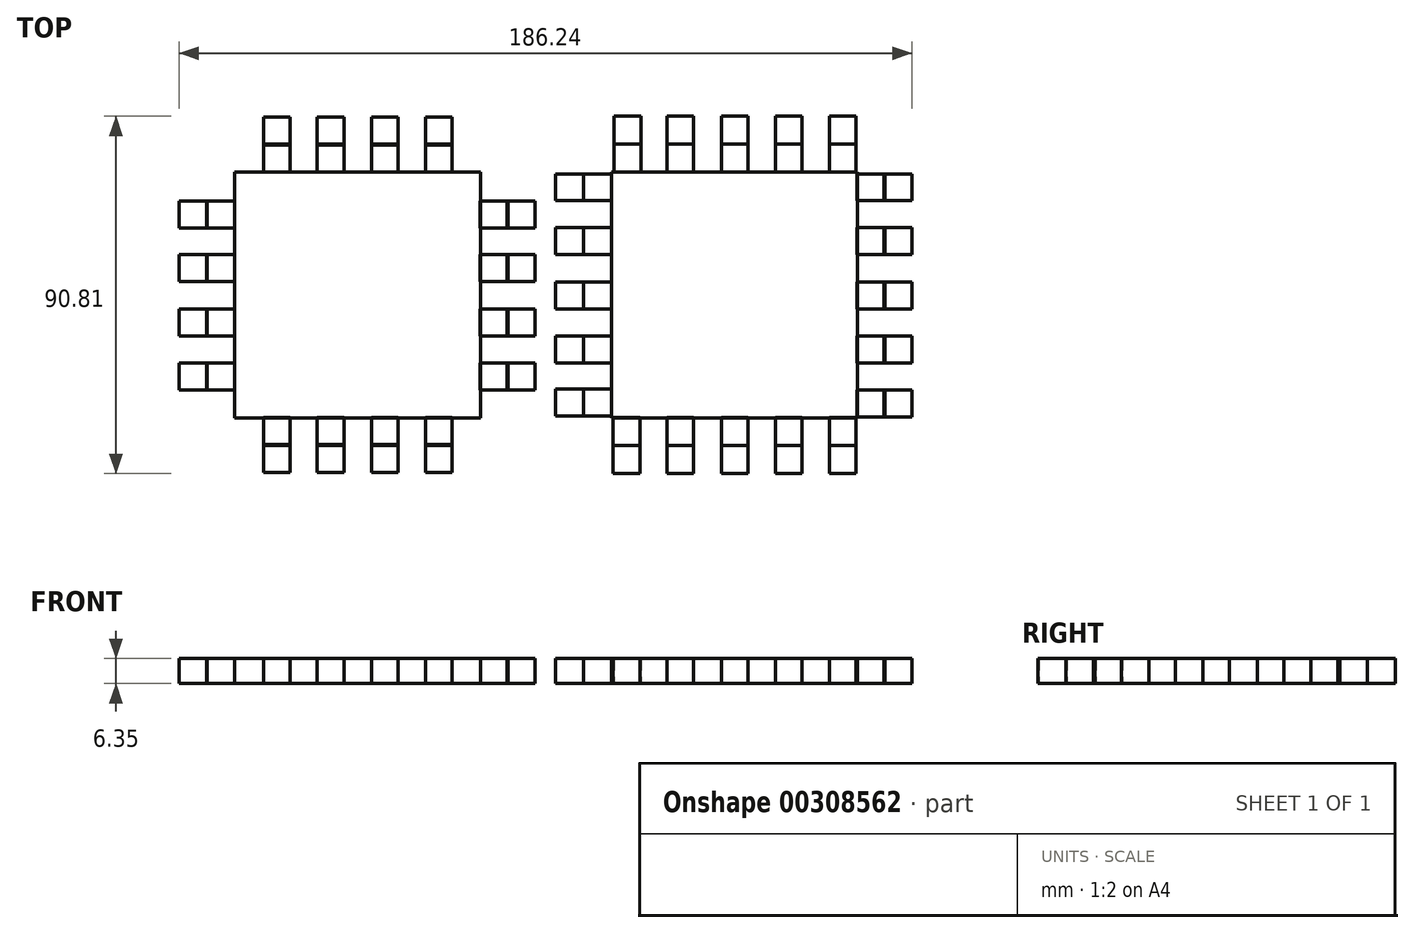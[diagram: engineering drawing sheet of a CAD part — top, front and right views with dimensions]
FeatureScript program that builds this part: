
annotation { "Feature Type Name" : "Feature", "Feature Type Description" : "" }
export const myFeature = defineFeature(function(context is Context, id is Id, definition is map)
    precondition{}
    {
        {
            var Q0;
            Q0=qCreatedBy(makeId("Top.planeOp"),FACE);
            var sketch = newSketch(context, id + "F0", { "sketchPlane" : qUnion([Q0])});
            skLineSegment(sketch, "E0.bottom", {"start": v(18.26, -15.01) * mm, "end": v(-49.21, -15.01) * mm});
            skLineSegment(sketch, "E0.top", {"start": v(18.26, 41.01) * mm, "end": v(-49.21, 41.01) * mm});
            skLineSegment(sketch, "E0.left", {"start": v(18.26, -15.01) * mm, "end": v(18.26, 41.01) * mm});
            skLineSegment(sketch, "E0.right", {"start": v(-49.21, -15.01) * mm, "end": v(-49.21, 41.01) * mm});
            skSolve(sketch);
        }
        {
            var Q0;
            Q0=qCreatedBy(makeId("Top.planeOp"),FACE);
            var sketch = newSketch(context, id + "F1", { "sketchPlane" : qUnion([Q0])});
            skLineSegment(sketch, "E1.bottom", {"start": v(-44.26, 52.77) * mm, "end": v(-37.45, 52.77) * mm});
            skLineSegment(sketch, "E1.top", {"start": v(-44.26, 45.65) * mm, "end": v(-37.45, 45.65) * mm});
            skLineSegment(sketch, "E1.left", {"start": v(-44.26, 52.77) * mm, "end": v(-44.26, 45.65) * mm});
            skLineSegment(sketch, "E1.right", {"start": v(-37.45, 52.77) * mm, "end": v(-37.45, 45.65) * mm});
            skSolve(sketch);
        }
        {
            var Q0;
            Q0=makeQuery(id+"F0.imprint","IMPRINT",FACE,{"disambiguationData":[TD([[makeQuery(id+"F0.imprint","IMPRINT",EDGE,{"derivedFrom":sQuery(id+"F0.wireOp",EDGE,"E0.bottom")}),-1.0]])]});
            var Q1;
            Q1=makeQuery(id+"F1.imprint","IMPRINT",FACE,{"disambiguationData":[TD([[makeQuery(id+"F1.imprint","IMPRINT",EDGE,{"derivedFrom":sQuery(id+"F1.wireOp",EDGE,"E1.bottom")}),-1.0]])]});
            extrude(context, id + "F2", {"entities" : qUnion([Q0, Q1]), "depth" : 6.35 * mm});
        }
        {
            var Q0;
            Q0=makeQuery(id+"F2.opExtrude","SWEPT_BODY",BODY,{"disambiguationData":[OSD([sQuery(id+"F1.wireOp",EDGE,"E1.bottom"),sQuery(id+"F1.wireOp",EDGE,"E1.top"),sQuery(id+"F1.wireOp",EDGE,"E1.left"),sQuery(id+"F1.wireOp",EDGE,"E1.right")])]});
            transform(context, id + "F3", {"entities" : qUnion([Q0]), "transformType" : TransformType.TRANSLATION_3D, "dx" : 21.08 * mm, "dy" : 0 * mm, "dz" : 0 * mm, "makeCopy" : false});
        }
        {
            var Q0;
            Q0=makeQuery(id+"F2.opExtrude","SWEPT_BODY",BODY,{"disambiguationData":[OSD([sQuery(id+"F1.wireOp",EDGE,"E1.bottom"),sQuery(id+"F1.wireOp",EDGE,"E1.top"),sQuery(id+"F1.wireOp",EDGE,"E1.left"),sQuery(id+"F1.wireOp",EDGE,"E1.right")])]});
            transform(context, id + "F4", {"entities" : qUnion([Q0]), "transformType" : TransformType.COPY});
        }
        {
            var Q0;
            Q0=makeQuery(id+"F2.opExtrude","SWEPT_BODY",BODY,{"disambiguationData":[OSD([sQuery(id+"F1.wireOp",EDGE,"E1.bottom"),sQuery(id+"F1.wireOp",EDGE,"E1.top"),sQuery(id+"F1.wireOp",EDGE,"E1.left"),sQuery(id+"F1.wireOp",EDGE,"E1.right")])]});
            transform(context, id + "F5", {"entities" : qUnion([Q0]), "transformType" : TransformType.TRANSLATION_3D, "dx" : 21.08 * mm, "dy" : 0 * mm, "dz" : 0 * mm, "makeCopy" : false});
        }
        {
            var Q0;
            Q0=makeQuery(id+"F4.opPattern","COPY",BODY,{"derivedFrom":makeQuery(id+"F2.opExtrude","SWEPT_BODY",BODY,{"disambiguationData":[OSD([sQuery(id+"F1.wireOp",EDGE,"E1.bottom"),sQuery(id+"F1.wireOp",EDGE,"E1.top"),sQuery(id+"F1.wireOp",EDGE,"E1.left"),sQuery(id+"F1.wireOp",EDGE,"E1.right")])]}),"instanceName":"1"});
            var Q1;
            Q1=makeQuery(id+"F2.opExtrude","SWEPT_BODY",BODY,{"disambiguationData":[OSD([sQuery(id+"F1.wireOp",EDGE,"E1.bottom"),sQuery(id+"F1.wireOp",EDGE,"E1.top"),sQuery(id+"F1.wireOp",EDGE,"E1.left"),sQuery(id+"F1.wireOp",EDGE,"E1.right")])]});
            transform(context, id + "F6", {"entities" : qUnion([Q0, Q1]), "transformType" : TransformType.COPY});
        }
        {
            var Q0;
            Q0=makeQuery(id+"F4.opPattern","COPY",BODY,{"derivedFrom":makeQuery(id+"F2.opExtrude","SWEPT_BODY",BODY,{"disambiguationData":[OSD([sQuery(id+"F1.wireOp",EDGE,"E1.bottom"),sQuery(id+"F1.wireOp",EDGE,"E1.top"),sQuery(id+"F1.wireOp",EDGE,"E1.left"),sQuery(id+"F1.wireOp",EDGE,"E1.right")])]}),"instanceName":"1"});
            var Q1;
            Q1=makeQuery(id+"F2.opExtrude","SWEPT_BODY",BODY,{"disambiguationData":[OSD([sQuery(id+"F1.wireOp",EDGE,"E1.bottom"),sQuery(id+"F1.wireOp",EDGE,"E1.top"),sQuery(id+"F1.wireOp",EDGE,"E1.left"),sQuery(id+"F1.wireOp",EDGE,"E1.right")])]});
            transform(context, id + "F7", {"entities" : qUnion([Q0, Q1]), "transformType" : TransformType.TRANSLATION_3D, "dx" : 9.9 * mm, "dy" : 0 * mm, "dz" : 0 * mm, "makeCopy" : false});
        }
        {
            var Q0;
            Q0=makeQuery(id+"F6.opPattern","COPY",BODY,{"derivedFrom":makeQuery(id+"F4.opPattern","COPY",BODY,{"derivedFrom":makeQuery(id+"F2.opExtrude","SWEPT_BODY",BODY,{"disambiguationData":[OSD([sQuery(id+"F1.wireOp",EDGE,"E1.bottom"),sQuery(id+"F1.wireOp",EDGE,"E1.top"),sQuery(id+"F1.wireOp",EDGE,"E1.left"),sQuery(id+"F1.wireOp",EDGE,"E1.right")])]}),"instanceName":"1"}),"instanceName":"1"});
            transform(context, id + "F8", {"entities" : qUnion([Q0]), "transformType" : TransformType.TRANSLATION_3D, "dx" : 2.54 * mm, "dy" : 0 * mm, "dz" : 0 * mm, "makeCopy" : false});
        }
        {
            var Q0;
            Q0=makeQuery(id+"F6.opPattern","COPY",BODY,{"derivedFrom":makeQuery(id+"F2.opExtrude","SWEPT_BODY",BODY,{"disambiguationData":[OSD([sQuery(id+"F1.wireOp",EDGE,"E1.bottom"),sQuery(id+"F1.wireOp",EDGE,"E1.top"),sQuery(id+"F1.wireOp",EDGE,"E1.left"),sQuery(id+"F1.wireOp",EDGE,"E1.right")])]}),"instanceName":"1"});
            transform(context, id + "F9", {"entities" : qUnion([Q0]), "transformType" : TransformType.TRANSLATION_3D, "dx" : -4.06 * mm, "dy" : 0 * mm, "dz" : 0 * mm, "makeCopy" : false});
        }
        {
            var Q0;
            Q0=makeQuery(id+"F2.opExtrude","SWEPT_BODY",BODY,{"disambiguationData":[OSD([sQuery(id+"F1.wireOp",EDGE,"E1.bottom"),sQuery(id+"F1.wireOp",EDGE,"E1.top"),sQuery(id+"F1.wireOp",EDGE,"E1.left"),sQuery(id+"F1.wireOp",EDGE,"E1.right")])]});
            transform(context, id + "F10", {"entities" : qUnion([Q0]), "transformType" : TransformType.TRANSLATION_3D, "dx" : -6.6 * mm, "dy" : 0 * mm, "dz" : 0 * mm, "makeCopy" : false});
        }
        {
            var Q0;
            Q0=makeQuery(id+"F6.opPattern","COPY",BODY,{"derivedFrom":makeQuery(id+"F2.opExtrude","SWEPT_BODY",BODY,{"disambiguationData":[OSD([sQuery(id+"F1.wireOp",EDGE,"E1.bottom"),sQuery(id+"F1.wireOp",EDGE,"E1.top"),sQuery(id+"F1.wireOp",EDGE,"E1.left"),sQuery(id+"F1.wireOp",EDGE,"E1.right")])]}),"instanceName":"1"});
            var Q1;
            Q1=makeQuery(id+"F4.opPattern","COPY",BODY,{"derivedFrom":makeQuery(id+"F2.opExtrude","SWEPT_BODY",BODY,{"disambiguationData":[OSD([sQuery(id+"F1.wireOp",EDGE,"E1.bottom"),sQuery(id+"F1.wireOp",EDGE,"E1.top"),sQuery(id+"F1.wireOp",EDGE,"E1.left"),sQuery(id+"F1.wireOp",EDGE,"E1.right")])]}),"instanceName":"1"});
            var Q2;
            Q2=makeQuery(id+"F2.opExtrude","SWEPT_BODY",BODY,{"disambiguationData":[OSD([sQuery(id+"F1.wireOp",EDGE,"E1.bottom"),sQuery(id+"F1.wireOp",EDGE,"E1.top"),sQuery(id+"F1.wireOp",EDGE,"E1.left"),sQuery(id+"F1.wireOp",EDGE,"E1.right")])]});
            var Q3;
            Q3=makeQuery(id+"F6.opPattern","COPY",BODY,{"derivedFrom":makeQuery(id+"F4.opPattern","COPY",BODY,{"derivedFrom":makeQuery(id+"F2.opExtrude","SWEPT_BODY",BODY,{"disambiguationData":[OSD([sQuery(id+"F1.wireOp",EDGE,"E1.bottom"),sQuery(id+"F1.wireOp",EDGE,"E1.top"),sQuery(id+"F1.wireOp",EDGE,"E1.left"),sQuery(id+"F1.wireOp",EDGE,"E1.right")])]}),"instanceName":"1"}),"instanceName":"1"});
            transform(context, id + "F11", {"entities" : qUnion([Q0, Q1, Q2, Q3]), "transformType" : TransformType.COPY});
        }
        {
            var Q0;
            Q0=makeQuery(id+"F11.opPattern","COPY",BODY,{"derivedFrom":makeQuery(id+"F4.opPattern","COPY",BODY,{"derivedFrom":makeQuery(id+"F2.opExtrude","SWEPT_BODY",BODY,{"disambiguationData":[OSD([sQuery(id+"F1.wireOp",EDGE,"E1.bottom"),sQuery(id+"F1.wireOp",EDGE,"E1.top"),sQuery(id+"F1.wireOp",EDGE,"E1.left"),sQuery(id+"F1.wireOp",EDGE,"E1.right")])]}),"instanceName":"1"}),"instanceName":"1"});
            var Q1;
            Q1=makeQuery(id+"F11.opPattern","COPY",BODY,{"derivedFrom":makeQuery(id+"F2.opExtrude","SWEPT_BODY",BODY,{"disambiguationData":[OSD([sQuery(id+"F1.wireOp",EDGE,"E1.bottom"),sQuery(id+"F1.wireOp",EDGE,"E1.top"),sQuery(id+"F1.wireOp",EDGE,"E1.left"),sQuery(id+"F1.wireOp",EDGE,"E1.right")])]}),"instanceName":"1"});
            var Q2;
            Q2=makeQuery(id+"F11.opPattern","COPY",BODY,{"derivedFrom":makeQuery(id+"F6.opPattern","COPY",BODY,{"derivedFrom":makeQuery(id+"F2.opExtrude","SWEPT_BODY",BODY,{"disambiguationData":[OSD([sQuery(id+"F1.wireOp",EDGE,"E1.bottom"),sQuery(id+"F1.wireOp",EDGE,"E1.top"),sQuery(id+"F1.wireOp",EDGE,"E1.left"),sQuery(id+"F1.wireOp",EDGE,"E1.right")])]}),"instanceName":"1"}),"instanceName":"1"});
            var Q3;
            Q3=makeQuery(id+"F11.opPattern","COPY",BODY,{"derivedFrom":makeQuery(id+"F6.opPattern","COPY",BODY,{"derivedFrom":makeQuery(id+"F4.opPattern","COPY",BODY,{"derivedFrom":makeQuery(id+"F2.opExtrude","SWEPT_BODY",BODY,{"disambiguationData":[OSD([sQuery(id+"F1.wireOp",EDGE,"E1.bottom"),sQuery(id+"F1.wireOp",EDGE,"E1.top"),sQuery(id+"F1.wireOp",EDGE,"E1.left"),sQuery(id+"F1.wireOp",EDGE,"E1.right")])]}),"instanceName":"1"}),"instanceName":"1"}),"instanceName":"1"});
            transform(context, id + "F12", {"entities" : qUnion([Q0, Q1, Q2, Q3]), "transformType" : TransformType.TRANSLATION_3D, "dx" : -29.46 * mm, "dy" : 0 * mm, "dz" : 0 * mm, "makeCopy" : false});
        }
        {
            var Q0;
            Q0=makeQuery(id+"F11.opPattern","COPY",BODY,{"derivedFrom":makeQuery(id+"F4.opPattern","COPY",BODY,{"derivedFrom":makeQuery(id+"F2.opExtrude","SWEPT_BODY",BODY,{"disambiguationData":[OSD([sQuery(id+"F1.wireOp",EDGE,"E1.bottom"),sQuery(id+"F1.wireOp",EDGE,"E1.top"),sQuery(id+"F1.wireOp",EDGE,"E1.left"),sQuery(id+"F1.wireOp",EDGE,"E1.right")])]}),"instanceName":"1"}),"instanceName":"1"});
            var Q1;
            Q1=makeQuery(id+"F6.opPattern","COPY",BODY,{"derivedFrom":makeQuery(id+"F2.opExtrude","SWEPT_BODY",BODY,{"disambiguationData":[OSD([sQuery(id+"F1.wireOp",EDGE,"E1.bottom"),sQuery(id+"F1.wireOp",EDGE,"E1.top"),sQuery(id+"F1.wireOp",EDGE,"E1.left"),sQuery(id+"F1.wireOp",EDGE,"E1.right")])]}),"instanceName":"1"});
            var Q2;
            Q2=makeQuery(id+"F11.opPattern","COPY",BODY,{"derivedFrom":makeQuery(id+"F2.opExtrude","SWEPT_BODY",BODY,{"disambiguationData":[OSD([sQuery(id+"F1.wireOp",EDGE,"E1.bottom"),sQuery(id+"F1.wireOp",EDGE,"E1.top"),sQuery(id+"F1.wireOp",EDGE,"E1.left"),sQuery(id+"F1.wireOp",EDGE,"E1.right")])]}),"instanceName":"1"});
            var Q3;
            Q3=makeQuery(id+"F4.opPattern","COPY",BODY,{"derivedFrom":makeQuery(id+"F2.opExtrude","SWEPT_BODY",BODY,{"disambiguationData":[OSD([sQuery(id+"F1.wireOp",EDGE,"E1.bottom"),sQuery(id+"F1.wireOp",EDGE,"E1.top"),sQuery(id+"F1.wireOp",EDGE,"E1.left"),sQuery(id+"F1.wireOp",EDGE,"E1.right")])]}),"instanceName":"1"});
            var Q4;
            Q4=makeQuery(id+"F11.opPattern","COPY",BODY,{"derivedFrom":makeQuery(id+"F6.opPattern","COPY",BODY,{"derivedFrom":makeQuery(id+"F2.opExtrude","SWEPT_BODY",BODY,{"disambiguationData":[OSD([sQuery(id+"F1.wireOp",EDGE,"E1.bottom"),sQuery(id+"F1.wireOp",EDGE,"E1.top"),sQuery(id+"F1.wireOp",EDGE,"E1.left"),sQuery(id+"F1.wireOp",EDGE,"E1.right")])]}),"instanceName":"1"}),"instanceName":"1"});
            var Q5;
            Q5=makeQuery(id+"F11.opPattern","COPY",BODY,{"derivedFrom":makeQuery(id+"F6.opPattern","COPY",BODY,{"derivedFrom":makeQuery(id+"F4.opPattern","COPY",BODY,{"derivedFrom":makeQuery(id+"F2.opExtrude","SWEPT_BODY",BODY,{"disambiguationData":[OSD([sQuery(id+"F1.wireOp",EDGE,"E1.bottom"),sQuery(id+"F1.wireOp",EDGE,"E1.top"),sQuery(id+"F1.wireOp",EDGE,"E1.left"),sQuery(id+"F1.wireOp",EDGE,"E1.right")])]}),"instanceName":"1"}),"instanceName":"1"}),"instanceName":"1"});
            var Q6;
            Q6=makeQuery(id+"F2.opExtrude","SWEPT_BODY",BODY,{"disambiguationData":[OSD([sQuery(id+"F1.wireOp",EDGE,"E1.bottom"),sQuery(id+"F1.wireOp",EDGE,"E1.top"),sQuery(id+"F1.wireOp",EDGE,"E1.left"),sQuery(id+"F1.wireOp",EDGE,"E1.right")])]});
            var Q7;
            Q7=makeQuery(id+"F6.opPattern","COPY",BODY,{"derivedFrom":makeQuery(id+"F4.opPattern","COPY",BODY,{"derivedFrom":makeQuery(id+"F2.opExtrude","SWEPT_BODY",BODY,{"disambiguationData":[OSD([sQuery(id+"F1.wireOp",EDGE,"E1.bottom"),sQuery(id+"F1.wireOp",EDGE,"E1.top"),sQuery(id+"F1.wireOp",EDGE,"E1.left"),sQuery(id+"F1.wireOp",EDGE,"E1.right")])]}),"instanceName":"1"}),"instanceName":"1"});
            transform(context, id + "F13", {"entities" : qUnion([Q0, Q1, Q2, Q3, Q4, Q5, Q6, Q7]), "transformType" : TransformType.COPY});
        }
        {
            var Q0;
            Q0=makeQuery(id+"F13.opPattern","COPY",BODY,{"derivedFrom":makeQuery(id+"F11.opPattern","COPY",BODY,{"derivedFrom":makeQuery(id+"F6.opPattern","COPY",BODY,{"derivedFrom":makeQuery(id+"F4.opPattern","COPY",BODY,{"derivedFrom":makeQuery(id+"F2.opExtrude","SWEPT_BODY",BODY,{"disambiguationData":[OSD([sQuery(id+"F1.wireOp",EDGE,"E1.bottom"),sQuery(id+"F1.wireOp",EDGE,"E1.top"),sQuery(id+"F1.wireOp",EDGE,"E1.left"),sQuery(id+"F1.wireOp",EDGE,"E1.right")])]}),"instanceName":"1"}),"instanceName":"1"}),"instanceName":"1"}),"instanceName":"1"});
            var Q1;
            Q1=makeQuery(id+"F13.opPattern","COPY",BODY,{"derivedFrom":makeQuery(id+"F6.opPattern","COPY",BODY,{"derivedFrom":makeQuery(id+"F4.opPattern","COPY",BODY,{"derivedFrom":makeQuery(id+"F2.opExtrude","SWEPT_BODY",BODY,{"disambiguationData":[OSD([sQuery(id+"F1.wireOp",EDGE,"E1.bottom"),sQuery(id+"F1.wireOp",EDGE,"E1.top"),sQuery(id+"F1.wireOp",EDGE,"E1.left"),sQuery(id+"F1.wireOp",EDGE,"E1.right")])]}),"instanceName":"1"}),"instanceName":"1"}),"instanceName":"1"});
            var Q2;
            Q2=makeQuery(id+"F13.opPattern","COPY",BODY,{"derivedFrom":makeQuery(id+"F6.opPattern","COPY",BODY,{"derivedFrom":makeQuery(id+"F2.opExtrude","SWEPT_BODY",BODY,{"disambiguationData":[OSD([sQuery(id+"F1.wireOp",EDGE,"E1.bottom"),sQuery(id+"F1.wireOp",EDGE,"E1.top"),sQuery(id+"F1.wireOp",EDGE,"E1.left"),sQuery(id+"F1.wireOp",EDGE,"E1.right")])]}),"instanceName":"1"}),"instanceName":"1"});
            var Q3;
            Q3=makeQuery(id+"F13.opPattern","COPY",BODY,{"derivedFrom":makeQuery(id+"F4.opPattern","COPY",BODY,{"derivedFrom":makeQuery(id+"F2.opExtrude","SWEPT_BODY",BODY,{"disambiguationData":[OSD([sQuery(id+"F1.wireOp",EDGE,"E1.bottom"),sQuery(id+"F1.wireOp",EDGE,"E1.top"),sQuery(id+"F1.wireOp",EDGE,"E1.left"),sQuery(id+"F1.wireOp",EDGE,"E1.right")])]}),"instanceName":"1"}),"instanceName":"1"});
            var Q4;
            Q4=makeQuery(id+"F13.opPattern","COPY",BODY,{"derivedFrom":makeQuery(id+"F2.opExtrude","SWEPT_BODY",BODY,{"disambiguationData":[OSD([sQuery(id+"F1.wireOp",EDGE,"E1.bottom"),sQuery(id+"F1.wireOp",EDGE,"E1.top"),sQuery(id+"F1.wireOp",EDGE,"E1.left"),sQuery(id+"F1.wireOp",EDGE,"E1.right")])]}),"instanceName":"1"});
            var Q5;
            Q5=makeQuery(id+"F13.opPattern","COPY",BODY,{"derivedFrom":makeQuery(id+"F11.opPattern","COPY",BODY,{"derivedFrom":makeQuery(id+"F6.opPattern","COPY",BODY,{"derivedFrom":makeQuery(id+"F2.opExtrude","SWEPT_BODY",BODY,{"disambiguationData":[OSD([sQuery(id+"F1.wireOp",EDGE,"E1.bottom"),sQuery(id+"F1.wireOp",EDGE,"E1.top"),sQuery(id+"F1.wireOp",EDGE,"E1.left"),sQuery(id+"F1.wireOp",EDGE,"E1.right")])]}),"instanceName":"1"}),"instanceName":"1"}),"instanceName":"1"});
            var Q6;
            Q6=makeQuery(id+"F13.opPattern","COPY",BODY,{"derivedFrom":makeQuery(id+"F11.opPattern","COPY",BODY,{"derivedFrom":makeQuery(id+"F4.opPattern","COPY",BODY,{"derivedFrom":makeQuery(id+"F2.opExtrude","SWEPT_BODY",BODY,{"disambiguationData":[OSD([sQuery(id+"F1.wireOp",EDGE,"E1.bottom"),sQuery(id+"F1.wireOp",EDGE,"E1.top"),sQuery(id+"F1.wireOp",EDGE,"E1.left"),sQuery(id+"F1.wireOp",EDGE,"E1.right")])]}),"instanceName":"1"}),"instanceName":"1"}),"instanceName":"1"});
            var Q7;
            Q7=makeQuery(id+"F13.opPattern","COPY",BODY,{"derivedFrom":makeQuery(id+"F11.opPattern","COPY",BODY,{"derivedFrom":makeQuery(id+"F2.opExtrude","SWEPT_BODY",BODY,{"disambiguationData":[OSD([sQuery(id+"F1.wireOp",EDGE,"E1.bottom"),sQuery(id+"F1.wireOp",EDGE,"E1.top"),sQuery(id+"F1.wireOp",EDGE,"E1.left"),sQuery(id+"F1.wireOp",EDGE,"E1.right")])]}),"instanceName":"1"}),"instanceName":"1"});
            transform(context, id + "F14", {"entities" : qUnion([Q0, Q1, Q2, Q3, Q4, Q5, Q6, Q7]), "transformType" : TransformType.TRANSLATION_3D, "dx" : 58.17 * mm, "dy" : 0 * mm, "dz" : 0 * mm, "makeCopy" : false});
        }
        {
            var Q0;
            Q0=makeQuery(id+"F13.opPattern","COPY",BODY,{"derivedFrom":makeQuery(id+"F11.opPattern","COPY",BODY,{"derivedFrom":makeQuery(id+"F6.opPattern","COPY",BODY,{"derivedFrom":makeQuery(id+"F4.opPattern","COPY",BODY,{"derivedFrom":makeQuery(id+"F2.opExtrude","SWEPT_BODY",BODY,{"disambiguationData":[OSD([sQuery(id+"F1.wireOp",EDGE,"E1.bottom"),sQuery(id+"F1.wireOp",EDGE,"E1.top"),sQuery(id+"F1.wireOp",EDGE,"E1.left"),sQuery(id+"F1.wireOp",EDGE,"E1.right")])]}),"instanceName":"1"}),"instanceName":"1"}),"instanceName":"1"}),"instanceName":"1"});
            var Q1;
            Q1=makeQuery(id+"F13.opPattern","COPY",BODY,{"derivedFrom":makeQuery(id+"F6.opPattern","COPY",BODY,{"derivedFrom":makeQuery(id+"F4.opPattern","COPY",BODY,{"derivedFrom":makeQuery(id+"F2.opExtrude","SWEPT_BODY",BODY,{"disambiguationData":[OSD([sQuery(id+"F1.wireOp",EDGE,"E1.bottom"),sQuery(id+"F1.wireOp",EDGE,"E1.top"),sQuery(id+"F1.wireOp",EDGE,"E1.left"),sQuery(id+"F1.wireOp",EDGE,"E1.right")])]}),"instanceName":"1"}),"instanceName":"1"}),"instanceName":"1"});
            var Q2;
            Q2=makeQuery(id+"F13.opPattern","COPY",BODY,{"derivedFrom":makeQuery(id+"F6.opPattern","COPY",BODY,{"derivedFrom":makeQuery(id+"F2.opExtrude","SWEPT_BODY",BODY,{"disambiguationData":[OSD([sQuery(id+"F1.wireOp",EDGE,"E1.bottom"),sQuery(id+"F1.wireOp",EDGE,"E1.top"),sQuery(id+"F1.wireOp",EDGE,"E1.left"),sQuery(id+"F1.wireOp",EDGE,"E1.right")])]}),"instanceName":"1"}),"instanceName":"1"});
            var Q3;
            Q3=makeQuery(id+"F11.opPattern","COPY",BODY,{"derivedFrom":makeQuery(id+"F4.opPattern","COPY",BODY,{"derivedFrom":makeQuery(id+"F2.opExtrude","SWEPT_BODY",BODY,{"disambiguationData":[OSD([sQuery(id+"F1.wireOp",EDGE,"E1.bottom"),sQuery(id+"F1.wireOp",EDGE,"E1.top"),sQuery(id+"F1.wireOp",EDGE,"E1.left"),sQuery(id+"F1.wireOp",EDGE,"E1.right")])]}),"instanceName":"1"}),"instanceName":"1"});
            var Q4;
            Q4=makeQuery(id+"F6.opPattern","COPY",BODY,{"derivedFrom":makeQuery(id+"F2.opExtrude","SWEPT_BODY",BODY,{"disambiguationData":[OSD([sQuery(id+"F1.wireOp",EDGE,"E1.bottom"),sQuery(id+"F1.wireOp",EDGE,"E1.top"),sQuery(id+"F1.wireOp",EDGE,"E1.left"),sQuery(id+"F1.wireOp",EDGE,"E1.right")])]}),"instanceName":"1"});
            var Q5;
            Q5=makeQuery(id+"F13.opPattern","COPY",BODY,{"derivedFrom":makeQuery(id+"F4.opPattern","COPY",BODY,{"derivedFrom":makeQuery(id+"F2.opExtrude","SWEPT_BODY",BODY,{"disambiguationData":[OSD([sQuery(id+"F1.wireOp",EDGE,"E1.bottom"),sQuery(id+"F1.wireOp",EDGE,"E1.top"),sQuery(id+"F1.wireOp",EDGE,"E1.left"),sQuery(id+"F1.wireOp",EDGE,"E1.right")])]}),"instanceName":"1"}),"instanceName":"1"});
            var Q6;
            Q6=makeQuery(id+"F13.opPattern","COPY",BODY,{"derivedFrom":makeQuery(id+"F2.opExtrude","SWEPT_BODY",BODY,{"disambiguationData":[OSD([sQuery(id+"F1.wireOp",EDGE,"E1.bottom"),sQuery(id+"F1.wireOp",EDGE,"E1.top"),sQuery(id+"F1.wireOp",EDGE,"E1.left"),sQuery(id+"F1.wireOp",EDGE,"E1.right")])]}),"instanceName":"1"});
            var Q7;
            Q7=makeQuery(id+"F11.opPattern","COPY",BODY,{"derivedFrom":makeQuery(id+"F2.opExtrude","SWEPT_BODY",BODY,{"disambiguationData":[OSD([sQuery(id+"F1.wireOp",EDGE,"E1.bottom"),sQuery(id+"F1.wireOp",EDGE,"E1.top"),sQuery(id+"F1.wireOp",EDGE,"E1.left"),sQuery(id+"F1.wireOp",EDGE,"E1.right")])]}),"instanceName":"1"});
            var Q8;
            Q8=makeQuery(id+"F4.opPattern","COPY",BODY,{"derivedFrom":makeQuery(id+"F2.opExtrude","SWEPT_BODY",BODY,{"disambiguationData":[OSD([sQuery(id+"F1.wireOp",EDGE,"E1.bottom"),sQuery(id+"F1.wireOp",EDGE,"E1.top"),sQuery(id+"F1.wireOp",EDGE,"E1.left"),sQuery(id+"F1.wireOp",EDGE,"E1.right")])]}),"instanceName":"1"});
            var Q9;
            Q9=makeQuery(id+"F11.opPattern","COPY",BODY,{"derivedFrom":makeQuery(id+"F6.opPattern","COPY",BODY,{"derivedFrom":makeQuery(id+"F2.opExtrude","SWEPT_BODY",BODY,{"disambiguationData":[OSD([sQuery(id+"F1.wireOp",EDGE,"E1.bottom"),sQuery(id+"F1.wireOp",EDGE,"E1.top"),sQuery(id+"F1.wireOp",EDGE,"E1.left"),sQuery(id+"F1.wireOp",EDGE,"E1.right")])]}),"instanceName":"1"}),"instanceName":"1"});
            var Q10;
            Q10=makeQuery(id+"F11.opPattern","COPY",BODY,{"derivedFrom":makeQuery(id+"F6.opPattern","COPY",BODY,{"derivedFrom":makeQuery(id+"F4.opPattern","COPY",BODY,{"derivedFrom":makeQuery(id+"F2.opExtrude","SWEPT_BODY",BODY,{"disambiguationData":[OSD([sQuery(id+"F1.wireOp",EDGE,"E1.bottom"),sQuery(id+"F1.wireOp",EDGE,"E1.top"),sQuery(id+"F1.wireOp",EDGE,"E1.left"),sQuery(id+"F1.wireOp",EDGE,"E1.right")])]}),"instanceName":"1"}),"instanceName":"1"}),"instanceName":"1"});
            var Q11;
            Q11=makeQuery(id+"F13.opPattern","COPY",BODY,{"derivedFrom":makeQuery(id+"F11.opPattern","COPY",BODY,{"derivedFrom":makeQuery(id+"F6.opPattern","COPY",BODY,{"derivedFrom":makeQuery(id+"F2.opExtrude","SWEPT_BODY",BODY,{"disambiguationData":[OSD([sQuery(id+"F1.wireOp",EDGE,"E1.bottom"),sQuery(id+"F1.wireOp",EDGE,"E1.top"),sQuery(id+"F1.wireOp",EDGE,"E1.left"),sQuery(id+"F1.wireOp",EDGE,"E1.right")])]}),"instanceName":"1"}),"instanceName":"1"}),"instanceName":"1"});
            var Q12;
            Q12=makeQuery(id+"F13.opPattern","COPY",BODY,{"derivedFrom":makeQuery(id+"F11.opPattern","COPY",BODY,{"derivedFrom":makeQuery(id+"F4.opPattern","COPY",BODY,{"derivedFrom":makeQuery(id+"F2.opExtrude","SWEPT_BODY",BODY,{"disambiguationData":[OSD([sQuery(id+"F1.wireOp",EDGE,"E1.bottom"),sQuery(id+"F1.wireOp",EDGE,"E1.top"),sQuery(id+"F1.wireOp",EDGE,"E1.left"),sQuery(id+"F1.wireOp",EDGE,"E1.right")])]}),"instanceName":"1"}),"instanceName":"1"}),"instanceName":"1"});
            var Q13;
            Q13=makeQuery(id+"F2.opExtrude","SWEPT_BODY",BODY,{"disambiguationData":[OSD([sQuery(id+"F1.wireOp",EDGE,"E1.bottom"),sQuery(id+"F1.wireOp",EDGE,"E1.top"),sQuery(id+"F1.wireOp",EDGE,"E1.left"),sQuery(id+"F1.wireOp",EDGE,"E1.right")])]});
            var Q14;
            Q14=makeQuery(id+"F13.opPattern","COPY",BODY,{"derivedFrom":makeQuery(id+"F11.opPattern","COPY",BODY,{"derivedFrom":makeQuery(id+"F2.opExtrude","SWEPT_BODY",BODY,{"disambiguationData":[OSD([sQuery(id+"F1.wireOp",EDGE,"E1.bottom"),sQuery(id+"F1.wireOp",EDGE,"E1.top"),sQuery(id+"F1.wireOp",EDGE,"E1.left"),sQuery(id+"F1.wireOp",EDGE,"E1.right")])]}),"instanceName":"1"}),"instanceName":"1"});
            var Q15;
            Q15=makeQuery(id+"F6.opPattern","COPY",BODY,{"derivedFrom":makeQuery(id+"F4.opPattern","COPY",BODY,{"derivedFrom":makeQuery(id+"F2.opExtrude","SWEPT_BODY",BODY,{"disambiguationData":[OSD([sQuery(id+"F1.wireOp",EDGE,"E1.bottom"),sQuery(id+"F1.wireOp",EDGE,"E1.top"),sQuery(id+"F1.wireOp",EDGE,"E1.left"),sQuery(id+"F1.wireOp",EDGE,"E1.right")])]}),"instanceName":"1"}),"instanceName":"1"});
            transform(context, id + "F15", {"entities" : qUnion([Q0, Q1, Q2, Q3, Q4, Q5, Q6, Q7, Q8, Q9, Q10, Q11, Q12, Q13, Q14, Q15]), "transformType" : TransformType.COPY});
        }
        {
            var Q0;
            Q0=makeQuery(id+"F15.opPattern","COPY",BODY,{"derivedFrom":makeQuery(id+"F11.opPattern","COPY",BODY,{"derivedFrom":makeQuery(id+"F2.opExtrude","SWEPT_BODY",BODY,{"disambiguationData":[OSD([sQuery(id+"F1.wireOp",EDGE,"E1.bottom"),sQuery(id+"F1.wireOp",EDGE,"E1.top"),sQuery(id+"F1.wireOp",EDGE,"E1.left"),sQuery(id+"F1.wireOp",EDGE,"E1.right")])]}),"instanceName":"1"}),"instanceName":"1"});
            var Q1;
            Q1=makeQuery(id+"F15.opPattern","COPY",BODY,{"derivedFrom":makeQuery(id+"F11.opPattern","COPY",BODY,{"derivedFrom":makeQuery(id+"F6.opPattern","COPY",BODY,{"derivedFrom":makeQuery(id+"F2.opExtrude","SWEPT_BODY",BODY,{"disambiguationData":[OSD([sQuery(id+"F1.wireOp",EDGE,"E1.bottom"),sQuery(id+"F1.wireOp",EDGE,"E1.top"),sQuery(id+"F1.wireOp",EDGE,"E1.left"),sQuery(id+"F1.wireOp",EDGE,"E1.right")])]}),"instanceName":"1"}),"instanceName":"1"}),"instanceName":"1"});
            var Q2;
            Q2=makeQuery(id+"F15.opPattern","COPY",BODY,{"derivedFrom":makeQuery(id+"F11.opPattern","COPY",BODY,{"derivedFrom":makeQuery(id+"F4.opPattern","COPY",BODY,{"derivedFrom":makeQuery(id+"F2.opExtrude","SWEPT_BODY",BODY,{"disambiguationData":[OSD([sQuery(id+"F1.wireOp",EDGE,"E1.bottom"),sQuery(id+"F1.wireOp",EDGE,"E1.top"),sQuery(id+"F1.wireOp",EDGE,"E1.left"),sQuery(id+"F1.wireOp",EDGE,"E1.right")])]}),"instanceName":"1"}),"instanceName":"1"}),"instanceName":"1"});
            var Q3;
            Q3=makeQuery(id+"F15.opPattern","COPY",BODY,{"derivedFrom":makeQuery(id+"F6.opPattern","COPY",BODY,{"derivedFrom":makeQuery(id+"F4.opPattern","COPY",BODY,{"derivedFrom":makeQuery(id+"F2.opExtrude","SWEPT_BODY",BODY,{"disambiguationData":[OSD([sQuery(id+"F1.wireOp",EDGE,"E1.bottom"),sQuery(id+"F1.wireOp",EDGE,"E1.top"),sQuery(id+"F1.wireOp",EDGE,"E1.left"),sQuery(id+"F1.wireOp",EDGE,"E1.right")])]}),"instanceName":"1"}),"instanceName":"1"}),"instanceName":"1"});
            var Q4;
            Q4=makeQuery(id+"F15.opPattern","COPY",BODY,{"derivedFrom":makeQuery(id+"F6.opPattern","COPY",BODY,{"derivedFrom":makeQuery(id+"F2.opExtrude","SWEPT_BODY",BODY,{"disambiguationData":[OSD([sQuery(id+"F1.wireOp",EDGE,"E1.bottom"),sQuery(id+"F1.wireOp",EDGE,"E1.top"),sQuery(id+"F1.wireOp",EDGE,"E1.left"),sQuery(id+"F1.wireOp",EDGE,"E1.right")])]}),"instanceName":"1"}),"instanceName":"1"});
            var Q5;
            Q5=makeQuery(id+"F15.opPattern","COPY",BODY,{"derivedFrom":makeQuery(id+"F4.opPattern","COPY",BODY,{"derivedFrom":makeQuery(id+"F2.opExtrude","SWEPT_BODY",BODY,{"disambiguationData":[OSD([sQuery(id+"F1.wireOp",EDGE,"E1.bottom"),sQuery(id+"F1.wireOp",EDGE,"E1.top"),sQuery(id+"F1.wireOp",EDGE,"E1.left"),sQuery(id+"F1.wireOp",EDGE,"E1.right")])]}),"instanceName":"1"}),"instanceName":"1"});
            var Q6;
            Q6=makeQuery(id+"F15.opPattern","COPY",BODY,{"derivedFrom":makeQuery(id+"F2.opExtrude","SWEPT_BODY",BODY,{"disambiguationData":[OSD([sQuery(id+"F1.wireOp",EDGE,"E1.bottom"),sQuery(id+"F1.wireOp",EDGE,"E1.top"),sQuery(id+"F1.wireOp",EDGE,"E1.left"),sQuery(id+"F1.wireOp",EDGE,"E1.right")])]}),"instanceName":"1"});
            var Q7;
            Q7=makeQuery(id+"F15.opPattern","COPY",BODY,{"derivedFrom":makeQuery(id+"F13.opPattern","COPY",BODY,{"derivedFrom":makeQuery(id+"F11.opPattern","COPY",BODY,{"derivedFrom":makeQuery(id+"F4.opPattern","COPY",BODY,{"derivedFrom":makeQuery(id+"F2.opExtrude","SWEPT_BODY",BODY,{"disambiguationData":[OSD([sQuery(id+"F1.wireOp",EDGE,"E1.bottom"),sQuery(id+"F1.wireOp",EDGE,"E1.top"),sQuery(id+"F1.wireOp",EDGE,"E1.left"),sQuery(id+"F1.wireOp",EDGE,"E1.right")])]}),"instanceName":"1"}),"instanceName":"1"}),"instanceName":"1"}),"instanceName":"1"});
            var Q8;
            Q8=makeQuery(id+"F15.opPattern","COPY",BODY,{"derivedFrom":makeQuery(id+"F13.opPattern","COPY",BODY,{"derivedFrom":makeQuery(id+"F11.opPattern","COPY",BODY,{"derivedFrom":makeQuery(id+"F2.opExtrude","SWEPT_BODY",BODY,{"disambiguationData":[OSD([sQuery(id+"F1.wireOp",EDGE,"E1.bottom"),sQuery(id+"F1.wireOp",EDGE,"E1.top"),sQuery(id+"F1.wireOp",EDGE,"E1.left"),sQuery(id+"F1.wireOp",EDGE,"E1.right")])]}),"instanceName":"1"}),"instanceName":"1"}),"instanceName":"1"});
            var Q9;
            Q9=makeQuery(id+"F15.opPattern","COPY",BODY,{"derivedFrom":makeQuery(id+"F13.opPattern","COPY",BODY,{"derivedFrom":makeQuery(id+"F6.opPattern","COPY",BODY,{"derivedFrom":makeQuery(id+"F4.opPattern","COPY",BODY,{"derivedFrom":makeQuery(id+"F2.opExtrude","SWEPT_BODY",BODY,{"disambiguationData":[OSD([sQuery(id+"F1.wireOp",EDGE,"E1.bottom"),sQuery(id+"F1.wireOp",EDGE,"E1.top"),sQuery(id+"F1.wireOp",EDGE,"E1.left"),sQuery(id+"F1.wireOp",EDGE,"E1.right")])]}),"instanceName":"1"}),"instanceName":"1"}),"instanceName":"1"}),"instanceName":"1"});
            var Q10;
            Q10=makeQuery(id+"F15.opPattern","COPY",BODY,{"derivedFrom":makeQuery(id+"F13.opPattern","COPY",BODY,{"derivedFrom":makeQuery(id+"F6.opPattern","COPY",BODY,{"derivedFrom":makeQuery(id+"F2.opExtrude","SWEPT_BODY",BODY,{"disambiguationData":[OSD([sQuery(id+"F1.wireOp",EDGE,"E1.bottom"),sQuery(id+"F1.wireOp",EDGE,"E1.top"),sQuery(id+"F1.wireOp",EDGE,"E1.left"),sQuery(id+"F1.wireOp",EDGE,"E1.right")])]}),"instanceName":"1"}),"instanceName":"1"}),"instanceName":"1"});
            var Q11;
            Q11=makeQuery(id+"F15.opPattern","COPY",BODY,{"derivedFrom":makeQuery(id+"F13.opPattern","COPY",BODY,{"derivedFrom":makeQuery(id+"F4.opPattern","COPY",BODY,{"derivedFrom":makeQuery(id+"F2.opExtrude","SWEPT_BODY",BODY,{"disambiguationData":[OSD([sQuery(id+"F1.wireOp",EDGE,"E1.bottom"),sQuery(id+"F1.wireOp",EDGE,"E1.top"),sQuery(id+"F1.wireOp",EDGE,"E1.left"),sQuery(id+"F1.wireOp",EDGE,"E1.right")])]}),"instanceName":"1"}),"instanceName":"1"}),"instanceName":"1"});
            var Q12;
            Q12=makeQuery(id+"F15.opPattern","COPY",BODY,{"derivedFrom":makeQuery(id+"F13.opPattern","COPY",BODY,{"derivedFrom":makeQuery(id+"F2.opExtrude","SWEPT_BODY",BODY,{"disambiguationData":[OSD([sQuery(id+"F1.wireOp",EDGE,"E1.bottom"),sQuery(id+"F1.wireOp",EDGE,"E1.top"),sQuery(id+"F1.wireOp",EDGE,"E1.left"),sQuery(id+"F1.wireOp",EDGE,"E1.right")])]}),"instanceName":"1"}),"instanceName":"1"});
            var Q13;
            Q13=makeQuery(id+"F15.opPattern","COPY",BODY,{"derivedFrom":makeQuery(id+"F11.opPattern","COPY",BODY,{"derivedFrom":makeQuery(id+"F6.opPattern","COPY",BODY,{"derivedFrom":makeQuery(id+"F4.opPattern","COPY",BODY,{"derivedFrom":makeQuery(id+"F2.opExtrude","SWEPT_BODY",BODY,{"disambiguationData":[OSD([sQuery(id+"F1.wireOp",EDGE,"E1.bottom"),sQuery(id+"F1.wireOp",EDGE,"E1.top"),sQuery(id+"F1.wireOp",EDGE,"E1.left"),sQuery(id+"F1.wireOp",EDGE,"E1.right")])]}),"instanceName":"1"}),"instanceName":"1"}),"instanceName":"1"}),"instanceName":"1"});
            var Q14;
            Q14=makeQuery(id+"F15.opPattern","COPY",BODY,{"derivedFrom":makeQuery(id+"F13.opPattern","COPY",BODY,{"derivedFrom":makeQuery(id+"F11.opPattern","COPY",BODY,{"derivedFrom":makeQuery(id+"F6.opPattern","COPY",BODY,{"derivedFrom":makeQuery(id+"F2.opExtrude","SWEPT_BODY",BODY,{"disambiguationData":[OSD([sQuery(id+"F1.wireOp",EDGE,"E1.bottom"),sQuery(id+"F1.wireOp",EDGE,"E1.top"),sQuery(id+"F1.wireOp",EDGE,"E1.left"),sQuery(id+"F1.wireOp",EDGE,"E1.right")])]}),"instanceName":"1"}),"instanceName":"1"}),"instanceName":"1"}),"instanceName":"1"});
            var Q15;
            Q15=makeQuery(id+"F15.opPattern","COPY",BODY,{"derivedFrom":makeQuery(id+"F13.opPattern","COPY",BODY,{"derivedFrom":makeQuery(id+"F11.opPattern","COPY",BODY,{"derivedFrom":makeQuery(id+"F6.opPattern","COPY",BODY,{"derivedFrom":makeQuery(id+"F4.opPattern","COPY",BODY,{"derivedFrom":makeQuery(id+"F2.opExtrude","SWEPT_BODY",BODY,{"disambiguationData":[OSD([sQuery(id+"F1.wireOp",EDGE,"E1.bottom"),sQuery(id+"F1.wireOp",EDGE,"E1.top"),sQuery(id+"F1.wireOp",EDGE,"E1.left"),sQuery(id+"F1.wireOp",EDGE,"E1.right")])]}),"instanceName":"1"}),"instanceName":"1"}),"instanceName":"1"}),"instanceName":"1"}),"instanceName":"1"});
            transform(context, id + "F16", {"entities" : qUnion([Q0, Q1, Q2, Q3, Q4, Q5, Q6, Q7, Q8, Q9, Q10, Q11, Q12, Q13, Q14, Q15]), "transformType" : TransformType.TRANSLATION_3D, "dx" : 0 * mm, "dy" : 0 * mm, "dz" : 0 * mm, "makeCopy" : false});
        }
        {
            var Q0;
            Q0=makeQuery(id+"F15.opPattern","COPY",BODY,{"derivedFrom":makeQuery(id+"F11.opPattern","COPY",BODY,{"derivedFrom":makeQuery(id+"F2.opExtrude","SWEPT_BODY",BODY,{"disambiguationData":[OSD([sQuery(id+"F1.wireOp",EDGE,"E1.bottom"),sQuery(id+"F1.wireOp",EDGE,"E1.top"),sQuery(id+"F1.wireOp",EDGE,"E1.left"),sQuery(id+"F1.wireOp",EDGE,"E1.right")])]}),"instanceName":"1"}),"instanceName":"1"});
            var Q1;
            Q1=makeQuery(id+"F15.opPattern","COPY",BODY,{"derivedFrom":makeQuery(id+"F11.opPattern","COPY",BODY,{"derivedFrom":makeQuery(id+"F6.opPattern","COPY",BODY,{"derivedFrom":makeQuery(id+"F2.opExtrude","SWEPT_BODY",BODY,{"disambiguationData":[OSD([sQuery(id+"F1.wireOp",EDGE,"E1.bottom"),sQuery(id+"F1.wireOp",EDGE,"E1.top"),sQuery(id+"F1.wireOp",EDGE,"E1.left"),sQuery(id+"F1.wireOp",EDGE,"E1.right")])]}),"instanceName":"1"}),"instanceName":"1"}),"instanceName":"1"});
            var Q2;
            Q2=makeQuery(id+"F15.opPattern","COPY",BODY,{"derivedFrom":makeQuery(id+"F11.opPattern","COPY",BODY,{"derivedFrom":makeQuery(id+"F4.opPattern","COPY",BODY,{"derivedFrom":makeQuery(id+"F2.opExtrude","SWEPT_BODY",BODY,{"disambiguationData":[OSD([sQuery(id+"F1.wireOp",EDGE,"E1.bottom"),sQuery(id+"F1.wireOp",EDGE,"E1.top"),sQuery(id+"F1.wireOp",EDGE,"E1.left"),sQuery(id+"F1.wireOp",EDGE,"E1.right")])]}),"instanceName":"1"}),"instanceName":"1"}),"instanceName":"1"});
            var Q3;
            Q3=makeQuery(id+"F15.opPattern","COPY",BODY,{"derivedFrom":makeQuery(id+"F6.opPattern","COPY",BODY,{"derivedFrom":makeQuery(id+"F4.opPattern","COPY",BODY,{"derivedFrom":makeQuery(id+"F2.opExtrude","SWEPT_BODY",BODY,{"disambiguationData":[OSD([sQuery(id+"F1.wireOp",EDGE,"E1.bottom"),sQuery(id+"F1.wireOp",EDGE,"E1.top"),sQuery(id+"F1.wireOp",EDGE,"E1.left"),sQuery(id+"F1.wireOp",EDGE,"E1.right")])]}),"instanceName":"1"}),"instanceName":"1"}),"instanceName":"1"});
            var Q4;
            Q4=makeQuery(id+"F15.opPattern","COPY",BODY,{"derivedFrom":makeQuery(id+"F6.opPattern","COPY",BODY,{"derivedFrom":makeQuery(id+"F2.opExtrude","SWEPT_BODY",BODY,{"disambiguationData":[OSD([sQuery(id+"F1.wireOp",EDGE,"E1.bottom"),sQuery(id+"F1.wireOp",EDGE,"E1.top"),sQuery(id+"F1.wireOp",EDGE,"E1.left"),sQuery(id+"F1.wireOp",EDGE,"E1.right")])]}),"instanceName":"1"}),"instanceName":"1"});
            var Q5;
            Q5=makeQuery(id+"F15.opPattern","COPY",BODY,{"derivedFrom":makeQuery(id+"F4.opPattern","COPY",BODY,{"derivedFrom":makeQuery(id+"F2.opExtrude","SWEPT_BODY",BODY,{"disambiguationData":[OSD([sQuery(id+"F1.wireOp",EDGE,"E1.bottom"),sQuery(id+"F1.wireOp",EDGE,"E1.top"),sQuery(id+"F1.wireOp",EDGE,"E1.left"),sQuery(id+"F1.wireOp",EDGE,"E1.right")])]}),"instanceName":"1"}),"instanceName":"1"});
            var Q6;
            Q6=makeQuery(id+"F15.opPattern","COPY",BODY,{"derivedFrom":makeQuery(id+"F2.opExtrude","SWEPT_BODY",BODY,{"disambiguationData":[OSD([sQuery(id+"F1.wireOp",EDGE,"E1.bottom"),sQuery(id+"F1.wireOp",EDGE,"E1.top"),sQuery(id+"F1.wireOp",EDGE,"E1.left"),sQuery(id+"F1.wireOp",EDGE,"E1.right")])]}),"instanceName":"1"});
            var Q7;
            Q7=makeQuery(id+"F15.opPattern","COPY",BODY,{"derivedFrom":makeQuery(id+"F13.opPattern","COPY",BODY,{"derivedFrom":makeQuery(id+"F11.opPattern","COPY",BODY,{"derivedFrom":makeQuery(id+"F4.opPattern","COPY",BODY,{"derivedFrom":makeQuery(id+"F2.opExtrude","SWEPT_BODY",BODY,{"disambiguationData":[OSD([sQuery(id+"F1.wireOp",EDGE,"E1.bottom"),sQuery(id+"F1.wireOp",EDGE,"E1.top"),sQuery(id+"F1.wireOp",EDGE,"E1.left"),sQuery(id+"F1.wireOp",EDGE,"E1.right")])]}),"instanceName":"1"}),"instanceName":"1"}),"instanceName":"1"}),"instanceName":"1"});
            var Q8;
            Q8=makeQuery(id+"F15.opPattern","COPY",BODY,{"derivedFrom":makeQuery(id+"F13.opPattern","COPY",BODY,{"derivedFrom":makeQuery(id+"F11.opPattern","COPY",BODY,{"derivedFrom":makeQuery(id+"F2.opExtrude","SWEPT_BODY",BODY,{"disambiguationData":[OSD([sQuery(id+"F1.wireOp",EDGE,"E1.bottom"),sQuery(id+"F1.wireOp",EDGE,"E1.top"),sQuery(id+"F1.wireOp",EDGE,"E1.left"),sQuery(id+"F1.wireOp",EDGE,"E1.right")])]}),"instanceName":"1"}),"instanceName":"1"}),"instanceName":"1"});
            var Q9;
            Q9=makeQuery(id+"F15.opPattern","COPY",BODY,{"derivedFrom":makeQuery(id+"F13.opPattern","COPY",BODY,{"derivedFrom":makeQuery(id+"F6.opPattern","COPY",BODY,{"derivedFrom":makeQuery(id+"F4.opPattern","COPY",BODY,{"derivedFrom":makeQuery(id+"F2.opExtrude","SWEPT_BODY",BODY,{"disambiguationData":[OSD([sQuery(id+"F1.wireOp",EDGE,"E1.bottom"),sQuery(id+"F1.wireOp",EDGE,"E1.top"),sQuery(id+"F1.wireOp",EDGE,"E1.left"),sQuery(id+"F1.wireOp",EDGE,"E1.right")])]}),"instanceName":"1"}),"instanceName":"1"}),"instanceName":"1"}),"instanceName":"1"});
            var Q10;
            Q10=makeQuery(id+"F15.opPattern","COPY",BODY,{"derivedFrom":makeQuery(id+"F13.opPattern","COPY",BODY,{"derivedFrom":makeQuery(id+"F6.opPattern","COPY",BODY,{"derivedFrom":makeQuery(id+"F2.opExtrude","SWEPT_BODY",BODY,{"disambiguationData":[OSD([sQuery(id+"F1.wireOp",EDGE,"E1.bottom"),sQuery(id+"F1.wireOp",EDGE,"E1.top"),sQuery(id+"F1.wireOp",EDGE,"E1.left"),sQuery(id+"F1.wireOp",EDGE,"E1.right")])]}),"instanceName":"1"}),"instanceName":"1"}),"instanceName":"1"});
            var Q11;
            Q11=makeQuery(id+"F15.opPattern","COPY",BODY,{"derivedFrom":makeQuery(id+"F13.opPattern","COPY",BODY,{"derivedFrom":makeQuery(id+"F4.opPattern","COPY",BODY,{"derivedFrom":makeQuery(id+"F2.opExtrude","SWEPT_BODY",BODY,{"disambiguationData":[OSD([sQuery(id+"F1.wireOp",EDGE,"E1.bottom"),sQuery(id+"F1.wireOp",EDGE,"E1.top"),sQuery(id+"F1.wireOp",EDGE,"E1.left"),sQuery(id+"F1.wireOp",EDGE,"E1.right")])]}),"instanceName":"1"}),"instanceName":"1"}),"instanceName":"1"});
            var Q12;
            Q12=makeQuery(id+"F15.opPattern","COPY",BODY,{"derivedFrom":makeQuery(id+"F13.opPattern","COPY",BODY,{"derivedFrom":makeQuery(id+"F2.opExtrude","SWEPT_BODY",BODY,{"disambiguationData":[OSD([sQuery(id+"F1.wireOp",EDGE,"E1.bottom"),sQuery(id+"F1.wireOp",EDGE,"E1.top"),sQuery(id+"F1.wireOp",EDGE,"E1.left"),sQuery(id+"F1.wireOp",EDGE,"E1.right")])]}),"instanceName":"1"}),"instanceName":"1"});
            var Q13;
            Q13=makeQuery(id+"F15.opPattern","COPY",BODY,{"derivedFrom":makeQuery(id+"F11.opPattern","COPY",BODY,{"derivedFrom":makeQuery(id+"F6.opPattern","COPY",BODY,{"derivedFrom":makeQuery(id+"F4.opPattern","COPY",BODY,{"derivedFrom":makeQuery(id+"F2.opExtrude","SWEPT_BODY",BODY,{"disambiguationData":[OSD([sQuery(id+"F1.wireOp",EDGE,"E1.bottom"),sQuery(id+"F1.wireOp",EDGE,"E1.top"),sQuery(id+"F1.wireOp",EDGE,"E1.left"),sQuery(id+"F1.wireOp",EDGE,"E1.right")])]}),"instanceName":"1"}),"instanceName":"1"}),"instanceName":"1"}),"instanceName":"1"});
            var Q14;
            Q14=makeQuery(id+"F15.opPattern","COPY",BODY,{"derivedFrom":makeQuery(id+"F13.opPattern","COPY",BODY,{"derivedFrom":makeQuery(id+"F11.opPattern","COPY",BODY,{"derivedFrom":makeQuery(id+"F6.opPattern","COPY",BODY,{"derivedFrom":makeQuery(id+"F2.opExtrude","SWEPT_BODY",BODY,{"disambiguationData":[OSD([sQuery(id+"F1.wireOp",EDGE,"E1.bottom"),sQuery(id+"F1.wireOp",EDGE,"E1.top"),sQuery(id+"F1.wireOp",EDGE,"E1.left"),sQuery(id+"F1.wireOp",EDGE,"E1.right")])]}),"instanceName":"1"}),"instanceName":"1"}),"instanceName":"1"}),"instanceName":"1"});
            var Q15;
            Q15=makeQuery(id+"F15.opPattern","COPY",BODY,{"derivedFrom":makeQuery(id+"F13.opPattern","COPY",BODY,{"derivedFrom":makeQuery(id+"F11.opPattern","COPY",BODY,{"derivedFrom":makeQuery(id+"F6.opPattern","COPY",BODY,{"derivedFrom":makeQuery(id+"F4.opPattern","COPY",BODY,{"derivedFrom":makeQuery(id+"F2.opExtrude","SWEPT_BODY",BODY,{"disambiguationData":[OSD([sQuery(id+"F1.wireOp",EDGE,"E1.bottom"),sQuery(id+"F1.wireOp",EDGE,"E1.top"),sQuery(id+"F1.wireOp",EDGE,"E1.left"),sQuery(id+"F1.wireOp",EDGE,"E1.right")])]}),"instanceName":"1"}),"instanceName":"1"}),"instanceName":"1"}),"instanceName":"1"}),"instanceName":"1"});
            transform(context, id + "F17", {"entities" : qUnion([Q0, Q1, Q2, Q3, Q4, Q5, Q6, Q7, Q8, Q9, Q10, Q11, Q12, Q13, Q14, Q15]), "transformType" : TransformType.TRANSLATION_3D, "dx" : 0 * mm, "dy" : -74.17 * mm, "dz" : 0 * mm, "makeCopy" : false});
        }
        {
            var Q0;
            Q0=makeQuery(id+"F13.opPattern","COPY",BODY,{"derivedFrom":makeQuery(id+"F11.opPattern","COPY",BODY,{"derivedFrom":makeQuery(id+"F6.opPattern","COPY",BODY,{"derivedFrom":makeQuery(id+"F4.opPattern","COPY",BODY,{"derivedFrom":makeQuery(id+"F2.opExtrude","SWEPT_BODY",BODY,{"disambiguationData":[OSD([sQuery(id+"F1.wireOp",EDGE,"E1.bottom"),sQuery(id+"F1.wireOp",EDGE,"E1.top"),sQuery(id+"F1.wireOp",EDGE,"E1.left"),sQuery(id+"F1.wireOp",EDGE,"E1.right")])]}),"instanceName":"1"}),"instanceName":"1"}),"instanceName":"1"}),"instanceName":"1"});
            var Q1;
            Q1=makeQuery(id+"F13.opPattern","COPY",BODY,{"derivedFrom":makeQuery(id+"F6.opPattern","COPY",BODY,{"derivedFrom":makeQuery(id+"F4.opPattern","COPY",BODY,{"derivedFrom":makeQuery(id+"F2.opExtrude","SWEPT_BODY",BODY,{"disambiguationData":[OSD([sQuery(id+"F1.wireOp",EDGE,"E1.bottom"),sQuery(id+"F1.wireOp",EDGE,"E1.top"),sQuery(id+"F1.wireOp",EDGE,"E1.left"),sQuery(id+"F1.wireOp",EDGE,"E1.right")])]}),"instanceName":"1"}),"instanceName":"1"}),"instanceName":"1"});
            var Q2;
            Q2=makeQuery(id+"F13.opPattern","COPY",BODY,{"derivedFrom":makeQuery(id+"F6.opPattern","COPY",BODY,{"derivedFrom":makeQuery(id+"F2.opExtrude","SWEPT_BODY",BODY,{"disambiguationData":[OSD([sQuery(id+"F1.wireOp",EDGE,"E1.bottom"),sQuery(id+"F1.wireOp",EDGE,"E1.top"),sQuery(id+"F1.wireOp",EDGE,"E1.left"),sQuery(id+"F1.wireOp",EDGE,"E1.right")])]}),"instanceName":"1"}),"instanceName":"1"});
            var Q3;
            Q3=makeQuery(id+"F11.opPattern","COPY",BODY,{"derivedFrom":makeQuery(id+"F4.opPattern","COPY",BODY,{"derivedFrom":makeQuery(id+"F2.opExtrude","SWEPT_BODY",BODY,{"disambiguationData":[OSD([sQuery(id+"F1.wireOp",EDGE,"E1.bottom"),sQuery(id+"F1.wireOp",EDGE,"E1.top"),sQuery(id+"F1.wireOp",EDGE,"E1.left"),sQuery(id+"F1.wireOp",EDGE,"E1.right")])]}),"instanceName":"1"}),"instanceName":"1"});
            var Q4;
            Q4=makeQuery(id+"F6.opPattern","COPY",BODY,{"derivedFrom":makeQuery(id+"F2.opExtrude","SWEPT_BODY",BODY,{"disambiguationData":[OSD([sQuery(id+"F1.wireOp",EDGE,"E1.bottom"),sQuery(id+"F1.wireOp",EDGE,"E1.top"),sQuery(id+"F1.wireOp",EDGE,"E1.left"),sQuery(id+"F1.wireOp",EDGE,"E1.right")])]}),"instanceName":"1"});
            var Q5;
            Q5=makeQuery(id+"F13.opPattern","COPY",BODY,{"derivedFrom":makeQuery(id+"F4.opPattern","COPY",BODY,{"derivedFrom":makeQuery(id+"F2.opExtrude","SWEPT_BODY",BODY,{"disambiguationData":[OSD([sQuery(id+"F1.wireOp",EDGE,"E1.bottom"),sQuery(id+"F1.wireOp",EDGE,"E1.top"),sQuery(id+"F1.wireOp",EDGE,"E1.left"),sQuery(id+"F1.wireOp",EDGE,"E1.right")])]}),"instanceName":"1"}),"instanceName":"1"});
            var Q6;
            Q6=makeQuery(id+"F13.opPattern","COPY",BODY,{"derivedFrom":makeQuery(id+"F2.opExtrude","SWEPT_BODY",BODY,{"disambiguationData":[OSD([sQuery(id+"F1.wireOp",EDGE,"E1.bottom"),sQuery(id+"F1.wireOp",EDGE,"E1.top"),sQuery(id+"F1.wireOp",EDGE,"E1.left"),sQuery(id+"F1.wireOp",EDGE,"E1.right")])]}),"instanceName":"1"});
            var Q7;
            Q7=makeQuery(id+"F11.opPattern","COPY",BODY,{"derivedFrom":makeQuery(id+"F2.opExtrude","SWEPT_BODY",BODY,{"disambiguationData":[OSD([sQuery(id+"F1.wireOp",EDGE,"E1.bottom"),sQuery(id+"F1.wireOp",EDGE,"E1.top"),sQuery(id+"F1.wireOp",EDGE,"E1.left"),sQuery(id+"F1.wireOp",EDGE,"E1.right")])]}),"instanceName":"1"});
            var Q8;
            Q8=makeQuery(id+"F4.opPattern","COPY",BODY,{"derivedFrom":makeQuery(id+"F2.opExtrude","SWEPT_BODY",BODY,{"disambiguationData":[OSD([sQuery(id+"F1.wireOp",EDGE,"E1.bottom"),sQuery(id+"F1.wireOp",EDGE,"E1.top"),sQuery(id+"F1.wireOp",EDGE,"E1.left"),sQuery(id+"F1.wireOp",EDGE,"E1.right")])]}),"instanceName":"1"});
            var Q9;
            Q9=makeQuery(id+"F11.opPattern","COPY",BODY,{"derivedFrom":makeQuery(id+"F6.opPattern","COPY",BODY,{"derivedFrom":makeQuery(id+"F2.opExtrude","SWEPT_BODY",BODY,{"disambiguationData":[OSD([sQuery(id+"F1.wireOp",EDGE,"E1.bottom"),sQuery(id+"F1.wireOp",EDGE,"E1.top"),sQuery(id+"F1.wireOp",EDGE,"E1.left"),sQuery(id+"F1.wireOp",EDGE,"E1.right")])]}),"instanceName":"1"}),"instanceName":"1"});
            var Q10;
            Q10=makeQuery(id+"F11.opPattern","COPY",BODY,{"derivedFrom":makeQuery(id+"F6.opPattern","COPY",BODY,{"derivedFrom":makeQuery(id+"F4.opPattern","COPY",BODY,{"derivedFrom":makeQuery(id+"F2.opExtrude","SWEPT_BODY",BODY,{"disambiguationData":[OSD([sQuery(id+"F1.wireOp",EDGE,"E1.bottom"),sQuery(id+"F1.wireOp",EDGE,"E1.top"),sQuery(id+"F1.wireOp",EDGE,"E1.left"),sQuery(id+"F1.wireOp",EDGE,"E1.right")])]}),"instanceName":"1"}),"instanceName":"1"}),"instanceName":"1"});
            var Q11;
            Q11=makeQuery(id+"F13.opPattern","COPY",BODY,{"derivedFrom":makeQuery(id+"F11.opPattern","COPY",BODY,{"derivedFrom":makeQuery(id+"F6.opPattern","COPY",BODY,{"derivedFrom":makeQuery(id+"F2.opExtrude","SWEPT_BODY",BODY,{"disambiguationData":[OSD([sQuery(id+"F1.wireOp",EDGE,"E1.bottom"),sQuery(id+"F1.wireOp",EDGE,"E1.top"),sQuery(id+"F1.wireOp",EDGE,"E1.left"),sQuery(id+"F1.wireOp",EDGE,"E1.right")])]}),"instanceName":"1"}),"instanceName":"1"}),"instanceName":"1"});
            var Q12;
            Q12=makeQuery(id+"F13.opPattern","COPY",BODY,{"derivedFrom":makeQuery(id+"F11.opPattern","COPY",BODY,{"derivedFrom":makeQuery(id+"F4.opPattern","COPY",BODY,{"derivedFrom":makeQuery(id+"F2.opExtrude","SWEPT_BODY",BODY,{"disambiguationData":[OSD([sQuery(id+"F1.wireOp",EDGE,"E1.bottom"),sQuery(id+"F1.wireOp",EDGE,"E1.top"),sQuery(id+"F1.wireOp",EDGE,"E1.left"),sQuery(id+"F1.wireOp",EDGE,"E1.right")])]}),"instanceName":"1"}),"instanceName":"1"}),"instanceName":"1"});
            var Q13;
            Q13=makeQuery(id+"F2.opExtrude","SWEPT_BODY",BODY,{"disambiguationData":[OSD([sQuery(id+"F1.wireOp",EDGE,"E1.bottom"),sQuery(id+"F1.wireOp",EDGE,"E1.top"),sQuery(id+"F1.wireOp",EDGE,"E1.left"),sQuery(id+"F1.wireOp",EDGE,"E1.right")])]});
            var Q14;
            Q14=makeQuery(id+"F13.opPattern","COPY",BODY,{"derivedFrom":makeQuery(id+"F11.opPattern","COPY",BODY,{"derivedFrom":makeQuery(id+"F2.opExtrude","SWEPT_BODY",BODY,{"disambiguationData":[OSD([sQuery(id+"F1.wireOp",EDGE,"E1.bottom"),sQuery(id+"F1.wireOp",EDGE,"E1.top"),sQuery(id+"F1.wireOp",EDGE,"E1.left"),sQuery(id+"F1.wireOp",EDGE,"E1.right")])]}),"instanceName":"1"}),"instanceName":"1"});
            var Q15;
            Q15=makeQuery(id+"F6.opPattern","COPY",BODY,{"derivedFrom":makeQuery(id+"F4.opPattern","COPY",BODY,{"derivedFrom":makeQuery(id+"F2.opExtrude","SWEPT_BODY",BODY,{"disambiguationData":[OSD([sQuery(id+"F1.wireOp",EDGE,"E1.bottom"),sQuery(id+"F1.wireOp",EDGE,"E1.top"),sQuery(id+"F1.wireOp",EDGE,"E1.left"),sQuery(id+"F1.wireOp",EDGE,"E1.right")])]}),"instanceName":"1"}),"instanceName":"1"});
            transform(context, id + "F18", {"entities" : qUnion([Q0, Q1, Q2, Q3, Q4, Q5, Q6, Q7, Q8, Q9, Q10, Q11, Q12, Q13, Q14, Q15]), "transformType" : TransformType.TRANSLATION_3D, "dx" : 1.02 * mm, "dy" : -4.32 * mm, "dz" : 0 * mm, "makeCopy" : false});
        }
        {
            var Q0;
            Q0=makeQuery(id+"F15.opPattern","COPY",BODY,{"derivedFrom":makeQuery(id+"F13.opPattern","COPY",BODY,{"derivedFrom":makeQuery(id+"F2.opExtrude","SWEPT_BODY",BODY,{"disambiguationData":[OSD([sQuery(id+"F1.wireOp",EDGE,"E1.bottom"),sQuery(id+"F1.wireOp",EDGE,"E1.top"),sQuery(id+"F1.wireOp",EDGE,"E1.left"),sQuery(id+"F1.wireOp",EDGE,"E1.right")])]}),"instanceName":"1"}),"instanceName":"1"});
            var Q1;
            Q1=makeQuery(id+"F15.opPattern","COPY",BODY,{"derivedFrom":makeQuery(id+"F13.opPattern","COPY",BODY,{"derivedFrom":makeQuery(id+"F6.opPattern","COPY",BODY,{"derivedFrom":makeQuery(id+"F2.opExtrude","SWEPT_BODY",BODY,{"disambiguationData":[OSD([sQuery(id+"F1.wireOp",EDGE,"E1.bottom"),sQuery(id+"F1.wireOp",EDGE,"E1.top"),sQuery(id+"F1.wireOp",EDGE,"E1.left"),sQuery(id+"F1.wireOp",EDGE,"E1.right")])]}),"instanceName":"1"}),"instanceName":"1"}),"instanceName":"1"});
            var Q2;
            Q2=makeQuery(id+"F15.opPattern","COPY",BODY,{"derivedFrom":makeQuery(id+"F13.opPattern","COPY",BODY,{"derivedFrom":makeQuery(id+"F4.opPattern","COPY",BODY,{"derivedFrom":makeQuery(id+"F2.opExtrude","SWEPT_BODY",BODY,{"disambiguationData":[OSD([sQuery(id+"F1.wireOp",EDGE,"E1.bottom"),sQuery(id+"F1.wireOp",EDGE,"E1.top"),sQuery(id+"F1.wireOp",EDGE,"E1.left"),sQuery(id+"F1.wireOp",EDGE,"E1.right")])]}),"instanceName":"1"}),"instanceName":"1"}),"instanceName":"1"});
            var Q3;
            Q3=makeQuery(id+"F15.opPattern","COPY",BODY,{"derivedFrom":makeQuery(id+"F13.opPattern","COPY",BODY,{"derivedFrom":makeQuery(id+"F6.opPattern","COPY",BODY,{"derivedFrom":makeQuery(id+"F4.opPattern","COPY",BODY,{"derivedFrom":makeQuery(id+"F2.opExtrude","SWEPT_BODY",BODY,{"disambiguationData":[OSD([sQuery(id+"F1.wireOp",EDGE,"E1.bottom"),sQuery(id+"F1.wireOp",EDGE,"E1.top"),sQuery(id+"F1.wireOp",EDGE,"E1.left"),sQuery(id+"F1.wireOp",EDGE,"E1.right")])]}),"instanceName":"1"}),"instanceName":"1"}),"instanceName":"1"}),"instanceName":"1"});
            var Q4;
            Q4=makeQuery(id+"F15.opPattern","COPY",BODY,{"derivedFrom":makeQuery(id+"F13.opPattern","COPY",BODY,{"derivedFrom":makeQuery(id+"F11.opPattern","COPY",BODY,{"derivedFrom":makeQuery(id+"F2.opExtrude","SWEPT_BODY",BODY,{"disambiguationData":[OSD([sQuery(id+"F1.wireOp",EDGE,"E1.bottom"),sQuery(id+"F1.wireOp",EDGE,"E1.top"),sQuery(id+"F1.wireOp",EDGE,"E1.left"),sQuery(id+"F1.wireOp",EDGE,"E1.right")])]}),"instanceName":"1"}),"instanceName":"1"}),"instanceName":"1"});
            var Q5;
            Q5=makeQuery(id+"F15.opPattern","COPY",BODY,{"derivedFrom":makeQuery(id+"F13.opPattern","COPY",BODY,{"derivedFrom":makeQuery(id+"F11.opPattern","COPY",BODY,{"derivedFrom":makeQuery(id+"F6.opPattern","COPY",BODY,{"derivedFrom":makeQuery(id+"F2.opExtrude","SWEPT_BODY",BODY,{"disambiguationData":[OSD([sQuery(id+"F1.wireOp",EDGE,"E1.bottom"),sQuery(id+"F1.wireOp",EDGE,"E1.top"),sQuery(id+"F1.wireOp",EDGE,"E1.left"),sQuery(id+"F1.wireOp",EDGE,"E1.right")])]}),"instanceName":"1"}),"instanceName":"1"}),"instanceName":"1"}),"instanceName":"1"});
            var Q6;
            Q6=makeQuery(id+"F15.opPattern","COPY",BODY,{"derivedFrom":makeQuery(id+"F13.opPattern","COPY",BODY,{"derivedFrom":makeQuery(id+"F11.opPattern","COPY",BODY,{"derivedFrom":makeQuery(id+"F4.opPattern","COPY",BODY,{"derivedFrom":makeQuery(id+"F2.opExtrude","SWEPT_BODY",BODY,{"disambiguationData":[OSD([sQuery(id+"F1.wireOp",EDGE,"E1.bottom"),sQuery(id+"F1.wireOp",EDGE,"E1.top"),sQuery(id+"F1.wireOp",EDGE,"E1.left"),sQuery(id+"F1.wireOp",EDGE,"E1.right")])]}),"instanceName":"1"}),"instanceName":"1"}),"instanceName":"1"}),"instanceName":"1"});
            var Q7;
            Q7=makeQuery(id+"F15.opPattern","COPY",BODY,{"derivedFrom":makeQuery(id+"F13.opPattern","COPY",BODY,{"derivedFrom":makeQuery(id+"F11.opPattern","COPY",BODY,{"derivedFrom":makeQuery(id+"F6.opPattern","COPY",BODY,{"derivedFrom":makeQuery(id+"F4.opPattern","COPY",BODY,{"derivedFrom":makeQuery(id+"F2.opExtrude","SWEPT_BODY",BODY,{"disambiguationData":[OSD([sQuery(id+"F1.wireOp",EDGE,"E1.bottom"),sQuery(id+"F1.wireOp",EDGE,"E1.top"),sQuery(id+"F1.wireOp",EDGE,"E1.left"),sQuery(id+"F1.wireOp",EDGE,"E1.right")])]}),"instanceName":"1"}),"instanceName":"1"}),"instanceName":"1"}),"instanceName":"1"}),"instanceName":"1"});
            var Q8;
            Q8=makeQuery(id+"F15.opPattern","COPY",BODY,{"derivedFrom":makeQuery(id+"F2.opExtrude","SWEPT_BODY",BODY,{"disambiguationData":[OSD([sQuery(id+"F1.wireOp",EDGE,"E1.bottom"),sQuery(id+"F1.wireOp",EDGE,"E1.top"),sQuery(id+"F1.wireOp",EDGE,"E1.left"),sQuery(id+"F1.wireOp",EDGE,"E1.right")])]}),"instanceName":"1"});
            var Q9;
            Q9=makeQuery(id+"F15.opPattern","COPY",BODY,{"derivedFrom":makeQuery(id+"F6.opPattern","COPY",BODY,{"derivedFrom":makeQuery(id+"F2.opExtrude","SWEPT_BODY",BODY,{"disambiguationData":[OSD([sQuery(id+"F1.wireOp",EDGE,"E1.bottom"),sQuery(id+"F1.wireOp",EDGE,"E1.top"),sQuery(id+"F1.wireOp",EDGE,"E1.left"),sQuery(id+"F1.wireOp",EDGE,"E1.right")])]}),"instanceName":"1"}),"instanceName":"1"});
            var Q10;
            Q10=makeQuery(id+"F15.opPattern","COPY",BODY,{"derivedFrom":makeQuery(id+"F4.opPattern","COPY",BODY,{"derivedFrom":makeQuery(id+"F2.opExtrude","SWEPT_BODY",BODY,{"disambiguationData":[OSD([sQuery(id+"F1.wireOp",EDGE,"E1.bottom"),sQuery(id+"F1.wireOp",EDGE,"E1.top"),sQuery(id+"F1.wireOp",EDGE,"E1.left"),sQuery(id+"F1.wireOp",EDGE,"E1.right")])]}),"instanceName":"1"}),"instanceName":"1"});
            var Q11;
            Q11=makeQuery(id+"F15.opPattern","COPY",BODY,{"derivedFrom":makeQuery(id+"F6.opPattern","COPY",BODY,{"derivedFrom":makeQuery(id+"F4.opPattern","COPY",BODY,{"derivedFrom":makeQuery(id+"F2.opExtrude","SWEPT_BODY",BODY,{"disambiguationData":[OSD([sQuery(id+"F1.wireOp",EDGE,"E1.bottom"),sQuery(id+"F1.wireOp",EDGE,"E1.top"),sQuery(id+"F1.wireOp",EDGE,"E1.left"),sQuery(id+"F1.wireOp",EDGE,"E1.right")])]}),"instanceName":"1"}),"instanceName":"1"}),"instanceName":"1"});
            var Q12;
            Q12=makeQuery(id+"F15.opPattern","COPY",BODY,{"derivedFrom":makeQuery(id+"F11.opPattern","COPY",BODY,{"derivedFrom":makeQuery(id+"F2.opExtrude","SWEPT_BODY",BODY,{"disambiguationData":[OSD([sQuery(id+"F1.wireOp",EDGE,"E1.bottom"),sQuery(id+"F1.wireOp",EDGE,"E1.top"),sQuery(id+"F1.wireOp",EDGE,"E1.left"),sQuery(id+"F1.wireOp",EDGE,"E1.right")])]}),"instanceName":"1"}),"instanceName":"1"});
            var Q13;
            Q13=makeQuery(id+"F15.opPattern","COPY",BODY,{"derivedFrom":makeQuery(id+"F11.opPattern","COPY",BODY,{"derivedFrom":makeQuery(id+"F6.opPattern","COPY",BODY,{"derivedFrom":makeQuery(id+"F2.opExtrude","SWEPT_BODY",BODY,{"disambiguationData":[OSD([sQuery(id+"F1.wireOp",EDGE,"E1.bottom"),sQuery(id+"F1.wireOp",EDGE,"E1.top"),sQuery(id+"F1.wireOp",EDGE,"E1.left"),sQuery(id+"F1.wireOp",EDGE,"E1.right")])]}),"instanceName":"1"}),"instanceName":"1"}),"instanceName":"1"});
            var Q14;
            Q14=makeQuery(id+"F15.opPattern","COPY",BODY,{"derivedFrom":makeQuery(id+"F11.opPattern","COPY",BODY,{"derivedFrom":makeQuery(id+"F4.opPattern","COPY",BODY,{"derivedFrom":makeQuery(id+"F2.opExtrude","SWEPT_BODY",BODY,{"disambiguationData":[OSD([sQuery(id+"F1.wireOp",EDGE,"E1.bottom"),sQuery(id+"F1.wireOp",EDGE,"E1.top"),sQuery(id+"F1.wireOp",EDGE,"E1.left"),sQuery(id+"F1.wireOp",EDGE,"E1.right")])]}),"instanceName":"1"}),"instanceName":"1"}),"instanceName":"1"});
            var Q15;
            Q15=makeQuery(id+"F15.opPattern","COPY",BODY,{"derivedFrom":makeQuery(id+"F11.opPattern","COPY",BODY,{"derivedFrom":makeQuery(id+"F6.opPattern","COPY",BODY,{"derivedFrom":makeQuery(id+"F4.opPattern","COPY",BODY,{"derivedFrom":makeQuery(id+"F2.opExtrude","SWEPT_BODY",BODY,{"disambiguationData":[OSD([sQuery(id+"F1.wireOp",EDGE,"E1.bottom"),sQuery(id+"F1.wireOp",EDGE,"E1.top"),sQuery(id+"F1.wireOp",EDGE,"E1.left"),sQuery(id+"F1.wireOp",EDGE,"E1.right")])]}),"instanceName":"1"}),"instanceName":"1"}),"instanceName":"1"}),"instanceName":"1"});
            transform(context, id + "F19", {"entities" : qUnion([Q0, Q1, Q2, Q3, Q4, Q5, Q6, Q7, Q8, Q9, Q10, Q11, Q12, Q13, Q14, Q15]), "transformType" : TransformType.TRANSLATION_3D, "dx" : 0 * mm, "dy" : 5.84 * mm, "dz" : 0 * mm, "makeCopy" : false});
        }
        {
            var Q0;
            Q0=makeQuery(id+"F15.opPattern","COPY",BODY,{"derivedFrom":makeQuery(id+"F11.opPattern","COPY",BODY,{"derivedFrom":makeQuery(id+"F6.opPattern","COPY",BODY,{"derivedFrom":makeQuery(id+"F4.opPattern","COPY",BODY,{"derivedFrom":makeQuery(id+"F2.opExtrude","SWEPT_BODY",BODY,{"disambiguationData":[OSD([sQuery(id+"F1.wireOp",EDGE,"E1.bottom"),sQuery(id+"F1.wireOp",EDGE,"E1.top"),sQuery(id+"F1.wireOp",EDGE,"E1.left"),sQuery(id+"F1.wireOp",EDGE,"E1.right")])]}),"instanceName":"1"}),"instanceName":"1"}),"instanceName":"1"}),"instanceName":"1"});
            var Q1;
            Q1=makeQuery(id+"F15.opPattern","COPY",BODY,{"derivedFrom":makeQuery(id+"F11.opPattern","COPY",BODY,{"derivedFrom":makeQuery(id+"F4.opPattern","COPY",BODY,{"derivedFrom":makeQuery(id+"F2.opExtrude","SWEPT_BODY",BODY,{"disambiguationData":[OSD([sQuery(id+"F1.wireOp",EDGE,"E1.bottom"),sQuery(id+"F1.wireOp",EDGE,"E1.top"),sQuery(id+"F1.wireOp",EDGE,"E1.left"),sQuery(id+"F1.wireOp",EDGE,"E1.right")])]}),"instanceName":"1"}),"instanceName":"1"}),"instanceName":"1"});
            var Q2;
            Q2=makeQuery(id+"F15.opPattern","COPY",BODY,{"derivedFrom":makeQuery(id+"F11.opPattern","COPY",BODY,{"derivedFrom":makeQuery(id+"F2.opExtrude","SWEPT_BODY",BODY,{"disambiguationData":[OSD([sQuery(id+"F1.wireOp",EDGE,"E1.bottom"),sQuery(id+"F1.wireOp",EDGE,"E1.top"),sQuery(id+"F1.wireOp",EDGE,"E1.left"),sQuery(id+"F1.wireOp",EDGE,"E1.right")])]}),"instanceName":"1"}),"instanceName":"1"});
            var Q3;
            Q3=makeQuery(id+"F15.opPattern","COPY",BODY,{"derivedFrom":makeQuery(id+"F11.opPattern","COPY",BODY,{"derivedFrom":makeQuery(id+"F6.opPattern","COPY",BODY,{"derivedFrom":makeQuery(id+"F2.opExtrude","SWEPT_BODY",BODY,{"disambiguationData":[OSD([sQuery(id+"F1.wireOp",EDGE,"E1.bottom"),sQuery(id+"F1.wireOp",EDGE,"E1.top"),sQuery(id+"F1.wireOp",EDGE,"E1.left"),sQuery(id+"F1.wireOp",EDGE,"E1.right")])]}),"instanceName":"1"}),"instanceName":"1"}),"instanceName":"1"});
            var Q4;
            Q4=makeQuery(id+"F15.opPattern","COPY",BODY,{"derivedFrom":makeQuery(id+"F6.opPattern","COPY",BODY,{"derivedFrom":makeQuery(id+"F4.opPattern","COPY",BODY,{"derivedFrom":makeQuery(id+"F2.opExtrude","SWEPT_BODY",BODY,{"disambiguationData":[OSD([sQuery(id+"F1.wireOp",EDGE,"E1.bottom"),sQuery(id+"F1.wireOp",EDGE,"E1.top"),sQuery(id+"F1.wireOp",EDGE,"E1.left"),sQuery(id+"F1.wireOp",EDGE,"E1.right")])]}),"instanceName":"1"}),"instanceName":"1"}),"instanceName":"1"});
            var Q5;
            Q5=makeQuery(id+"F15.opPattern","COPY",BODY,{"derivedFrom":makeQuery(id+"F4.opPattern","COPY",BODY,{"derivedFrom":makeQuery(id+"F2.opExtrude","SWEPT_BODY",BODY,{"disambiguationData":[OSD([sQuery(id+"F1.wireOp",EDGE,"E1.bottom"),sQuery(id+"F1.wireOp",EDGE,"E1.top"),sQuery(id+"F1.wireOp",EDGE,"E1.left"),sQuery(id+"F1.wireOp",EDGE,"E1.right")])]}),"instanceName":"1"}),"instanceName":"1"});
            var Q6;
            Q6=makeQuery(id+"F15.opPattern","COPY",BODY,{"derivedFrom":makeQuery(id+"F6.opPattern","COPY",BODY,{"derivedFrom":makeQuery(id+"F2.opExtrude","SWEPT_BODY",BODY,{"disambiguationData":[OSD([sQuery(id+"F1.wireOp",EDGE,"E1.bottom"),sQuery(id+"F1.wireOp",EDGE,"E1.top"),sQuery(id+"F1.wireOp",EDGE,"E1.left"),sQuery(id+"F1.wireOp",EDGE,"E1.right")])]}),"instanceName":"1"}),"instanceName":"1"});
            var Q7;
            Q7=makeQuery(id+"F15.opPattern","COPY",BODY,{"derivedFrom":makeQuery(id+"F2.opExtrude","SWEPT_BODY",BODY,{"disambiguationData":[OSD([sQuery(id+"F1.wireOp",EDGE,"E1.bottom"),sQuery(id+"F1.wireOp",EDGE,"E1.top"),sQuery(id+"F1.wireOp",EDGE,"E1.left"),sQuery(id+"F1.wireOp",EDGE,"E1.right")])]}),"instanceName":"1"});
            var Q8;
            Q8=makeQuery(id+"F15.opPattern","COPY",BODY,{"derivedFrom":makeQuery(id+"F13.opPattern","COPY",BODY,{"derivedFrom":makeQuery(id+"F11.opPattern","COPY",BODY,{"derivedFrom":makeQuery(id+"F6.opPattern","COPY",BODY,{"derivedFrom":makeQuery(id+"F4.opPattern","COPY",BODY,{"derivedFrom":makeQuery(id+"F2.opExtrude","SWEPT_BODY",BODY,{"disambiguationData":[OSD([sQuery(id+"F1.wireOp",EDGE,"E1.bottom"),sQuery(id+"F1.wireOp",EDGE,"E1.top"),sQuery(id+"F1.wireOp",EDGE,"E1.left"),sQuery(id+"F1.wireOp",EDGE,"E1.right")])]}),"instanceName":"1"}),"instanceName":"1"}),"instanceName":"1"}),"instanceName":"1"}),"instanceName":"1"});
            var Q9;
            Q9=makeQuery(id+"F15.opPattern","COPY",BODY,{"derivedFrom":makeQuery(id+"F13.opPattern","COPY",BODY,{"derivedFrom":makeQuery(id+"F11.opPattern","COPY",BODY,{"derivedFrom":makeQuery(id+"F4.opPattern","COPY",BODY,{"derivedFrom":makeQuery(id+"F2.opExtrude","SWEPT_BODY",BODY,{"disambiguationData":[OSD([sQuery(id+"F1.wireOp",EDGE,"E1.bottom"),sQuery(id+"F1.wireOp",EDGE,"E1.top"),sQuery(id+"F1.wireOp",EDGE,"E1.left"),sQuery(id+"F1.wireOp",EDGE,"E1.right")])]}),"instanceName":"1"}),"instanceName":"1"}),"instanceName":"1"}),"instanceName":"1"});
            var Q10;
            Q10=makeQuery(id+"F15.opPattern","COPY",BODY,{"derivedFrom":makeQuery(id+"F13.opPattern","COPY",BODY,{"derivedFrom":makeQuery(id+"F11.opPattern","COPY",BODY,{"derivedFrom":makeQuery(id+"F6.opPattern","COPY",BODY,{"derivedFrom":makeQuery(id+"F2.opExtrude","SWEPT_BODY",BODY,{"disambiguationData":[OSD([sQuery(id+"F1.wireOp",EDGE,"E1.bottom"),sQuery(id+"F1.wireOp",EDGE,"E1.top"),sQuery(id+"F1.wireOp",EDGE,"E1.left"),sQuery(id+"F1.wireOp",EDGE,"E1.right")])]}),"instanceName":"1"}),"instanceName":"1"}),"instanceName":"1"}),"instanceName":"1"});
            var Q11;
            Q11=makeQuery(id+"F15.opPattern","COPY",BODY,{"derivedFrom":makeQuery(id+"F13.opPattern","COPY",BODY,{"derivedFrom":makeQuery(id+"F11.opPattern","COPY",BODY,{"derivedFrom":makeQuery(id+"F2.opExtrude","SWEPT_BODY",BODY,{"disambiguationData":[OSD([sQuery(id+"F1.wireOp",EDGE,"E1.bottom"),sQuery(id+"F1.wireOp",EDGE,"E1.top"),sQuery(id+"F1.wireOp",EDGE,"E1.left"),sQuery(id+"F1.wireOp",EDGE,"E1.right")])]}),"instanceName":"1"}),"instanceName":"1"}),"instanceName":"1"});
            var Q12;
            Q12=makeQuery(id+"F15.opPattern","COPY",BODY,{"derivedFrom":makeQuery(id+"F13.opPattern","COPY",BODY,{"derivedFrom":makeQuery(id+"F6.opPattern","COPY",BODY,{"derivedFrom":makeQuery(id+"F4.opPattern","COPY",BODY,{"derivedFrom":makeQuery(id+"F2.opExtrude","SWEPT_BODY",BODY,{"disambiguationData":[OSD([sQuery(id+"F1.wireOp",EDGE,"E1.bottom"),sQuery(id+"F1.wireOp",EDGE,"E1.top"),sQuery(id+"F1.wireOp",EDGE,"E1.left"),sQuery(id+"F1.wireOp",EDGE,"E1.right")])]}),"instanceName":"1"}),"instanceName":"1"}),"instanceName":"1"}),"instanceName":"1"});
            var Q13;
            Q13=makeQuery(id+"F15.opPattern","COPY",BODY,{"derivedFrom":makeQuery(id+"F13.opPattern","COPY",BODY,{"derivedFrom":makeQuery(id+"F4.opPattern","COPY",BODY,{"derivedFrom":makeQuery(id+"F2.opExtrude","SWEPT_BODY",BODY,{"disambiguationData":[OSD([sQuery(id+"F1.wireOp",EDGE,"E1.bottom"),sQuery(id+"F1.wireOp",EDGE,"E1.top"),sQuery(id+"F1.wireOp",EDGE,"E1.left"),sQuery(id+"F1.wireOp",EDGE,"E1.right")])]}),"instanceName":"1"}),"instanceName":"1"}),"instanceName":"1"});
            var Q14;
            Q14=makeQuery(id+"F15.opPattern","COPY",BODY,{"derivedFrom":makeQuery(id+"F13.opPattern","COPY",BODY,{"derivedFrom":makeQuery(id+"F6.opPattern","COPY",BODY,{"derivedFrom":makeQuery(id+"F2.opExtrude","SWEPT_BODY",BODY,{"disambiguationData":[OSD([sQuery(id+"F1.wireOp",EDGE,"E1.bottom"),sQuery(id+"F1.wireOp",EDGE,"E1.top"),sQuery(id+"F1.wireOp",EDGE,"E1.left"),sQuery(id+"F1.wireOp",EDGE,"E1.right")])]}),"instanceName":"1"}),"instanceName":"1"}),"instanceName":"1"});
            var Q15;
            Q15=makeQuery(id+"F15.opPattern","COPY",BODY,{"derivedFrom":makeQuery(id+"F13.opPattern","COPY",BODY,{"derivedFrom":makeQuery(id+"F2.opExtrude","SWEPT_BODY",BODY,{"disambiguationData":[OSD([sQuery(id+"F1.wireOp",EDGE,"E1.bottom"),sQuery(id+"F1.wireOp",EDGE,"E1.top"),sQuery(id+"F1.wireOp",EDGE,"E1.left"),sQuery(id+"F1.wireOp",EDGE,"E1.right")])]}),"instanceName":"1"}),"instanceName":"1"});
            transform(context, id + "F20", {"entities" : qUnion([Q0, Q1, Q2, Q3, Q4, Q5, Q6, Q7, Q8, Q9, Q10, Q11, Q12, Q13, Q14, Q15]), "transformType" : TransformType.COPY});
        }
        {
            var Q0;
            Q0=makeQuery(id+"F15.opPattern","COPY",BODY,{"derivedFrom":makeQuery(id+"F11.opPattern","COPY",BODY,{"derivedFrom":makeQuery(id+"F6.opPattern","COPY",BODY,{"derivedFrom":makeQuery(id+"F4.opPattern","COPY",BODY,{"derivedFrom":makeQuery(id+"F2.opExtrude","SWEPT_BODY",BODY,{"disambiguationData":[OSD([sQuery(id+"F1.wireOp",EDGE,"E1.bottom"),sQuery(id+"F1.wireOp",EDGE,"E1.top"),sQuery(id+"F1.wireOp",EDGE,"E1.left"),sQuery(id+"F1.wireOp",EDGE,"E1.right")])]}),"instanceName":"1"}),"instanceName":"1"}),"instanceName":"1"}),"instanceName":"1"});
            var Q1;
            Q1=makeQuery(id+"F15.opPattern","COPY",BODY,{"derivedFrom":makeQuery(id+"F13.opPattern","COPY",BODY,{"derivedFrom":makeQuery(id+"F2.opExtrude","SWEPT_BODY",BODY,{"disambiguationData":[OSD([sQuery(id+"F1.wireOp",EDGE,"E1.bottom"),sQuery(id+"F1.wireOp",EDGE,"E1.top"),sQuery(id+"F1.wireOp",EDGE,"E1.left"),sQuery(id+"F1.wireOp",EDGE,"E1.right")])]}),"instanceName":"1"}),"instanceName":"1"});
            var Q2;
            Q2=makeQuery(id+"F15.opPattern","COPY",BODY,{"derivedFrom":makeQuery(id+"F13.opPattern","COPY",BODY,{"derivedFrom":makeQuery(id+"F6.opPattern","COPY",BODY,{"derivedFrom":makeQuery(id+"F2.opExtrude","SWEPT_BODY",BODY,{"disambiguationData":[OSD([sQuery(id+"F1.wireOp",EDGE,"E1.bottom"),sQuery(id+"F1.wireOp",EDGE,"E1.top"),sQuery(id+"F1.wireOp",EDGE,"E1.left"),sQuery(id+"F1.wireOp",EDGE,"E1.right")])]}),"instanceName":"1"}),"instanceName":"1"}),"instanceName":"1"});
            var Q3;
            Q3=makeQuery(id+"F15.opPattern","COPY",BODY,{"derivedFrom":makeQuery(id+"F13.opPattern","COPY",BODY,{"derivedFrom":makeQuery(id+"F4.opPattern","COPY",BODY,{"derivedFrom":makeQuery(id+"F2.opExtrude","SWEPT_BODY",BODY,{"disambiguationData":[OSD([sQuery(id+"F1.wireOp",EDGE,"E1.bottom"),sQuery(id+"F1.wireOp",EDGE,"E1.top"),sQuery(id+"F1.wireOp",EDGE,"E1.left"),sQuery(id+"F1.wireOp",EDGE,"E1.right")])]}),"instanceName":"1"}),"instanceName":"1"}),"instanceName":"1"});
            var Q4;
            Q4=makeQuery(id+"F15.opPattern","COPY",BODY,{"derivedFrom":makeQuery(id+"F13.opPattern","COPY",BODY,{"derivedFrom":makeQuery(id+"F6.opPattern","COPY",BODY,{"derivedFrom":makeQuery(id+"F4.opPattern","COPY",BODY,{"derivedFrom":makeQuery(id+"F2.opExtrude","SWEPT_BODY",BODY,{"disambiguationData":[OSD([sQuery(id+"F1.wireOp",EDGE,"E1.bottom"),sQuery(id+"F1.wireOp",EDGE,"E1.top"),sQuery(id+"F1.wireOp",EDGE,"E1.left"),sQuery(id+"F1.wireOp",EDGE,"E1.right")])]}),"instanceName":"1"}),"instanceName":"1"}),"instanceName":"1"}),"instanceName":"1"});
            var Q5;
            Q5=makeQuery(id+"F15.opPattern","COPY",BODY,{"derivedFrom":makeQuery(id+"F11.opPattern","COPY",BODY,{"derivedFrom":makeQuery(id+"F4.opPattern","COPY",BODY,{"derivedFrom":makeQuery(id+"F2.opExtrude","SWEPT_BODY",BODY,{"disambiguationData":[OSD([sQuery(id+"F1.wireOp",EDGE,"E1.bottom"),sQuery(id+"F1.wireOp",EDGE,"E1.top"),sQuery(id+"F1.wireOp",EDGE,"E1.left"),sQuery(id+"F1.wireOp",EDGE,"E1.right")])]}),"instanceName":"1"}),"instanceName":"1"}),"instanceName":"1"});
            var Q6;
            Q6=makeQuery(id+"F15.opPattern","COPY",BODY,{"derivedFrom":makeQuery(id+"F11.opPattern","COPY",BODY,{"derivedFrom":makeQuery(id+"F6.opPattern","COPY",BODY,{"derivedFrom":makeQuery(id+"F2.opExtrude","SWEPT_BODY",BODY,{"disambiguationData":[OSD([sQuery(id+"F1.wireOp",EDGE,"E1.bottom"),sQuery(id+"F1.wireOp",EDGE,"E1.top"),sQuery(id+"F1.wireOp",EDGE,"E1.left"),sQuery(id+"F1.wireOp",EDGE,"E1.right")])]}),"instanceName":"1"}),"instanceName":"1"}),"instanceName":"1"});
            var Q7;
            Q7=makeQuery(id+"F15.opPattern","COPY",BODY,{"derivedFrom":makeQuery(id+"F11.opPattern","COPY",BODY,{"derivedFrom":makeQuery(id+"F2.opExtrude","SWEPT_BODY",BODY,{"disambiguationData":[OSD([sQuery(id+"F1.wireOp",EDGE,"E1.bottom"),sQuery(id+"F1.wireOp",EDGE,"E1.top"),sQuery(id+"F1.wireOp",EDGE,"E1.left"),sQuery(id+"F1.wireOp",EDGE,"E1.right")])]}),"instanceName":"1"}),"instanceName":"1"});
            var Q8;
            Q8=makeQuery(id+"F15.opPattern","COPY",BODY,{"derivedFrom":makeQuery(id+"F6.opPattern","COPY",BODY,{"derivedFrom":makeQuery(id+"F4.opPattern","COPY",BODY,{"derivedFrom":makeQuery(id+"F2.opExtrude","SWEPT_BODY",BODY,{"disambiguationData":[OSD([sQuery(id+"F1.wireOp",EDGE,"E1.bottom"),sQuery(id+"F1.wireOp",EDGE,"E1.top"),sQuery(id+"F1.wireOp",EDGE,"E1.left"),sQuery(id+"F1.wireOp",EDGE,"E1.right")])]}),"instanceName":"1"}),"instanceName":"1"}),"instanceName":"1"});
            var Q9;
            Q9=makeQuery(id+"F15.opPattern","COPY",BODY,{"derivedFrom":makeQuery(id+"F4.opPattern","COPY",BODY,{"derivedFrom":makeQuery(id+"F2.opExtrude","SWEPT_BODY",BODY,{"disambiguationData":[OSD([sQuery(id+"F1.wireOp",EDGE,"E1.bottom"),sQuery(id+"F1.wireOp",EDGE,"E1.top"),sQuery(id+"F1.wireOp",EDGE,"E1.left"),sQuery(id+"F1.wireOp",EDGE,"E1.right")])]}),"instanceName":"1"}),"instanceName":"1"});
            var Q10;
            Q10=makeQuery(id+"F15.opPattern","COPY",BODY,{"derivedFrom":makeQuery(id+"F6.opPattern","COPY",BODY,{"derivedFrom":makeQuery(id+"F2.opExtrude","SWEPT_BODY",BODY,{"disambiguationData":[OSD([sQuery(id+"F1.wireOp",EDGE,"E1.bottom"),sQuery(id+"F1.wireOp",EDGE,"E1.top"),sQuery(id+"F1.wireOp",EDGE,"E1.left"),sQuery(id+"F1.wireOp",EDGE,"E1.right")])]}),"instanceName":"1"}),"instanceName":"1"});
            var Q11;
            Q11=makeQuery(id+"F15.opPattern","COPY",BODY,{"derivedFrom":makeQuery(id+"F2.opExtrude","SWEPT_BODY",BODY,{"disambiguationData":[OSD([sQuery(id+"F1.wireOp",EDGE,"E1.bottom"),sQuery(id+"F1.wireOp",EDGE,"E1.top"),sQuery(id+"F1.wireOp",EDGE,"E1.left"),sQuery(id+"F1.wireOp",EDGE,"E1.right")])]}),"instanceName":"1"});
            var Q12;
            Q12=makeQuery(id+"F15.opPattern","COPY",BODY,{"derivedFrom":makeQuery(id+"F13.opPattern","COPY",BODY,{"derivedFrom":makeQuery(id+"F11.opPattern","COPY",BODY,{"derivedFrom":makeQuery(id+"F2.opExtrude","SWEPT_BODY",BODY,{"disambiguationData":[OSD([sQuery(id+"F1.wireOp",EDGE,"E1.bottom"),sQuery(id+"F1.wireOp",EDGE,"E1.top"),sQuery(id+"F1.wireOp",EDGE,"E1.left"),sQuery(id+"F1.wireOp",EDGE,"E1.right")])]}),"instanceName":"1"}),"instanceName":"1"}),"instanceName":"1"});
            var Q13;
            Q13=makeQuery(id+"F15.opPattern","COPY",BODY,{"derivedFrom":makeQuery(id+"F13.opPattern","COPY",BODY,{"derivedFrom":makeQuery(id+"F11.opPattern","COPY",BODY,{"derivedFrom":makeQuery(id+"F6.opPattern","COPY",BODY,{"derivedFrom":makeQuery(id+"F2.opExtrude","SWEPT_BODY",BODY,{"disambiguationData":[OSD([sQuery(id+"F1.wireOp",EDGE,"E1.bottom"),sQuery(id+"F1.wireOp",EDGE,"E1.top"),sQuery(id+"F1.wireOp",EDGE,"E1.left"),sQuery(id+"F1.wireOp",EDGE,"E1.right")])]}),"instanceName":"1"}),"instanceName":"1"}),"instanceName":"1"}),"instanceName":"1"});
            var Q14;
            Q14=makeQuery(id+"F15.opPattern","COPY",BODY,{"derivedFrom":makeQuery(id+"F13.opPattern","COPY",BODY,{"derivedFrom":makeQuery(id+"F11.opPattern","COPY",BODY,{"derivedFrom":makeQuery(id+"F4.opPattern","COPY",BODY,{"derivedFrom":makeQuery(id+"F2.opExtrude","SWEPT_BODY",BODY,{"disambiguationData":[OSD([sQuery(id+"F1.wireOp",EDGE,"E1.bottom"),sQuery(id+"F1.wireOp",EDGE,"E1.top"),sQuery(id+"F1.wireOp",EDGE,"E1.left"),sQuery(id+"F1.wireOp",EDGE,"E1.right")])]}),"instanceName":"1"}),"instanceName":"1"}),"instanceName":"1"}),"instanceName":"1"});
            var Q15;
            Q15=makeQuery(id+"F15.opPattern","COPY",BODY,{"derivedFrom":makeQuery(id+"F13.opPattern","COPY",BODY,{"derivedFrom":makeQuery(id+"F11.opPattern","COPY",BODY,{"derivedFrom":makeQuery(id+"F6.opPattern","COPY",BODY,{"derivedFrom":makeQuery(id+"F4.opPattern","COPY",BODY,{"derivedFrom":makeQuery(id+"F2.opExtrude","SWEPT_BODY",BODY,{"disambiguationData":[OSD([sQuery(id+"F1.wireOp",EDGE,"E1.bottom"),sQuery(id+"F1.wireOp",EDGE,"E1.top"),sQuery(id+"F1.wireOp",EDGE,"E1.left"),sQuery(id+"F1.wireOp",EDGE,"E1.right")])]}),"instanceName":"1"}),"instanceName":"1"}),"instanceName":"1"}),"instanceName":"1"}),"instanceName":"1"});
            transform(context, id + "F21", {"entities" : qUnion([Q0, Q1, Q2, Q3, Q4, Q5, Q6, Q7, Q8, Q9, Q10, Q11, Q12, Q13, Q14, Q15]), "transformType" : TransformType.TRANSLATION_3D, "dx" : 0 * mm, "dy" : -25.4 * mm, "dz" : 0 * mm, "makeCopy" : false});
        }
        {
            var Q0;
            Q0=makeQuery(id+"F15.opPattern","COPY",BODY,{"derivedFrom":makeQuery(id+"F11.opPattern","COPY",BODY,{"derivedFrom":makeQuery(id+"F6.opPattern","COPY",BODY,{"derivedFrom":makeQuery(id+"F4.opPattern","COPY",BODY,{"derivedFrom":makeQuery(id+"F2.opExtrude","SWEPT_BODY",BODY,{"disambiguationData":[OSD([sQuery(id+"F1.wireOp",EDGE,"E1.bottom"),sQuery(id+"F1.wireOp",EDGE,"E1.top"),sQuery(id+"F1.wireOp",EDGE,"E1.left"),sQuery(id+"F1.wireOp",EDGE,"E1.right")])]}),"instanceName":"1"}),"instanceName":"1"}),"instanceName":"1"}),"instanceName":"1"});
            var Q1;
            Q1=makeQuery(id+"F15.opPattern","COPY",BODY,{"derivedFrom":makeQuery(id+"F11.opPattern","COPY",BODY,{"derivedFrom":makeQuery(id+"F4.opPattern","COPY",BODY,{"derivedFrom":makeQuery(id+"F2.opExtrude","SWEPT_BODY",BODY,{"disambiguationData":[OSD([sQuery(id+"F1.wireOp",EDGE,"E1.bottom"),sQuery(id+"F1.wireOp",EDGE,"E1.top"),sQuery(id+"F1.wireOp",EDGE,"E1.left"),sQuery(id+"F1.wireOp",EDGE,"E1.right")])]}),"instanceName":"1"}),"instanceName":"1"}),"instanceName":"1"});
            var Q2;
            Q2=makeQuery(id+"F15.opPattern","COPY",BODY,{"derivedFrom":makeQuery(id+"F11.opPattern","COPY",BODY,{"derivedFrom":makeQuery(id+"F6.opPattern","COPY",BODY,{"derivedFrom":makeQuery(id+"F2.opExtrude","SWEPT_BODY",BODY,{"disambiguationData":[OSD([sQuery(id+"F1.wireOp",EDGE,"E1.bottom"),sQuery(id+"F1.wireOp",EDGE,"E1.top"),sQuery(id+"F1.wireOp",EDGE,"E1.left"),sQuery(id+"F1.wireOp",EDGE,"E1.right")])]}),"instanceName":"1"}),"instanceName":"1"}),"instanceName":"1"});
            var Q3;
            Q3=makeQuery(id+"F15.opPattern","COPY",BODY,{"derivedFrom":makeQuery(id+"F11.opPattern","COPY",BODY,{"derivedFrom":makeQuery(id+"F2.opExtrude","SWEPT_BODY",BODY,{"disambiguationData":[OSD([sQuery(id+"F1.wireOp",EDGE,"E1.bottom"),sQuery(id+"F1.wireOp",EDGE,"E1.top"),sQuery(id+"F1.wireOp",EDGE,"E1.left"),sQuery(id+"F1.wireOp",EDGE,"E1.right")])]}),"instanceName":"1"}),"instanceName":"1"});
            var Q4;
            Q4=makeQuery(id+"F15.opPattern","COPY",BODY,{"derivedFrom":makeQuery(id+"F6.opPattern","COPY",BODY,{"derivedFrom":makeQuery(id+"F4.opPattern","COPY",BODY,{"derivedFrom":makeQuery(id+"F2.opExtrude","SWEPT_BODY",BODY,{"disambiguationData":[OSD([sQuery(id+"F1.wireOp",EDGE,"E1.bottom"),sQuery(id+"F1.wireOp",EDGE,"E1.top"),sQuery(id+"F1.wireOp",EDGE,"E1.left"),sQuery(id+"F1.wireOp",EDGE,"E1.right")])]}),"instanceName":"1"}),"instanceName":"1"}),"instanceName":"1"});
            var Q5;
            Q5=makeQuery(id+"F15.opPattern","COPY",BODY,{"derivedFrom":makeQuery(id+"F4.opPattern","COPY",BODY,{"derivedFrom":makeQuery(id+"F2.opExtrude","SWEPT_BODY",BODY,{"disambiguationData":[OSD([sQuery(id+"F1.wireOp",EDGE,"E1.bottom"),sQuery(id+"F1.wireOp",EDGE,"E1.top"),sQuery(id+"F1.wireOp",EDGE,"E1.left"),sQuery(id+"F1.wireOp",EDGE,"E1.right")])]}),"instanceName":"1"}),"instanceName":"1"});
            var Q6;
            Q6=makeQuery(id+"F15.opPattern","COPY",BODY,{"derivedFrom":makeQuery(id+"F6.opPattern","COPY",BODY,{"derivedFrom":makeQuery(id+"F2.opExtrude","SWEPT_BODY",BODY,{"disambiguationData":[OSD([sQuery(id+"F1.wireOp",EDGE,"E1.bottom"),sQuery(id+"F1.wireOp",EDGE,"E1.top"),sQuery(id+"F1.wireOp",EDGE,"E1.left"),sQuery(id+"F1.wireOp",EDGE,"E1.right")])]}),"instanceName":"1"}),"instanceName":"1"});
            var Q7;
            Q7=makeQuery(id+"F15.opPattern","COPY",BODY,{"derivedFrom":makeQuery(id+"F2.opExtrude","SWEPT_BODY",BODY,{"disambiguationData":[OSD([sQuery(id+"F1.wireOp",EDGE,"E1.bottom"),sQuery(id+"F1.wireOp",EDGE,"E1.top"),sQuery(id+"F1.wireOp",EDGE,"E1.left"),sQuery(id+"F1.wireOp",EDGE,"E1.right")])]}),"instanceName":"1"});
            var Q8;
            Q8=makeQuery(id+"F15.opPattern","COPY",BODY,{"derivedFrom":makeQuery(id+"F13.opPattern","COPY",BODY,{"derivedFrom":makeQuery(id+"F11.opPattern","COPY",BODY,{"derivedFrom":makeQuery(id+"F6.opPattern","COPY",BODY,{"derivedFrom":makeQuery(id+"F4.opPattern","COPY",BODY,{"derivedFrom":makeQuery(id+"F2.opExtrude","SWEPT_BODY",BODY,{"disambiguationData":[OSD([sQuery(id+"F1.wireOp",EDGE,"E1.bottom"),sQuery(id+"F1.wireOp",EDGE,"E1.top"),sQuery(id+"F1.wireOp",EDGE,"E1.left"),sQuery(id+"F1.wireOp",EDGE,"E1.right")])]}),"instanceName":"1"}),"instanceName":"1"}),"instanceName":"1"}),"instanceName":"1"}),"instanceName":"1"});
            var Q9;
            Q9=makeQuery(id+"F15.opPattern","COPY",BODY,{"derivedFrom":makeQuery(id+"F13.opPattern","COPY",BODY,{"derivedFrom":makeQuery(id+"F11.opPattern","COPY",BODY,{"derivedFrom":makeQuery(id+"F4.opPattern","COPY",BODY,{"derivedFrom":makeQuery(id+"F2.opExtrude","SWEPT_BODY",BODY,{"disambiguationData":[OSD([sQuery(id+"F1.wireOp",EDGE,"E1.bottom"),sQuery(id+"F1.wireOp",EDGE,"E1.top"),sQuery(id+"F1.wireOp",EDGE,"E1.left"),sQuery(id+"F1.wireOp",EDGE,"E1.right")])]}),"instanceName":"1"}),"instanceName":"1"}),"instanceName":"1"}),"instanceName":"1"});
            var Q10;
            Q10=makeQuery(id+"F15.opPattern","COPY",BODY,{"derivedFrom":makeQuery(id+"F13.opPattern","COPY",BODY,{"derivedFrom":makeQuery(id+"F11.opPattern","COPY",BODY,{"derivedFrom":makeQuery(id+"F6.opPattern","COPY",BODY,{"derivedFrom":makeQuery(id+"F2.opExtrude","SWEPT_BODY",BODY,{"disambiguationData":[OSD([sQuery(id+"F1.wireOp",EDGE,"E1.bottom"),sQuery(id+"F1.wireOp",EDGE,"E1.top"),sQuery(id+"F1.wireOp",EDGE,"E1.left"),sQuery(id+"F1.wireOp",EDGE,"E1.right")])]}),"instanceName":"1"}),"instanceName":"1"}),"instanceName":"1"}),"instanceName":"1"});
            var Q11;
            Q11=makeQuery(id+"F15.opPattern","COPY",BODY,{"derivedFrom":makeQuery(id+"F13.opPattern","COPY",BODY,{"derivedFrom":makeQuery(id+"F11.opPattern","COPY",BODY,{"derivedFrom":makeQuery(id+"F2.opExtrude","SWEPT_BODY",BODY,{"disambiguationData":[OSD([sQuery(id+"F1.wireOp",EDGE,"E1.bottom"),sQuery(id+"F1.wireOp",EDGE,"E1.top"),sQuery(id+"F1.wireOp",EDGE,"E1.left"),sQuery(id+"F1.wireOp",EDGE,"E1.right")])]}),"instanceName":"1"}),"instanceName":"1"}),"instanceName":"1"});
            var Q12;
            Q12=makeQuery(id+"F15.opPattern","COPY",BODY,{"derivedFrom":makeQuery(id+"F13.opPattern","COPY",BODY,{"derivedFrom":makeQuery(id+"F6.opPattern","COPY",BODY,{"derivedFrom":makeQuery(id+"F4.opPattern","COPY",BODY,{"derivedFrom":makeQuery(id+"F2.opExtrude","SWEPT_BODY",BODY,{"disambiguationData":[OSD([sQuery(id+"F1.wireOp",EDGE,"E1.bottom"),sQuery(id+"F1.wireOp",EDGE,"E1.top"),sQuery(id+"F1.wireOp",EDGE,"E1.left"),sQuery(id+"F1.wireOp",EDGE,"E1.right")])]}),"instanceName":"1"}),"instanceName":"1"}),"instanceName":"1"}),"instanceName":"1"});
            var Q13;
            Q13=makeQuery(id+"F15.opPattern","COPY",BODY,{"derivedFrom":makeQuery(id+"F13.opPattern","COPY",BODY,{"derivedFrom":makeQuery(id+"F4.opPattern","COPY",BODY,{"derivedFrom":makeQuery(id+"F2.opExtrude","SWEPT_BODY",BODY,{"disambiguationData":[OSD([sQuery(id+"F1.wireOp",EDGE,"E1.bottom"),sQuery(id+"F1.wireOp",EDGE,"E1.top"),sQuery(id+"F1.wireOp",EDGE,"E1.left"),sQuery(id+"F1.wireOp",EDGE,"E1.right")])]}),"instanceName":"1"}),"instanceName":"1"}),"instanceName":"1"});
            var Q14;
            Q14=makeQuery(id+"F15.opPattern","COPY",BODY,{"derivedFrom":makeQuery(id+"F13.opPattern","COPY",BODY,{"derivedFrom":makeQuery(id+"F6.opPattern","COPY",BODY,{"derivedFrom":makeQuery(id+"F2.opExtrude","SWEPT_BODY",BODY,{"disambiguationData":[OSD([sQuery(id+"F1.wireOp",EDGE,"E1.bottom"),sQuery(id+"F1.wireOp",EDGE,"E1.top"),sQuery(id+"F1.wireOp",EDGE,"E1.left"),sQuery(id+"F1.wireOp",EDGE,"E1.right")])]}),"instanceName":"1"}),"instanceName":"1"}),"instanceName":"1"});
            var Q15;
            Q15=makeQuery(id+"F15.opPattern","COPY",BODY,{"derivedFrom":makeQuery(id+"F13.opPattern","COPY",BODY,{"derivedFrom":makeQuery(id+"F2.opExtrude","SWEPT_BODY",BODY,{"disambiguationData":[OSD([sQuery(id+"F1.wireOp",EDGE,"E1.bottom"),sQuery(id+"F1.wireOp",EDGE,"E1.top"),sQuery(id+"F1.wireOp",EDGE,"E1.left"),sQuery(id+"F1.wireOp",EDGE,"E1.right")])]}),"instanceName":"1"}),"instanceName":"1"});
            transform(context, id + "F22", {"entities" : qUnion([Q0, Q1, Q2, Q3, Q4, Q5, Q6, Q7, Q8, Q9, Q10, Q11, Q12, Q13, Q14, Q15]), "transformType" : TransformType.COPY});
        }
        {
            var Q0;
            Q0=makeQuery(id+"F15.opPattern","COPY",BODY,{"derivedFrom":makeQuery(id+"F11.opPattern","COPY",BODY,{"derivedFrom":makeQuery(id+"F6.opPattern","COPY",BODY,{"derivedFrom":makeQuery(id+"F4.opPattern","COPY",BODY,{"derivedFrom":makeQuery(id+"F2.opExtrude","SWEPT_BODY",BODY,{"disambiguationData":[OSD([sQuery(id+"F1.wireOp",EDGE,"E1.bottom"),sQuery(id+"F1.wireOp",EDGE,"E1.top"),sQuery(id+"F1.wireOp",EDGE,"E1.left"),sQuery(id+"F1.wireOp",EDGE,"E1.right")])]}),"instanceName":"1"}),"instanceName":"1"}),"instanceName":"1"}),"instanceName":"1"});
            var Q1;
            Q1=makeQuery(id+"F15.opPattern","COPY",BODY,{"derivedFrom":makeQuery(id+"F13.opPattern","COPY",BODY,{"derivedFrom":makeQuery(id+"F2.opExtrude","SWEPT_BODY",BODY,{"disambiguationData":[OSD([sQuery(id+"F1.wireOp",EDGE,"E1.bottom"),sQuery(id+"F1.wireOp",EDGE,"E1.top"),sQuery(id+"F1.wireOp",EDGE,"E1.left"),sQuery(id+"F1.wireOp",EDGE,"E1.right")])]}),"instanceName":"1"}),"instanceName":"1"});
            var Q2;
            Q2=makeQuery(id+"F15.opPattern","COPY",BODY,{"derivedFrom":makeQuery(id+"F13.opPattern","COPY",BODY,{"derivedFrom":makeQuery(id+"F6.opPattern","COPY",BODY,{"derivedFrom":makeQuery(id+"F2.opExtrude","SWEPT_BODY",BODY,{"disambiguationData":[OSD([sQuery(id+"F1.wireOp",EDGE,"E1.bottom"),sQuery(id+"F1.wireOp",EDGE,"E1.top"),sQuery(id+"F1.wireOp",EDGE,"E1.left"),sQuery(id+"F1.wireOp",EDGE,"E1.right")])]}),"instanceName":"1"}),"instanceName":"1"}),"instanceName":"1"});
            var Q3;
            Q3=makeQuery(id+"F15.opPattern","COPY",BODY,{"derivedFrom":makeQuery(id+"F13.opPattern","COPY",BODY,{"derivedFrom":makeQuery(id+"F4.opPattern","COPY",BODY,{"derivedFrom":makeQuery(id+"F2.opExtrude","SWEPT_BODY",BODY,{"disambiguationData":[OSD([sQuery(id+"F1.wireOp",EDGE,"E1.bottom"),sQuery(id+"F1.wireOp",EDGE,"E1.top"),sQuery(id+"F1.wireOp",EDGE,"E1.left"),sQuery(id+"F1.wireOp",EDGE,"E1.right")])]}),"instanceName":"1"}),"instanceName":"1"}),"instanceName":"1"});
            var Q4;
            Q4=makeQuery(id+"F15.opPattern","COPY",BODY,{"derivedFrom":makeQuery(id+"F13.opPattern","COPY",BODY,{"derivedFrom":makeQuery(id+"F6.opPattern","COPY",BODY,{"derivedFrom":makeQuery(id+"F4.opPattern","COPY",BODY,{"derivedFrom":makeQuery(id+"F2.opExtrude","SWEPT_BODY",BODY,{"disambiguationData":[OSD([sQuery(id+"F1.wireOp",EDGE,"E1.bottom"),sQuery(id+"F1.wireOp",EDGE,"E1.top"),sQuery(id+"F1.wireOp",EDGE,"E1.left"),sQuery(id+"F1.wireOp",EDGE,"E1.right")])]}),"instanceName":"1"}),"instanceName":"1"}),"instanceName":"1"}),"instanceName":"1"});
            var Q5;
            Q5=makeQuery(id+"F15.opPattern","COPY",BODY,{"derivedFrom":makeQuery(id+"F11.opPattern","COPY",BODY,{"derivedFrom":makeQuery(id+"F4.opPattern","COPY",BODY,{"derivedFrom":makeQuery(id+"F2.opExtrude","SWEPT_BODY",BODY,{"disambiguationData":[OSD([sQuery(id+"F1.wireOp",EDGE,"E1.bottom"),sQuery(id+"F1.wireOp",EDGE,"E1.top"),sQuery(id+"F1.wireOp",EDGE,"E1.left"),sQuery(id+"F1.wireOp",EDGE,"E1.right")])]}),"instanceName":"1"}),"instanceName":"1"}),"instanceName":"1"});
            var Q6;
            Q6=makeQuery(id+"F15.opPattern","COPY",BODY,{"derivedFrom":makeQuery(id+"F11.opPattern","COPY",BODY,{"derivedFrom":makeQuery(id+"F6.opPattern","COPY",BODY,{"derivedFrom":makeQuery(id+"F2.opExtrude","SWEPT_BODY",BODY,{"disambiguationData":[OSD([sQuery(id+"F1.wireOp",EDGE,"E1.bottom"),sQuery(id+"F1.wireOp",EDGE,"E1.top"),sQuery(id+"F1.wireOp",EDGE,"E1.left"),sQuery(id+"F1.wireOp",EDGE,"E1.right")])]}),"instanceName":"1"}),"instanceName":"1"}),"instanceName":"1"});
            var Q7;
            Q7=makeQuery(id+"F15.opPattern","COPY",BODY,{"derivedFrom":makeQuery(id+"F11.opPattern","COPY",BODY,{"derivedFrom":makeQuery(id+"F2.opExtrude","SWEPT_BODY",BODY,{"disambiguationData":[OSD([sQuery(id+"F1.wireOp",EDGE,"E1.bottom"),sQuery(id+"F1.wireOp",EDGE,"E1.top"),sQuery(id+"F1.wireOp",EDGE,"E1.left"),sQuery(id+"F1.wireOp",EDGE,"E1.right")])]}),"instanceName":"1"}),"instanceName":"1"});
            var Q8;
            Q8=makeQuery(id+"F15.opPattern","COPY",BODY,{"derivedFrom":makeQuery(id+"F6.opPattern","COPY",BODY,{"derivedFrom":makeQuery(id+"F4.opPattern","COPY",BODY,{"derivedFrom":makeQuery(id+"F2.opExtrude","SWEPT_BODY",BODY,{"disambiguationData":[OSD([sQuery(id+"F1.wireOp",EDGE,"E1.bottom"),sQuery(id+"F1.wireOp",EDGE,"E1.top"),sQuery(id+"F1.wireOp",EDGE,"E1.left"),sQuery(id+"F1.wireOp",EDGE,"E1.right")])]}),"instanceName":"1"}),"instanceName":"1"}),"instanceName":"1"});
            var Q9;
            Q9=makeQuery(id+"F15.opPattern","COPY",BODY,{"derivedFrom":makeQuery(id+"F4.opPattern","COPY",BODY,{"derivedFrom":makeQuery(id+"F2.opExtrude","SWEPT_BODY",BODY,{"disambiguationData":[OSD([sQuery(id+"F1.wireOp",EDGE,"E1.bottom"),sQuery(id+"F1.wireOp",EDGE,"E1.top"),sQuery(id+"F1.wireOp",EDGE,"E1.left"),sQuery(id+"F1.wireOp",EDGE,"E1.right")])]}),"instanceName":"1"}),"instanceName":"1"});
            var Q10;
            Q10=makeQuery(id+"F15.opPattern","COPY",BODY,{"derivedFrom":makeQuery(id+"F6.opPattern","COPY",BODY,{"derivedFrom":makeQuery(id+"F2.opExtrude","SWEPT_BODY",BODY,{"disambiguationData":[OSD([sQuery(id+"F1.wireOp",EDGE,"E1.bottom"),sQuery(id+"F1.wireOp",EDGE,"E1.top"),sQuery(id+"F1.wireOp",EDGE,"E1.left"),sQuery(id+"F1.wireOp",EDGE,"E1.right")])]}),"instanceName":"1"}),"instanceName":"1"});
            var Q11;
            Q11=makeQuery(id+"F15.opPattern","COPY",BODY,{"derivedFrom":makeQuery(id+"F2.opExtrude","SWEPT_BODY",BODY,{"disambiguationData":[OSD([sQuery(id+"F1.wireOp",EDGE,"E1.bottom"),sQuery(id+"F1.wireOp",EDGE,"E1.top"),sQuery(id+"F1.wireOp",EDGE,"E1.left"),sQuery(id+"F1.wireOp",EDGE,"E1.right")])]}),"instanceName":"1"});
            var Q12;
            Q12=makeQuery(id+"F15.opPattern","COPY",BODY,{"derivedFrom":makeQuery(id+"F13.opPattern","COPY",BODY,{"derivedFrom":makeQuery(id+"F11.opPattern","COPY",BODY,{"derivedFrom":makeQuery(id+"F6.opPattern","COPY",BODY,{"derivedFrom":makeQuery(id+"F4.opPattern","COPY",BODY,{"derivedFrom":makeQuery(id+"F2.opExtrude","SWEPT_BODY",BODY,{"disambiguationData":[OSD([sQuery(id+"F1.wireOp",EDGE,"E1.bottom"),sQuery(id+"F1.wireOp",EDGE,"E1.top"),sQuery(id+"F1.wireOp",EDGE,"E1.left"),sQuery(id+"F1.wireOp",EDGE,"E1.right")])]}),"instanceName":"1"}),"instanceName":"1"}),"instanceName":"1"}),"instanceName":"1"}),"instanceName":"1"});
            var Q13;
            Q13=makeQuery(id+"F15.opPattern","COPY",BODY,{"derivedFrom":makeQuery(id+"F13.opPattern","COPY",BODY,{"derivedFrom":makeQuery(id+"F11.opPattern","COPY",BODY,{"derivedFrom":makeQuery(id+"F4.opPattern","COPY",BODY,{"derivedFrom":makeQuery(id+"F2.opExtrude","SWEPT_BODY",BODY,{"disambiguationData":[OSD([sQuery(id+"F1.wireOp",EDGE,"E1.bottom"),sQuery(id+"F1.wireOp",EDGE,"E1.top"),sQuery(id+"F1.wireOp",EDGE,"E1.left"),sQuery(id+"F1.wireOp",EDGE,"E1.right")])]}),"instanceName":"1"}),"instanceName":"1"}),"instanceName":"1"}),"instanceName":"1"});
            var Q14;
            Q14=makeQuery(id+"F15.opPattern","COPY",BODY,{"derivedFrom":makeQuery(id+"F13.opPattern","COPY",BODY,{"derivedFrom":makeQuery(id+"F11.opPattern","COPY",BODY,{"derivedFrom":makeQuery(id+"F6.opPattern","COPY",BODY,{"derivedFrom":makeQuery(id+"F2.opExtrude","SWEPT_BODY",BODY,{"disambiguationData":[OSD([sQuery(id+"F1.wireOp",EDGE,"E1.bottom"),sQuery(id+"F1.wireOp",EDGE,"E1.top"),sQuery(id+"F1.wireOp",EDGE,"E1.left"),sQuery(id+"F1.wireOp",EDGE,"E1.right")])]}),"instanceName":"1"}),"instanceName":"1"}),"instanceName":"1"}),"instanceName":"1"});
            var Q15;
            Q15=makeQuery(id+"F15.opPattern","COPY",BODY,{"derivedFrom":makeQuery(id+"F13.opPattern","COPY",BODY,{"derivedFrom":makeQuery(id+"F11.opPattern","COPY",BODY,{"derivedFrom":makeQuery(id+"F2.opExtrude","SWEPT_BODY",BODY,{"disambiguationData":[OSD([sQuery(id+"F1.wireOp",EDGE,"E1.bottom"),sQuery(id+"F1.wireOp",EDGE,"E1.top"),sQuery(id+"F1.wireOp",EDGE,"E1.left"),sQuery(id+"F1.wireOp",EDGE,"E1.right")])]}),"instanceName":"1"}),"instanceName":"1"}),"instanceName":"1"});
            transform(context, id + "F23", {"entities" : qUnion([Q0, Q1, Q2, Q3, Q4, Q5, Q6, Q7, Q8, Q9, Q10, Q11, Q12, Q13, Q14, Q15]), "transformType" : TransformType.TRANSLATION_3D, "dx" : 0 * mm, "dy" : -25.4 * mm, "dz" : 0 * mm, "makeCopy" : false});
        }
        {
            var Q0;
            Q0=makeQuery(id+"F22.opPattern","COPY",BODY,{"derivedFrom":makeQuery(id+"F15.opPattern","COPY",BODY,{"derivedFrom":makeQuery(id+"F11.opPattern","COPY",BODY,{"derivedFrom":makeQuery(id+"F6.opPattern","COPY",BODY,{"derivedFrom":makeQuery(id+"F4.opPattern","COPY",BODY,{"derivedFrom":makeQuery(id+"F2.opExtrude","SWEPT_BODY",BODY,{"disambiguationData":[OSD([sQuery(id+"F1.wireOp",EDGE,"E1.bottom"),sQuery(id+"F1.wireOp",EDGE,"E1.top"),sQuery(id+"F1.wireOp",EDGE,"E1.left"),sQuery(id+"F1.wireOp",EDGE,"E1.right")])]}),"instanceName":"1"}),"instanceName":"1"}),"instanceName":"1"}),"instanceName":"1"}),"instanceName":"1"});
            var Q1;
            Q1=makeQuery(id+"F22.opPattern","COPY",BODY,{"derivedFrom":makeQuery(id+"F15.opPattern","COPY",BODY,{"derivedFrom":makeQuery(id+"F11.opPattern","COPY",BODY,{"derivedFrom":makeQuery(id+"F4.opPattern","COPY",BODY,{"derivedFrom":makeQuery(id+"F2.opExtrude","SWEPT_BODY",BODY,{"disambiguationData":[OSD([sQuery(id+"F1.wireOp",EDGE,"E1.bottom"),sQuery(id+"F1.wireOp",EDGE,"E1.top"),sQuery(id+"F1.wireOp",EDGE,"E1.left"),sQuery(id+"F1.wireOp",EDGE,"E1.right")])]}),"instanceName":"1"}),"instanceName":"1"}),"instanceName":"1"}),"instanceName":"1"});
            var Q2;
            Q2=makeQuery(id+"F22.opPattern","COPY",BODY,{"derivedFrom":makeQuery(id+"F15.opPattern","COPY",BODY,{"derivedFrom":makeQuery(id+"F11.opPattern","COPY",BODY,{"derivedFrom":makeQuery(id+"F6.opPattern","COPY",BODY,{"derivedFrom":makeQuery(id+"F2.opExtrude","SWEPT_BODY",BODY,{"disambiguationData":[OSD([sQuery(id+"F1.wireOp",EDGE,"E1.bottom"),sQuery(id+"F1.wireOp",EDGE,"E1.top"),sQuery(id+"F1.wireOp",EDGE,"E1.left"),sQuery(id+"F1.wireOp",EDGE,"E1.right")])]}),"instanceName":"1"}),"instanceName":"1"}),"instanceName":"1"}),"instanceName":"1"});
            var Q3;
            Q3=makeQuery(id+"F22.opPattern","COPY",BODY,{"derivedFrom":makeQuery(id+"F15.opPattern","COPY",BODY,{"derivedFrom":makeQuery(id+"F11.opPattern","COPY",BODY,{"derivedFrom":makeQuery(id+"F2.opExtrude","SWEPT_BODY",BODY,{"disambiguationData":[OSD([sQuery(id+"F1.wireOp",EDGE,"E1.bottom"),sQuery(id+"F1.wireOp",EDGE,"E1.top"),sQuery(id+"F1.wireOp",EDGE,"E1.left"),sQuery(id+"F1.wireOp",EDGE,"E1.right")])]}),"instanceName":"1"}),"instanceName":"1"}),"instanceName":"1"});
            var Q4;
            Q4=makeQuery(id+"F22.opPattern","COPY",BODY,{"derivedFrom":makeQuery(id+"F15.opPattern","COPY",BODY,{"derivedFrom":makeQuery(id+"F6.opPattern","COPY",BODY,{"derivedFrom":makeQuery(id+"F4.opPattern","COPY",BODY,{"derivedFrom":makeQuery(id+"F2.opExtrude","SWEPT_BODY",BODY,{"disambiguationData":[OSD([sQuery(id+"F1.wireOp",EDGE,"E1.bottom"),sQuery(id+"F1.wireOp",EDGE,"E1.top"),sQuery(id+"F1.wireOp",EDGE,"E1.left"),sQuery(id+"F1.wireOp",EDGE,"E1.right")])]}),"instanceName":"1"}),"instanceName":"1"}),"instanceName":"1"}),"instanceName":"1"});
            var Q5;
            Q5=makeQuery(id+"F22.opPattern","COPY",BODY,{"derivedFrom":makeQuery(id+"F15.opPattern","COPY",BODY,{"derivedFrom":makeQuery(id+"F4.opPattern","COPY",BODY,{"derivedFrom":makeQuery(id+"F2.opExtrude","SWEPT_BODY",BODY,{"disambiguationData":[OSD([sQuery(id+"F1.wireOp",EDGE,"E1.bottom"),sQuery(id+"F1.wireOp",EDGE,"E1.top"),sQuery(id+"F1.wireOp",EDGE,"E1.left"),sQuery(id+"F1.wireOp",EDGE,"E1.right")])]}),"instanceName":"1"}),"instanceName":"1"}),"instanceName":"1"});
            var Q6;
            Q6=makeQuery(id+"F22.opPattern","COPY",BODY,{"derivedFrom":makeQuery(id+"F15.opPattern","COPY",BODY,{"derivedFrom":makeQuery(id+"F6.opPattern","COPY",BODY,{"derivedFrom":makeQuery(id+"F2.opExtrude","SWEPT_BODY",BODY,{"disambiguationData":[OSD([sQuery(id+"F1.wireOp",EDGE,"E1.bottom"),sQuery(id+"F1.wireOp",EDGE,"E1.top"),sQuery(id+"F1.wireOp",EDGE,"E1.left"),sQuery(id+"F1.wireOp",EDGE,"E1.right")])]}),"instanceName":"1"}),"instanceName":"1"}),"instanceName":"1"});
            var Q7;
            Q7=makeQuery(id+"F22.opPattern","COPY",BODY,{"derivedFrom":makeQuery(id+"F15.opPattern","COPY",BODY,{"derivedFrom":makeQuery(id+"F2.opExtrude","SWEPT_BODY",BODY,{"disambiguationData":[OSD([sQuery(id+"F1.wireOp",EDGE,"E1.bottom"),sQuery(id+"F1.wireOp",EDGE,"E1.top"),sQuery(id+"F1.wireOp",EDGE,"E1.left"),sQuery(id+"F1.wireOp",EDGE,"E1.right")])]}),"instanceName":"1"}),"instanceName":"1"});
            var Q8;
            Q8=makeQuery(id+"F22.opPattern","COPY",BODY,{"derivedFrom":makeQuery(id+"F15.opPattern","COPY",BODY,{"derivedFrom":makeQuery(id+"F13.opPattern","COPY",BODY,{"derivedFrom":makeQuery(id+"F11.opPattern","COPY",BODY,{"derivedFrom":makeQuery(id+"F6.opPattern","COPY",BODY,{"derivedFrom":makeQuery(id+"F4.opPattern","COPY",BODY,{"derivedFrom":makeQuery(id+"F2.opExtrude","SWEPT_BODY",BODY,{"disambiguationData":[OSD([sQuery(id+"F1.wireOp",EDGE,"E1.bottom"),sQuery(id+"F1.wireOp",EDGE,"E1.top"),sQuery(id+"F1.wireOp",EDGE,"E1.left"),sQuery(id+"F1.wireOp",EDGE,"E1.right")])]}),"instanceName":"1"}),"instanceName":"1"}),"instanceName":"1"}),"instanceName":"1"}),"instanceName":"1"}),"instanceName":"1"});
            var Q9;
            Q9=makeQuery(id+"F22.opPattern","COPY",BODY,{"derivedFrom":makeQuery(id+"F15.opPattern","COPY",BODY,{"derivedFrom":makeQuery(id+"F13.opPattern","COPY",BODY,{"derivedFrom":makeQuery(id+"F11.opPattern","COPY",BODY,{"derivedFrom":makeQuery(id+"F4.opPattern","COPY",BODY,{"derivedFrom":makeQuery(id+"F2.opExtrude","SWEPT_BODY",BODY,{"disambiguationData":[OSD([sQuery(id+"F1.wireOp",EDGE,"E1.bottom"),sQuery(id+"F1.wireOp",EDGE,"E1.top"),sQuery(id+"F1.wireOp",EDGE,"E1.left"),sQuery(id+"F1.wireOp",EDGE,"E1.right")])]}),"instanceName":"1"}),"instanceName":"1"}),"instanceName":"1"}),"instanceName":"1"}),"instanceName":"1"});
            var Q10;
            Q10=makeQuery(id+"F22.opPattern","COPY",BODY,{"derivedFrom":makeQuery(id+"F15.opPattern","COPY",BODY,{"derivedFrom":makeQuery(id+"F13.opPattern","COPY",BODY,{"derivedFrom":makeQuery(id+"F11.opPattern","COPY",BODY,{"derivedFrom":makeQuery(id+"F6.opPattern","COPY",BODY,{"derivedFrom":makeQuery(id+"F2.opExtrude","SWEPT_BODY",BODY,{"disambiguationData":[OSD([sQuery(id+"F1.wireOp",EDGE,"E1.bottom"),sQuery(id+"F1.wireOp",EDGE,"E1.top"),sQuery(id+"F1.wireOp",EDGE,"E1.left"),sQuery(id+"F1.wireOp",EDGE,"E1.right")])]}),"instanceName":"1"}),"instanceName":"1"}),"instanceName":"1"}),"instanceName":"1"}),"instanceName":"1"});
            var Q11;
            Q11=makeQuery(id+"F22.opPattern","COPY",BODY,{"derivedFrom":makeQuery(id+"F15.opPattern","COPY",BODY,{"derivedFrom":makeQuery(id+"F13.opPattern","COPY",BODY,{"derivedFrom":makeQuery(id+"F11.opPattern","COPY",BODY,{"derivedFrom":makeQuery(id+"F2.opExtrude","SWEPT_BODY",BODY,{"disambiguationData":[OSD([sQuery(id+"F1.wireOp",EDGE,"E1.bottom"),sQuery(id+"F1.wireOp",EDGE,"E1.top"),sQuery(id+"F1.wireOp",EDGE,"E1.left"),sQuery(id+"F1.wireOp",EDGE,"E1.right")])]}),"instanceName":"1"}),"instanceName":"1"}),"instanceName":"1"}),"instanceName":"1"});
            var Q12;
            Q12=makeQuery(id+"F22.opPattern","COPY",BODY,{"derivedFrom":makeQuery(id+"F15.opPattern","COPY",BODY,{"derivedFrom":makeQuery(id+"F13.opPattern","COPY",BODY,{"derivedFrom":makeQuery(id+"F6.opPattern","COPY",BODY,{"derivedFrom":makeQuery(id+"F4.opPattern","COPY",BODY,{"derivedFrom":makeQuery(id+"F2.opExtrude","SWEPT_BODY",BODY,{"disambiguationData":[OSD([sQuery(id+"F1.wireOp",EDGE,"E1.bottom"),sQuery(id+"F1.wireOp",EDGE,"E1.top"),sQuery(id+"F1.wireOp",EDGE,"E1.left"),sQuery(id+"F1.wireOp",EDGE,"E1.right")])]}),"instanceName":"1"}),"instanceName":"1"}),"instanceName":"1"}),"instanceName":"1"}),"instanceName":"1"});
            var Q13;
            Q13=makeQuery(id+"F22.opPattern","COPY",BODY,{"derivedFrom":makeQuery(id+"F15.opPattern","COPY",BODY,{"derivedFrom":makeQuery(id+"F13.opPattern","COPY",BODY,{"derivedFrom":makeQuery(id+"F4.opPattern","COPY",BODY,{"derivedFrom":makeQuery(id+"F2.opExtrude","SWEPT_BODY",BODY,{"disambiguationData":[OSD([sQuery(id+"F1.wireOp",EDGE,"E1.bottom"),sQuery(id+"F1.wireOp",EDGE,"E1.top"),sQuery(id+"F1.wireOp",EDGE,"E1.left"),sQuery(id+"F1.wireOp",EDGE,"E1.right")])]}),"instanceName":"1"}),"instanceName":"1"}),"instanceName":"1"}),"instanceName":"1"});
            var Q14;
            Q14=makeQuery(id+"F22.opPattern","COPY",BODY,{"derivedFrom":makeQuery(id+"F15.opPattern","COPY",BODY,{"derivedFrom":makeQuery(id+"F13.opPattern","COPY",BODY,{"derivedFrom":makeQuery(id+"F6.opPattern","COPY",BODY,{"derivedFrom":makeQuery(id+"F2.opExtrude","SWEPT_BODY",BODY,{"disambiguationData":[OSD([sQuery(id+"F1.wireOp",EDGE,"E1.bottom"),sQuery(id+"F1.wireOp",EDGE,"E1.top"),sQuery(id+"F1.wireOp",EDGE,"E1.left"),sQuery(id+"F1.wireOp",EDGE,"E1.right")])]}),"instanceName":"1"}),"instanceName":"1"}),"instanceName":"1"}),"instanceName":"1"});
            var Q15;
            Q15=makeQuery(id+"F22.opPattern","COPY",BODY,{"derivedFrom":makeQuery(id+"F15.opPattern","COPY",BODY,{"derivedFrom":makeQuery(id+"F13.opPattern","COPY",BODY,{"derivedFrom":makeQuery(id+"F2.opExtrude","SWEPT_BODY",BODY,{"disambiguationData":[OSD([sQuery(id+"F1.wireOp",EDGE,"E1.bottom"),sQuery(id+"F1.wireOp",EDGE,"E1.top"),sQuery(id+"F1.wireOp",EDGE,"E1.left"),sQuery(id+"F1.wireOp",EDGE,"E1.right")])]}),"instanceName":"1"}),"instanceName":"1"}),"instanceName":"1"});
            var Q16;
            Q16=makeQuery(id+"F20.opPattern","COPY",EDGE,{"derivedFrom":makeQuery(id+"F15.opPattern","COPY",EDGE,{"derivedFrom":makeQuery(id+"F11.opPattern","COPY",EDGE,{"derivedFrom":makeQuery(id+"F6.opPattern","COPY",EDGE,{"derivedFrom":makeQuery(id+"F4.opPattern","COPY",EDGE,{"derivedFrom":makeQuery(id+"F2.opExtrude","SWEPT_EDGE",EDGE,{"disambiguationData":[OSD([sQuery(id+"F1.wireOp",EDGE,"E1.top"),sQuery(id+"F1.wireOp",EDGE,"E1.left")])]}),"instanceName":"1"}),"instanceName":"1"}),"instanceName":"1"}),"instanceName":"1"}),"instanceName":"1"});
            transform(context, id + "F24", {"entities" : qUnion([Q0, Q1, Q2, Q3, Q4, Q5, Q6, Q7, Q8, Q9, Q10, Q11, Q12, Q13, Q14, Q15]), "transformType" : TransformType.ROTATION, "transformAxis" : qUnion([Q16]), "angle" : 90 * degree, "makeCopy" : false});
        }
        {
            var Q0;
            Q0=makeQuery(id+"F15.opPattern","COPY",BODY,{"derivedFrom":makeQuery(id+"F11.opPattern","COPY",BODY,{"derivedFrom":makeQuery(id+"F6.opPattern","COPY",BODY,{"derivedFrom":makeQuery(id+"F4.opPattern","COPY",BODY,{"derivedFrom":makeQuery(id+"F2.opExtrude","SWEPT_BODY",BODY,{"disambiguationData":[OSD([sQuery(id+"F1.wireOp",EDGE,"E1.bottom"),sQuery(id+"F1.wireOp",EDGE,"E1.top"),sQuery(id+"F1.wireOp",EDGE,"E1.left"),sQuery(id+"F1.wireOp",EDGE,"E1.right")])]}),"instanceName":"1"}),"instanceName":"1"}),"instanceName":"1"}),"instanceName":"1"});
            var Q1;
            Q1=makeQuery(id+"F15.opPattern","COPY",BODY,{"derivedFrom":makeQuery(id+"F11.opPattern","COPY",BODY,{"derivedFrom":makeQuery(id+"F4.opPattern","COPY",BODY,{"derivedFrom":makeQuery(id+"F2.opExtrude","SWEPT_BODY",BODY,{"disambiguationData":[OSD([sQuery(id+"F1.wireOp",EDGE,"E1.bottom"),sQuery(id+"F1.wireOp",EDGE,"E1.top"),sQuery(id+"F1.wireOp",EDGE,"E1.left"),sQuery(id+"F1.wireOp",EDGE,"E1.right")])]}),"instanceName":"1"}),"instanceName":"1"}),"instanceName":"1"});
            var Q2;
            Q2=makeQuery(id+"F15.opPattern","COPY",BODY,{"derivedFrom":makeQuery(id+"F11.opPattern","COPY",BODY,{"derivedFrom":makeQuery(id+"F6.opPattern","COPY",BODY,{"derivedFrom":makeQuery(id+"F2.opExtrude","SWEPT_BODY",BODY,{"disambiguationData":[OSD([sQuery(id+"F1.wireOp",EDGE,"E1.bottom"),sQuery(id+"F1.wireOp",EDGE,"E1.top"),sQuery(id+"F1.wireOp",EDGE,"E1.left"),sQuery(id+"F1.wireOp",EDGE,"E1.right")])]}),"instanceName":"1"}),"instanceName":"1"}),"instanceName":"1"});
            var Q3;
            Q3=makeQuery(id+"F15.opPattern","COPY",BODY,{"derivedFrom":makeQuery(id+"F11.opPattern","COPY",BODY,{"derivedFrom":makeQuery(id+"F2.opExtrude","SWEPT_BODY",BODY,{"disambiguationData":[OSD([sQuery(id+"F1.wireOp",EDGE,"E1.bottom"),sQuery(id+"F1.wireOp",EDGE,"E1.top"),sQuery(id+"F1.wireOp",EDGE,"E1.left"),sQuery(id+"F1.wireOp",EDGE,"E1.right")])]}),"instanceName":"1"}),"instanceName":"1"});
            var Q4;
            Q4=makeQuery(id+"F15.opPattern","COPY",BODY,{"derivedFrom":makeQuery(id+"F6.opPattern","COPY",BODY,{"derivedFrom":makeQuery(id+"F4.opPattern","COPY",BODY,{"derivedFrom":makeQuery(id+"F2.opExtrude","SWEPT_BODY",BODY,{"disambiguationData":[OSD([sQuery(id+"F1.wireOp",EDGE,"E1.bottom"),sQuery(id+"F1.wireOp",EDGE,"E1.top"),sQuery(id+"F1.wireOp",EDGE,"E1.left"),sQuery(id+"F1.wireOp",EDGE,"E1.right")])]}),"instanceName":"1"}),"instanceName":"1"}),"instanceName":"1"});
            var Q5;
            Q5=makeQuery(id+"F15.opPattern","COPY",BODY,{"derivedFrom":makeQuery(id+"F4.opPattern","COPY",BODY,{"derivedFrom":makeQuery(id+"F2.opExtrude","SWEPT_BODY",BODY,{"disambiguationData":[OSD([sQuery(id+"F1.wireOp",EDGE,"E1.bottom"),sQuery(id+"F1.wireOp",EDGE,"E1.top"),sQuery(id+"F1.wireOp",EDGE,"E1.left"),sQuery(id+"F1.wireOp",EDGE,"E1.right")])]}),"instanceName":"1"}),"instanceName":"1"});
            var Q6;
            Q6=makeQuery(id+"F15.opPattern","COPY",BODY,{"derivedFrom":makeQuery(id+"F6.opPattern","COPY",BODY,{"derivedFrom":makeQuery(id+"F2.opExtrude","SWEPT_BODY",BODY,{"disambiguationData":[OSD([sQuery(id+"F1.wireOp",EDGE,"E1.bottom"),sQuery(id+"F1.wireOp",EDGE,"E1.top"),sQuery(id+"F1.wireOp",EDGE,"E1.left"),sQuery(id+"F1.wireOp",EDGE,"E1.right")])]}),"instanceName":"1"}),"instanceName":"1"});
            var Q7;
            Q7=makeQuery(id+"F15.opPattern","COPY",BODY,{"derivedFrom":makeQuery(id+"F2.opExtrude","SWEPT_BODY",BODY,{"disambiguationData":[OSD([sQuery(id+"F1.wireOp",EDGE,"E1.bottom"),sQuery(id+"F1.wireOp",EDGE,"E1.top"),sQuery(id+"F1.wireOp",EDGE,"E1.left"),sQuery(id+"F1.wireOp",EDGE,"E1.right")])]}),"instanceName":"1"});
            var Q8;
            Q8=makeQuery(id+"F15.opPattern","COPY",BODY,{"derivedFrom":makeQuery(id+"F13.opPattern","COPY",BODY,{"derivedFrom":makeQuery(id+"F11.opPattern","COPY",BODY,{"derivedFrom":makeQuery(id+"F6.opPattern","COPY",BODY,{"derivedFrom":makeQuery(id+"F4.opPattern","COPY",BODY,{"derivedFrom":makeQuery(id+"F2.opExtrude","SWEPT_BODY",BODY,{"disambiguationData":[OSD([sQuery(id+"F1.wireOp",EDGE,"E1.bottom"),sQuery(id+"F1.wireOp",EDGE,"E1.top"),sQuery(id+"F1.wireOp",EDGE,"E1.left"),sQuery(id+"F1.wireOp",EDGE,"E1.right")])]}),"instanceName":"1"}),"instanceName":"1"}),"instanceName":"1"}),"instanceName":"1"}),"instanceName":"1"});
            var Q9;
            Q9=makeQuery(id+"F15.opPattern","COPY",BODY,{"derivedFrom":makeQuery(id+"F13.opPattern","COPY",BODY,{"derivedFrom":makeQuery(id+"F11.opPattern","COPY",BODY,{"derivedFrom":makeQuery(id+"F4.opPattern","COPY",BODY,{"derivedFrom":makeQuery(id+"F2.opExtrude","SWEPT_BODY",BODY,{"disambiguationData":[OSD([sQuery(id+"F1.wireOp",EDGE,"E1.bottom"),sQuery(id+"F1.wireOp",EDGE,"E1.top"),sQuery(id+"F1.wireOp",EDGE,"E1.left"),sQuery(id+"F1.wireOp",EDGE,"E1.right")])]}),"instanceName":"1"}),"instanceName":"1"}),"instanceName":"1"}),"instanceName":"1"});
            var Q10;
            Q10=makeQuery(id+"F15.opPattern","COPY",BODY,{"derivedFrom":makeQuery(id+"F13.opPattern","COPY",BODY,{"derivedFrom":makeQuery(id+"F11.opPattern","COPY",BODY,{"derivedFrom":makeQuery(id+"F6.opPattern","COPY",BODY,{"derivedFrom":makeQuery(id+"F2.opExtrude","SWEPT_BODY",BODY,{"disambiguationData":[OSD([sQuery(id+"F1.wireOp",EDGE,"E1.bottom"),sQuery(id+"F1.wireOp",EDGE,"E1.top"),sQuery(id+"F1.wireOp",EDGE,"E1.left"),sQuery(id+"F1.wireOp",EDGE,"E1.right")])]}),"instanceName":"1"}),"instanceName":"1"}),"instanceName":"1"}),"instanceName":"1"});
            var Q11;
            Q11=makeQuery(id+"F15.opPattern","COPY",BODY,{"derivedFrom":makeQuery(id+"F13.opPattern","COPY",BODY,{"derivedFrom":makeQuery(id+"F11.opPattern","COPY",BODY,{"derivedFrom":makeQuery(id+"F2.opExtrude","SWEPT_BODY",BODY,{"disambiguationData":[OSD([sQuery(id+"F1.wireOp",EDGE,"E1.bottom"),sQuery(id+"F1.wireOp",EDGE,"E1.top"),sQuery(id+"F1.wireOp",EDGE,"E1.left"),sQuery(id+"F1.wireOp",EDGE,"E1.right")])]}),"instanceName":"1"}),"instanceName":"1"}),"instanceName":"1"});
            var Q12;
            Q12=makeQuery(id+"F15.opPattern","COPY",BODY,{"derivedFrom":makeQuery(id+"F13.opPattern","COPY",BODY,{"derivedFrom":makeQuery(id+"F6.opPattern","COPY",BODY,{"derivedFrom":makeQuery(id+"F4.opPattern","COPY",BODY,{"derivedFrom":makeQuery(id+"F2.opExtrude","SWEPT_BODY",BODY,{"disambiguationData":[OSD([sQuery(id+"F1.wireOp",EDGE,"E1.bottom"),sQuery(id+"F1.wireOp",EDGE,"E1.top"),sQuery(id+"F1.wireOp",EDGE,"E1.left"),sQuery(id+"F1.wireOp",EDGE,"E1.right")])]}),"instanceName":"1"}),"instanceName":"1"}),"instanceName":"1"}),"instanceName":"1"});
            var Q13;
            Q13=makeQuery(id+"F15.opPattern","COPY",BODY,{"derivedFrom":makeQuery(id+"F13.opPattern","COPY",BODY,{"derivedFrom":makeQuery(id+"F4.opPattern","COPY",BODY,{"derivedFrom":makeQuery(id+"F2.opExtrude","SWEPT_BODY",BODY,{"disambiguationData":[OSD([sQuery(id+"F1.wireOp",EDGE,"E1.bottom"),sQuery(id+"F1.wireOp",EDGE,"E1.top"),sQuery(id+"F1.wireOp",EDGE,"E1.left"),sQuery(id+"F1.wireOp",EDGE,"E1.right")])]}),"instanceName":"1"}),"instanceName":"1"}),"instanceName":"1"});
            var Q14;
            Q14=makeQuery(id+"F15.opPattern","COPY",BODY,{"derivedFrom":makeQuery(id+"F13.opPattern","COPY",BODY,{"derivedFrom":makeQuery(id+"F6.opPattern","COPY",BODY,{"derivedFrom":makeQuery(id+"F2.opExtrude","SWEPT_BODY",BODY,{"disambiguationData":[OSD([sQuery(id+"F1.wireOp",EDGE,"E1.bottom"),sQuery(id+"F1.wireOp",EDGE,"E1.top"),sQuery(id+"F1.wireOp",EDGE,"E1.left"),sQuery(id+"F1.wireOp",EDGE,"E1.right")])]}),"instanceName":"1"}),"instanceName":"1"}),"instanceName":"1"});
            var Q15;
            Q15=makeQuery(id+"F15.opPattern","COPY",BODY,{"derivedFrom":makeQuery(id+"F13.opPattern","COPY",BODY,{"derivedFrom":makeQuery(id+"F2.opExtrude","SWEPT_BODY",BODY,{"disambiguationData":[OSD([sQuery(id+"F1.wireOp",EDGE,"E1.bottom"),sQuery(id+"F1.wireOp",EDGE,"E1.top"),sQuery(id+"F1.wireOp",EDGE,"E1.left"),sQuery(id+"F1.wireOp",EDGE,"E1.right")])]}),"instanceName":"1"}),"instanceName":"1"});
            var Q16;
            Q16=makeQuery(id+"F20.opPattern","COPY",EDGE,{"derivedFrom":makeQuery(id+"F15.opPattern","COPY",EDGE,{"derivedFrom":makeQuery(id+"F11.opPattern","COPY",EDGE,{"derivedFrom":makeQuery(id+"F6.opPattern","COPY",EDGE,{"derivedFrom":makeQuery(id+"F4.opPattern","COPY",EDGE,{"derivedFrom":makeQuery(id+"F2.opExtrude","SWEPT_EDGE",EDGE,{"disambiguationData":[OSD([sQuery(id+"F1.wireOp",EDGE,"E1.top"),sQuery(id+"F1.wireOp",EDGE,"E1.left")])]}),"instanceName":"1"}),"instanceName":"1"}),"instanceName":"1"}),"instanceName":"1"}),"instanceName":"1"});
            transform(context, id + "F25", {"entities" : qUnion([Q0, Q1, Q2, Q3, Q4, Q5, Q6, Q7, Q8, Q9, Q10, Q11, Q12, Q13, Q14, Q15]), "transformType" : TransformType.ROTATION, "transformAxis" : qUnion([Q16]), "angle" : 90 * degree, "makeCopy" : false});
        }
        {
            var Q0;
            Q0=makeQuery(id+"F22.opPattern","COPY",BODY,{"derivedFrom":makeQuery(id+"F15.opPattern","COPY",BODY,{"derivedFrom":makeQuery(id+"F11.opPattern","COPY",BODY,{"derivedFrom":makeQuery(id+"F4.opPattern","COPY",BODY,{"derivedFrom":makeQuery(id+"F2.opExtrude","SWEPT_BODY",BODY,{"disambiguationData":[OSD([sQuery(id+"F1.wireOp",EDGE,"E1.bottom"),sQuery(id+"F1.wireOp",EDGE,"E1.top"),sQuery(id+"F1.wireOp",EDGE,"E1.left"),sQuery(id+"F1.wireOp",EDGE,"E1.right")])]}),"instanceName":"1"}),"instanceName":"1"}),"instanceName":"1"}),"instanceName":"1"});
            var Q1;
            Q1=makeQuery(id+"F22.opPattern","COPY",BODY,{"derivedFrom":makeQuery(id+"F15.opPattern","COPY",BODY,{"derivedFrom":makeQuery(id+"F11.opPattern","COPY",BODY,{"derivedFrom":makeQuery(id+"F6.opPattern","COPY",BODY,{"derivedFrom":makeQuery(id+"F2.opExtrude","SWEPT_BODY",BODY,{"disambiguationData":[OSD([sQuery(id+"F1.wireOp",EDGE,"E1.bottom"),sQuery(id+"F1.wireOp",EDGE,"E1.top"),sQuery(id+"F1.wireOp",EDGE,"E1.left"),sQuery(id+"F1.wireOp",EDGE,"E1.right")])]}),"instanceName":"1"}),"instanceName":"1"}),"instanceName":"1"}),"instanceName":"1"});
            var Q2;
            Q2=makeQuery(id+"F22.opPattern","COPY",BODY,{"derivedFrom":makeQuery(id+"F15.opPattern","COPY",BODY,{"derivedFrom":makeQuery(id+"F11.opPattern","COPY",BODY,{"derivedFrom":makeQuery(id+"F2.opExtrude","SWEPT_BODY",BODY,{"disambiguationData":[OSD([sQuery(id+"F1.wireOp",EDGE,"E1.bottom"),sQuery(id+"F1.wireOp",EDGE,"E1.top"),sQuery(id+"F1.wireOp",EDGE,"E1.left"),sQuery(id+"F1.wireOp",EDGE,"E1.right")])]}),"instanceName":"1"}),"instanceName":"1"}),"instanceName":"1"});
            var Q3;
            Q3=makeQuery(id+"F22.opPattern","COPY",BODY,{"derivedFrom":makeQuery(id+"F15.opPattern","COPY",BODY,{"derivedFrom":makeQuery(id+"F6.opPattern","COPY",BODY,{"derivedFrom":makeQuery(id+"F4.opPattern","COPY",BODY,{"derivedFrom":makeQuery(id+"F2.opExtrude","SWEPT_BODY",BODY,{"disambiguationData":[OSD([sQuery(id+"F1.wireOp",EDGE,"E1.bottom"),sQuery(id+"F1.wireOp",EDGE,"E1.top"),sQuery(id+"F1.wireOp",EDGE,"E1.left"),sQuery(id+"F1.wireOp",EDGE,"E1.right")])]}),"instanceName":"1"}),"instanceName":"1"}),"instanceName":"1"}),"instanceName":"1"});
            var Q4;
            Q4=makeQuery(id+"F22.opPattern","COPY",BODY,{"derivedFrom":makeQuery(id+"F15.opPattern","COPY",BODY,{"derivedFrom":makeQuery(id+"F4.opPattern","COPY",BODY,{"derivedFrom":makeQuery(id+"F2.opExtrude","SWEPT_BODY",BODY,{"disambiguationData":[OSD([sQuery(id+"F1.wireOp",EDGE,"E1.bottom"),sQuery(id+"F1.wireOp",EDGE,"E1.top"),sQuery(id+"F1.wireOp",EDGE,"E1.left"),sQuery(id+"F1.wireOp",EDGE,"E1.right")])]}),"instanceName":"1"}),"instanceName":"1"}),"instanceName":"1"});
            var Q5;
            Q5=makeQuery(id+"F22.opPattern","COPY",BODY,{"derivedFrom":makeQuery(id+"F15.opPattern","COPY",BODY,{"derivedFrom":makeQuery(id+"F6.opPattern","COPY",BODY,{"derivedFrom":makeQuery(id+"F2.opExtrude","SWEPT_BODY",BODY,{"disambiguationData":[OSD([sQuery(id+"F1.wireOp",EDGE,"E1.bottom"),sQuery(id+"F1.wireOp",EDGE,"E1.top"),sQuery(id+"F1.wireOp",EDGE,"E1.left"),sQuery(id+"F1.wireOp",EDGE,"E1.right")])]}),"instanceName":"1"}),"instanceName":"1"}),"instanceName":"1"});
            var Q6;
            Q6=makeQuery(id+"F22.opPattern","COPY",BODY,{"derivedFrom":makeQuery(id+"F15.opPattern","COPY",BODY,{"derivedFrom":makeQuery(id+"F2.opExtrude","SWEPT_BODY",BODY,{"disambiguationData":[OSD([sQuery(id+"F1.wireOp",EDGE,"E1.bottom"),sQuery(id+"F1.wireOp",EDGE,"E1.top"),sQuery(id+"F1.wireOp",EDGE,"E1.left"),sQuery(id+"F1.wireOp",EDGE,"E1.right")])]}),"instanceName":"1"}),"instanceName":"1"});
            var Q7;
            Q7=makeQuery(id+"F22.opPattern","COPY",BODY,{"derivedFrom":makeQuery(id+"F15.opPattern","COPY",BODY,{"derivedFrom":makeQuery(id+"F13.opPattern","COPY",BODY,{"derivedFrom":makeQuery(id+"F11.opPattern","COPY",BODY,{"derivedFrom":makeQuery(id+"F6.opPattern","COPY",BODY,{"derivedFrom":makeQuery(id+"F4.opPattern","COPY",BODY,{"derivedFrom":makeQuery(id+"F2.opExtrude","SWEPT_BODY",BODY,{"disambiguationData":[OSD([sQuery(id+"F1.wireOp",EDGE,"E1.bottom"),sQuery(id+"F1.wireOp",EDGE,"E1.top"),sQuery(id+"F1.wireOp",EDGE,"E1.left"),sQuery(id+"F1.wireOp",EDGE,"E1.right")])]}),"instanceName":"1"}),"instanceName":"1"}),"instanceName":"1"}),"instanceName":"1"}),"instanceName":"1"}),"instanceName":"1"});
            var Q8;
            Q8=makeQuery(id+"F22.opPattern","COPY",BODY,{"derivedFrom":makeQuery(id+"F15.opPattern","COPY",BODY,{"derivedFrom":makeQuery(id+"F13.opPattern","COPY",BODY,{"derivedFrom":makeQuery(id+"F11.opPattern","COPY",BODY,{"derivedFrom":makeQuery(id+"F4.opPattern","COPY",BODY,{"derivedFrom":makeQuery(id+"F2.opExtrude","SWEPT_BODY",BODY,{"disambiguationData":[OSD([sQuery(id+"F1.wireOp",EDGE,"E1.bottom"),sQuery(id+"F1.wireOp",EDGE,"E1.top"),sQuery(id+"F1.wireOp",EDGE,"E1.left"),sQuery(id+"F1.wireOp",EDGE,"E1.right")])]}),"instanceName":"1"}),"instanceName":"1"}),"instanceName":"1"}),"instanceName":"1"}),"instanceName":"1"});
            var Q9;
            Q9=makeQuery(id+"F22.opPattern","COPY",BODY,{"derivedFrom":makeQuery(id+"F15.opPattern","COPY",BODY,{"derivedFrom":makeQuery(id+"F13.opPattern","COPY",BODY,{"derivedFrom":makeQuery(id+"F11.opPattern","COPY",BODY,{"derivedFrom":makeQuery(id+"F6.opPattern","COPY",BODY,{"derivedFrom":makeQuery(id+"F2.opExtrude","SWEPT_BODY",BODY,{"disambiguationData":[OSD([sQuery(id+"F1.wireOp",EDGE,"E1.bottom"),sQuery(id+"F1.wireOp",EDGE,"E1.top"),sQuery(id+"F1.wireOp",EDGE,"E1.left"),sQuery(id+"F1.wireOp",EDGE,"E1.right")])]}),"instanceName":"1"}),"instanceName":"1"}),"instanceName":"1"}),"instanceName":"1"}),"instanceName":"1"});
            var Q10;
            Q10=makeQuery(id+"F22.opPattern","COPY",BODY,{"derivedFrom":makeQuery(id+"F15.opPattern","COPY",BODY,{"derivedFrom":makeQuery(id+"F13.opPattern","COPY",BODY,{"derivedFrom":makeQuery(id+"F11.opPattern","COPY",BODY,{"derivedFrom":makeQuery(id+"F2.opExtrude","SWEPT_BODY",BODY,{"disambiguationData":[OSD([sQuery(id+"F1.wireOp",EDGE,"E1.bottom"),sQuery(id+"F1.wireOp",EDGE,"E1.top"),sQuery(id+"F1.wireOp",EDGE,"E1.left"),sQuery(id+"F1.wireOp",EDGE,"E1.right")])]}),"instanceName":"1"}),"instanceName":"1"}),"instanceName":"1"}),"instanceName":"1"});
            var Q11;
            Q11=makeQuery(id+"F22.opPattern","COPY",BODY,{"derivedFrom":makeQuery(id+"F15.opPattern","COPY",BODY,{"derivedFrom":makeQuery(id+"F13.opPattern","COPY",BODY,{"derivedFrom":makeQuery(id+"F6.opPattern","COPY",BODY,{"derivedFrom":makeQuery(id+"F4.opPattern","COPY",BODY,{"derivedFrom":makeQuery(id+"F2.opExtrude","SWEPT_BODY",BODY,{"disambiguationData":[OSD([sQuery(id+"F1.wireOp",EDGE,"E1.bottom"),sQuery(id+"F1.wireOp",EDGE,"E1.top"),sQuery(id+"F1.wireOp",EDGE,"E1.left"),sQuery(id+"F1.wireOp",EDGE,"E1.right")])]}),"instanceName":"1"}),"instanceName":"1"}),"instanceName":"1"}),"instanceName":"1"}),"instanceName":"1"});
            var Q12;
            Q12=makeQuery(id+"F22.opPattern","COPY",BODY,{"derivedFrom":makeQuery(id+"F15.opPattern","COPY",BODY,{"derivedFrom":makeQuery(id+"F13.opPattern","COPY",BODY,{"derivedFrom":makeQuery(id+"F4.opPattern","COPY",BODY,{"derivedFrom":makeQuery(id+"F2.opExtrude","SWEPT_BODY",BODY,{"disambiguationData":[OSD([sQuery(id+"F1.wireOp",EDGE,"E1.bottom"),sQuery(id+"F1.wireOp",EDGE,"E1.top"),sQuery(id+"F1.wireOp",EDGE,"E1.left"),sQuery(id+"F1.wireOp",EDGE,"E1.right")])]}),"instanceName":"1"}),"instanceName":"1"}),"instanceName":"1"}),"instanceName":"1"});
            var Q13;
            Q13=makeQuery(id+"F22.opPattern","COPY",BODY,{"derivedFrom":makeQuery(id+"F15.opPattern","COPY",BODY,{"derivedFrom":makeQuery(id+"F13.opPattern","COPY",BODY,{"derivedFrom":makeQuery(id+"F6.opPattern","COPY",BODY,{"derivedFrom":makeQuery(id+"F2.opExtrude","SWEPT_BODY",BODY,{"disambiguationData":[OSD([sQuery(id+"F1.wireOp",EDGE,"E1.bottom"),sQuery(id+"F1.wireOp",EDGE,"E1.top"),sQuery(id+"F1.wireOp",EDGE,"E1.left"),sQuery(id+"F1.wireOp",EDGE,"E1.right")])]}),"instanceName":"1"}),"instanceName":"1"}),"instanceName":"1"}),"instanceName":"1"});
            var Q14;
            Q14=makeQuery(id+"F22.opPattern","COPY",BODY,{"derivedFrom":makeQuery(id+"F15.opPattern","COPY",BODY,{"derivedFrom":makeQuery(id+"F13.opPattern","COPY",BODY,{"derivedFrom":makeQuery(id+"F2.opExtrude","SWEPT_BODY",BODY,{"disambiguationData":[OSD([sQuery(id+"F1.wireOp",EDGE,"E1.bottom"),sQuery(id+"F1.wireOp",EDGE,"E1.top"),sQuery(id+"F1.wireOp",EDGE,"E1.left"),sQuery(id+"F1.wireOp",EDGE,"E1.right")])]}),"instanceName":"1"}),"instanceName":"1"}),"instanceName":"1"});
            transform(context, id + "F26", {"entities" : qUnion([Q0, Q1, Q2, Q3, Q4, Q5, Q6, Q7, Q8, Q9, Q10, Q11, Q12, Q13, Q14]), "transformType" : TransformType.TRANSLATION_3D, "dx" : 19.05 * mm, "dy" : 78.74 * mm, "dz" : 0 * mm, "makeCopy" : false});
        }
        {
            var Q0;
            Q0=makeQuery(id+"F22.opPattern","COPY",BODY,{"derivedFrom":makeQuery(id+"F15.opPattern","COPY",BODY,{"derivedFrom":makeQuery(id+"F11.opPattern","COPY",BODY,{"derivedFrom":makeQuery(id+"F6.opPattern","COPY",BODY,{"derivedFrom":makeQuery(id+"F4.opPattern","COPY",BODY,{"derivedFrom":makeQuery(id+"F2.opExtrude","SWEPT_BODY",BODY,{"disambiguationData":[OSD([sQuery(id+"F1.wireOp",EDGE,"E1.bottom"),sQuery(id+"F1.wireOp",EDGE,"E1.top"),sQuery(id+"F1.wireOp",EDGE,"E1.left"),sQuery(id+"F1.wireOp",EDGE,"E1.right")])]}),"instanceName":"1"}),"instanceName":"1"}),"instanceName":"1"}),"instanceName":"1"}),"instanceName":"1"});
            deleteBodies(context, id + "F27", {"entities" : qUnion([Q0])});
        }
        {
            var Q0;
            Q0=makeQuery(id+"F15.opPattern","COPY",BODY,{"derivedFrom":makeQuery(id+"F13.opPattern","COPY",BODY,{"derivedFrom":makeQuery(id+"F2.opExtrude","SWEPT_BODY",BODY,{"disambiguationData":[OSD([sQuery(id+"F1.wireOp",EDGE,"E1.bottom"),sQuery(id+"F1.wireOp",EDGE,"E1.top"),sQuery(id+"F1.wireOp",EDGE,"E1.left"),sQuery(id+"F1.wireOp",EDGE,"E1.right")])]}),"instanceName":"1"}),"instanceName":"1"});
            var Q1;
            Q1=makeQuery(id+"F15.opPattern","COPY",BODY,{"derivedFrom":makeQuery(id+"F13.opPattern","COPY",BODY,{"derivedFrom":makeQuery(id+"F6.opPattern","COPY",BODY,{"derivedFrom":makeQuery(id+"F2.opExtrude","SWEPT_BODY",BODY,{"disambiguationData":[OSD([sQuery(id+"F1.wireOp",EDGE,"E1.bottom"),sQuery(id+"F1.wireOp",EDGE,"E1.top"),sQuery(id+"F1.wireOp",EDGE,"E1.left"),sQuery(id+"F1.wireOp",EDGE,"E1.right")])]}),"instanceName":"1"}),"instanceName":"1"}),"instanceName":"1"});
            var Q2;
            Q2=makeQuery(id+"F15.opPattern","COPY",BODY,{"derivedFrom":makeQuery(id+"F13.opPattern","COPY",BODY,{"derivedFrom":makeQuery(id+"F4.opPattern","COPY",BODY,{"derivedFrom":makeQuery(id+"F2.opExtrude","SWEPT_BODY",BODY,{"disambiguationData":[OSD([sQuery(id+"F1.wireOp",EDGE,"E1.bottom"),sQuery(id+"F1.wireOp",EDGE,"E1.top"),sQuery(id+"F1.wireOp",EDGE,"E1.left"),sQuery(id+"F1.wireOp",EDGE,"E1.right")])]}),"instanceName":"1"}),"instanceName":"1"}),"instanceName":"1"});
            var Q3;
            Q3=makeQuery(id+"F15.opPattern","COPY",BODY,{"derivedFrom":makeQuery(id+"F13.opPattern","COPY",BODY,{"derivedFrom":makeQuery(id+"F6.opPattern","COPY",BODY,{"derivedFrom":makeQuery(id+"F4.opPattern","COPY",BODY,{"derivedFrom":makeQuery(id+"F2.opExtrude","SWEPT_BODY",BODY,{"disambiguationData":[OSD([sQuery(id+"F1.wireOp",EDGE,"E1.bottom"),sQuery(id+"F1.wireOp",EDGE,"E1.top"),sQuery(id+"F1.wireOp",EDGE,"E1.left"),sQuery(id+"F1.wireOp",EDGE,"E1.right")])]}),"instanceName":"1"}),"instanceName":"1"}),"instanceName":"1"}),"instanceName":"1"});
            var Q4;
            Q4=makeQuery(id+"F15.opPattern","COPY",BODY,{"derivedFrom":makeQuery(id+"F13.opPattern","COPY",BODY,{"derivedFrom":makeQuery(id+"F11.opPattern","COPY",BODY,{"derivedFrom":makeQuery(id+"F2.opExtrude","SWEPT_BODY",BODY,{"disambiguationData":[OSD([sQuery(id+"F1.wireOp",EDGE,"E1.bottom"),sQuery(id+"F1.wireOp",EDGE,"E1.top"),sQuery(id+"F1.wireOp",EDGE,"E1.left"),sQuery(id+"F1.wireOp",EDGE,"E1.right")])]}),"instanceName":"1"}),"instanceName":"1"}),"instanceName":"1"});
            var Q5;
            Q5=makeQuery(id+"F15.opPattern","COPY",BODY,{"derivedFrom":makeQuery(id+"F13.opPattern","COPY",BODY,{"derivedFrom":makeQuery(id+"F11.opPattern","COPY",BODY,{"derivedFrom":makeQuery(id+"F6.opPattern","COPY",BODY,{"derivedFrom":makeQuery(id+"F2.opExtrude","SWEPT_BODY",BODY,{"disambiguationData":[OSD([sQuery(id+"F1.wireOp",EDGE,"E1.bottom"),sQuery(id+"F1.wireOp",EDGE,"E1.top"),sQuery(id+"F1.wireOp",EDGE,"E1.left"),sQuery(id+"F1.wireOp",EDGE,"E1.right")])]}),"instanceName":"1"}),"instanceName":"1"}),"instanceName":"1"}),"instanceName":"1"});
            var Q6;
            Q6=makeQuery(id+"F15.opPattern","COPY",BODY,{"derivedFrom":makeQuery(id+"F13.opPattern","COPY",BODY,{"derivedFrom":makeQuery(id+"F11.opPattern","COPY",BODY,{"derivedFrom":makeQuery(id+"F4.opPattern","COPY",BODY,{"derivedFrom":makeQuery(id+"F2.opExtrude","SWEPT_BODY",BODY,{"disambiguationData":[OSD([sQuery(id+"F1.wireOp",EDGE,"E1.bottom"),sQuery(id+"F1.wireOp",EDGE,"E1.top"),sQuery(id+"F1.wireOp",EDGE,"E1.left"),sQuery(id+"F1.wireOp",EDGE,"E1.right")])]}),"instanceName":"1"}),"instanceName":"1"}),"instanceName":"1"}),"instanceName":"1"});
            var Q7;
            Q7=makeQuery(id+"F15.opPattern","COPY",BODY,{"derivedFrom":makeQuery(id+"F13.opPattern","COPY",BODY,{"derivedFrom":makeQuery(id+"F11.opPattern","COPY",BODY,{"derivedFrom":makeQuery(id+"F6.opPattern","COPY",BODY,{"derivedFrom":makeQuery(id+"F4.opPattern","COPY",BODY,{"derivedFrom":makeQuery(id+"F2.opExtrude","SWEPT_BODY",BODY,{"disambiguationData":[OSD([sQuery(id+"F1.wireOp",EDGE,"E1.bottom"),sQuery(id+"F1.wireOp",EDGE,"E1.top"),sQuery(id+"F1.wireOp",EDGE,"E1.left"),sQuery(id+"F1.wireOp",EDGE,"E1.right")])]}),"instanceName":"1"}),"instanceName":"1"}),"instanceName":"1"}),"instanceName":"1"}),"instanceName":"1"});
            var Q8;
            Q8=makeQuery(id+"F15.opPattern","COPY",BODY,{"derivedFrom":makeQuery(id+"F2.opExtrude","SWEPT_BODY",BODY,{"disambiguationData":[OSD([sQuery(id+"F1.wireOp",EDGE,"E1.bottom"),sQuery(id+"F1.wireOp",EDGE,"E1.top"),sQuery(id+"F1.wireOp",EDGE,"E1.left"),sQuery(id+"F1.wireOp",EDGE,"E1.right")])]}),"instanceName":"1"});
            var Q9;
            Q9=makeQuery(id+"F15.opPattern","COPY",BODY,{"derivedFrom":makeQuery(id+"F6.opPattern","COPY",BODY,{"derivedFrom":makeQuery(id+"F2.opExtrude","SWEPT_BODY",BODY,{"disambiguationData":[OSD([sQuery(id+"F1.wireOp",EDGE,"E1.bottom"),sQuery(id+"F1.wireOp",EDGE,"E1.top"),sQuery(id+"F1.wireOp",EDGE,"E1.left"),sQuery(id+"F1.wireOp",EDGE,"E1.right")])]}),"instanceName":"1"}),"instanceName":"1"});
            var Q10;
            Q10=makeQuery(id+"F15.opPattern","COPY",BODY,{"derivedFrom":makeQuery(id+"F4.opPattern","COPY",BODY,{"derivedFrom":makeQuery(id+"F2.opExtrude","SWEPT_BODY",BODY,{"disambiguationData":[OSD([sQuery(id+"F1.wireOp",EDGE,"E1.bottom"),sQuery(id+"F1.wireOp",EDGE,"E1.top"),sQuery(id+"F1.wireOp",EDGE,"E1.left"),sQuery(id+"F1.wireOp",EDGE,"E1.right")])]}),"instanceName":"1"}),"instanceName":"1"});
            var Q11;
            Q11=makeQuery(id+"F15.opPattern","COPY",BODY,{"derivedFrom":makeQuery(id+"F6.opPattern","COPY",BODY,{"derivedFrom":makeQuery(id+"F4.opPattern","COPY",BODY,{"derivedFrom":makeQuery(id+"F2.opExtrude","SWEPT_BODY",BODY,{"disambiguationData":[OSD([sQuery(id+"F1.wireOp",EDGE,"E1.bottom"),sQuery(id+"F1.wireOp",EDGE,"E1.top"),sQuery(id+"F1.wireOp",EDGE,"E1.left"),sQuery(id+"F1.wireOp",EDGE,"E1.right")])]}),"instanceName":"1"}),"instanceName":"1"}),"instanceName":"1"});
            var Q12;
            Q12=makeQuery(id+"F15.opPattern","COPY",BODY,{"derivedFrom":makeQuery(id+"F11.opPattern","COPY",BODY,{"derivedFrom":makeQuery(id+"F2.opExtrude","SWEPT_BODY",BODY,{"disambiguationData":[OSD([sQuery(id+"F1.wireOp",EDGE,"E1.bottom"),sQuery(id+"F1.wireOp",EDGE,"E1.top"),sQuery(id+"F1.wireOp",EDGE,"E1.left"),sQuery(id+"F1.wireOp",EDGE,"E1.right")])]}),"instanceName":"1"}),"instanceName":"1"});
            var Q13;
            Q13=makeQuery(id+"F15.opPattern","COPY",BODY,{"derivedFrom":makeQuery(id+"F11.opPattern","COPY",BODY,{"derivedFrom":makeQuery(id+"F6.opPattern","COPY",BODY,{"derivedFrom":makeQuery(id+"F2.opExtrude","SWEPT_BODY",BODY,{"disambiguationData":[OSD([sQuery(id+"F1.wireOp",EDGE,"E1.bottom"),sQuery(id+"F1.wireOp",EDGE,"E1.top"),sQuery(id+"F1.wireOp",EDGE,"E1.left"),sQuery(id+"F1.wireOp",EDGE,"E1.right")])]}),"instanceName":"1"}),"instanceName":"1"}),"instanceName":"1"});
            var Q14;
            Q14=makeQuery(id+"F15.opPattern","COPY",BODY,{"derivedFrom":makeQuery(id+"F11.opPattern","COPY",BODY,{"derivedFrom":makeQuery(id+"F4.opPattern","COPY",BODY,{"derivedFrom":makeQuery(id+"F2.opExtrude","SWEPT_BODY",BODY,{"disambiguationData":[OSD([sQuery(id+"F1.wireOp",EDGE,"E1.bottom"),sQuery(id+"F1.wireOp",EDGE,"E1.top"),sQuery(id+"F1.wireOp",EDGE,"E1.left"),sQuery(id+"F1.wireOp",EDGE,"E1.right")])]}),"instanceName":"1"}),"instanceName":"1"}),"instanceName":"1"});
            var Q15;
            Q15=makeQuery(id+"F15.opPattern","COPY",BODY,{"derivedFrom":makeQuery(id+"F11.opPattern","COPY",BODY,{"derivedFrom":makeQuery(id+"F6.opPattern","COPY",BODY,{"derivedFrom":makeQuery(id+"F4.opPattern","COPY",BODY,{"derivedFrom":makeQuery(id+"F2.opExtrude","SWEPT_BODY",BODY,{"disambiguationData":[OSD([sQuery(id+"F1.wireOp",EDGE,"E1.bottom"),sQuery(id+"F1.wireOp",EDGE,"E1.top"),sQuery(id+"F1.wireOp",EDGE,"E1.left"),sQuery(id+"F1.wireOp",EDGE,"E1.right")])]}),"instanceName":"1"}),"instanceName":"1"}),"instanceName":"1"}),"instanceName":"1"});
            transform(context, id + "F28", {"entities" : qUnion([Q0, Q1, Q2, Q3, Q4, Q5, Q6, Q7, Q8, Q9, Q10, Q11, Q12, Q13, Q14, Q15]), "transformType" : TransformType.TRANSLATION_3D, "dx" : 119.38 * mm, "dy" : 63.5 * mm, "dz" : 0 * mm, "makeCopy" : false});
        }
        {
            var Q0;
            Q0=makeQuery(id+"F15.opPattern","COPY",BODY,{"derivedFrom":makeQuery(id+"F13.opPattern","COPY",BODY,{"derivedFrom":makeQuery(id+"F2.opExtrude","SWEPT_BODY",BODY,{"disambiguationData":[OSD([sQuery(id+"F1.wireOp",EDGE,"E1.bottom"),sQuery(id+"F1.wireOp",EDGE,"E1.top"),sQuery(id+"F1.wireOp",EDGE,"E1.left"),sQuery(id+"F1.wireOp",EDGE,"E1.right")])]}),"instanceName":"1"}),"instanceName":"1"});
            var Q1;
            Q1=makeQuery(id+"F15.opPattern","COPY",BODY,{"derivedFrom":makeQuery(id+"F13.opPattern","COPY",BODY,{"derivedFrom":makeQuery(id+"F6.opPattern","COPY",BODY,{"derivedFrom":makeQuery(id+"F2.opExtrude","SWEPT_BODY",BODY,{"disambiguationData":[OSD([sQuery(id+"F1.wireOp",EDGE,"E1.bottom"),sQuery(id+"F1.wireOp",EDGE,"E1.top"),sQuery(id+"F1.wireOp",EDGE,"E1.left"),sQuery(id+"F1.wireOp",EDGE,"E1.right")])]}),"instanceName":"1"}),"instanceName":"1"}),"instanceName":"1"});
            var Q2;
            Q2=makeQuery(id+"F15.opPattern","COPY",BODY,{"derivedFrom":makeQuery(id+"F13.opPattern","COPY",BODY,{"derivedFrom":makeQuery(id+"F4.opPattern","COPY",BODY,{"derivedFrom":makeQuery(id+"F2.opExtrude","SWEPT_BODY",BODY,{"disambiguationData":[OSD([sQuery(id+"F1.wireOp",EDGE,"E1.bottom"),sQuery(id+"F1.wireOp",EDGE,"E1.top"),sQuery(id+"F1.wireOp",EDGE,"E1.left"),sQuery(id+"F1.wireOp",EDGE,"E1.right")])]}),"instanceName":"1"}),"instanceName":"1"}),"instanceName":"1"});
            var Q3;
            Q3=makeQuery(id+"F15.opPattern","COPY",BODY,{"derivedFrom":makeQuery(id+"F13.opPattern","COPY",BODY,{"derivedFrom":makeQuery(id+"F6.opPattern","COPY",BODY,{"derivedFrom":makeQuery(id+"F4.opPattern","COPY",BODY,{"derivedFrom":makeQuery(id+"F2.opExtrude","SWEPT_BODY",BODY,{"disambiguationData":[OSD([sQuery(id+"F1.wireOp",EDGE,"E1.bottom"),sQuery(id+"F1.wireOp",EDGE,"E1.top"),sQuery(id+"F1.wireOp",EDGE,"E1.left"),sQuery(id+"F1.wireOp",EDGE,"E1.right")])]}),"instanceName":"1"}),"instanceName":"1"}),"instanceName":"1"}),"instanceName":"1"});
            var Q4;
            Q4=makeQuery(id+"F15.opPattern","COPY",BODY,{"derivedFrom":makeQuery(id+"F13.opPattern","COPY",BODY,{"derivedFrom":makeQuery(id+"F11.opPattern","COPY",BODY,{"derivedFrom":makeQuery(id+"F2.opExtrude","SWEPT_BODY",BODY,{"disambiguationData":[OSD([sQuery(id+"F1.wireOp",EDGE,"E1.bottom"),sQuery(id+"F1.wireOp",EDGE,"E1.top"),sQuery(id+"F1.wireOp",EDGE,"E1.left"),sQuery(id+"F1.wireOp",EDGE,"E1.right")])]}),"instanceName":"1"}),"instanceName":"1"}),"instanceName":"1"});
            var Q5;
            Q5=makeQuery(id+"F15.opPattern","COPY",BODY,{"derivedFrom":makeQuery(id+"F13.opPattern","COPY",BODY,{"derivedFrom":makeQuery(id+"F11.opPattern","COPY",BODY,{"derivedFrom":makeQuery(id+"F6.opPattern","COPY",BODY,{"derivedFrom":makeQuery(id+"F2.opExtrude","SWEPT_BODY",BODY,{"disambiguationData":[OSD([sQuery(id+"F1.wireOp",EDGE,"E1.bottom"),sQuery(id+"F1.wireOp",EDGE,"E1.top"),sQuery(id+"F1.wireOp",EDGE,"E1.left"),sQuery(id+"F1.wireOp",EDGE,"E1.right")])]}),"instanceName":"1"}),"instanceName":"1"}),"instanceName":"1"}),"instanceName":"1"});
            var Q6;
            Q6=makeQuery(id+"F15.opPattern","COPY",BODY,{"derivedFrom":makeQuery(id+"F13.opPattern","COPY",BODY,{"derivedFrom":makeQuery(id+"F11.opPattern","COPY",BODY,{"derivedFrom":makeQuery(id+"F4.opPattern","COPY",BODY,{"derivedFrom":makeQuery(id+"F2.opExtrude","SWEPT_BODY",BODY,{"disambiguationData":[OSD([sQuery(id+"F1.wireOp",EDGE,"E1.bottom"),sQuery(id+"F1.wireOp",EDGE,"E1.top"),sQuery(id+"F1.wireOp",EDGE,"E1.left"),sQuery(id+"F1.wireOp",EDGE,"E1.right")])]}),"instanceName":"1"}),"instanceName":"1"}),"instanceName":"1"}),"instanceName":"1"});
            var Q7;
            Q7=makeQuery(id+"F15.opPattern","COPY",BODY,{"derivedFrom":makeQuery(id+"F13.opPattern","COPY",BODY,{"derivedFrom":makeQuery(id+"F11.opPattern","COPY",BODY,{"derivedFrom":makeQuery(id+"F6.opPattern","COPY",BODY,{"derivedFrom":makeQuery(id+"F4.opPattern","COPY",BODY,{"derivedFrom":makeQuery(id+"F2.opExtrude","SWEPT_BODY",BODY,{"disambiguationData":[OSD([sQuery(id+"F1.wireOp",EDGE,"E1.bottom"),sQuery(id+"F1.wireOp",EDGE,"E1.top"),sQuery(id+"F1.wireOp",EDGE,"E1.left"),sQuery(id+"F1.wireOp",EDGE,"E1.right")])]}),"instanceName":"1"}),"instanceName":"1"}),"instanceName":"1"}),"instanceName":"1"}),"instanceName":"1"});
            deleteBodies(context, id + "F29", {"entities" : qUnion([Q0, Q1, Q2, Q3, Q4, Q5, Q6, Q7])});
        }
        {
            var Q0;
            Q0=makeQuery(id+"F20.opPattern","COPY",BODY,{"derivedFrom":makeQuery(id+"F15.opPattern","COPY",BODY,{"derivedFrom":makeQuery(id+"F13.opPattern","COPY",BODY,{"derivedFrom":makeQuery(id+"F11.opPattern","COPY",BODY,{"derivedFrom":makeQuery(id+"F6.opPattern","COPY",BODY,{"derivedFrom":makeQuery(id+"F2.opExtrude","SWEPT_BODY",BODY,{"disambiguationData":[OSD([sQuery(id+"F1.wireOp",EDGE,"E1.bottom"),sQuery(id+"F1.wireOp",EDGE,"E1.top"),sQuery(id+"F1.wireOp",EDGE,"E1.left"),sQuery(id+"F1.wireOp",EDGE,"E1.right")])]}),"instanceName":"1"}),"instanceName":"1"}),"instanceName":"1"}),"instanceName":"1"}),"instanceName":"1"});
            var Q1;
            Q1=makeQuery(id+"F20.opPattern","COPY",BODY,{"derivedFrom":makeQuery(id+"F15.opPattern","COPY",BODY,{"derivedFrom":makeQuery(id+"F13.opPattern","COPY",BODY,{"derivedFrom":makeQuery(id+"F11.opPattern","COPY",BODY,{"derivedFrom":makeQuery(id+"F2.opExtrude","SWEPT_BODY",BODY,{"disambiguationData":[OSD([sQuery(id+"F1.wireOp",EDGE,"E1.bottom"),sQuery(id+"F1.wireOp",EDGE,"E1.top"),sQuery(id+"F1.wireOp",EDGE,"E1.left"),sQuery(id+"F1.wireOp",EDGE,"E1.right")])]}),"instanceName":"1"}),"instanceName":"1"}),"instanceName":"1"}),"instanceName":"1"});
            var Q2;
            Q2=makeQuery(id+"F20.opPattern","COPY",BODY,{"derivedFrom":makeQuery(id+"F15.opPattern","COPY",BODY,{"derivedFrom":makeQuery(id+"F13.opPattern","COPY",BODY,{"derivedFrom":makeQuery(id+"F6.opPattern","COPY",BODY,{"derivedFrom":makeQuery(id+"F4.opPattern","COPY",BODY,{"derivedFrom":makeQuery(id+"F2.opExtrude","SWEPT_BODY",BODY,{"disambiguationData":[OSD([sQuery(id+"F1.wireOp",EDGE,"E1.bottom"),sQuery(id+"F1.wireOp",EDGE,"E1.top"),sQuery(id+"F1.wireOp",EDGE,"E1.left"),sQuery(id+"F1.wireOp",EDGE,"E1.right")])]}),"instanceName":"1"}),"instanceName":"1"}),"instanceName":"1"}),"instanceName":"1"}),"instanceName":"1"});
            var Q3;
            Q3=makeQuery(id+"F20.opPattern","COPY",BODY,{"derivedFrom":makeQuery(id+"F15.opPattern","COPY",BODY,{"derivedFrom":makeQuery(id+"F13.opPattern","COPY",BODY,{"derivedFrom":makeQuery(id+"F4.opPattern","COPY",BODY,{"derivedFrom":makeQuery(id+"F2.opExtrude","SWEPT_BODY",BODY,{"disambiguationData":[OSD([sQuery(id+"F1.wireOp",EDGE,"E1.bottom"),sQuery(id+"F1.wireOp",EDGE,"E1.top"),sQuery(id+"F1.wireOp",EDGE,"E1.left"),sQuery(id+"F1.wireOp",EDGE,"E1.right")])]}),"instanceName":"1"}),"instanceName":"1"}),"instanceName":"1"}),"instanceName":"1"});
            var Q4;
            Q4=makeQuery(id+"F20.opPattern","COPY",BODY,{"derivedFrom":makeQuery(id+"F15.opPattern","COPY",BODY,{"derivedFrom":makeQuery(id+"F13.opPattern","COPY",BODY,{"derivedFrom":makeQuery(id+"F6.opPattern","COPY",BODY,{"derivedFrom":makeQuery(id+"F2.opExtrude","SWEPT_BODY",BODY,{"disambiguationData":[OSD([sQuery(id+"F1.wireOp",EDGE,"E1.bottom"),sQuery(id+"F1.wireOp",EDGE,"E1.top"),sQuery(id+"F1.wireOp",EDGE,"E1.left"),sQuery(id+"F1.wireOp",EDGE,"E1.right")])]}),"instanceName":"1"}),"instanceName":"1"}),"instanceName":"1"}),"instanceName":"1"});
            var Q5;
            Q5=makeQuery(id+"F20.opPattern","COPY",BODY,{"derivedFrom":makeQuery(id+"F15.opPattern","COPY",BODY,{"derivedFrom":makeQuery(id+"F13.opPattern","COPY",BODY,{"derivedFrom":makeQuery(id+"F2.opExtrude","SWEPT_BODY",BODY,{"disambiguationData":[OSD([sQuery(id+"F1.wireOp",EDGE,"E1.bottom"),sQuery(id+"F1.wireOp",EDGE,"E1.top"),sQuery(id+"F1.wireOp",EDGE,"E1.left"),sQuery(id+"F1.wireOp",EDGE,"E1.right")])]}),"instanceName":"1"}),"instanceName":"1"}),"instanceName":"1"});
            var Q6;
            Q6=makeQuery(id+"F22.opPattern","COPY",BODY,{"derivedFrom":makeQuery(id+"F15.opPattern","COPY",BODY,{"derivedFrom":makeQuery(id+"F13.opPattern","COPY",BODY,{"derivedFrom":makeQuery(id+"F2.opExtrude","SWEPT_BODY",BODY,{"disambiguationData":[OSD([sQuery(id+"F1.wireOp",EDGE,"E1.bottom"),sQuery(id+"F1.wireOp",EDGE,"E1.top"),sQuery(id+"F1.wireOp",EDGE,"E1.left"),sQuery(id+"F1.wireOp",EDGE,"E1.right")])]}),"instanceName":"1"}),"instanceName":"1"}),"instanceName":"1"});
            var Q7;
            Q7=makeQuery(id+"F22.opPattern","COPY",BODY,{"derivedFrom":makeQuery(id+"F15.opPattern","COPY",BODY,{"derivedFrom":makeQuery(id+"F13.opPattern","COPY",BODY,{"derivedFrom":makeQuery(id+"F4.opPattern","COPY",BODY,{"derivedFrom":makeQuery(id+"F2.opExtrude","SWEPT_BODY",BODY,{"disambiguationData":[OSD([sQuery(id+"F1.wireOp",EDGE,"E1.bottom"),sQuery(id+"F1.wireOp",EDGE,"E1.top"),sQuery(id+"F1.wireOp",EDGE,"E1.left"),sQuery(id+"F1.wireOp",EDGE,"E1.right")])]}),"instanceName":"1"}),"instanceName":"1"}),"instanceName":"1"}),"instanceName":"1"});
            var Q8;
            Q8=makeQuery(id+"F22.opPattern","COPY",BODY,{"derivedFrom":makeQuery(id+"F15.opPattern","COPY",BODY,{"derivedFrom":makeQuery(id+"F13.opPattern","COPY",BODY,{"derivedFrom":makeQuery(id+"F6.opPattern","COPY",BODY,{"derivedFrom":makeQuery(id+"F2.opExtrude","SWEPT_BODY",BODY,{"disambiguationData":[OSD([sQuery(id+"F1.wireOp",EDGE,"E1.bottom"),sQuery(id+"F1.wireOp",EDGE,"E1.top"),sQuery(id+"F1.wireOp",EDGE,"E1.left"),sQuery(id+"F1.wireOp",EDGE,"E1.right")])]}),"instanceName":"1"}),"instanceName":"1"}),"instanceName":"1"}),"instanceName":"1"});
            var Q9;
            Q9=makeQuery(id+"F22.opPattern","COPY",BODY,{"derivedFrom":makeQuery(id+"F15.opPattern","COPY",BODY,{"derivedFrom":makeQuery(id+"F13.opPattern","COPY",BODY,{"derivedFrom":makeQuery(id+"F6.opPattern","COPY",BODY,{"derivedFrom":makeQuery(id+"F4.opPattern","COPY",BODY,{"derivedFrom":makeQuery(id+"F2.opExtrude","SWEPT_BODY",BODY,{"disambiguationData":[OSD([sQuery(id+"F1.wireOp",EDGE,"E1.bottom"),sQuery(id+"F1.wireOp",EDGE,"E1.top"),sQuery(id+"F1.wireOp",EDGE,"E1.left"),sQuery(id+"F1.wireOp",EDGE,"E1.right")])]}),"instanceName":"1"}),"instanceName":"1"}),"instanceName":"1"}),"instanceName":"1"}),"instanceName":"1"});
            var Q10;
            Q10=makeQuery(id+"F22.opPattern","COPY",BODY,{"derivedFrom":makeQuery(id+"F15.opPattern","COPY",BODY,{"derivedFrom":makeQuery(id+"F13.opPattern","COPY",BODY,{"derivedFrom":makeQuery(id+"F11.opPattern","COPY",BODY,{"derivedFrom":makeQuery(id+"F2.opExtrude","SWEPT_BODY",BODY,{"disambiguationData":[OSD([sQuery(id+"F1.wireOp",EDGE,"E1.bottom"),sQuery(id+"F1.wireOp",EDGE,"E1.top"),sQuery(id+"F1.wireOp",EDGE,"E1.left"),sQuery(id+"F1.wireOp",EDGE,"E1.right")])]}),"instanceName":"1"}),"instanceName":"1"}),"instanceName":"1"}),"instanceName":"1"});
            deleteBodies(context, id + "F30", {"entities" : qUnion([Q0, Q1, Q2, Q3, Q4, Q5, Q6, Q7, Q8, Q9, Q10])});
        }
        {
            var Q0;
            Q0=makeQuery(id+"F13.opPattern","COPY",BODY,{"derivedFrom":makeQuery(id+"F2.opExtrude","SWEPT_BODY",BODY,{"disambiguationData":[OSD([sQuery(id+"F1.wireOp",EDGE,"E1.bottom"),sQuery(id+"F1.wireOp",EDGE,"E1.top"),sQuery(id+"F1.wireOp",EDGE,"E1.left"),sQuery(id+"F1.wireOp",EDGE,"E1.right")])]}),"instanceName":"1"});
            var Q1;
            Q1=makeQuery(id+"F13.opPattern","COPY",BODY,{"derivedFrom":makeQuery(id+"F4.opPattern","COPY",BODY,{"derivedFrom":makeQuery(id+"F2.opExtrude","SWEPT_BODY",BODY,{"disambiguationData":[OSD([sQuery(id+"F1.wireOp",EDGE,"E1.bottom"),sQuery(id+"F1.wireOp",EDGE,"E1.top"),sQuery(id+"F1.wireOp",EDGE,"E1.left"),sQuery(id+"F1.wireOp",EDGE,"E1.right")])]}),"instanceName":"1"}),"instanceName":"1"});
            var Q2;
            Q2=makeQuery(id+"F13.opPattern","COPY",BODY,{"derivedFrom":makeQuery(id+"F6.opPattern","COPY",BODY,{"derivedFrom":makeQuery(id+"F2.opExtrude","SWEPT_BODY",BODY,{"disambiguationData":[OSD([sQuery(id+"F1.wireOp",EDGE,"E1.bottom"),sQuery(id+"F1.wireOp",EDGE,"E1.top"),sQuery(id+"F1.wireOp",EDGE,"E1.left"),sQuery(id+"F1.wireOp",EDGE,"E1.right")])]}),"instanceName":"1"}),"instanceName":"1"});
            var Q3;
            Q3=makeQuery(id+"F13.opPattern","COPY",BODY,{"derivedFrom":makeQuery(id+"F6.opPattern","COPY",BODY,{"derivedFrom":makeQuery(id+"F4.opPattern","COPY",BODY,{"derivedFrom":makeQuery(id+"F2.opExtrude","SWEPT_BODY",BODY,{"disambiguationData":[OSD([sQuery(id+"F1.wireOp",EDGE,"E1.bottom"),sQuery(id+"F1.wireOp",EDGE,"E1.top"),sQuery(id+"F1.wireOp",EDGE,"E1.left"),sQuery(id+"F1.wireOp",EDGE,"E1.right")])]}),"instanceName":"1"}),"instanceName":"1"}),"instanceName":"1"});
            var Q4;
            Q4=makeQuery(id+"F13.opPattern","COPY",BODY,{"derivedFrom":makeQuery(id+"F11.opPattern","COPY",BODY,{"derivedFrom":makeQuery(id+"F2.opExtrude","SWEPT_BODY",BODY,{"disambiguationData":[OSD([sQuery(id+"F1.wireOp",EDGE,"E1.bottom"),sQuery(id+"F1.wireOp",EDGE,"E1.top"),sQuery(id+"F1.wireOp",EDGE,"E1.left"),sQuery(id+"F1.wireOp",EDGE,"E1.right")])]}),"instanceName":"1"}),"instanceName":"1"});
            var Q5;
            Q5=makeQuery(id+"F13.opPattern","COPY",BODY,{"derivedFrom":makeQuery(id+"F11.opPattern","COPY",BODY,{"derivedFrom":makeQuery(id+"F6.opPattern","COPY",BODY,{"derivedFrom":makeQuery(id+"F2.opExtrude","SWEPT_BODY",BODY,{"disambiguationData":[OSD([sQuery(id+"F1.wireOp",EDGE,"E1.bottom"),sQuery(id+"F1.wireOp",EDGE,"E1.top"),sQuery(id+"F1.wireOp",EDGE,"E1.left"),sQuery(id+"F1.wireOp",EDGE,"E1.right")])]}),"instanceName":"1"}),"instanceName":"1"}),"instanceName":"1"});
            deleteBodies(context, id + "F31", {"entities" : qUnion([Q0, Q1, Q2, Q3, Q4, Q5])});
        }
        {
            var Q0;
            Q0=makeQuery(id+"F22.opPattern","COPY",BODY,{"derivedFrom":makeQuery(id+"F15.opPattern","COPY",BODY,{"derivedFrom":makeQuery(id+"F11.opPattern","COPY",BODY,{"derivedFrom":makeQuery(id+"F4.opPattern","COPY",BODY,{"derivedFrom":makeQuery(id+"F2.opExtrude","SWEPT_BODY",BODY,{"disambiguationData":[OSD([sQuery(id+"F1.wireOp",EDGE,"E1.bottom"),sQuery(id+"F1.wireOp",EDGE,"E1.top"),sQuery(id+"F1.wireOp",EDGE,"E1.left"),sQuery(id+"F1.wireOp",EDGE,"E1.right")])]}),"instanceName":"1"}),"instanceName":"1"}),"instanceName":"1"}),"instanceName":"1"});
            var Q1;
            Q1=makeQuery(id+"F22.opPattern","COPY",BODY,{"derivedFrom":makeQuery(id+"F15.opPattern","COPY",BODY,{"derivedFrom":makeQuery(id+"F13.opPattern","COPY",BODY,{"derivedFrom":makeQuery(id+"F11.opPattern","COPY",BODY,{"derivedFrom":makeQuery(id+"F6.opPattern","COPY",BODY,{"derivedFrom":makeQuery(id+"F2.opExtrude","SWEPT_BODY",BODY,{"disambiguationData":[OSD([sQuery(id+"F1.wireOp",EDGE,"E1.bottom"),sQuery(id+"F1.wireOp",EDGE,"E1.top"),sQuery(id+"F1.wireOp",EDGE,"E1.left"),sQuery(id+"F1.wireOp",EDGE,"E1.right")])]}),"instanceName":"1"}),"instanceName":"1"}),"instanceName":"1"}),"instanceName":"1"}),"instanceName":"1"});
            var Q2;
            Q2=makeQuery(id+"F20.opPattern","COPY",BODY,{"derivedFrom":makeQuery(id+"F15.opPattern","COPY",BODY,{"derivedFrom":makeQuery(id+"F13.opPattern","COPY",BODY,{"derivedFrom":makeQuery(id+"F11.opPattern","COPY",BODY,{"derivedFrom":makeQuery(id+"F4.opPattern","COPY",BODY,{"derivedFrom":makeQuery(id+"F2.opExtrude","SWEPT_BODY",BODY,{"disambiguationData":[OSD([sQuery(id+"F1.wireOp",EDGE,"E1.bottom"),sQuery(id+"F1.wireOp",EDGE,"E1.top"),sQuery(id+"F1.wireOp",EDGE,"E1.left"),sQuery(id+"F1.wireOp",EDGE,"E1.right")])]}),"instanceName":"1"}),"instanceName":"1"}),"instanceName":"1"}),"instanceName":"1"}),"instanceName":"1"});
            var Q3;
            Q3=makeQuery(id+"F13.opPattern","COPY",BODY,{"derivedFrom":makeQuery(id+"F11.opPattern","COPY",BODY,{"derivedFrom":makeQuery(id+"F4.opPattern","COPY",BODY,{"derivedFrom":makeQuery(id+"F2.opExtrude","SWEPT_BODY",BODY,{"disambiguationData":[OSD([sQuery(id+"F1.wireOp",EDGE,"E1.bottom"),sQuery(id+"F1.wireOp",EDGE,"E1.top"),sQuery(id+"F1.wireOp",EDGE,"E1.left"),sQuery(id+"F1.wireOp",EDGE,"E1.right")])]}),"instanceName":"1"}),"instanceName":"1"}),"instanceName":"1"});
            var Q4;
            Q4=makeQuery(id+"F15.opPattern","COPY",BODY,{"derivedFrom":makeQuery(id+"F2.opExtrude","SWEPT_BODY",BODY,{"disambiguationData":[OSD([sQuery(id+"F1.wireOp",EDGE,"E1.bottom"),sQuery(id+"F1.wireOp",EDGE,"E1.top"),sQuery(id+"F1.wireOp",EDGE,"E1.left"),sQuery(id+"F1.wireOp",EDGE,"E1.right")])]}),"instanceName":"1"});
            deleteBodies(context, id + "F32", {"entities" : qUnion([Q0, Q1, Q2, Q3, Q4])});
        }
        {
            var Q0;
            Q0=makeQuery(id+"F20.opPattern","COPY",BODY,{"derivedFrom":makeQuery(id+"F15.opPattern","COPY",BODY,{"derivedFrom":makeQuery(id+"F13.opPattern","COPY",BODY,{"derivedFrom":makeQuery(id+"F11.opPattern","COPY",BODY,{"derivedFrom":makeQuery(id+"F6.opPattern","COPY",BODY,{"derivedFrom":makeQuery(id+"F4.opPattern","COPY",BODY,{"derivedFrom":makeQuery(id+"F2.opExtrude","SWEPT_BODY",BODY,{"disambiguationData":[OSD([sQuery(id+"F1.wireOp",EDGE,"E1.bottom"),sQuery(id+"F1.wireOp",EDGE,"E1.top"),sQuery(id+"F1.wireOp",EDGE,"E1.left"),sQuery(id+"F1.wireOp",EDGE,"E1.right")])]}),"instanceName":"1"}),"instanceName":"1"}),"instanceName":"1"}),"instanceName":"1"}),"instanceName":"1"}),"instanceName":"1"});
            var Q1;
            Q1=makeQuery(id+"F20.opPattern","COPY",BODY,{"derivedFrom":makeQuery(id+"F15.opPattern","COPY",BODY,{"derivedFrom":makeQuery(id+"F11.opPattern","COPY",BODY,{"derivedFrom":makeQuery(id+"F6.opPattern","COPY",BODY,{"derivedFrom":makeQuery(id+"F4.opPattern","COPY",BODY,{"derivedFrom":makeQuery(id+"F2.opExtrude","SWEPT_BODY",BODY,{"disambiguationData":[OSD([sQuery(id+"F1.wireOp",EDGE,"E1.bottom"),sQuery(id+"F1.wireOp",EDGE,"E1.top"),sQuery(id+"F1.wireOp",EDGE,"E1.left"),sQuery(id+"F1.wireOp",EDGE,"E1.right")])]}),"instanceName":"1"}),"instanceName":"1"}),"instanceName":"1"}),"instanceName":"1"}),"instanceName":"1"});
            var Q2;
            Q2=makeQuery(id+"F20.opPattern","COPY",BODY,{"derivedFrom":makeQuery(id+"F15.opPattern","COPY",BODY,{"derivedFrom":makeQuery(id+"F11.opPattern","COPY",BODY,{"derivedFrom":makeQuery(id+"F6.opPattern","COPY",BODY,{"derivedFrom":makeQuery(id+"F2.opExtrude","SWEPT_BODY",BODY,{"disambiguationData":[OSD([sQuery(id+"F1.wireOp",EDGE,"E1.bottom"),sQuery(id+"F1.wireOp",EDGE,"E1.top"),sQuery(id+"F1.wireOp",EDGE,"E1.left"),sQuery(id+"F1.wireOp",EDGE,"E1.right")])]}),"instanceName":"1"}),"instanceName":"1"}),"instanceName":"1"}),"instanceName":"1"});
            var Q3;
            Q3=makeQuery(id+"F20.opPattern","COPY",BODY,{"derivedFrom":makeQuery(id+"F15.opPattern","COPY",BODY,{"derivedFrom":makeQuery(id+"F11.opPattern","COPY",BODY,{"derivedFrom":makeQuery(id+"F4.opPattern","COPY",BODY,{"derivedFrom":makeQuery(id+"F2.opExtrude","SWEPT_BODY",BODY,{"disambiguationData":[OSD([sQuery(id+"F1.wireOp",EDGE,"E1.bottom"),sQuery(id+"F1.wireOp",EDGE,"E1.top"),sQuery(id+"F1.wireOp",EDGE,"E1.left"),sQuery(id+"F1.wireOp",EDGE,"E1.right")])]}),"instanceName":"1"}),"instanceName":"1"}),"instanceName":"1"}),"instanceName":"1"});
            var Q4;
            Q4=makeQuery(id+"F20.opPattern","COPY",BODY,{"derivedFrom":makeQuery(id+"F15.opPattern","COPY",BODY,{"derivedFrom":makeQuery(id+"F11.opPattern","COPY",BODY,{"derivedFrom":makeQuery(id+"F2.opExtrude","SWEPT_BODY",BODY,{"disambiguationData":[OSD([sQuery(id+"F1.wireOp",EDGE,"E1.bottom"),sQuery(id+"F1.wireOp",EDGE,"E1.top"),sQuery(id+"F1.wireOp",EDGE,"E1.left"),sQuery(id+"F1.wireOp",EDGE,"E1.right")])]}),"instanceName":"1"}),"instanceName":"1"}),"instanceName":"1"});
            var Q5;
            Q5=makeQuery(id+"F20.opPattern","COPY",BODY,{"derivedFrom":makeQuery(id+"F15.opPattern","COPY",BODY,{"derivedFrom":makeQuery(id+"F6.opPattern","COPY",BODY,{"derivedFrom":makeQuery(id+"F4.opPattern","COPY",BODY,{"derivedFrom":makeQuery(id+"F2.opExtrude","SWEPT_BODY",BODY,{"disambiguationData":[OSD([sQuery(id+"F1.wireOp",EDGE,"E1.bottom"),sQuery(id+"F1.wireOp",EDGE,"E1.top"),sQuery(id+"F1.wireOp",EDGE,"E1.left"),sQuery(id+"F1.wireOp",EDGE,"E1.right")])]}),"instanceName":"1"}),"instanceName":"1"}),"instanceName":"1"}),"instanceName":"1"});
            var Q6;
            Q6=makeQuery(id+"F20.opPattern","COPY",BODY,{"derivedFrom":makeQuery(id+"F15.opPattern","COPY",BODY,{"derivedFrom":makeQuery(id+"F6.opPattern","COPY",BODY,{"derivedFrom":makeQuery(id+"F2.opExtrude","SWEPT_BODY",BODY,{"disambiguationData":[OSD([sQuery(id+"F1.wireOp",EDGE,"E1.bottom"),sQuery(id+"F1.wireOp",EDGE,"E1.top"),sQuery(id+"F1.wireOp",EDGE,"E1.left"),sQuery(id+"F1.wireOp",EDGE,"E1.right")])]}),"instanceName":"1"}),"instanceName":"1"}),"instanceName":"1"});
            var Q7;
            Q7=makeQuery(id+"F20.opPattern","COPY",BODY,{"derivedFrom":makeQuery(id+"F15.opPattern","COPY",BODY,{"derivedFrom":makeQuery(id+"F4.opPattern","COPY",BODY,{"derivedFrom":makeQuery(id+"F2.opExtrude","SWEPT_BODY",BODY,{"disambiguationData":[OSD([sQuery(id+"F1.wireOp",EDGE,"E1.bottom"),sQuery(id+"F1.wireOp",EDGE,"E1.top"),sQuery(id+"F1.wireOp",EDGE,"E1.left"),sQuery(id+"F1.wireOp",EDGE,"E1.right")])]}),"instanceName":"1"}),"instanceName":"1"}),"instanceName":"1"});
            var Q8;
            Q8=makeQuery(id+"F20.opPattern","COPY",BODY,{"derivedFrom":makeQuery(id+"F15.opPattern","COPY",BODY,{"derivedFrom":makeQuery(id+"F2.opExtrude","SWEPT_BODY",BODY,{"disambiguationData":[OSD([sQuery(id+"F1.wireOp",EDGE,"E1.bottom"),sQuery(id+"F1.wireOp",EDGE,"E1.top"),sQuery(id+"F1.wireOp",EDGE,"E1.left"),sQuery(id+"F1.wireOp",EDGE,"E1.right")])]}),"instanceName":"1"}),"instanceName":"1"});
            transform(context, id + "F33", {"entities" : qUnion([Q0, Q1, Q2, Q3, Q4, Q5, Q6, Q7, Q8]), "transformType" : TransformType.TRANSLATION_3D, "dx" : 1.78 * mm, "dy" : 0 * mm, "dz" : 0 * mm, "makeCopy" : false});
        }
        {
            var Q0;
            Q0=makeQuery(id+"F2.opExtrude","SWEPT_BODY",BODY,{"disambiguationData":[OSD([sQuery(id+"F1.wireOp",EDGE,"E1.bottom"),sQuery(id+"F1.wireOp",EDGE,"E1.top"),sQuery(id+"F1.wireOp",EDGE,"E1.left"),sQuery(id+"F1.wireOp",EDGE,"E1.right")])]});
            var Q1;
            Q1=makeQuery(id+"F4.opPattern","COPY",BODY,{"derivedFrom":makeQuery(id+"F2.opExtrude","SWEPT_BODY",BODY,{"disambiguationData":[OSD([sQuery(id+"F1.wireOp",EDGE,"E1.bottom"),sQuery(id+"F1.wireOp",EDGE,"E1.top"),sQuery(id+"F1.wireOp",EDGE,"E1.left"),sQuery(id+"F1.wireOp",EDGE,"E1.right")])]}),"instanceName":"1"});
            var Q2;
            Q2=makeQuery(id+"F6.opPattern","COPY",BODY,{"derivedFrom":makeQuery(id+"F2.opExtrude","SWEPT_BODY",BODY,{"disambiguationData":[OSD([sQuery(id+"F1.wireOp",EDGE,"E1.bottom"),sQuery(id+"F1.wireOp",EDGE,"E1.top"),sQuery(id+"F1.wireOp",EDGE,"E1.left"),sQuery(id+"F1.wireOp",EDGE,"E1.right")])]}),"instanceName":"1"});
            var Q3;
            Q3=makeQuery(id+"F6.opPattern","COPY",BODY,{"derivedFrom":makeQuery(id+"F4.opPattern","COPY",BODY,{"derivedFrom":makeQuery(id+"F2.opExtrude","SWEPT_BODY",BODY,{"disambiguationData":[OSD([sQuery(id+"F1.wireOp",EDGE,"E1.bottom"),sQuery(id+"F1.wireOp",EDGE,"E1.top"),sQuery(id+"F1.wireOp",EDGE,"E1.left"),sQuery(id+"F1.wireOp",EDGE,"E1.right")])]}),"instanceName":"1"}),"instanceName":"1"});
            var Q4;
            Q4=makeQuery(id+"F11.opPattern","COPY",BODY,{"derivedFrom":makeQuery(id+"F2.opExtrude","SWEPT_BODY",BODY,{"disambiguationData":[OSD([sQuery(id+"F1.wireOp",EDGE,"E1.bottom"),sQuery(id+"F1.wireOp",EDGE,"E1.top"),sQuery(id+"F1.wireOp",EDGE,"E1.left"),sQuery(id+"F1.wireOp",EDGE,"E1.right")])]}),"instanceName":"1"});
            var Q5;
            Q5=makeQuery(id+"F11.opPattern","COPY",BODY,{"derivedFrom":makeQuery(id+"F4.opPattern","COPY",BODY,{"derivedFrom":makeQuery(id+"F2.opExtrude","SWEPT_BODY",BODY,{"disambiguationData":[OSD([sQuery(id+"F1.wireOp",EDGE,"E1.bottom"),sQuery(id+"F1.wireOp",EDGE,"E1.top"),sQuery(id+"F1.wireOp",EDGE,"E1.left"),sQuery(id+"F1.wireOp",EDGE,"E1.right")])]}),"instanceName":"1"}),"instanceName":"1"});
            var Q6;
            Q6=makeQuery(id+"F11.opPattern","COPY",BODY,{"derivedFrom":makeQuery(id+"F6.opPattern","COPY",BODY,{"derivedFrom":makeQuery(id+"F2.opExtrude","SWEPT_BODY",BODY,{"disambiguationData":[OSD([sQuery(id+"F1.wireOp",EDGE,"E1.bottom"),sQuery(id+"F1.wireOp",EDGE,"E1.top"),sQuery(id+"F1.wireOp",EDGE,"E1.left"),sQuery(id+"F1.wireOp",EDGE,"E1.right")])]}),"instanceName":"1"}),"instanceName":"1"});
            var Q7;
            Q7=makeQuery(id+"F11.opPattern","COPY",BODY,{"derivedFrom":makeQuery(id+"F6.opPattern","COPY",BODY,{"derivedFrom":makeQuery(id+"F4.opPattern","COPY",BODY,{"derivedFrom":makeQuery(id+"F2.opExtrude","SWEPT_BODY",BODY,{"disambiguationData":[OSD([sQuery(id+"F1.wireOp",EDGE,"E1.bottom"),sQuery(id+"F1.wireOp",EDGE,"E1.top"),sQuery(id+"F1.wireOp",EDGE,"E1.left"),sQuery(id+"F1.wireOp",EDGE,"E1.right")])]}),"instanceName":"1"}),"instanceName":"1"}),"instanceName":"1"});
            var Q8;
            Q8=makeQuery(id+"F13.opPattern","COPY",BODY,{"derivedFrom":makeQuery(id+"F11.opPattern","COPY",BODY,{"derivedFrom":makeQuery(id+"F6.opPattern","COPY",BODY,{"derivedFrom":makeQuery(id+"F4.opPattern","COPY",BODY,{"derivedFrom":makeQuery(id+"F2.opExtrude","SWEPT_BODY",BODY,{"disambiguationData":[OSD([sQuery(id+"F1.wireOp",EDGE,"E1.bottom"),sQuery(id+"F1.wireOp",EDGE,"E1.top"),sQuery(id+"F1.wireOp",EDGE,"E1.left"),sQuery(id+"F1.wireOp",EDGE,"E1.right")])]}),"instanceName":"1"}),"instanceName":"1"}),"instanceName":"1"}),"instanceName":"1"});
            transform(context, id + "F34", {"entities" : qUnion([Q0, Q1, Q2, Q3, Q4, Q5, Q6, Q7, Q8]), "transformType" : TransformType.TRANSLATION_3D, "dx" : 1.27 * mm, "dy" : 0 * mm, "dz" : 0 * mm, "makeCopy" : false});
        }
        {
            var Q0;
            Q0=makeQuery(id+"F22.opPattern","COPY",BODY,{"derivedFrom":makeQuery(id+"F15.opPattern","COPY",BODY,{"derivedFrom":makeQuery(id+"F13.opPattern","COPY",BODY,{"derivedFrom":makeQuery(id+"F11.opPattern","COPY",BODY,{"derivedFrom":makeQuery(id+"F4.opPattern","COPY",BODY,{"derivedFrom":makeQuery(id+"F2.opExtrude","SWEPT_BODY",BODY,{"disambiguationData":[OSD([sQuery(id+"F1.wireOp",EDGE,"E1.bottom"),sQuery(id+"F1.wireOp",EDGE,"E1.top"),sQuery(id+"F1.wireOp",EDGE,"E1.left"),sQuery(id+"F1.wireOp",EDGE,"E1.right")])]}),"instanceName":"1"}),"instanceName":"1"}),"instanceName":"1"}),"instanceName":"1"}),"instanceName":"1"});
            deleteBodies(context, id + "F35", {"entities" : qUnion([Q0])});
        }
        {
            var Q0;
            Q0=makeQuery(id+"F22.opPattern","COPY",BODY,{"derivedFrom":makeQuery(id+"F15.opPattern","COPY",BODY,{"derivedFrom":makeQuery(id+"F13.opPattern","COPY",BODY,{"derivedFrom":makeQuery(id+"F11.opPattern","COPY",BODY,{"derivedFrom":makeQuery(id+"F6.opPattern","COPY",BODY,{"derivedFrom":makeQuery(id+"F4.opPattern","COPY",BODY,{"derivedFrom":makeQuery(id+"F2.opExtrude","SWEPT_BODY",BODY,{"disambiguationData":[OSD([sQuery(id+"F1.wireOp",EDGE,"E1.bottom"),sQuery(id+"F1.wireOp",EDGE,"E1.top"),sQuery(id+"F1.wireOp",EDGE,"E1.left"),sQuery(id+"F1.wireOp",EDGE,"E1.right")])]}),"instanceName":"1"}),"instanceName":"1"}),"instanceName":"1"}),"instanceName":"1"}),"instanceName":"1"}),"instanceName":"1"});
            var Q1;
            Q1=makeQuery(id+"F22.opPattern","COPY",BODY,{"derivedFrom":makeQuery(id+"F15.opPattern","COPY",BODY,{"derivedFrom":makeQuery(id+"F11.opPattern","COPY",BODY,{"derivedFrom":makeQuery(id+"F6.opPattern","COPY",BODY,{"derivedFrom":makeQuery(id+"F2.opExtrude","SWEPT_BODY",BODY,{"disambiguationData":[OSD([sQuery(id+"F1.wireOp",EDGE,"E1.bottom"),sQuery(id+"F1.wireOp",EDGE,"E1.top"),sQuery(id+"F1.wireOp",EDGE,"E1.left"),sQuery(id+"F1.wireOp",EDGE,"E1.right")])]}),"instanceName":"1"}),"instanceName":"1"}),"instanceName":"1"}),"instanceName":"1"});
            var Q2;
            Q2=makeQuery(id+"F22.opPattern","COPY",BODY,{"derivedFrom":makeQuery(id+"F15.opPattern","COPY",BODY,{"derivedFrom":makeQuery(id+"F11.opPattern","COPY",BODY,{"derivedFrom":makeQuery(id+"F2.opExtrude","SWEPT_BODY",BODY,{"disambiguationData":[OSD([sQuery(id+"F1.wireOp",EDGE,"E1.bottom"),sQuery(id+"F1.wireOp",EDGE,"E1.top"),sQuery(id+"F1.wireOp",EDGE,"E1.left"),sQuery(id+"F1.wireOp",EDGE,"E1.right")])]}),"instanceName":"1"}),"instanceName":"1"}),"instanceName":"1"});
            var Q3;
            Q3=makeQuery(id+"F22.opPattern","COPY",BODY,{"derivedFrom":makeQuery(id+"F15.opPattern","COPY",BODY,{"derivedFrom":makeQuery(id+"F6.opPattern","COPY",BODY,{"derivedFrom":makeQuery(id+"F4.opPattern","COPY",BODY,{"derivedFrom":makeQuery(id+"F2.opExtrude","SWEPT_BODY",BODY,{"disambiguationData":[OSD([sQuery(id+"F1.wireOp",EDGE,"E1.bottom"),sQuery(id+"F1.wireOp",EDGE,"E1.top"),sQuery(id+"F1.wireOp",EDGE,"E1.left"),sQuery(id+"F1.wireOp",EDGE,"E1.right")])]}),"instanceName":"1"}),"instanceName":"1"}),"instanceName":"1"}),"instanceName":"1"});
            var Q4;
            Q4=makeQuery(id+"F22.opPattern","COPY",BODY,{"derivedFrom":makeQuery(id+"F15.opPattern","COPY",BODY,{"derivedFrom":makeQuery(id+"F6.opPattern","COPY",BODY,{"derivedFrom":makeQuery(id+"F2.opExtrude","SWEPT_BODY",BODY,{"disambiguationData":[OSD([sQuery(id+"F1.wireOp",EDGE,"E1.bottom"),sQuery(id+"F1.wireOp",EDGE,"E1.top"),sQuery(id+"F1.wireOp",EDGE,"E1.left"),sQuery(id+"F1.wireOp",EDGE,"E1.right")])]}),"instanceName":"1"}),"instanceName":"1"}),"instanceName":"1"});
            var Q5;
            Q5=makeQuery(id+"F22.opPattern","COPY",BODY,{"derivedFrom":makeQuery(id+"F15.opPattern","COPY",BODY,{"derivedFrom":makeQuery(id+"F4.opPattern","COPY",BODY,{"derivedFrom":makeQuery(id+"F2.opExtrude","SWEPT_BODY",BODY,{"disambiguationData":[OSD([sQuery(id+"F1.wireOp",EDGE,"E1.bottom"),sQuery(id+"F1.wireOp",EDGE,"E1.top"),sQuery(id+"F1.wireOp",EDGE,"E1.left"),sQuery(id+"F1.wireOp",EDGE,"E1.right")])]}),"instanceName":"1"}),"instanceName":"1"}),"instanceName":"1"});
            var Q6;
            Q6=makeQuery(id+"F22.opPattern","COPY",BODY,{"derivedFrom":makeQuery(id+"F15.opPattern","COPY",BODY,{"derivedFrom":makeQuery(id+"F2.opExtrude","SWEPT_BODY",BODY,{"disambiguationData":[OSD([sQuery(id+"F1.wireOp",EDGE,"E1.bottom"),sQuery(id+"F1.wireOp",EDGE,"E1.top"),sQuery(id+"F1.wireOp",EDGE,"E1.left"),sQuery(id+"F1.wireOp",EDGE,"E1.right")])]}),"instanceName":"1"}),"instanceName":"1"});
            var Q7;
            Q7=makeQuery(id+"F15.opPattern","COPY",BODY,{"derivedFrom":makeQuery(id+"F4.opPattern","COPY",BODY,{"derivedFrom":makeQuery(id+"F2.opExtrude","SWEPT_BODY",BODY,{"disambiguationData":[OSD([sQuery(id+"F1.wireOp",EDGE,"E1.bottom"),sQuery(id+"F1.wireOp",EDGE,"E1.top"),sQuery(id+"F1.wireOp",EDGE,"E1.left"),sQuery(id+"F1.wireOp",EDGE,"E1.right")])]}),"instanceName":"1"}),"instanceName":"1"});
            var Q8;
            Q8=makeQuery(id+"F15.opPattern","COPY",BODY,{"derivedFrom":makeQuery(id+"F11.opPattern","COPY",BODY,{"derivedFrom":makeQuery(id+"F6.opPattern","COPY",BODY,{"derivedFrom":makeQuery(id+"F4.opPattern","COPY",BODY,{"derivedFrom":makeQuery(id+"F2.opExtrude","SWEPT_BODY",BODY,{"disambiguationData":[OSD([sQuery(id+"F1.wireOp",EDGE,"E1.bottom"),sQuery(id+"F1.wireOp",EDGE,"E1.top"),sQuery(id+"F1.wireOp",EDGE,"E1.left"),sQuery(id+"F1.wireOp",EDGE,"E1.right")])]}),"instanceName":"1"}),"instanceName":"1"}),"instanceName":"1"}),"instanceName":"1"});
            var Q9;
            Q9=makeQuery(id+"F15.opPattern","COPY",BODY,{"derivedFrom":makeQuery(id+"F11.opPattern","COPY",BODY,{"derivedFrom":makeQuery(id+"F6.opPattern","COPY",BODY,{"derivedFrom":makeQuery(id+"F2.opExtrude","SWEPT_BODY",BODY,{"disambiguationData":[OSD([sQuery(id+"F1.wireOp",EDGE,"E1.bottom"),sQuery(id+"F1.wireOp",EDGE,"E1.top"),sQuery(id+"F1.wireOp",EDGE,"E1.left"),sQuery(id+"F1.wireOp",EDGE,"E1.right")])]}),"instanceName":"1"}),"instanceName":"1"}),"instanceName":"1"});
            var Q10;
            Q10=makeQuery(id+"F15.opPattern","COPY",BODY,{"derivedFrom":makeQuery(id+"F11.opPattern","COPY",BODY,{"derivedFrom":makeQuery(id+"F4.opPattern","COPY",BODY,{"derivedFrom":makeQuery(id+"F2.opExtrude","SWEPT_BODY",BODY,{"disambiguationData":[OSD([sQuery(id+"F1.wireOp",EDGE,"E1.bottom"),sQuery(id+"F1.wireOp",EDGE,"E1.top"),sQuery(id+"F1.wireOp",EDGE,"E1.left"),sQuery(id+"F1.wireOp",EDGE,"E1.right")])]}),"instanceName":"1"}),"instanceName":"1"}),"instanceName":"1"});
            var Q11;
            Q11=makeQuery(id+"F15.opPattern","COPY",BODY,{"derivedFrom":makeQuery(id+"F11.opPattern","COPY",BODY,{"derivedFrom":makeQuery(id+"F2.opExtrude","SWEPT_BODY",BODY,{"disambiguationData":[OSD([sQuery(id+"F1.wireOp",EDGE,"E1.bottom"),sQuery(id+"F1.wireOp",EDGE,"E1.top"),sQuery(id+"F1.wireOp",EDGE,"E1.left"),sQuery(id+"F1.wireOp",EDGE,"E1.right")])]}),"instanceName":"1"}),"instanceName":"1"});
            var Q12;
            Q12=makeQuery(id+"F15.opPattern","COPY",BODY,{"derivedFrom":makeQuery(id+"F6.opPattern","COPY",BODY,{"derivedFrom":makeQuery(id+"F4.opPattern","COPY",BODY,{"derivedFrom":makeQuery(id+"F2.opExtrude","SWEPT_BODY",BODY,{"disambiguationData":[OSD([sQuery(id+"F1.wireOp",EDGE,"E1.bottom"),sQuery(id+"F1.wireOp",EDGE,"E1.top"),sQuery(id+"F1.wireOp",EDGE,"E1.left"),sQuery(id+"F1.wireOp",EDGE,"E1.right")])]}),"instanceName":"1"}),"instanceName":"1"}),"instanceName":"1"});
            var Q13;
            Q13=makeQuery(id+"F15.opPattern","COPY",BODY,{"derivedFrom":makeQuery(id+"F6.opPattern","COPY",BODY,{"derivedFrom":makeQuery(id+"F2.opExtrude","SWEPT_BODY",BODY,{"disambiguationData":[OSD([sQuery(id+"F1.wireOp",EDGE,"E1.bottom"),sQuery(id+"F1.wireOp",EDGE,"E1.top"),sQuery(id+"F1.wireOp",EDGE,"E1.left"),sQuery(id+"F1.wireOp",EDGE,"E1.right")])]}),"instanceName":"1"}),"instanceName":"1"});
            transform(context, id + "F36", {"entities" : qUnion([Q0, Q1, Q2, Q3, Q4, Q5, Q6, Q7, Q8, Q9, Q10, Q11, Q12, Q13]), "transformType" : TransformType.TRANSLATION_3D, "dx" : 0 * mm, "dy" : -2.8 * mm, "dz" : 0 * mm, "makeCopy" : false});
        }
        {
            var Q0;
            Q0=makeQuery(id+"F22.opPattern","COPY",BODY,{"derivedFrom":makeQuery(id+"F15.opPattern","COPY",BODY,{"derivedFrom":makeQuery(id+"F11.opPattern","COPY",BODY,{"derivedFrom":makeQuery(id+"F2.opExtrude","SWEPT_BODY",BODY,{"disambiguationData":[OSD([sQuery(id+"F1.wireOp",EDGE,"E1.bottom"),sQuery(id+"F1.wireOp",EDGE,"E1.top"),sQuery(id+"F1.wireOp",EDGE,"E1.left"),sQuery(id+"F1.wireOp",EDGE,"E1.right")])]}),"instanceName":"1"}),"instanceName":"1"}),"instanceName":"1"});
            transform(context, id + "F37", {"entities" : qUnion([Q0]), "transformType" : TransformType.TRANSLATION_3D, "dx" : 0 * mm, "dy" : -0.76 * mm, "dz" : 0 * mm, "makeCopy" : false});
        }
        {
            var Q0;
            Q0=makeQuery(id+"F22.opPattern","COPY",BODY,{"derivedFrom":makeQuery(id+"F15.opPattern","COPY",BODY,{"derivedFrom":makeQuery(id+"F11.opPattern","COPY",BODY,{"derivedFrom":makeQuery(id+"F6.opPattern","COPY",BODY,{"derivedFrom":makeQuery(id+"F2.opExtrude","SWEPT_BODY",BODY,{"disambiguationData":[OSD([sQuery(id+"F1.wireOp",EDGE,"E1.bottom"),sQuery(id+"F1.wireOp",EDGE,"E1.top"),sQuery(id+"F1.wireOp",EDGE,"E1.left"),sQuery(id+"F1.wireOp",EDGE,"E1.right")])]}),"instanceName":"1"}),"instanceName":"1"}),"instanceName":"1"}),"instanceName":"1"});
            transform(context, id + "F38", {"entities" : qUnion([Q0]), "transformType" : TransformType.TRANSLATION_3D, "dx" : 0 * mm, "dy" : -1.27 * mm, "dz" : 0 * mm, "makeCopy" : false});
        }
        {
            var Q0;
            Q0=makeQuery(id+"F22.opPattern","COPY",BODY,{"derivedFrom":makeQuery(id+"F15.opPattern","COPY",BODY,{"derivedFrom":makeQuery(id+"F4.opPattern","COPY",BODY,{"derivedFrom":makeQuery(id+"F2.opExtrude","SWEPT_BODY",BODY,{"disambiguationData":[OSD([sQuery(id+"F1.wireOp",EDGE,"E1.bottom"),sQuery(id+"F1.wireOp",EDGE,"E1.top"),sQuery(id+"F1.wireOp",EDGE,"E1.left"),sQuery(id+"F1.wireOp",EDGE,"E1.right")])]}),"instanceName":"1"}),"instanceName":"1"}),"instanceName":"1"});
            transform(context, id + "F39", {"entities" : qUnion([Q0]), "transformType" : TransformType.TRANSLATION_3D, "dx" : 0 * mm, "dy" : 0.5 * mm, "dz" : 0 * mm, "makeCopy" : false});
        }
        {
            var Q0;
            Q0=makeQuery(id+"F22.opPattern","COPY",BODY,{"derivedFrom":makeQuery(id+"F15.opPattern","COPY",BODY,{"derivedFrom":makeQuery(id+"F6.opPattern","COPY",BODY,{"derivedFrom":makeQuery(id+"F2.opExtrude","SWEPT_BODY",BODY,{"disambiguationData":[OSD([sQuery(id+"F1.wireOp",EDGE,"E1.bottom"),sQuery(id+"F1.wireOp",EDGE,"E1.top"),sQuery(id+"F1.wireOp",EDGE,"E1.left"),sQuery(id+"F1.wireOp",EDGE,"E1.right")])]}),"instanceName":"1"}),"instanceName":"1"}),"instanceName":"1"});
            transform(context, id + "F40", {"entities" : qUnion([Q0]), "transformType" : TransformType.TRANSLATION_3D, "dx" : 0 * mm, "dy" : 0.76 * mm, "dz" : 0 * mm, "makeCopy" : false});
        }
        {
            var Q0;
            Q0=makeQuery(id+"F22.opPattern","COPY",BODY,{"derivedFrom":makeQuery(id+"F15.opPattern","COPY",BODY,{"derivedFrom":makeQuery(id+"F2.opExtrude","SWEPT_BODY",BODY,{"disambiguationData":[OSD([sQuery(id+"F1.wireOp",EDGE,"E1.bottom"),sQuery(id+"F1.wireOp",EDGE,"E1.top"),sQuery(id+"F1.wireOp",EDGE,"E1.left"),sQuery(id+"F1.wireOp",EDGE,"E1.right")])]}),"instanceName":"1"}),"instanceName":"1"});
            transform(context, id + "F41", {"entities" : qUnion([Q0]), "transformType" : TransformType.TRANSLATION_3D, "dx" : 0 * mm, "dy" : 1.27 * mm, "dz" : 0 * mm, "makeCopy" : false});
        }
        {
            var Q0;
            Q0=makeQuery(id+"F22.opPattern","COPY",BODY,{"derivedFrom":makeQuery(id+"F15.opPattern","COPY",BODY,{"derivedFrom":makeQuery(id+"F13.opPattern","COPY",BODY,{"derivedFrom":makeQuery(id+"F11.opPattern","COPY",BODY,{"derivedFrom":makeQuery(id+"F6.opPattern","COPY",BODY,{"derivedFrom":makeQuery(id+"F4.opPattern","COPY",BODY,{"derivedFrom":makeQuery(id+"F2.opExtrude","SWEPT_BODY",BODY,{"disambiguationData":[OSD([sQuery(id+"F1.wireOp",EDGE,"E1.bottom"),sQuery(id+"F1.wireOp",EDGE,"E1.top"),sQuery(id+"F1.wireOp",EDGE,"E1.left"),sQuery(id+"F1.wireOp",EDGE,"E1.right")])]}),"instanceName":"1"}),"instanceName":"1"}),"instanceName":"1"}),"instanceName":"1"}),"instanceName":"1"}),"instanceName":"1"});
            transform(context, id + "F42", {"entities" : qUnion([Q0]), "transformType" : TransformType.TRANSLATION_3D, "dx" : 0 * mm, "dy" : 1.27 * mm, "dz" : 0 * mm, "makeCopy" : false});
        }
        {
            var Q0;
            Q0=makeQuery(id+"F15.opPattern","COPY",BODY,{"derivedFrom":makeQuery(id+"F4.opPattern","COPY",BODY,{"derivedFrom":makeQuery(id+"F2.opExtrude","SWEPT_BODY",BODY,{"disambiguationData":[OSD([sQuery(id+"F1.wireOp",EDGE,"E1.bottom"),sQuery(id+"F1.wireOp",EDGE,"E1.top"),sQuery(id+"F1.wireOp",EDGE,"E1.left"),sQuery(id+"F1.wireOp",EDGE,"E1.right")])]}),"instanceName":"1"}),"instanceName":"1"});
            var Q1;
            Q1=makeQuery(id+"F15.opPattern","COPY",BODY,{"derivedFrom":makeQuery(id+"F11.opPattern","COPY",BODY,{"derivedFrom":makeQuery(id+"F6.opPattern","COPY",BODY,{"derivedFrom":makeQuery(id+"F4.opPattern","COPY",BODY,{"derivedFrom":makeQuery(id+"F2.opExtrude","SWEPT_BODY",BODY,{"disambiguationData":[OSD([sQuery(id+"F1.wireOp",EDGE,"E1.bottom"),sQuery(id+"F1.wireOp",EDGE,"E1.top"),sQuery(id+"F1.wireOp",EDGE,"E1.left"),sQuery(id+"F1.wireOp",EDGE,"E1.right")])]}),"instanceName":"1"}),"instanceName":"1"}),"instanceName":"1"}),"instanceName":"1"});
            var Q2;
            Q2=makeQuery(id+"F15.opPattern","COPY",BODY,{"derivedFrom":makeQuery(id+"F11.opPattern","COPY",BODY,{"derivedFrom":makeQuery(id+"F6.opPattern","COPY",BODY,{"derivedFrom":makeQuery(id+"F2.opExtrude","SWEPT_BODY",BODY,{"disambiguationData":[OSD([sQuery(id+"F1.wireOp",EDGE,"E1.bottom"),sQuery(id+"F1.wireOp",EDGE,"E1.top"),sQuery(id+"F1.wireOp",EDGE,"E1.left"),sQuery(id+"F1.wireOp",EDGE,"E1.right")])]}),"instanceName":"1"}),"instanceName":"1"}),"instanceName":"1"});
            var Q3;
            Q3=makeQuery(id+"F15.opPattern","COPY",BODY,{"derivedFrom":makeQuery(id+"F11.opPattern","COPY",BODY,{"derivedFrom":makeQuery(id+"F4.opPattern","COPY",BODY,{"derivedFrom":makeQuery(id+"F2.opExtrude","SWEPT_BODY",BODY,{"disambiguationData":[OSD([sQuery(id+"F1.wireOp",EDGE,"E1.bottom"),sQuery(id+"F1.wireOp",EDGE,"E1.top"),sQuery(id+"F1.wireOp",EDGE,"E1.left"),sQuery(id+"F1.wireOp",EDGE,"E1.right")])]}),"instanceName":"1"}),"instanceName":"1"}),"instanceName":"1"});
            var Q4;
            Q4=makeQuery(id+"F15.opPattern","COPY",BODY,{"derivedFrom":makeQuery(id+"F11.opPattern","COPY",BODY,{"derivedFrom":makeQuery(id+"F2.opExtrude","SWEPT_BODY",BODY,{"disambiguationData":[OSD([sQuery(id+"F1.wireOp",EDGE,"E1.bottom"),sQuery(id+"F1.wireOp",EDGE,"E1.top"),sQuery(id+"F1.wireOp",EDGE,"E1.left"),sQuery(id+"F1.wireOp",EDGE,"E1.right")])]}),"instanceName":"1"}),"instanceName":"1"});
            var Q5;
            Q5=makeQuery(id+"F15.opPattern","COPY",BODY,{"derivedFrom":makeQuery(id+"F6.opPattern","COPY",BODY,{"derivedFrom":makeQuery(id+"F4.opPattern","COPY",BODY,{"derivedFrom":makeQuery(id+"F2.opExtrude","SWEPT_BODY",BODY,{"disambiguationData":[OSD([sQuery(id+"F1.wireOp",EDGE,"E1.bottom"),sQuery(id+"F1.wireOp",EDGE,"E1.top"),sQuery(id+"F1.wireOp",EDGE,"E1.left"),sQuery(id+"F1.wireOp",EDGE,"E1.right")])]}),"instanceName":"1"}),"instanceName":"1"}),"instanceName":"1"});
            var Q6;
            Q6=makeQuery(id+"F15.opPattern","COPY",BODY,{"derivedFrom":makeQuery(id+"F6.opPattern","COPY",BODY,{"derivedFrom":makeQuery(id+"F2.opExtrude","SWEPT_BODY",BODY,{"disambiguationData":[OSD([sQuery(id+"F1.wireOp",EDGE,"E1.bottom"),sQuery(id+"F1.wireOp",EDGE,"E1.top"),sQuery(id+"F1.wireOp",EDGE,"E1.left"),sQuery(id+"F1.wireOp",EDGE,"E1.right")])]}),"instanceName":"1"}),"instanceName":"1"});
            deleteBodies(context, id + "F43", {"entities" : qUnion([Q0, Q1, Q2, Q3, Q4, Q5, Q6])});
        }
        {
            var Q0;
            Q0=makeQuery(id+"F22.opPattern","COPY",BODY,{"derivedFrom":makeQuery(id+"F15.opPattern","COPY",BODY,{"derivedFrom":makeQuery(id+"F13.opPattern","COPY",BODY,{"derivedFrom":makeQuery(id+"F11.opPattern","COPY",BODY,{"derivedFrom":makeQuery(id+"F6.opPattern","COPY",BODY,{"derivedFrom":makeQuery(id+"F4.opPattern","COPY",BODY,{"derivedFrom":makeQuery(id+"F2.opExtrude","SWEPT_BODY",BODY,{"disambiguationData":[OSD([sQuery(id+"F1.wireOp",EDGE,"E1.bottom"),sQuery(id+"F1.wireOp",EDGE,"E1.top"),sQuery(id+"F1.wireOp",EDGE,"E1.left"),sQuery(id+"F1.wireOp",EDGE,"E1.right")])]}),"instanceName":"1"}),"instanceName":"1"}),"instanceName":"1"}),"instanceName":"1"}),"instanceName":"1"}),"instanceName":"1"});
            var Q1;
            Q1=makeQuery(id+"F22.opPattern","COPY",BODY,{"derivedFrom":makeQuery(id+"F15.opPattern","COPY",BODY,{"derivedFrom":makeQuery(id+"F11.opPattern","COPY",BODY,{"derivedFrom":makeQuery(id+"F6.opPattern","COPY",BODY,{"derivedFrom":makeQuery(id+"F2.opExtrude","SWEPT_BODY",BODY,{"disambiguationData":[OSD([sQuery(id+"F1.wireOp",EDGE,"E1.bottom"),sQuery(id+"F1.wireOp",EDGE,"E1.top"),sQuery(id+"F1.wireOp",EDGE,"E1.left"),sQuery(id+"F1.wireOp",EDGE,"E1.right")])]}),"instanceName":"1"}),"instanceName":"1"}),"instanceName":"1"}),"instanceName":"1"});
            var Q2;
            Q2=makeQuery(id+"F22.opPattern","COPY",BODY,{"derivedFrom":makeQuery(id+"F15.opPattern","COPY",BODY,{"derivedFrom":makeQuery(id+"F11.opPattern","COPY",BODY,{"derivedFrom":makeQuery(id+"F2.opExtrude","SWEPT_BODY",BODY,{"disambiguationData":[OSD([sQuery(id+"F1.wireOp",EDGE,"E1.bottom"),sQuery(id+"F1.wireOp",EDGE,"E1.top"),sQuery(id+"F1.wireOp",EDGE,"E1.left"),sQuery(id+"F1.wireOp",EDGE,"E1.right")])]}),"instanceName":"1"}),"instanceName":"1"}),"instanceName":"1"});
            var Q3;
            Q3=makeQuery(id+"F22.opPattern","COPY",BODY,{"derivedFrom":makeQuery(id+"F15.opPattern","COPY",BODY,{"derivedFrom":makeQuery(id+"F6.opPattern","COPY",BODY,{"derivedFrom":makeQuery(id+"F4.opPattern","COPY",BODY,{"derivedFrom":makeQuery(id+"F2.opExtrude","SWEPT_BODY",BODY,{"disambiguationData":[OSD([sQuery(id+"F1.wireOp",EDGE,"E1.bottom"),sQuery(id+"F1.wireOp",EDGE,"E1.top"),sQuery(id+"F1.wireOp",EDGE,"E1.left"),sQuery(id+"F1.wireOp",EDGE,"E1.right")])]}),"instanceName":"1"}),"instanceName":"1"}),"instanceName":"1"}),"instanceName":"1"});
            var Q4;
            Q4=makeQuery(id+"F22.opPattern","COPY",BODY,{"derivedFrom":makeQuery(id+"F15.opPattern","COPY",BODY,{"derivedFrom":makeQuery(id+"F6.opPattern","COPY",BODY,{"derivedFrom":makeQuery(id+"F2.opExtrude","SWEPT_BODY",BODY,{"disambiguationData":[OSD([sQuery(id+"F1.wireOp",EDGE,"E1.bottom"),sQuery(id+"F1.wireOp",EDGE,"E1.top"),sQuery(id+"F1.wireOp",EDGE,"E1.left"),sQuery(id+"F1.wireOp",EDGE,"E1.right")])]}),"instanceName":"1"}),"instanceName":"1"}),"instanceName":"1"});
            var Q5;
            Q5=makeQuery(id+"F22.opPattern","COPY",BODY,{"derivedFrom":makeQuery(id+"F15.opPattern","COPY",BODY,{"derivedFrom":makeQuery(id+"F4.opPattern","COPY",BODY,{"derivedFrom":makeQuery(id+"F2.opExtrude","SWEPT_BODY",BODY,{"disambiguationData":[OSD([sQuery(id+"F1.wireOp",EDGE,"E1.bottom"),sQuery(id+"F1.wireOp",EDGE,"E1.top"),sQuery(id+"F1.wireOp",EDGE,"E1.left"),sQuery(id+"F1.wireOp",EDGE,"E1.right")])]}),"instanceName":"1"}),"instanceName":"1"}),"instanceName":"1"});
            var Q6;
            Q6=makeQuery(id+"F22.opPattern","COPY",BODY,{"derivedFrom":makeQuery(id+"F15.opPattern","COPY",BODY,{"derivedFrom":makeQuery(id+"F2.opExtrude","SWEPT_BODY",BODY,{"disambiguationData":[OSD([sQuery(id+"F1.wireOp",EDGE,"E1.bottom"),sQuery(id+"F1.wireOp",EDGE,"E1.top"),sQuery(id+"F1.wireOp",EDGE,"E1.left"),sQuery(id+"F1.wireOp",EDGE,"E1.right")])]}),"instanceName":"1"}),"instanceName":"1"});
            transform(context, id + "F44", {"entities" : qUnion([Q0, Q1, Q2, Q3, Q4, Q5, Q6]), "transformType" : TransformType.COPY});
        }
        {
            var Q0;
            Q0=makeQuery(id+"F22.opPattern","COPY",BODY,{"derivedFrom":makeQuery(id+"F15.opPattern","COPY",BODY,{"derivedFrom":makeQuery(id+"F11.opPattern","COPY",BODY,{"derivedFrom":makeQuery(id+"F6.opPattern","COPY",BODY,{"derivedFrom":makeQuery(id+"F2.opExtrude","SWEPT_BODY",BODY,{"disambiguationData":[OSD([sQuery(id+"F1.wireOp",EDGE,"E1.bottom"),sQuery(id+"F1.wireOp",EDGE,"E1.top"),sQuery(id+"F1.wireOp",EDGE,"E1.left"),sQuery(id+"F1.wireOp",EDGE,"E1.right")])]}),"instanceName":"1"}),"instanceName":"1"}),"instanceName":"1"}),"instanceName":"1"});
            var Q1;
            Q1=makeQuery(id+"F44.opPattern","COPY",BODY,{"derivedFrom":makeQuery(id+"F22.opPattern","COPY",BODY,{"derivedFrom":makeQuery(id+"F15.opPattern","COPY",BODY,{"derivedFrom":makeQuery(id+"F11.opPattern","COPY",BODY,{"derivedFrom":makeQuery(id+"F2.opExtrude","SWEPT_BODY",BODY,{"disambiguationData":[OSD([sQuery(id+"F1.wireOp",EDGE,"E1.bottom"),sQuery(id+"F1.wireOp",EDGE,"E1.top"),sQuery(id+"F1.wireOp",EDGE,"E1.left"),sQuery(id+"F1.wireOp",EDGE,"E1.right")])]}),"instanceName":"1"}),"instanceName":"1"}),"instanceName":"1"}),"instanceName":"1"});
            var Q2;
            Q2=makeQuery(id+"F44.opPattern","COPY",BODY,{"derivedFrom":makeQuery(id+"F22.opPattern","COPY",BODY,{"derivedFrom":makeQuery(id+"F15.opPattern","COPY",BODY,{"derivedFrom":makeQuery(id+"F6.opPattern","COPY",BODY,{"derivedFrom":makeQuery(id+"F4.opPattern","COPY",BODY,{"derivedFrom":makeQuery(id+"F2.opExtrude","SWEPT_BODY",BODY,{"disambiguationData":[OSD([sQuery(id+"F1.wireOp",EDGE,"E1.bottom"),sQuery(id+"F1.wireOp",EDGE,"E1.top"),sQuery(id+"F1.wireOp",EDGE,"E1.left"),sQuery(id+"F1.wireOp",EDGE,"E1.right")])]}),"instanceName":"1"}),"instanceName":"1"}),"instanceName":"1"}),"instanceName":"1"}),"instanceName":"1"});
            var Q3;
            Q3=makeQuery(id+"F44.opPattern","COPY",BODY,{"derivedFrom":makeQuery(id+"F22.opPattern","COPY",BODY,{"derivedFrom":makeQuery(id+"F15.opPattern","COPY",BODY,{"derivedFrom":makeQuery(id+"F4.opPattern","COPY",BODY,{"derivedFrom":makeQuery(id+"F2.opExtrude","SWEPT_BODY",BODY,{"disambiguationData":[OSD([sQuery(id+"F1.wireOp",EDGE,"E1.bottom"),sQuery(id+"F1.wireOp",EDGE,"E1.top"),sQuery(id+"F1.wireOp",EDGE,"E1.left"),sQuery(id+"F1.wireOp",EDGE,"E1.right")])]}),"instanceName":"1"}),"instanceName":"1"}),"instanceName":"1"}),"instanceName":"1"});
            var Q4;
            Q4=makeQuery(id+"F44.opPattern","COPY",BODY,{"derivedFrom":makeQuery(id+"F22.opPattern","COPY",BODY,{"derivedFrom":makeQuery(id+"F15.opPattern","COPY",BODY,{"derivedFrom":makeQuery(id+"F6.opPattern","COPY",BODY,{"derivedFrom":makeQuery(id+"F2.opExtrude","SWEPT_BODY",BODY,{"disambiguationData":[OSD([sQuery(id+"F1.wireOp",EDGE,"E1.bottom"),sQuery(id+"F1.wireOp",EDGE,"E1.top"),sQuery(id+"F1.wireOp",EDGE,"E1.left"),sQuery(id+"F1.wireOp",EDGE,"E1.right")])]}),"instanceName":"1"}),"instanceName":"1"}),"instanceName":"1"}),"instanceName":"1"});
            var Q5;
            Q5=makeQuery(id+"F44.opPattern","COPY",BODY,{"derivedFrom":makeQuery(id+"F22.opPattern","COPY",BODY,{"derivedFrom":makeQuery(id+"F15.opPattern","COPY",BODY,{"derivedFrom":makeQuery(id+"F2.opExtrude","SWEPT_BODY",BODY,{"disambiguationData":[OSD([sQuery(id+"F1.wireOp",EDGE,"E1.bottom"),sQuery(id+"F1.wireOp",EDGE,"E1.top"),sQuery(id+"F1.wireOp",EDGE,"E1.left"),sQuery(id+"F1.wireOp",EDGE,"E1.right")])]}),"instanceName":"1"}),"instanceName":"1"}),"instanceName":"1"});
            var Q6;
            Q6=makeQuery(id+"F22.opPattern","COPY",BODY,{"derivedFrom":makeQuery(id+"F15.opPattern","COPY",BODY,{"derivedFrom":makeQuery(id+"F13.opPattern","COPY",BODY,{"derivedFrom":makeQuery(id+"F11.opPattern","COPY",BODY,{"derivedFrom":makeQuery(id+"F6.opPattern","COPY",BODY,{"derivedFrom":makeQuery(id+"F4.opPattern","COPY",BODY,{"derivedFrom":makeQuery(id+"F2.opExtrude","SWEPT_BODY",BODY,{"disambiguationData":[OSD([sQuery(id+"F1.wireOp",EDGE,"E1.bottom"),sQuery(id+"F1.wireOp",EDGE,"E1.top"),sQuery(id+"F1.wireOp",EDGE,"E1.left"),sQuery(id+"F1.wireOp",EDGE,"E1.right")])]}),"instanceName":"1"}),"instanceName":"1"}),"instanceName":"1"}),"instanceName":"1"}),"instanceName":"1"}),"instanceName":"1"});
            transform(context, id + "F45", {"entities" : qUnion([Q0, Q1, Q2, Q3, Q4, Q5, Q6]), "transformType" : TransformType.TRANSLATION_3D, "dx" : 74.68 * mm, "dy" : 0 * mm, "dz" : 0 * mm, "makeCopy" : false});
        }
        {
            var Q0;
            Q0=makeQuery(id+"F11.opPattern","COPY",BODY,{"derivedFrom":makeQuery(id+"F6.opPattern","COPY",BODY,{"derivedFrom":makeQuery(id+"F4.opPattern","COPY",BODY,{"derivedFrom":makeQuery(id+"F2.opExtrude","SWEPT_BODY",BODY,{"disambiguationData":[OSD([sQuery(id+"F1.wireOp",EDGE,"E1.bottom"),sQuery(id+"F1.wireOp",EDGE,"E1.top"),sQuery(id+"F1.wireOp",EDGE,"E1.left"),sQuery(id+"F1.wireOp",EDGE,"E1.right")])]}),"instanceName":"1"}),"instanceName":"1"}),"instanceName":"1"});
            transform(context, id + "F46", {"entities" : qUnion([Q0]), "transformType" : TransformType.TRANSLATION_3D, "dx" : 0.46 * mm, "dy" : 0 * mm, "dz" : 0 * mm, "makeCopy" : false});
        }
        {
            var Q0;
            Q0=makeQuery(id+"F11.opPattern","COPY",BODY,{"derivedFrom":makeQuery(id+"F6.opPattern","COPY",BODY,{"derivedFrom":makeQuery(id+"F2.opExtrude","SWEPT_BODY",BODY,{"disambiguationData":[OSD([sQuery(id+"F1.wireOp",EDGE,"E1.bottom"),sQuery(id+"F1.wireOp",EDGE,"E1.top"),sQuery(id+"F1.wireOp",EDGE,"E1.left"),sQuery(id+"F1.wireOp",EDGE,"E1.right")])]}),"instanceName":"1"}),"instanceName":"1"});
            transform(context, id + "F47", {"entities" : qUnion([Q0]), "transformType" : TransformType.TRANSLATION_3D, "dx" : -0.38 * mm, "dy" : 0 * mm, "dz" : 0 * mm, "makeCopy" : false});
        }
        {
            var Q0;
            Q0=makeQuery(id+"F11.opPattern","COPY",BODY,{"derivedFrom":makeQuery(id+"F2.opExtrude","SWEPT_BODY",BODY,{"disambiguationData":[OSD([sQuery(id+"F1.wireOp",EDGE,"E1.bottom"),sQuery(id+"F1.wireOp",EDGE,"E1.top"),sQuery(id+"F1.wireOp",EDGE,"E1.left"),sQuery(id+"F1.wireOp",EDGE,"E1.right")])]}),"instanceName":"1"});
            transform(context, id + "F48", {"entities" : qUnion([Q0]), "transformType" : TransformType.TRANSLATION_3D, "dx" : -0.84 * mm, "dy" : 0 * mm, "dz" : 0 * mm, "makeCopy" : false});
        }
        {
            var Q0;
            Q0=makeQuery(id+"F6.opPattern","COPY",BODY,{"derivedFrom":makeQuery(id+"F4.opPattern","COPY",BODY,{"derivedFrom":makeQuery(id+"F2.opExtrude","SWEPT_BODY",BODY,{"disambiguationData":[OSD([sQuery(id+"F1.wireOp",EDGE,"E1.bottom"),sQuery(id+"F1.wireOp",EDGE,"E1.top"),sQuery(id+"F1.wireOp",EDGE,"E1.left"),sQuery(id+"F1.wireOp",EDGE,"E1.right")])]}),"instanceName":"1"}),"instanceName":"1"});
            transform(context, id + "F49", {"entities" : qUnion([Q0]), "transformType" : TransformType.TRANSLATION_3D, "dx" : -1.52 * mm, "dy" : 0 * mm, "dz" : 0 * mm, "makeCopy" : false});
        }
        {
            var Q0;
            Q0=makeQuery(id+"F4.opPattern","COPY",BODY,{"derivedFrom":makeQuery(id+"F2.opExtrude","SWEPT_BODY",BODY,{"disambiguationData":[OSD([sQuery(id+"F1.wireOp",EDGE,"E1.bottom"),sQuery(id+"F1.wireOp",EDGE,"E1.top"),sQuery(id+"F1.wireOp",EDGE,"E1.left"),sQuery(id+"F1.wireOp",EDGE,"E1.right")])]}),"instanceName":"1"});
            transform(context, id + "F50", {"entities" : qUnion([Q0]), "transformType" : TransformType.TRANSLATION_3D, "dx" : -2.03 * mm, "dy" : 0 * mm, "dz" : 0 * mm, "makeCopy" : false});
        }
        {
            var Q0;
            Q0=makeQuery(id+"F6.opPattern","COPY",BODY,{"derivedFrom":makeQuery(id+"F2.opExtrude","SWEPT_BODY",BODY,{"disambiguationData":[OSD([sQuery(id+"F1.wireOp",EDGE,"E1.bottom"),sQuery(id+"F1.wireOp",EDGE,"E1.top"),sQuery(id+"F1.wireOp",EDGE,"E1.left"),sQuery(id+"F1.wireOp",EDGE,"E1.right")])]}),"instanceName":"1"});
            transform(context, id + "F51", {"entities" : qUnion([Q0]), "transformType" : TransformType.TRANSLATION_3D, "dx" : -2.3 * mm, "dy" : 0 * mm, "dz" : 0 * mm, "makeCopy" : false});
        }
        {
            var Q0;
            Q0=makeQuery(id+"F2.opExtrude","SWEPT_BODY",BODY,{"disambiguationData":[OSD([sQuery(id+"F1.wireOp",EDGE,"E1.bottom"),sQuery(id+"F1.wireOp",EDGE,"E1.top"),sQuery(id+"F1.wireOp",EDGE,"E1.left"),sQuery(id+"F1.wireOp",EDGE,"E1.right")])]});
            transform(context, id + "F52", {"entities" : qUnion([Q0]), "transformType" : TransformType.TRANSLATION_3D, "dx" : 0 * mm, "dy" : 0 * mm, "dz" : 0 * mm, "makeCopy" : false});
        }
        {
            var Q0;
            Q0=makeQuery(id+"F2.opExtrude","SWEPT_BODY",BODY,{"disambiguationData":[OSD([sQuery(id+"F1.wireOp",EDGE,"E1.bottom"),sQuery(id+"F1.wireOp",EDGE,"E1.top"),sQuery(id+"F1.wireOp",EDGE,"E1.left"),sQuery(id+"F1.wireOp",EDGE,"E1.right")])]});
            var Q1;
            Q1=makeQuery(id+"F13.opPattern","COPY",BODY,{"derivedFrom":makeQuery(id+"F11.opPattern","COPY",BODY,{"derivedFrom":makeQuery(id+"F6.opPattern","COPY",BODY,{"derivedFrom":makeQuery(id+"F4.opPattern","COPY",BODY,{"derivedFrom":makeQuery(id+"F2.opExtrude","SWEPT_BODY",BODY,{"disambiguationData":[OSD([sQuery(id+"F1.wireOp",EDGE,"E1.bottom"),sQuery(id+"F1.wireOp",EDGE,"E1.top"),sQuery(id+"F1.wireOp",EDGE,"E1.left"),sQuery(id+"F1.wireOp",EDGE,"E1.right")])]}),"instanceName":"1"}),"instanceName":"1"}),"instanceName":"1"}),"instanceName":"1"});
            transform(context, id + "F53", {"entities" : qUnion([Q0, Q1]), "transformType" : TransformType.TRANSLATION_3D, "dx" : -2.8 * mm, "dy" : 0 * mm, "dz" : 0 * mm, "makeCopy" : false});
        }
        {
            var Q0;
            Q0=makeQuery(id+"F20.opPattern","COPY",BODY,{"derivedFrom":makeQuery(id+"F15.opPattern","COPY",BODY,{"derivedFrom":makeQuery(id+"F13.opPattern","COPY",BODY,{"derivedFrom":makeQuery(id+"F11.opPattern","COPY",BODY,{"derivedFrom":makeQuery(id+"F6.opPattern","COPY",BODY,{"derivedFrom":makeQuery(id+"F4.opPattern","COPY",BODY,{"derivedFrom":makeQuery(id+"F2.opExtrude","SWEPT_BODY",BODY,{"disambiguationData":[OSD([sQuery(id+"F1.wireOp",EDGE,"E1.bottom"),sQuery(id+"F1.wireOp",EDGE,"E1.top"),sQuery(id+"F1.wireOp",EDGE,"E1.left"),sQuery(id+"F1.wireOp",EDGE,"E1.right")])]}),"instanceName":"1"}),"instanceName":"1"}),"instanceName":"1"}),"instanceName":"1"}),"instanceName":"1"}),"instanceName":"1"});
            var Q1;
            Q1=makeQuery(id+"F20.opPattern","COPY",BODY,{"derivedFrom":makeQuery(id+"F15.opPattern","COPY",BODY,{"derivedFrom":makeQuery(id+"F11.opPattern","COPY",BODY,{"derivedFrom":makeQuery(id+"F6.opPattern","COPY",BODY,{"derivedFrom":makeQuery(id+"F4.opPattern","COPY",BODY,{"derivedFrom":makeQuery(id+"F2.opExtrude","SWEPT_BODY",BODY,{"disambiguationData":[OSD([sQuery(id+"F1.wireOp",EDGE,"E1.bottom"),sQuery(id+"F1.wireOp",EDGE,"E1.top"),sQuery(id+"F1.wireOp",EDGE,"E1.left"),sQuery(id+"F1.wireOp",EDGE,"E1.right")])]}),"instanceName":"1"}),"instanceName":"1"}),"instanceName":"1"}),"instanceName":"1"}),"instanceName":"1"});
            var Q2;
            Q2=makeQuery(id+"F20.opPattern","COPY",BODY,{"derivedFrom":makeQuery(id+"F15.opPattern","COPY",BODY,{"derivedFrom":makeQuery(id+"F11.opPattern","COPY",BODY,{"derivedFrom":makeQuery(id+"F6.opPattern","COPY",BODY,{"derivedFrom":makeQuery(id+"F2.opExtrude","SWEPT_BODY",BODY,{"disambiguationData":[OSD([sQuery(id+"F1.wireOp",EDGE,"E1.bottom"),sQuery(id+"F1.wireOp",EDGE,"E1.top"),sQuery(id+"F1.wireOp",EDGE,"E1.left"),sQuery(id+"F1.wireOp",EDGE,"E1.right")])]}),"instanceName":"1"}),"instanceName":"1"}),"instanceName":"1"}),"instanceName":"1"});
            var Q3;
            Q3=makeQuery(id+"F20.opPattern","COPY",BODY,{"derivedFrom":makeQuery(id+"F15.opPattern","COPY",BODY,{"derivedFrom":makeQuery(id+"F11.opPattern","COPY",BODY,{"derivedFrom":makeQuery(id+"F4.opPattern","COPY",BODY,{"derivedFrom":makeQuery(id+"F2.opExtrude","SWEPT_BODY",BODY,{"disambiguationData":[OSD([sQuery(id+"F1.wireOp",EDGE,"E1.bottom"),sQuery(id+"F1.wireOp",EDGE,"E1.top"),sQuery(id+"F1.wireOp",EDGE,"E1.left"),sQuery(id+"F1.wireOp",EDGE,"E1.right")])]}),"instanceName":"1"}),"instanceName":"1"}),"instanceName":"1"}),"instanceName":"1"});
            var Q4;
            Q4=makeQuery(id+"F20.opPattern","COPY",BODY,{"derivedFrom":makeQuery(id+"F15.opPattern","COPY",BODY,{"derivedFrom":makeQuery(id+"F11.opPattern","COPY",BODY,{"derivedFrom":makeQuery(id+"F2.opExtrude","SWEPT_BODY",BODY,{"disambiguationData":[OSD([sQuery(id+"F1.wireOp",EDGE,"E1.bottom"),sQuery(id+"F1.wireOp",EDGE,"E1.top"),sQuery(id+"F1.wireOp",EDGE,"E1.left"),sQuery(id+"F1.wireOp",EDGE,"E1.right")])]}),"instanceName":"1"}),"instanceName":"1"}),"instanceName":"1"});
            var Q5;
            Q5=makeQuery(id+"F20.opPattern","COPY",BODY,{"derivedFrom":makeQuery(id+"F15.opPattern","COPY",BODY,{"derivedFrom":makeQuery(id+"F6.opPattern","COPY",BODY,{"derivedFrom":makeQuery(id+"F4.opPattern","COPY",BODY,{"derivedFrom":makeQuery(id+"F2.opExtrude","SWEPT_BODY",BODY,{"disambiguationData":[OSD([sQuery(id+"F1.wireOp",EDGE,"E1.bottom"),sQuery(id+"F1.wireOp",EDGE,"E1.top"),sQuery(id+"F1.wireOp",EDGE,"E1.left"),sQuery(id+"F1.wireOp",EDGE,"E1.right")])]}),"instanceName":"1"}),"instanceName":"1"}),"instanceName":"1"}),"instanceName":"1"});
            var Q6;
            Q6=makeQuery(id+"F20.opPattern","COPY",BODY,{"derivedFrom":makeQuery(id+"F15.opPattern","COPY",BODY,{"derivedFrom":makeQuery(id+"F6.opPattern","COPY",BODY,{"derivedFrom":makeQuery(id+"F2.opExtrude","SWEPT_BODY",BODY,{"disambiguationData":[OSD([sQuery(id+"F1.wireOp",EDGE,"E1.bottom"),sQuery(id+"F1.wireOp",EDGE,"E1.top"),sQuery(id+"F1.wireOp",EDGE,"E1.left"),sQuery(id+"F1.wireOp",EDGE,"E1.right")])]}),"instanceName":"1"}),"instanceName":"1"}),"instanceName":"1"});
            var Q7;
            Q7=makeQuery(id+"F20.opPattern","COPY",BODY,{"derivedFrom":makeQuery(id+"F15.opPattern","COPY",BODY,{"derivedFrom":makeQuery(id+"F4.opPattern","COPY",BODY,{"derivedFrom":makeQuery(id+"F2.opExtrude","SWEPT_BODY",BODY,{"disambiguationData":[OSD([sQuery(id+"F1.wireOp",EDGE,"E1.bottom"),sQuery(id+"F1.wireOp",EDGE,"E1.top"),sQuery(id+"F1.wireOp",EDGE,"E1.left"),sQuery(id+"F1.wireOp",EDGE,"E1.right")])]}),"instanceName":"1"}),"instanceName":"1"}),"instanceName":"1"});
            var Q8;
            Q8=makeQuery(id+"F20.opPattern","COPY",BODY,{"derivedFrom":makeQuery(id+"F15.opPattern","COPY",BODY,{"derivedFrom":makeQuery(id+"F2.opExtrude","SWEPT_BODY",BODY,{"disambiguationData":[OSD([sQuery(id+"F1.wireOp",EDGE,"E1.bottom"),sQuery(id+"F1.wireOp",EDGE,"E1.top"),sQuery(id+"F1.wireOp",EDGE,"E1.left"),sQuery(id+"F1.wireOp",EDGE,"E1.right")])]}),"instanceName":"1"}),"instanceName":"1"});
            deleteBodies(context, id + "F54", {"entities" : qUnion([Q0, Q1, Q2, Q3, Q4, Q5, Q6, Q7, Q8])});
        }
        {
            var Q0;
            Q0=makeQuery(id+"F2.opExtrude","SWEPT_BODY",BODY,{"disambiguationData":[OSD([sQuery(id+"F1.wireOp",EDGE,"E1.bottom"),sQuery(id+"F1.wireOp",EDGE,"E1.top"),sQuery(id+"F1.wireOp",EDGE,"E1.left"),sQuery(id+"F1.wireOp",EDGE,"E1.right")])]});
            var Q1;
            Q1=makeQuery(id+"F4.opPattern","COPY",BODY,{"derivedFrom":makeQuery(id+"F2.opExtrude","SWEPT_BODY",BODY,{"disambiguationData":[OSD([sQuery(id+"F1.wireOp",EDGE,"E1.bottom"),sQuery(id+"F1.wireOp",EDGE,"E1.top"),sQuery(id+"F1.wireOp",EDGE,"E1.left"),sQuery(id+"F1.wireOp",EDGE,"E1.right")])]}),"instanceName":"1"});
            var Q2;
            Q2=makeQuery(id+"F6.opPattern","COPY",BODY,{"derivedFrom":makeQuery(id+"F2.opExtrude","SWEPT_BODY",BODY,{"disambiguationData":[OSD([sQuery(id+"F1.wireOp",EDGE,"E1.bottom"),sQuery(id+"F1.wireOp",EDGE,"E1.top"),sQuery(id+"F1.wireOp",EDGE,"E1.left"),sQuery(id+"F1.wireOp",EDGE,"E1.right")])]}),"instanceName":"1"});
            var Q3;
            Q3=makeQuery(id+"F6.opPattern","COPY",BODY,{"derivedFrom":makeQuery(id+"F4.opPattern","COPY",BODY,{"derivedFrom":makeQuery(id+"F2.opExtrude","SWEPT_BODY",BODY,{"disambiguationData":[OSD([sQuery(id+"F1.wireOp",EDGE,"E1.bottom"),sQuery(id+"F1.wireOp",EDGE,"E1.top"),sQuery(id+"F1.wireOp",EDGE,"E1.left"),sQuery(id+"F1.wireOp",EDGE,"E1.right")])]}),"instanceName":"1"}),"instanceName":"1"});
            var Q4;
            Q4=makeQuery(id+"F11.opPattern","COPY",BODY,{"derivedFrom":makeQuery(id+"F2.opExtrude","SWEPT_BODY",BODY,{"disambiguationData":[OSD([sQuery(id+"F1.wireOp",EDGE,"E1.bottom"),sQuery(id+"F1.wireOp",EDGE,"E1.top"),sQuery(id+"F1.wireOp",EDGE,"E1.left"),sQuery(id+"F1.wireOp",EDGE,"E1.right")])]}),"instanceName":"1"});
            var Q5;
            Q5=makeQuery(id+"F11.opPattern","COPY",BODY,{"derivedFrom":makeQuery(id+"F4.opPattern","COPY",BODY,{"derivedFrom":makeQuery(id+"F2.opExtrude","SWEPT_BODY",BODY,{"disambiguationData":[OSD([sQuery(id+"F1.wireOp",EDGE,"E1.bottom"),sQuery(id+"F1.wireOp",EDGE,"E1.top"),sQuery(id+"F1.wireOp",EDGE,"E1.left"),sQuery(id+"F1.wireOp",EDGE,"E1.right")])]}),"instanceName":"1"}),"instanceName":"1"});
            var Q6;
            Q6=makeQuery(id+"F11.opPattern","COPY",BODY,{"derivedFrom":makeQuery(id+"F6.opPattern","COPY",BODY,{"derivedFrom":makeQuery(id+"F2.opExtrude","SWEPT_BODY",BODY,{"disambiguationData":[OSD([sQuery(id+"F1.wireOp",EDGE,"E1.bottom"),sQuery(id+"F1.wireOp",EDGE,"E1.top"),sQuery(id+"F1.wireOp",EDGE,"E1.left"),sQuery(id+"F1.wireOp",EDGE,"E1.right")])]}),"instanceName":"1"}),"instanceName":"1"});
            var Q7;
            Q7=makeQuery(id+"F11.opPattern","COPY",BODY,{"derivedFrom":makeQuery(id+"F6.opPattern","COPY",BODY,{"derivedFrom":makeQuery(id+"F4.opPattern","COPY",BODY,{"derivedFrom":makeQuery(id+"F2.opExtrude","SWEPT_BODY",BODY,{"disambiguationData":[OSD([sQuery(id+"F1.wireOp",EDGE,"E1.bottom"),sQuery(id+"F1.wireOp",EDGE,"E1.top"),sQuery(id+"F1.wireOp",EDGE,"E1.left"),sQuery(id+"F1.wireOp",EDGE,"E1.right")])]}),"instanceName":"1"}),"instanceName":"1"}),"instanceName":"1"});
            var Q8;
            Q8=makeQuery(id+"F13.opPattern","COPY",BODY,{"derivedFrom":makeQuery(id+"F11.opPattern","COPY",BODY,{"derivedFrom":makeQuery(id+"F6.opPattern","COPY",BODY,{"derivedFrom":makeQuery(id+"F4.opPattern","COPY",BODY,{"derivedFrom":makeQuery(id+"F2.opExtrude","SWEPT_BODY",BODY,{"disambiguationData":[OSD([sQuery(id+"F1.wireOp",EDGE,"E1.bottom"),sQuery(id+"F1.wireOp",EDGE,"E1.top"),sQuery(id+"F1.wireOp",EDGE,"E1.left"),sQuery(id+"F1.wireOp",EDGE,"E1.right")])]}),"instanceName":"1"}),"instanceName":"1"}),"instanceName":"1"}),"instanceName":"1"});
            transform(context, id + "F55", {"entities" : qUnion([Q0, Q1, Q2, Q3, Q4, Q5, Q6, Q7, Q8]), "transformType" : TransformType.COPY});
        }
        {
            var Q0;
            Q0=makeQuery(id+"F11.opPattern","COPY",BODY,{"derivedFrom":makeQuery(id+"F4.opPattern","COPY",BODY,{"derivedFrom":makeQuery(id+"F2.opExtrude","SWEPT_BODY",BODY,{"disambiguationData":[OSD([sQuery(id+"F1.wireOp",EDGE,"E1.bottom"),sQuery(id+"F1.wireOp",EDGE,"E1.top"),sQuery(id+"F1.wireOp",EDGE,"E1.left"),sQuery(id+"F1.wireOp",EDGE,"E1.right")])]}),"instanceName":"1"}),"instanceName":"1"});
            var Q1;
            Q1=makeQuery(id+"F55.opPattern","COPY",BODY,{"derivedFrom":makeQuery(id+"F11.opPattern","COPY",BODY,{"derivedFrom":makeQuery(id+"F6.opPattern","COPY",BODY,{"derivedFrom":makeQuery(id+"F2.opExtrude","SWEPT_BODY",BODY,{"disambiguationData":[OSD([sQuery(id+"F1.wireOp",EDGE,"E1.bottom"),sQuery(id+"F1.wireOp",EDGE,"E1.top"),sQuery(id+"F1.wireOp",EDGE,"E1.left"),sQuery(id+"F1.wireOp",EDGE,"E1.right")])]}),"instanceName":"1"}),"instanceName":"1"}),"instanceName":"1"});
            var Q2;
            Q2=makeQuery(id+"F11.opPattern","COPY",BODY,{"derivedFrom":makeQuery(id+"F2.opExtrude","SWEPT_BODY",BODY,{"disambiguationData":[OSD([sQuery(id+"F1.wireOp",EDGE,"E1.bottom"),sQuery(id+"F1.wireOp",EDGE,"E1.top"),sQuery(id+"F1.wireOp",EDGE,"E1.left"),sQuery(id+"F1.wireOp",EDGE,"E1.right")])]}),"instanceName":"1"});
            var Q3;
            Q3=makeQuery(id+"F11.opPattern","COPY",BODY,{"derivedFrom":makeQuery(id+"F6.opPattern","COPY",BODY,{"derivedFrom":makeQuery(id+"F4.opPattern","COPY",BODY,{"derivedFrom":makeQuery(id+"F2.opExtrude","SWEPT_BODY",BODY,{"disambiguationData":[OSD([sQuery(id+"F1.wireOp",EDGE,"E1.bottom"),sQuery(id+"F1.wireOp",EDGE,"E1.top"),sQuery(id+"F1.wireOp",EDGE,"E1.left"),sQuery(id+"F1.wireOp",EDGE,"E1.right")])]}),"instanceName":"1"}),"instanceName":"1"}),"instanceName":"1"});
            var Q4;
            Q4=makeQuery(id+"F13.opPattern","COPY",BODY,{"derivedFrom":makeQuery(id+"F11.opPattern","COPY",BODY,{"derivedFrom":makeQuery(id+"F6.opPattern","COPY",BODY,{"derivedFrom":makeQuery(id+"F4.opPattern","COPY",BODY,{"derivedFrom":makeQuery(id+"F2.opExtrude","SWEPT_BODY",BODY,{"disambiguationData":[OSD([sQuery(id+"F1.wireOp",EDGE,"E1.bottom"),sQuery(id+"F1.wireOp",EDGE,"E1.top"),sQuery(id+"F1.wireOp",EDGE,"E1.left"),sQuery(id+"F1.wireOp",EDGE,"E1.right")])]}),"instanceName":"1"}),"instanceName":"1"}),"instanceName":"1"}),"instanceName":"1"});
            var Q5;
            Q5=makeQuery(id+"F55.opPattern","COPY",BODY,{"derivedFrom":makeQuery(id+"F2.opExtrude","SWEPT_BODY",BODY,{"disambiguationData":[OSD([sQuery(id+"F1.wireOp",EDGE,"E1.bottom"),sQuery(id+"F1.wireOp",EDGE,"E1.top"),sQuery(id+"F1.wireOp",EDGE,"E1.left"),sQuery(id+"F1.wireOp",EDGE,"E1.right")])]}),"instanceName":"1"});
            var Q6;
            Q6=makeQuery(id+"F6.opPattern","COPY",BODY,{"derivedFrom":makeQuery(id+"F2.opExtrude","SWEPT_BODY",BODY,{"disambiguationData":[OSD([sQuery(id+"F1.wireOp",EDGE,"E1.bottom"),sQuery(id+"F1.wireOp",EDGE,"E1.top"),sQuery(id+"F1.wireOp",EDGE,"E1.left"),sQuery(id+"F1.wireOp",EDGE,"E1.right")])]}),"instanceName":"1"});
            var Q7;
            Q7=makeQuery(id+"F4.opPattern","COPY",BODY,{"derivedFrom":makeQuery(id+"F2.opExtrude","SWEPT_BODY",BODY,{"disambiguationData":[OSD([sQuery(id+"F1.wireOp",EDGE,"E1.bottom"),sQuery(id+"F1.wireOp",EDGE,"E1.top"),sQuery(id+"F1.wireOp",EDGE,"E1.left"),sQuery(id+"F1.wireOp",EDGE,"E1.right")])]}),"instanceName":"1"});
            var Q8;
            Q8=makeQuery(id+"F6.opPattern","COPY",BODY,{"derivedFrom":makeQuery(id+"F4.opPattern","COPY",BODY,{"derivedFrom":makeQuery(id+"F2.opExtrude","SWEPT_BODY",BODY,{"disambiguationData":[OSD([sQuery(id+"F1.wireOp",EDGE,"E1.bottom"),sQuery(id+"F1.wireOp",EDGE,"E1.top"),sQuery(id+"F1.wireOp",EDGE,"E1.left"),sQuery(id+"F1.wireOp",EDGE,"E1.right")])]}),"instanceName":"1"}),"instanceName":"1"});
            transform(context, id + "F56", {"entities" : qUnion([Q0, Q1, Q2, Q3, Q4, Q5, Q6, Q7, Q8]), "transformType" : TransformType.TRANSLATION_3D, "dx" : 0 * mm, "dy" : -63.5 * mm, "dz" : 0 * mm, "makeCopy" : false});
        }
        {
            var Q0;
            Q0=makeQuery(id+"F55.opPattern","COPY",BODY,{"derivedFrom":makeQuery(id+"F4.opPattern","COPY",BODY,{"derivedFrom":makeQuery(id+"F2.opExtrude","SWEPT_BODY",BODY,{"disambiguationData":[OSD([sQuery(id+"F1.wireOp",EDGE,"E1.bottom"),sQuery(id+"F1.wireOp",EDGE,"E1.top"),sQuery(id+"F1.wireOp",EDGE,"E1.left"),sQuery(id+"F1.wireOp",EDGE,"E1.right")])]}),"instanceName":"1"}),"instanceName":"1"});
            var Q1;
            Q1=makeQuery(id+"F55.opPattern","COPY",BODY,{"derivedFrom":makeQuery(id+"F6.opPattern","COPY",BODY,{"derivedFrom":makeQuery(id+"F2.opExtrude","SWEPT_BODY",BODY,{"disambiguationData":[OSD([sQuery(id+"F1.wireOp",EDGE,"E1.bottom"),sQuery(id+"F1.wireOp",EDGE,"E1.top"),sQuery(id+"F1.wireOp",EDGE,"E1.left"),sQuery(id+"F1.wireOp",EDGE,"E1.right")])]}),"instanceName":"1"}),"instanceName":"1"});
            var Q2;
            Q2=makeQuery(id+"F55.opPattern","COPY",BODY,{"derivedFrom":makeQuery(id+"F6.opPattern","COPY",BODY,{"derivedFrom":makeQuery(id+"F4.opPattern","COPY",BODY,{"derivedFrom":makeQuery(id+"F2.opExtrude","SWEPT_BODY",BODY,{"disambiguationData":[OSD([sQuery(id+"F1.wireOp",EDGE,"E1.bottom"),sQuery(id+"F1.wireOp",EDGE,"E1.top"),sQuery(id+"F1.wireOp",EDGE,"E1.left"),sQuery(id+"F1.wireOp",EDGE,"E1.right")])]}),"instanceName":"1"}),"instanceName":"1"}),"instanceName":"1"});
            var Q3;
            Q3=makeQuery(id+"F55.opPattern","COPY",BODY,{"derivedFrom":makeQuery(id+"F11.opPattern","COPY",BODY,{"derivedFrom":makeQuery(id+"F2.opExtrude","SWEPT_BODY",BODY,{"disambiguationData":[OSD([sQuery(id+"F1.wireOp",EDGE,"E1.bottom"),sQuery(id+"F1.wireOp",EDGE,"E1.top"),sQuery(id+"F1.wireOp",EDGE,"E1.left"),sQuery(id+"F1.wireOp",EDGE,"E1.right")])]}),"instanceName":"1"}),"instanceName":"1"});
            var Q4;
            Q4=makeQuery(id+"F55.opPattern","COPY",BODY,{"derivedFrom":makeQuery(id+"F11.opPattern","COPY",BODY,{"derivedFrom":makeQuery(id+"F4.opPattern","COPY",BODY,{"derivedFrom":makeQuery(id+"F2.opExtrude","SWEPT_BODY",BODY,{"disambiguationData":[OSD([sQuery(id+"F1.wireOp",EDGE,"E1.bottom"),sQuery(id+"F1.wireOp",EDGE,"E1.top"),sQuery(id+"F1.wireOp",EDGE,"E1.left"),sQuery(id+"F1.wireOp",EDGE,"E1.right")])]}),"instanceName":"1"}),"instanceName":"1"}),"instanceName":"1"});
            var Q5;
            Q5=makeQuery(id+"F55.opPattern","COPY",BODY,{"derivedFrom":makeQuery(id+"F11.opPattern","COPY",BODY,{"derivedFrom":makeQuery(id+"F6.opPattern","COPY",BODY,{"derivedFrom":makeQuery(id+"F4.opPattern","COPY",BODY,{"derivedFrom":makeQuery(id+"F2.opExtrude","SWEPT_BODY",BODY,{"disambiguationData":[OSD([sQuery(id+"F1.wireOp",EDGE,"E1.bottom"),sQuery(id+"F1.wireOp",EDGE,"E1.top"),sQuery(id+"F1.wireOp",EDGE,"E1.left"),sQuery(id+"F1.wireOp",EDGE,"E1.right")])]}),"instanceName":"1"}),"instanceName":"1"}),"instanceName":"1"}),"instanceName":"1"});
            var Q6;
            Q6=makeQuery(id+"F55.opPattern","COPY",BODY,{"derivedFrom":makeQuery(id+"F13.opPattern","COPY",BODY,{"derivedFrom":makeQuery(id+"F11.opPattern","COPY",BODY,{"derivedFrom":makeQuery(id+"F6.opPattern","COPY",BODY,{"derivedFrom":makeQuery(id+"F4.opPattern","COPY",BODY,{"derivedFrom":makeQuery(id+"F2.opExtrude","SWEPT_BODY",BODY,{"disambiguationData":[OSD([sQuery(id+"F1.wireOp",EDGE,"E1.bottom"),sQuery(id+"F1.wireOp",EDGE,"E1.top"),sQuery(id+"F1.wireOp",EDGE,"E1.left"),sQuery(id+"F1.wireOp",EDGE,"E1.right")])]}),"instanceName":"1"}),"instanceName":"1"}),"instanceName":"1"}),"instanceName":"1"}),"instanceName":"1"});
            var Q7;
            Q7=makeQuery(id+"F2.opExtrude","SWEPT_BODY",BODY,{"disambiguationData":[OSD([sQuery(id+"F1.wireOp",EDGE,"E1.bottom"),sQuery(id+"F1.wireOp",EDGE,"E1.top"),sQuery(id+"F1.wireOp",EDGE,"E1.left"),sQuery(id+"F1.wireOp",EDGE,"E1.right")])]});
            var Q8;
            Q8=makeQuery(id+"F11.opPattern","COPY",BODY,{"derivedFrom":makeQuery(id+"F6.opPattern","COPY",BODY,{"derivedFrom":makeQuery(id+"F2.opExtrude","SWEPT_BODY",BODY,{"disambiguationData":[OSD([sQuery(id+"F1.wireOp",EDGE,"E1.bottom"),sQuery(id+"F1.wireOp",EDGE,"E1.top"),sQuery(id+"F1.wireOp",EDGE,"E1.left"),sQuery(id+"F1.wireOp",EDGE,"E1.right")])]}),"instanceName":"1"}),"instanceName":"1"});
            var Q9;
            Q9=makeQuery(id+"F55.opPattern","COPY",BODY,{"derivedFrom":makeQuery(id+"F2.opExtrude","SWEPT_BODY",BODY,{"disambiguationData":[OSD([sQuery(id+"F1.wireOp",EDGE,"E1.bottom"),sQuery(id+"F1.wireOp",EDGE,"E1.top"),sQuery(id+"F1.wireOp",EDGE,"E1.left"),sQuery(id+"F1.wireOp",EDGE,"E1.right")])]}),"instanceName":"1"});
            var Q10;
            Q10=makeQuery(id+"F55.opPattern","COPY",BODY,{"derivedFrom":makeQuery(id+"F11.opPattern","COPY",BODY,{"derivedFrom":makeQuery(id+"F6.opPattern","COPY",BODY,{"derivedFrom":makeQuery(id+"F2.opExtrude","SWEPT_BODY",BODY,{"disambiguationData":[OSD([sQuery(id+"F1.wireOp",EDGE,"E1.bottom"),sQuery(id+"F1.wireOp",EDGE,"E1.top"),sQuery(id+"F1.wireOp",EDGE,"E1.left"),sQuery(id+"F1.wireOp",EDGE,"E1.right")])]}),"instanceName":"1"}),"instanceName":"1"}),"instanceName":"1"});
            var Q11;
            Q11=makeQuery(id+"F4.opPattern","COPY",BODY,{"derivedFrom":makeQuery(id+"F2.opExtrude","SWEPT_BODY",BODY,{"disambiguationData":[OSD([sQuery(id+"F1.wireOp",EDGE,"E1.bottom"),sQuery(id+"F1.wireOp",EDGE,"E1.top"),sQuery(id+"F1.wireOp",EDGE,"E1.left"),sQuery(id+"F1.wireOp",EDGE,"E1.right")])]}),"instanceName":"1"});
            var Q12;
            Q12=makeQuery(id+"F6.opPattern","COPY",BODY,{"derivedFrom":makeQuery(id+"F2.opExtrude","SWEPT_BODY",BODY,{"disambiguationData":[OSD([sQuery(id+"F1.wireOp",EDGE,"E1.bottom"),sQuery(id+"F1.wireOp",EDGE,"E1.top"),sQuery(id+"F1.wireOp",EDGE,"E1.left"),sQuery(id+"F1.wireOp",EDGE,"E1.right")])]}),"instanceName":"1"});
            var Q13;
            Q13=makeQuery(id+"F6.opPattern","COPY",BODY,{"derivedFrom":makeQuery(id+"F4.opPattern","COPY",BODY,{"derivedFrom":makeQuery(id+"F2.opExtrude","SWEPT_BODY",BODY,{"disambiguationData":[OSD([sQuery(id+"F1.wireOp",EDGE,"E1.bottom"),sQuery(id+"F1.wireOp",EDGE,"E1.top"),sQuery(id+"F1.wireOp",EDGE,"E1.left"),sQuery(id+"F1.wireOp",EDGE,"E1.right")])]}),"instanceName":"1"}),"instanceName":"1"});
            var Q14;
            Q14=makeQuery(id+"F11.opPattern","COPY",BODY,{"derivedFrom":makeQuery(id+"F2.opExtrude","SWEPT_BODY",BODY,{"disambiguationData":[OSD([sQuery(id+"F1.wireOp",EDGE,"E1.bottom"),sQuery(id+"F1.wireOp",EDGE,"E1.top"),sQuery(id+"F1.wireOp",EDGE,"E1.left"),sQuery(id+"F1.wireOp",EDGE,"E1.right")])]}),"instanceName":"1"});
            var Q15;
            Q15=makeQuery(id+"F11.opPattern","COPY",BODY,{"derivedFrom":makeQuery(id+"F4.opPattern","COPY",BODY,{"derivedFrom":makeQuery(id+"F2.opExtrude","SWEPT_BODY",BODY,{"disambiguationData":[OSD([sQuery(id+"F1.wireOp",EDGE,"E1.bottom"),sQuery(id+"F1.wireOp",EDGE,"E1.top"),sQuery(id+"F1.wireOp",EDGE,"E1.left"),sQuery(id+"F1.wireOp",EDGE,"E1.right")])]}),"instanceName":"1"}),"instanceName":"1"});
            var Q16;
            Q16=makeQuery(id+"F11.opPattern","COPY",BODY,{"derivedFrom":makeQuery(id+"F6.opPattern","COPY",BODY,{"derivedFrom":makeQuery(id+"F4.opPattern","COPY",BODY,{"derivedFrom":makeQuery(id+"F2.opExtrude","SWEPT_BODY",BODY,{"disambiguationData":[OSD([sQuery(id+"F1.wireOp",EDGE,"E1.bottom"),sQuery(id+"F1.wireOp",EDGE,"E1.top"),sQuery(id+"F1.wireOp",EDGE,"E1.left"),sQuery(id+"F1.wireOp",EDGE,"E1.right")])]}),"instanceName":"1"}),"instanceName":"1"}),"instanceName":"1"});
            var Q17;
            Q17=makeQuery(id+"F13.opPattern","COPY",BODY,{"derivedFrom":makeQuery(id+"F11.opPattern","COPY",BODY,{"derivedFrom":makeQuery(id+"F6.opPattern","COPY",BODY,{"derivedFrom":makeQuery(id+"F4.opPattern","COPY",BODY,{"derivedFrom":makeQuery(id+"F2.opExtrude","SWEPT_BODY",BODY,{"disambiguationData":[OSD([sQuery(id+"F1.wireOp",EDGE,"E1.bottom"),sQuery(id+"F1.wireOp",EDGE,"E1.top"),sQuery(id+"F1.wireOp",EDGE,"E1.left"),sQuery(id+"F1.wireOp",EDGE,"E1.right")])]}),"instanceName":"1"}),"instanceName":"1"}),"instanceName":"1"}),"instanceName":"1"});
            transform(context, id + "F57", {"entities" : qUnion([Q0, Q1, Q2, Q3, Q4, Q5, Q6, Q7, Q8, Q9, Q10, Q11, Q12, Q13, Q14, Q15, Q16, Q17]), "transformType" : TransformType.TRANSLATION_3D, "dx" : 0.97 * mm, "dy" : 0 * mm, "dz" : 0 * mm, "makeCopy" : false});
        }
        {
            var Q0;
            Q0=qCreatedBy(makeId("Top.planeOp"),FACE);
            var sketch = newSketch(context, id + "F58", { "sketchPlane" : qUnion([Q0])});
            skLineSegment(sketch, "E2.bottom", {"start": v(-74.28, -29.87) * mm, "end": v(-136.8, -29.87) * mm});
            skLineSegment(sketch, "E2.top", {"start": v(-74.28, 32.65) * mm, "end": v(-136.8, 32.65) * mm});
            skLineSegment(sketch, "E2.left", {"start": v(-74.28, -29.87) * mm, "end": v(-74.28, 32.65) * mm});
            skLineSegment(sketch, "E2.right", {"start": v(-136.8, -29.87) * mm, "end": v(-136.8, 32.65) * mm});
            skSolve(sketch);
        }
        {
            var Q0;
            Q0=makeQuery(id+"F58.imprint","IMPRINT",FACE,{"disambiguationData":[TD([[makeQuery(id+"F58.imprint","IMPRINT",EDGE,{"derivedFrom":sQuery(id+"F58.wireOp",EDGE,"E2.bottom")}),-1.0]])]});
            extrude(context, id + "F59", {"entities" : qUnion([Q0]), "depth" : 6.35 * mm});
        }
        {
            var Q0;
            Q0=makeQuery(id+"F59.opExtrude","SWEPT_BODY",BODY,{"disambiguationData":[OSD([sQuery(id+"F58.wireOp",EDGE,"E2.bottom"),sQuery(id+"F58.wireOp",EDGE,"E2.top"),sQuery(id+"F58.wireOp",EDGE,"E2.left"),sQuery(id+"F58.wireOp",EDGE,"E2.right")])]});
            transform(context, id + "F60", {"entities" : qUnion([Q0]), "transformType" : TransformType.TRANSLATION_3D, "dx" : 89.92 * mm, "dy" : 8.13 * mm, "dz" : 0 * mm, "makeCopy" : false});
        }
        {
            var Q0;
            Q0=makeQuery(id+"F2.opExtrude","SWEPT_BODY",BODY,{"disambiguationData":[OSD([sQuery(id+"F0.wireOp",EDGE,"E0.bottom"),sQuery(id+"F0.wireOp",EDGE,"E0.top"),sQuery(id+"F0.wireOp",EDGE,"E0.left"),sQuery(id+"F0.wireOp",EDGE,"E0.right")])]});
            deleteBodies(context, id + "F61", {"entities" : qUnion([Q0])});
        }
        {
            var Q0;
            Q0=makeQuery(id+"F2.opExtrude","SWEPT_BODY",BODY,{"disambiguationData":[OSD([sQuery(id+"F1.wireOp",EDGE,"E1.bottom"),sQuery(id+"F1.wireOp",EDGE,"E1.top"),sQuery(id+"F1.wireOp",EDGE,"E1.left"),sQuery(id+"F1.wireOp",EDGE,"E1.right")])]});
            var Q1;
            Q1=makeQuery(id+"F55.opPattern","COPY",BODY,{"derivedFrom":makeQuery(id+"F4.opPattern","COPY",BODY,{"derivedFrom":makeQuery(id+"F2.opExtrude","SWEPT_BODY",BODY,{"disambiguationData":[OSD([sQuery(id+"F1.wireOp",EDGE,"E1.bottom"),sQuery(id+"F1.wireOp",EDGE,"E1.top"),sQuery(id+"F1.wireOp",EDGE,"E1.left"),sQuery(id+"F1.wireOp",EDGE,"E1.right")])]}),"instanceName":"1"}),"instanceName":"1"});
            var Q2;
            Q2=makeQuery(id+"F55.opPattern","COPY",BODY,{"derivedFrom":makeQuery(id+"F6.opPattern","COPY",BODY,{"derivedFrom":makeQuery(id+"F2.opExtrude","SWEPT_BODY",BODY,{"disambiguationData":[OSD([sQuery(id+"F1.wireOp",EDGE,"E1.bottom"),sQuery(id+"F1.wireOp",EDGE,"E1.top"),sQuery(id+"F1.wireOp",EDGE,"E1.left"),sQuery(id+"F1.wireOp",EDGE,"E1.right")])]}),"instanceName":"1"}),"instanceName":"1"});
            var Q3;
            Q3=makeQuery(id+"F55.opPattern","COPY",BODY,{"derivedFrom":makeQuery(id+"F6.opPattern","COPY",BODY,{"derivedFrom":makeQuery(id+"F4.opPattern","COPY",BODY,{"derivedFrom":makeQuery(id+"F2.opExtrude","SWEPT_BODY",BODY,{"disambiguationData":[OSD([sQuery(id+"F1.wireOp",EDGE,"E1.bottom"),sQuery(id+"F1.wireOp",EDGE,"E1.top"),sQuery(id+"F1.wireOp",EDGE,"E1.left"),sQuery(id+"F1.wireOp",EDGE,"E1.right")])]}),"instanceName":"1"}),"instanceName":"1"}),"instanceName":"1"});
            var Q4;
            Q4=makeQuery(id+"F55.opPattern","COPY",BODY,{"derivedFrom":makeQuery(id+"F11.opPattern","COPY",BODY,{"derivedFrom":makeQuery(id+"F2.opExtrude","SWEPT_BODY",BODY,{"disambiguationData":[OSD([sQuery(id+"F1.wireOp",EDGE,"E1.bottom"),sQuery(id+"F1.wireOp",EDGE,"E1.top"),sQuery(id+"F1.wireOp",EDGE,"E1.left"),sQuery(id+"F1.wireOp",EDGE,"E1.right")])]}),"instanceName":"1"}),"instanceName":"1"});
            var Q5;
            Q5=makeQuery(id+"F55.opPattern","COPY",BODY,{"derivedFrom":makeQuery(id+"F11.opPattern","COPY",BODY,{"derivedFrom":makeQuery(id+"F4.opPattern","COPY",BODY,{"derivedFrom":makeQuery(id+"F2.opExtrude","SWEPT_BODY",BODY,{"disambiguationData":[OSD([sQuery(id+"F1.wireOp",EDGE,"E1.bottom"),sQuery(id+"F1.wireOp",EDGE,"E1.top"),sQuery(id+"F1.wireOp",EDGE,"E1.left"),sQuery(id+"F1.wireOp",EDGE,"E1.right")])]}),"instanceName":"1"}),"instanceName":"1"}),"instanceName":"1"});
            var Q6;
            Q6=makeQuery(id+"F11.opPattern","COPY",BODY,{"derivedFrom":makeQuery(id+"F6.opPattern","COPY",BODY,{"derivedFrom":makeQuery(id+"F2.opExtrude","SWEPT_BODY",BODY,{"disambiguationData":[OSD([sQuery(id+"F1.wireOp",EDGE,"E1.bottom"),sQuery(id+"F1.wireOp",EDGE,"E1.top"),sQuery(id+"F1.wireOp",EDGE,"E1.left"),sQuery(id+"F1.wireOp",EDGE,"E1.right")])]}),"instanceName":"1"}),"instanceName":"1"});
            var Q7;
            Q7=makeQuery(id+"F55.opPattern","COPY",BODY,{"derivedFrom":makeQuery(id+"F11.opPattern","COPY",BODY,{"derivedFrom":makeQuery(id+"F6.opPattern","COPY",BODY,{"derivedFrom":makeQuery(id+"F4.opPattern","COPY",BODY,{"derivedFrom":makeQuery(id+"F2.opExtrude","SWEPT_BODY",BODY,{"disambiguationData":[OSD([sQuery(id+"F1.wireOp",EDGE,"E1.bottom"),sQuery(id+"F1.wireOp",EDGE,"E1.top"),sQuery(id+"F1.wireOp",EDGE,"E1.left"),sQuery(id+"F1.wireOp",EDGE,"E1.right")])]}),"instanceName":"1"}),"instanceName":"1"}),"instanceName":"1"}),"instanceName":"1"});
            var Q8;
            Q8=makeQuery(id+"F55.opPattern","COPY",BODY,{"derivedFrom":makeQuery(id+"F13.opPattern","COPY",BODY,{"derivedFrom":makeQuery(id+"F11.opPattern","COPY",BODY,{"derivedFrom":makeQuery(id+"F6.opPattern","COPY",BODY,{"derivedFrom":makeQuery(id+"F4.opPattern","COPY",BODY,{"derivedFrom":makeQuery(id+"F2.opExtrude","SWEPT_BODY",BODY,{"disambiguationData":[OSD([sQuery(id+"F1.wireOp",EDGE,"E1.bottom"),sQuery(id+"F1.wireOp",EDGE,"E1.top"),sQuery(id+"F1.wireOp",EDGE,"E1.left"),sQuery(id+"F1.wireOp",EDGE,"E1.right")])]}),"instanceName":"1"}),"instanceName":"1"}),"instanceName":"1"}),"instanceName":"1"}),"instanceName":"1"});
            transform(context, id + "F62", {"entities" : qUnion([Q0, Q1, Q2, Q3, Q4, Q5, Q6, Q7, Q8]), "transformType" : TransformType.TRANSLATION_3D, "dx" : 0 * mm, "dy" : -0.5 * mm, "dz" : 0 * mm, "makeCopy" : false});
        }
        {
            var Q0;
            Q0=makeQuery(id+"F11.opPattern","COPY",BODY,{"derivedFrom":makeQuery(id+"F4.opPattern","COPY",BODY,{"derivedFrom":makeQuery(id+"F2.opExtrude","SWEPT_BODY",BODY,{"disambiguationData":[OSD([sQuery(id+"F1.wireOp",EDGE,"E1.bottom"),sQuery(id+"F1.wireOp",EDGE,"E1.top"),sQuery(id+"F1.wireOp",EDGE,"E1.left"),sQuery(id+"F1.wireOp",EDGE,"E1.right")])]}),"instanceName":"1"}),"instanceName":"1"});
            var Q1;
            Q1=makeQuery(id+"F11.opPattern","COPY",BODY,{"derivedFrom":makeQuery(id+"F6.opPattern","COPY",BODY,{"derivedFrom":makeQuery(id+"F4.opPattern","COPY",BODY,{"derivedFrom":makeQuery(id+"F2.opExtrude","SWEPT_BODY",BODY,{"disambiguationData":[OSD([sQuery(id+"F1.wireOp",EDGE,"E1.bottom"),sQuery(id+"F1.wireOp",EDGE,"E1.top"),sQuery(id+"F1.wireOp",EDGE,"E1.left"),sQuery(id+"F1.wireOp",EDGE,"E1.right")])]}),"instanceName":"1"}),"instanceName":"1"}),"instanceName":"1"});
            var Q2;
            Q2=makeQuery(id+"F55.opPattern","COPY",BODY,{"derivedFrom":makeQuery(id+"F11.opPattern","COPY",BODY,{"derivedFrom":makeQuery(id+"F6.opPattern","COPY",BODY,{"derivedFrom":makeQuery(id+"F2.opExtrude","SWEPT_BODY",BODY,{"disambiguationData":[OSD([sQuery(id+"F1.wireOp",EDGE,"E1.bottom"),sQuery(id+"F1.wireOp",EDGE,"E1.top"),sQuery(id+"F1.wireOp",EDGE,"E1.left"),sQuery(id+"F1.wireOp",EDGE,"E1.right")])]}),"instanceName":"1"}),"instanceName":"1"}),"instanceName":"1"});
            var Q3;
            Q3=makeQuery(id+"F11.opPattern","COPY",BODY,{"derivedFrom":makeQuery(id+"F2.opExtrude","SWEPT_BODY",BODY,{"disambiguationData":[OSD([sQuery(id+"F1.wireOp",EDGE,"E1.bottom"),sQuery(id+"F1.wireOp",EDGE,"E1.top"),sQuery(id+"F1.wireOp",EDGE,"E1.left"),sQuery(id+"F1.wireOp",EDGE,"E1.right")])]}),"instanceName":"1"});
            var Q4;
            Q4=makeQuery(id+"F6.opPattern","COPY",BODY,{"derivedFrom":makeQuery(id+"F4.opPattern","COPY",BODY,{"derivedFrom":makeQuery(id+"F2.opExtrude","SWEPT_BODY",BODY,{"disambiguationData":[OSD([sQuery(id+"F1.wireOp",EDGE,"E1.bottom"),sQuery(id+"F1.wireOp",EDGE,"E1.top"),sQuery(id+"F1.wireOp",EDGE,"E1.left"),sQuery(id+"F1.wireOp",EDGE,"E1.right")])]}),"instanceName":"1"}),"instanceName":"1"});
            var Q5;
            Q5=makeQuery(id+"F4.opPattern","COPY",BODY,{"derivedFrom":makeQuery(id+"F2.opExtrude","SWEPT_BODY",BODY,{"disambiguationData":[OSD([sQuery(id+"F1.wireOp",EDGE,"E1.bottom"),sQuery(id+"F1.wireOp",EDGE,"E1.top"),sQuery(id+"F1.wireOp",EDGE,"E1.left"),sQuery(id+"F1.wireOp",EDGE,"E1.right")])]}),"instanceName":"1"});
            var Q6;
            Q6=makeQuery(id+"F6.opPattern","COPY",BODY,{"derivedFrom":makeQuery(id+"F2.opExtrude","SWEPT_BODY",BODY,{"disambiguationData":[OSD([sQuery(id+"F1.wireOp",EDGE,"E1.bottom"),sQuery(id+"F1.wireOp",EDGE,"E1.top"),sQuery(id+"F1.wireOp",EDGE,"E1.left"),sQuery(id+"F1.wireOp",EDGE,"E1.right")])]}),"instanceName":"1"});
            var Q7;
            Q7=makeQuery(id+"F55.opPattern","COPY",BODY,{"derivedFrom":makeQuery(id+"F2.opExtrude","SWEPT_BODY",BODY,{"disambiguationData":[OSD([sQuery(id+"F1.wireOp",EDGE,"E1.bottom"),sQuery(id+"F1.wireOp",EDGE,"E1.top"),sQuery(id+"F1.wireOp",EDGE,"E1.left"),sQuery(id+"F1.wireOp",EDGE,"E1.right")])]}),"instanceName":"1"});
            var Q8;
            Q8=makeQuery(id+"F13.opPattern","COPY",BODY,{"derivedFrom":makeQuery(id+"F11.opPattern","COPY",BODY,{"derivedFrom":makeQuery(id+"F6.opPattern","COPY",BODY,{"derivedFrom":makeQuery(id+"F4.opPattern","COPY",BODY,{"derivedFrom":makeQuery(id+"F2.opExtrude","SWEPT_BODY",BODY,{"disambiguationData":[OSD([sQuery(id+"F1.wireOp",EDGE,"E1.bottom"),sQuery(id+"F1.wireOp",EDGE,"E1.top"),sQuery(id+"F1.wireOp",EDGE,"E1.left"),sQuery(id+"F1.wireOp",EDGE,"E1.right")])]}),"instanceName":"1"}),"instanceName":"1"}),"instanceName":"1"}),"instanceName":"1"});
            transform(context, id + "F63", {"entities" : qUnion([Q0, Q1, Q2, Q3, Q4, Q5, Q6, Q7, Q8]), "transformType" : TransformType.TRANSLATION_3D, "dx" : 0 * mm, "dy" : -7.11 * mm, "dz" : 0 * mm, "makeCopy" : false});
        }
        {
            var Q0;
            Q0=makeQuery(id+"F4.opPattern","COPY",BODY,{"derivedFrom":makeQuery(id+"F2.opExtrude","SWEPT_BODY",BODY,{"disambiguationData":[OSD([sQuery(id+"F1.wireOp",EDGE,"E1.bottom"),sQuery(id+"F1.wireOp",EDGE,"E1.top"),sQuery(id+"F1.wireOp",EDGE,"E1.left"),sQuery(id+"F1.wireOp",EDGE,"E1.right")])]}),"instanceName":"1"});
            var Q1;
            Q1=makeQuery(id+"F6.opPattern","COPY",BODY,{"derivedFrom":makeQuery(id+"F2.opExtrude","SWEPT_BODY",BODY,{"disambiguationData":[OSD([sQuery(id+"F1.wireOp",EDGE,"E1.bottom"),sQuery(id+"F1.wireOp",EDGE,"E1.top"),sQuery(id+"F1.wireOp",EDGE,"E1.left"),sQuery(id+"F1.wireOp",EDGE,"E1.right")])]}),"instanceName":"1"});
            var Q2;
            Q2=makeQuery(id+"F6.opPattern","COPY",BODY,{"derivedFrom":makeQuery(id+"F4.opPattern","COPY",BODY,{"derivedFrom":makeQuery(id+"F2.opExtrude","SWEPT_BODY",BODY,{"disambiguationData":[OSD([sQuery(id+"F1.wireOp",EDGE,"E1.bottom"),sQuery(id+"F1.wireOp",EDGE,"E1.top"),sQuery(id+"F1.wireOp",EDGE,"E1.left"),sQuery(id+"F1.wireOp",EDGE,"E1.right")])]}),"instanceName":"1"}),"instanceName":"1"});
            var Q3;
            Q3=makeQuery(id+"F55.opPattern","COPY",BODY,{"derivedFrom":makeQuery(id+"F2.opExtrude","SWEPT_BODY",BODY,{"disambiguationData":[OSD([sQuery(id+"F1.wireOp",EDGE,"E1.bottom"),sQuery(id+"F1.wireOp",EDGE,"E1.top"),sQuery(id+"F1.wireOp",EDGE,"E1.left"),sQuery(id+"F1.wireOp",EDGE,"E1.right")])]}),"instanceName":"1"});
            var Q4;
            Q4=makeQuery(id+"F55.opPattern","COPY",BODY,{"derivedFrom":makeQuery(id+"F11.opPattern","COPY",BODY,{"derivedFrom":makeQuery(id+"F6.opPattern","COPY",BODY,{"derivedFrom":makeQuery(id+"F2.opExtrude","SWEPT_BODY",BODY,{"disambiguationData":[OSD([sQuery(id+"F1.wireOp",EDGE,"E1.bottom"),sQuery(id+"F1.wireOp",EDGE,"E1.top"),sQuery(id+"F1.wireOp",EDGE,"E1.left"),sQuery(id+"F1.wireOp",EDGE,"E1.right")])]}),"instanceName":"1"}),"instanceName":"1"}),"instanceName":"1"});
            var Q5;
            Q5=makeQuery(id+"F13.opPattern","COPY",BODY,{"derivedFrom":makeQuery(id+"F11.opPattern","COPY",BODY,{"derivedFrom":makeQuery(id+"F6.opPattern","COPY",BODY,{"derivedFrom":makeQuery(id+"F4.opPattern","COPY",BODY,{"derivedFrom":makeQuery(id+"F2.opExtrude","SWEPT_BODY",BODY,{"disambiguationData":[OSD([sQuery(id+"F1.wireOp",EDGE,"E1.bottom"),sQuery(id+"F1.wireOp",EDGE,"E1.top"),sQuery(id+"F1.wireOp",EDGE,"E1.left"),sQuery(id+"F1.wireOp",EDGE,"E1.right")])]}),"instanceName":"1"}),"instanceName":"1"}),"instanceName":"1"}),"instanceName":"1"});
            var Q6;
            Q6=makeQuery(id+"F11.opPattern","COPY",BODY,{"derivedFrom":makeQuery(id+"F6.opPattern","COPY",BODY,{"derivedFrom":makeQuery(id+"F4.opPattern","COPY",BODY,{"derivedFrom":makeQuery(id+"F2.opExtrude","SWEPT_BODY",BODY,{"disambiguationData":[OSD([sQuery(id+"F1.wireOp",EDGE,"E1.bottom"),sQuery(id+"F1.wireOp",EDGE,"E1.top"),sQuery(id+"F1.wireOp",EDGE,"E1.left"),sQuery(id+"F1.wireOp",EDGE,"E1.right")])]}),"instanceName":"1"}),"instanceName":"1"}),"instanceName":"1"});
            var Q7;
            Q7=makeQuery(id+"F11.opPattern","COPY",BODY,{"derivedFrom":makeQuery(id+"F4.opPattern","COPY",BODY,{"derivedFrom":makeQuery(id+"F2.opExtrude","SWEPT_BODY",BODY,{"disambiguationData":[OSD([sQuery(id+"F1.wireOp",EDGE,"E1.bottom"),sQuery(id+"F1.wireOp",EDGE,"E1.top"),sQuery(id+"F1.wireOp",EDGE,"E1.left"),sQuery(id+"F1.wireOp",EDGE,"E1.right")])]}),"instanceName":"1"}),"instanceName":"1"});
            var Q8;
            Q8=makeQuery(id+"F11.opPattern","COPY",BODY,{"derivedFrom":makeQuery(id+"F2.opExtrude","SWEPT_BODY",BODY,{"disambiguationData":[OSD([sQuery(id+"F1.wireOp",EDGE,"E1.bottom"),sQuery(id+"F1.wireOp",EDGE,"E1.top"),sQuery(id+"F1.wireOp",EDGE,"E1.left"),sQuery(id+"F1.wireOp",EDGE,"E1.right")])]}),"instanceName":"1"});
            transform(context, id + "F64", {"entities" : qUnion([Q0, Q1, Q2, Q3, Q4, Q5, Q6, Q7, Q8]), "transformType" : TransformType.TRANSLATION_3D, "dx" : 0 * mm, "dy" : 0.38 * mm, "dz" : 0 * mm, "makeCopy" : false});
        }
        {
            var Q0;
            Q0=makeQuery(id+"F4.opPattern","COPY",BODY,{"derivedFrom":makeQuery(id+"F2.opExtrude","SWEPT_BODY",BODY,{"disambiguationData":[OSD([sQuery(id+"F1.wireOp",EDGE,"E1.bottom"),sQuery(id+"F1.wireOp",EDGE,"E1.top"),sQuery(id+"F1.wireOp",EDGE,"E1.left"),sQuery(id+"F1.wireOp",EDGE,"E1.right")])]}),"instanceName":"1"});
            var Q1;
            Q1=makeQuery(id+"F6.opPattern","COPY",BODY,{"derivedFrom":makeQuery(id+"F2.opExtrude","SWEPT_BODY",BODY,{"disambiguationData":[OSD([sQuery(id+"F1.wireOp",EDGE,"E1.bottom"),sQuery(id+"F1.wireOp",EDGE,"E1.top"),sQuery(id+"F1.wireOp",EDGE,"E1.left"),sQuery(id+"F1.wireOp",EDGE,"E1.right")])]}),"instanceName":"1"});
            var Q2;
            Q2=makeQuery(id+"F6.opPattern","COPY",BODY,{"derivedFrom":makeQuery(id+"F4.opPattern","COPY",BODY,{"derivedFrom":makeQuery(id+"F2.opExtrude","SWEPT_BODY",BODY,{"disambiguationData":[OSD([sQuery(id+"F1.wireOp",EDGE,"E1.bottom"),sQuery(id+"F1.wireOp",EDGE,"E1.top"),sQuery(id+"F1.wireOp",EDGE,"E1.left"),sQuery(id+"F1.wireOp",EDGE,"E1.right")])]}),"instanceName":"1"}),"instanceName":"1"});
            var Q3;
            Q3=makeQuery(id+"F55.opPattern","COPY",BODY,{"derivedFrom":makeQuery(id+"F2.opExtrude","SWEPT_BODY",BODY,{"disambiguationData":[OSD([sQuery(id+"F1.wireOp",EDGE,"E1.bottom"),sQuery(id+"F1.wireOp",EDGE,"E1.top"),sQuery(id+"F1.wireOp",EDGE,"E1.left"),sQuery(id+"F1.wireOp",EDGE,"E1.right")])]}),"instanceName":"1"});
            var Q4;
            Q4=makeQuery(id+"F55.opPattern","COPY",BODY,{"derivedFrom":makeQuery(id+"F11.opPattern","COPY",BODY,{"derivedFrom":makeQuery(id+"F6.opPattern","COPY",BODY,{"derivedFrom":makeQuery(id+"F2.opExtrude","SWEPT_BODY",BODY,{"disambiguationData":[OSD([sQuery(id+"F1.wireOp",EDGE,"E1.bottom"),sQuery(id+"F1.wireOp",EDGE,"E1.top"),sQuery(id+"F1.wireOp",EDGE,"E1.left"),sQuery(id+"F1.wireOp",EDGE,"E1.right")])]}),"instanceName":"1"}),"instanceName":"1"}),"instanceName":"1"});
            var Q5;
            Q5=makeQuery(id+"F13.opPattern","COPY",BODY,{"derivedFrom":makeQuery(id+"F11.opPattern","COPY",BODY,{"derivedFrom":makeQuery(id+"F6.opPattern","COPY",BODY,{"derivedFrom":makeQuery(id+"F4.opPattern","COPY",BODY,{"derivedFrom":makeQuery(id+"F2.opExtrude","SWEPT_BODY",BODY,{"disambiguationData":[OSD([sQuery(id+"F1.wireOp",EDGE,"E1.bottom"),sQuery(id+"F1.wireOp",EDGE,"E1.top"),sQuery(id+"F1.wireOp",EDGE,"E1.left"),sQuery(id+"F1.wireOp",EDGE,"E1.right")])]}),"instanceName":"1"}),"instanceName":"1"}),"instanceName":"1"}),"instanceName":"1"});
            var Q6;
            Q6=makeQuery(id+"F11.opPattern","COPY",BODY,{"derivedFrom":makeQuery(id+"F6.opPattern","COPY",BODY,{"derivedFrom":makeQuery(id+"F4.opPattern","COPY",BODY,{"derivedFrom":makeQuery(id+"F2.opExtrude","SWEPT_BODY",BODY,{"disambiguationData":[OSD([sQuery(id+"F1.wireOp",EDGE,"E1.bottom"),sQuery(id+"F1.wireOp",EDGE,"E1.top"),sQuery(id+"F1.wireOp",EDGE,"E1.left"),sQuery(id+"F1.wireOp",EDGE,"E1.right")])]}),"instanceName":"1"}),"instanceName":"1"}),"instanceName":"1"});
            var Q7;
            Q7=makeQuery(id+"F11.opPattern","COPY",BODY,{"derivedFrom":makeQuery(id+"F4.opPattern","COPY",BODY,{"derivedFrom":makeQuery(id+"F2.opExtrude","SWEPT_BODY",BODY,{"disambiguationData":[OSD([sQuery(id+"F1.wireOp",EDGE,"E1.bottom"),sQuery(id+"F1.wireOp",EDGE,"E1.top"),sQuery(id+"F1.wireOp",EDGE,"E1.left"),sQuery(id+"F1.wireOp",EDGE,"E1.right")])]}),"instanceName":"1"}),"instanceName":"1"});
            var Q8;
            Q8=makeQuery(id+"F11.opPattern","COPY",BODY,{"derivedFrom":makeQuery(id+"F2.opExtrude","SWEPT_BODY",BODY,{"disambiguationData":[OSD([sQuery(id+"F1.wireOp",EDGE,"E1.bottom"),sQuery(id+"F1.wireOp",EDGE,"E1.top"),sQuery(id+"F1.wireOp",EDGE,"E1.left"),sQuery(id+"F1.wireOp",EDGE,"E1.right")])]}),"instanceName":"1"});
            transform(context, id + "F65", {"entities" : qUnion([Q0, Q1, Q2, Q3, Q4, Q5, Q6, Q7, Q8]), "transformType" : TransformType.COPY});
        }
        {
            var Q0;
            Q0=makeQuery(id+"F22.opPattern","COPY",BODY,{"derivedFrom":makeQuery(id+"F15.opPattern","COPY",BODY,{"derivedFrom":makeQuery(id+"F6.opPattern","COPY",BODY,{"derivedFrom":makeQuery(id+"F4.opPattern","COPY",BODY,{"derivedFrom":makeQuery(id+"F2.opExtrude","SWEPT_BODY",BODY,{"disambiguationData":[OSD([sQuery(id+"F1.wireOp",EDGE,"E1.bottom"),sQuery(id+"F1.wireOp",EDGE,"E1.top"),sQuery(id+"F1.wireOp",EDGE,"E1.left"),sQuery(id+"F1.wireOp",EDGE,"E1.right")])]}),"instanceName":"1"}),"instanceName":"1"}),"instanceName":"1"}),"instanceName":"1"});
            var Q1;
            Q1=makeQuery(id+"F22.opPattern","COPY",BODY,{"derivedFrom":makeQuery(id+"F15.opPattern","COPY",BODY,{"derivedFrom":makeQuery(id+"F11.opPattern","COPY",BODY,{"derivedFrom":makeQuery(id+"F2.opExtrude","SWEPT_BODY",BODY,{"disambiguationData":[OSD([sQuery(id+"F1.wireOp",EDGE,"E1.bottom"),sQuery(id+"F1.wireOp",EDGE,"E1.top"),sQuery(id+"F1.wireOp",EDGE,"E1.left"),sQuery(id+"F1.wireOp",EDGE,"E1.right")])]}),"instanceName":"1"}),"instanceName":"1"}),"instanceName":"1"});
            var Q2;
            Q2=makeQuery(id+"F22.opPattern","COPY",BODY,{"derivedFrom":makeQuery(id+"F15.opPattern","COPY",BODY,{"derivedFrom":makeQuery(id+"F6.opPattern","COPY",BODY,{"derivedFrom":makeQuery(id+"F2.opExtrude","SWEPT_BODY",BODY,{"disambiguationData":[OSD([sQuery(id+"F1.wireOp",EDGE,"E1.bottom"),sQuery(id+"F1.wireOp",EDGE,"E1.top"),sQuery(id+"F1.wireOp",EDGE,"E1.left"),sQuery(id+"F1.wireOp",EDGE,"E1.right")])]}),"instanceName":"1"}),"instanceName":"1"}),"instanceName":"1"});
            var Q3;
            Q3=makeQuery(id+"F44.opPattern","COPY",BODY,{"derivedFrom":makeQuery(id+"F22.opPattern","COPY",BODY,{"derivedFrom":makeQuery(id+"F15.opPattern","COPY",BODY,{"derivedFrom":makeQuery(id+"F11.opPattern","COPY",BODY,{"derivedFrom":makeQuery(id+"F6.opPattern","COPY",BODY,{"derivedFrom":makeQuery(id+"F2.opExtrude","SWEPT_BODY",BODY,{"disambiguationData":[OSD([sQuery(id+"F1.wireOp",EDGE,"E1.bottom"),sQuery(id+"F1.wireOp",EDGE,"E1.top"),sQuery(id+"F1.wireOp",EDGE,"E1.left"),sQuery(id+"F1.wireOp",EDGE,"E1.right")])]}),"instanceName":"1"}),"instanceName":"1"}),"instanceName":"1"}),"instanceName":"1"}),"instanceName":"1"});
            var Q4;
            Q4=makeQuery(id+"F44.opPattern","COPY",BODY,{"derivedFrom":makeQuery(id+"F22.opPattern","COPY",BODY,{"derivedFrom":makeQuery(id+"F15.opPattern","COPY",BODY,{"derivedFrom":makeQuery(id+"F13.opPattern","COPY",BODY,{"derivedFrom":makeQuery(id+"F11.opPattern","COPY",BODY,{"derivedFrom":makeQuery(id+"F6.opPattern","COPY",BODY,{"derivedFrom":makeQuery(id+"F4.opPattern","COPY",BODY,{"derivedFrom":makeQuery(id+"F2.opExtrude","SWEPT_BODY",BODY,{"disambiguationData":[OSD([sQuery(id+"F1.wireOp",EDGE,"E1.bottom"),sQuery(id+"F1.wireOp",EDGE,"E1.top"),sQuery(id+"F1.wireOp",EDGE,"E1.left"),sQuery(id+"F1.wireOp",EDGE,"E1.right")])]}),"instanceName":"1"}),"instanceName":"1"}),"instanceName":"1"}),"instanceName":"1"}),"instanceName":"1"}),"instanceName":"1"}),"instanceName":"1"});
            var Q5;
            Q5=makeQuery(id+"F22.opPattern","COPY",BODY,{"derivedFrom":makeQuery(id+"F15.opPattern","COPY",BODY,{"derivedFrom":makeQuery(id+"F4.opPattern","COPY",BODY,{"derivedFrom":makeQuery(id+"F2.opExtrude","SWEPT_BODY",BODY,{"disambiguationData":[OSD([sQuery(id+"F1.wireOp",EDGE,"E1.bottom"),sQuery(id+"F1.wireOp",EDGE,"E1.top"),sQuery(id+"F1.wireOp",EDGE,"E1.left"),sQuery(id+"F1.wireOp",EDGE,"E1.right")])]}),"instanceName":"1"}),"instanceName":"1"}),"instanceName":"1"});
            var Q6;
            Q6=makeQuery(id+"F22.opPattern","COPY",BODY,{"derivedFrom":makeQuery(id+"F15.opPattern","COPY",BODY,{"derivedFrom":makeQuery(id+"F2.opExtrude","SWEPT_BODY",BODY,{"disambiguationData":[OSD([sQuery(id+"F1.wireOp",EDGE,"E1.bottom"),sQuery(id+"F1.wireOp",EDGE,"E1.top"),sQuery(id+"F1.wireOp",EDGE,"E1.left"),sQuery(id+"F1.wireOp",EDGE,"E1.right")])]}),"instanceName":"1"}),"instanceName":"1"});
            deleteBodies(context, id + "F66", {"entities" : qUnion([Q0, Q1, Q2, Q3, Q4, Q5, Q6])});
        }
        {
            var Q0;
            Q0=makeQuery(id+"F11.opPattern","COPY",BODY,{"derivedFrom":makeQuery(id+"F6.opPattern","COPY",BODY,{"derivedFrom":makeQuery(id+"F4.opPattern","COPY",BODY,{"derivedFrom":makeQuery(id+"F2.opExtrude","SWEPT_BODY",BODY,{"disambiguationData":[OSD([sQuery(id+"F1.wireOp",EDGE,"E1.bottom"),sQuery(id+"F1.wireOp",EDGE,"E1.top"),sQuery(id+"F1.wireOp",EDGE,"E1.left"),sQuery(id+"F1.wireOp",EDGE,"E1.right")])]}),"instanceName":"1"}),"instanceName":"1"}),"instanceName":"1"});
            var Q1;
            Q1=makeQuery(id+"F11.opPattern","COPY",BODY,{"derivedFrom":makeQuery(id+"F4.opPattern","COPY",BODY,{"derivedFrom":makeQuery(id+"F2.opExtrude","SWEPT_BODY",BODY,{"disambiguationData":[OSD([sQuery(id+"F1.wireOp",EDGE,"E1.bottom"),sQuery(id+"F1.wireOp",EDGE,"E1.top"),sQuery(id+"F1.wireOp",EDGE,"E1.left"),sQuery(id+"F1.wireOp",EDGE,"E1.right")])]}),"instanceName":"1"}),"instanceName":"1"});
            var Q2;
            Q2=makeQuery(id+"F55.opPattern","COPY",BODY,{"derivedFrom":makeQuery(id+"F11.opPattern","COPY",BODY,{"derivedFrom":makeQuery(id+"F6.opPattern","COPY",BODY,{"derivedFrom":makeQuery(id+"F2.opExtrude","SWEPT_BODY",BODY,{"disambiguationData":[OSD([sQuery(id+"F1.wireOp",EDGE,"E1.bottom"),sQuery(id+"F1.wireOp",EDGE,"E1.top"),sQuery(id+"F1.wireOp",EDGE,"E1.left"),sQuery(id+"F1.wireOp",EDGE,"E1.right")])]}),"instanceName":"1"}),"instanceName":"1"}),"instanceName":"1"});
            var Q3;
            Q3=makeQuery(id+"F6.opPattern","COPY",BODY,{"derivedFrom":makeQuery(id+"F4.opPattern","COPY",BODY,{"derivedFrom":makeQuery(id+"F2.opExtrude","SWEPT_BODY",BODY,{"disambiguationData":[OSD([sQuery(id+"F1.wireOp",EDGE,"E1.bottom"),sQuery(id+"F1.wireOp",EDGE,"E1.top"),sQuery(id+"F1.wireOp",EDGE,"E1.left"),sQuery(id+"F1.wireOp",EDGE,"E1.right")])]}),"instanceName":"1"}),"instanceName":"1"});
            var Q4;
            Q4=makeQuery(id+"F11.opPattern","COPY",BODY,{"derivedFrom":makeQuery(id+"F2.opExtrude","SWEPT_BODY",BODY,{"disambiguationData":[OSD([sQuery(id+"F1.wireOp",EDGE,"E1.bottom"),sQuery(id+"F1.wireOp",EDGE,"E1.top"),sQuery(id+"F1.wireOp",EDGE,"E1.left"),sQuery(id+"F1.wireOp",EDGE,"E1.right")])]}),"instanceName":"1"});
            var Q5;
            Q5=makeQuery(id+"F4.opPattern","COPY",BODY,{"derivedFrom":makeQuery(id+"F2.opExtrude","SWEPT_BODY",BODY,{"disambiguationData":[OSD([sQuery(id+"F1.wireOp",EDGE,"E1.bottom"),sQuery(id+"F1.wireOp",EDGE,"E1.top"),sQuery(id+"F1.wireOp",EDGE,"E1.left"),sQuery(id+"F1.wireOp",EDGE,"E1.right")])]}),"instanceName":"1"});
            var Q6;
            Q6=makeQuery(id+"F6.opPattern","COPY",BODY,{"derivedFrom":makeQuery(id+"F2.opExtrude","SWEPT_BODY",BODY,{"disambiguationData":[OSD([sQuery(id+"F1.wireOp",EDGE,"E1.bottom"),sQuery(id+"F1.wireOp",EDGE,"E1.top"),sQuery(id+"F1.wireOp",EDGE,"E1.left"),sQuery(id+"F1.wireOp",EDGE,"E1.right")])]}),"instanceName":"1"});
            var Q7;
            Q7=makeQuery(id+"F55.opPattern","COPY",BODY,{"derivedFrom":makeQuery(id+"F2.opExtrude","SWEPT_BODY",BODY,{"disambiguationData":[OSD([sQuery(id+"F1.wireOp",EDGE,"E1.bottom"),sQuery(id+"F1.wireOp",EDGE,"E1.top"),sQuery(id+"F1.wireOp",EDGE,"E1.left"),sQuery(id+"F1.wireOp",EDGE,"E1.right")])]}),"instanceName":"1"});
            var Q8;
            Q8=makeQuery(id+"F13.opPattern","COPY",BODY,{"derivedFrom":makeQuery(id+"F11.opPattern","COPY",BODY,{"derivedFrom":makeQuery(id+"F6.opPattern","COPY",BODY,{"derivedFrom":makeQuery(id+"F4.opPattern","COPY",BODY,{"derivedFrom":makeQuery(id+"F2.opExtrude","SWEPT_BODY",BODY,{"disambiguationData":[OSD([sQuery(id+"F1.wireOp",EDGE,"E1.bottom"),sQuery(id+"F1.wireOp",EDGE,"E1.top"),sQuery(id+"F1.wireOp",EDGE,"E1.left"),sQuery(id+"F1.wireOp",EDGE,"E1.right")])]}),"instanceName":"1"}),"instanceName":"1"}),"instanceName":"1"}),"instanceName":"1"});
            var Q9;
            Q9=makeQuery(id+"F59.opExtrude","SWEPT_EDGE",EDGE,{"disambiguationData":[OSD([sQuery(id+"F58.wireOp",EDGE,"E2.top"),sQuery(id+"F58.wireOp",EDGE,"E2.right")])]});
            transform(context, id + "F67", {"entities" : qUnion([Q0, Q1, Q2, Q3, Q4, Q5, Q6, Q7, Q8]), "transformType" : TransformType.ROTATION, "transformAxis" : qUnion([Q9]), "angle" : 90 * degree, "makeCopy" : false});
        }
        {
            var Q0;
            Q0=makeQuery(id+"F44.opPattern","COPY",BODY,{"derivedFrom":makeQuery(id+"F22.opPattern","COPY",BODY,{"derivedFrom":makeQuery(id+"F15.opPattern","COPY",BODY,{"derivedFrom":makeQuery(id+"F11.opPattern","COPY",BODY,{"derivedFrom":makeQuery(id+"F2.opExtrude","SWEPT_BODY",BODY,{"disambiguationData":[OSD([sQuery(id+"F1.wireOp",EDGE,"E1.bottom"),sQuery(id+"F1.wireOp",EDGE,"E1.top"),sQuery(id+"F1.wireOp",EDGE,"E1.left"),sQuery(id+"F1.wireOp",EDGE,"E1.right")])]}),"instanceName":"1"}),"instanceName":"1"}),"instanceName":"1"}),"instanceName":"1"});
            var Q1;
            Q1=makeQuery(id+"F22.opPattern","COPY",BODY,{"derivedFrom":makeQuery(id+"F15.opPattern","COPY",BODY,{"derivedFrom":makeQuery(id+"F11.opPattern","COPY",BODY,{"derivedFrom":makeQuery(id+"F6.opPattern","COPY",BODY,{"derivedFrom":makeQuery(id+"F2.opExtrude","SWEPT_BODY",BODY,{"disambiguationData":[OSD([sQuery(id+"F1.wireOp",EDGE,"E1.bottom"),sQuery(id+"F1.wireOp",EDGE,"E1.top"),sQuery(id+"F1.wireOp",EDGE,"E1.left"),sQuery(id+"F1.wireOp",EDGE,"E1.right")])]}),"instanceName":"1"}),"instanceName":"1"}),"instanceName":"1"}),"instanceName":"1"});
            var Q2;
            Q2=makeQuery(id+"F22.opPattern","COPY",BODY,{"derivedFrom":makeQuery(id+"F15.opPattern","COPY",BODY,{"derivedFrom":makeQuery(id+"F13.opPattern","COPY",BODY,{"derivedFrom":makeQuery(id+"F11.opPattern","COPY",BODY,{"derivedFrom":makeQuery(id+"F6.opPattern","COPY",BODY,{"derivedFrom":makeQuery(id+"F4.opPattern","COPY",BODY,{"derivedFrom":makeQuery(id+"F2.opExtrude","SWEPT_BODY",BODY,{"disambiguationData":[OSD([sQuery(id+"F1.wireOp",EDGE,"E1.bottom"),sQuery(id+"F1.wireOp",EDGE,"E1.top"),sQuery(id+"F1.wireOp",EDGE,"E1.left"),sQuery(id+"F1.wireOp",EDGE,"E1.right")])]}),"instanceName":"1"}),"instanceName":"1"}),"instanceName":"1"}),"instanceName":"1"}),"instanceName":"1"}),"instanceName":"1"});
            var Q3;
            Q3=makeQuery(id+"F44.opPattern","COPY",BODY,{"derivedFrom":makeQuery(id+"F22.opPattern","COPY",BODY,{"derivedFrom":makeQuery(id+"F15.opPattern","COPY",BODY,{"derivedFrom":makeQuery(id+"F2.opExtrude","SWEPT_BODY",BODY,{"disambiguationData":[OSD([sQuery(id+"F1.wireOp",EDGE,"E1.bottom"),sQuery(id+"F1.wireOp",EDGE,"E1.top"),sQuery(id+"F1.wireOp",EDGE,"E1.left"),sQuery(id+"F1.wireOp",EDGE,"E1.right")])]}),"instanceName":"1"}),"instanceName":"1"}),"instanceName":"1"});
            var Q4;
            Q4=makeQuery(id+"F44.opPattern","COPY",BODY,{"derivedFrom":makeQuery(id+"F22.opPattern","COPY",BODY,{"derivedFrom":makeQuery(id+"F15.opPattern","COPY",BODY,{"derivedFrom":makeQuery(id+"F4.opPattern","COPY",BODY,{"derivedFrom":makeQuery(id+"F2.opExtrude","SWEPT_BODY",BODY,{"disambiguationData":[OSD([sQuery(id+"F1.wireOp",EDGE,"E1.bottom"),sQuery(id+"F1.wireOp",EDGE,"E1.top"),sQuery(id+"F1.wireOp",EDGE,"E1.left"),sQuery(id+"F1.wireOp",EDGE,"E1.right")])]}),"instanceName":"1"}),"instanceName":"1"}),"instanceName":"1"}),"instanceName":"1"});
            var Q5;
            Q5=makeQuery(id+"F44.opPattern","COPY",BODY,{"derivedFrom":makeQuery(id+"F22.opPattern","COPY",BODY,{"derivedFrom":makeQuery(id+"F15.opPattern","COPY",BODY,{"derivedFrom":makeQuery(id+"F6.opPattern","COPY",BODY,{"derivedFrom":makeQuery(id+"F2.opExtrude","SWEPT_BODY",BODY,{"disambiguationData":[OSD([sQuery(id+"F1.wireOp",EDGE,"E1.bottom"),sQuery(id+"F1.wireOp",EDGE,"E1.top"),sQuery(id+"F1.wireOp",EDGE,"E1.left"),sQuery(id+"F1.wireOp",EDGE,"E1.right")])]}),"instanceName":"1"}),"instanceName":"1"}),"instanceName":"1"}),"instanceName":"1"});
            var Q6;
            Q6=makeQuery(id+"F44.opPattern","COPY",BODY,{"derivedFrom":makeQuery(id+"F22.opPattern","COPY",BODY,{"derivedFrom":makeQuery(id+"F15.opPattern","COPY",BODY,{"derivedFrom":makeQuery(id+"F6.opPattern","COPY",BODY,{"derivedFrom":makeQuery(id+"F4.opPattern","COPY",BODY,{"derivedFrom":makeQuery(id+"F2.opExtrude","SWEPT_BODY",BODY,{"disambiguationData":[OSD([sQuery(id+"F1.wireOp",EDGE,"E1.bottom"),sQuery(id+"F1.wireOp",EDGE,"E1.top"),sQuery(id+"F1.wireOp",EDGE,"E1.left"),sQuery(id+"F1.wireOp",EDGE,"E1.right")])]}),"instanceName":"1"}),"instanceName":"1"}),"instanceName":"1"}),"instanceName":"1"}),"instanceName":"1"});
            deleteBodies(context, id + "F68", {"entities" : qUnion([Q0, Q1, Q2, Q3, Q4, Q5, Q6])});
        }
        {
            var Q0;
            Q0=makeQuery(id+"F4.opPattern","COPY",BODY,{"derivedFrom":makeQuery(id+"F2.opExtrude","SWEPT_BODY",BODY,{"disambiguationData":[OSD([sQuery(id+"F1.wireOp",EDGE,"E1.bottom"),sQuery(id+"F1.wireOp",EDGE,"E1.top"),sQuery(id+"F1.wireOp",EDGE,"E1.left"),sQuery(id+"F1.wireOp",EDGE,"E1.right")])]}),"instanceName":"1"});
            var Q1;
            Q1=makeQuery(id+"F6.opPattern","COPY",BODY,{"derivedFrom":makeQuery(id+"F2.opExtrude","SWEPT_BODY",BODY,{"disambiguationData":[OSD([sQuery(id+"F1.wireOp",EDGE,"E1.bottom"),sQuery(id+"F1.wireOp",EDGE,"E1.top"),sQuery(id+"F1.wireOp",EDGE,"E1.left"),sQuery(id+"F1.wireOp",EDGE,"E1.right")])]}),"instanceName":"1"});
            var Q2;
            Q2=makeQuery(id+"F6.opPattern","COPY",BODY,{"derivedFrom":makeQuery(id+"F4.opPattern","COPY",BODY,{"derivedFrom":makeQuery(id+"F2.opExtrude","SWEPT_BODY",BODY,{"disambiguationData":[OSD([sQuery(id+"F1.wireOp",EDGE,"E1.bottom"),sQuery(id+"F1.wireOp",EDGE,"E1.top"),sQuery(id+"F1.wireOp",EDGE,"E1.left"),sQuery(id+"F1.wireOp",EDGE,"E1.right")])]}),"instanceName":"1"}),"instanceName":"1"});
            var Q3;
            Q3=makeQuery(id+"F55.opPattern","COPY",BODY,{"derivedFrom":makeQuery(id+"F2.opExtrude","SWEPT_BODY",BODY,{"disambiguationData":[OSD([sQuery(id+"F1.wireOp",EDGE,"E1.bottom"),sQuery(id+"F1.wireOp",EDGE,"E1.top"),sQuery(id+"F1.wireOp",EDGE,"E1.left"),sQuery(id+"F1.wireOp",EDGE,"E1.right")])]}),"instanceName":"1"});
            var Q4;
            Q4=makeQuery(id+"F55.opPattern","COPY",BODY,{"derivedFrom":makeQuery(id+"F11.opPattern","COPY",BODY,{"derivedFrom":makeQuery(id+"F6.opPattern","COPY",BODY,{"derivedFrom":makeQuery(id+"F2.opExtrude","SWEPT_BODY",BODY,{"disambiguationData":[OSD([sQuery(id+"F1.wireOp",EDGE,"E1.bottom"),sQuery(id+"F1.wireOp",EDGE,"E1.top"),sQuery(id+"F1.wireOp",EDGE,"E1.left"),sQuery(id+"F1.wireOp",EDGE,"E1.right")])]}),"instanceName":"1"}),"instanceName":"1"}),"instanceName":"1"});
            var Q5;
            Q5=makeQuery(id+"F13.opPattern","COPY",BODY,{"derivedFrom":makeQuery(id+"F11.opPattern","COPY",BODY,{"derivedFrom":makeQuery(id+"F6.opPattern","COPY",BODY,{"derivedFrom":makeQuery(id+"F4.opPattern","COPY",BODY,{"derivedFrom":makeQuery(id+"F2.opExtrude","SWEPT_BODY",BODY,{"disambiguationData":[OSD([sQuery(id+"F1.wireOp",EDGE,"E1.bottom"),sQuery(id+"F1.wireOp",EDGE,"E1.top"),sQuery(id+"F1.wireOp",EDGE,"E1.left"),sQuery(id+"F1.wireOp",EDGE,"E1.right")])]}),"instanceName":"1"}),"instanceName":"1"}),"instanceName":"1"}),"instanceName":"1"});
            var Q6;
            Q6=makeQuery(id+"F11.opPattern","COPY",BODY,{"derivedFrom":makeQuery(id+"F6.opPattern","COPY",BODY,{"derivedFrom":makeQuery(id+"F4.opPattern","COPY",BODY,{"derivedFrom":makeQuery(id+"F2.opExtrude","SWEPT_BODY",BODY,{"disambiguationData":[OSD([sQuery(id+"F1.wireOp",EDGE,"E1.bottom"),sQuery(id+"F1.wireOp",EDGE,"E1.top"),sQuery(id+"F1.wireOp",EDGE,"E1.left"),sQuery(id+"F1.wireOp",EDGE,"E1.right")])]}),"instanceName":"1"}),"instanceName":"1"}),"instanceName":"1"});
            var Q7;
            Q7=makeQuery(id+"F11.opPattern","COPY",BODY,{"derivedFrom":makeQuery(id+"F4.opPattern","COPY",BODY,{"derivedFrom":makeQuery(id+"F2.opExtrude","SWEPT_BODY",BODY,{"disambiguationData":[OSD([sQuery(id+"F1.wireOp",EDGE,"E1.bottom"),sQuery(id+"F1.wireOp",EDGE,"E1.top"),sQuery(id+"F1.wireOp",EDGE,"E1.left"),sQuery(id+"F1.wireOp",EDGE,"E1.right")])]}),"instanceName":"1"}),"instanceName":"1"});
            var Q8;
            Q8=makeQuery(id+"F11.opPattern","COPY",BODY,{"derivedFrom":makeQuery(id+"F2.opExtrude","SWEPT_BODY",BODY,{"disambiguationData":[OSD([sQuery(id+"F1.wireOp",EDGE,"E1.bottom"),sQuery(id+"F1.wireOp",EDGE,"E1.top"),sQuery(id+"F1.wireOp",EDGE,"E1.left"),sQuery(id+"F1.wireOp",EDGE,"E1.right")])]}),"instanceName":"1"});
            transform(context, id + "F69", {"entities" : qUnion([Q0, Q1, Q2, Q3, Q4, Q5, Q6, Q7, Q8]), "transformType" : TransformType.TRANSLATION_3D, "dx" : 132.08 * mm, "dy" : 0 * mm, "dz" : 0 * mm, "makeCopy" : true});
        }
        {
            var Q0;
            Q0=makeQuery(id+"F4.opPattern","COPY",BODY,{"derivedFrom":makeQuery(id+"F2.opExtrude","SWEPT_BODY",BODY,{"disambiguationData":[OSD([sQuery(id+"F1.wireOp",EDGE,"E1.bottom"),sQuery(id+"F1.wireOp",EDGE,"E1.top"),sQuery(id+"F1.wireOp",EDGE,"E1.left"),sQuery(id+"F1.wireOp",EDGE,"E1.right")])]}),"instanceName":"1"});
            var Q1;
            Q1=makeQuery(id+"F6.opPattern","COPY",BODY,{"derivedFrom":makeQuery(id+"F2.opExtrude","SWEPT_BODY",BODY,{"disambiguationData":[OSD([sQuery(id+"F1.wireOp",EDGE,"E1.bottom"),sQuery(id+"F1.wireOp",EDGE,"E1.top"),sQuery(id+"F1.wireOp",EDGE,"E1.left"),sQuery(id+"F1.wireOp",EDGE,"E1.right")])]}),"instanceName":"1"});
            var Q2;
            Q2=makeQuery(id+"F6.opPattern","COPY",BODY,{"derivedFrom":makeQuery(id+"F4.opPattern","COPY",BODY,{"derivedFrom":makeQuery(id+"F2.opExtrude","SWEPT_BODY",BODY,{"disambiguationData":[OSD([sQuery(id+"F1.wireOp",EDGE,"E1.bottom"),sQuery(id+"F1.wireOp",EDGE,"E1.top"),sQuery(id+"F1.wireOp",EDGE,"E1.left"),sQuery(id+"F1.wireOp",EDGE,"E1.right")])]}),"instanceName":"1"}),"instanceName":"1"});
            var Q3;
            Q3=makeQuery(id+"F55.opPattern","COPY",BODY,{"derivedFrom":makeQuery(id+"F2.opExtrude","SWEPT_BODY",BODY,{"disambiguationData":[OSD([sQuery(id+"F1.wireOp",EDGE,"E1.bottom"),sQuery(id+"F1.wireOp",EDGE,"E1.top"),sQuery(id+"F1.wireOp",EDGE,"E1.left"),sQuery(id+"F1.wireOp",EDGE,"E1.right")])]}),"instanceName":"1"});
            var Q4;
            Q4=makeQuery(id+"F55.opPattern","COPY",BODY,{"derivedFrom":makeQuery(id+"F11.opPattern","COPY",BODY,{"derivedFrom":makeQuery(id+"F6.opPattern","COPY",BODY,{"derivedFrom":makeQuery(id+"F2.opExtrude","SWEPT_BODY",BODY,{"disambiguationData":[OSD([sQuery(id+"F1.wireOp",EDGE,"E1.bottom"),sQuery(id+"F1.wireOp",EDGE,"E1.top"),sQuery(id+"F1.wireOp",EDGE,"E1.left"),sQuery(id+"F1.wireOp",EDGE,"E1.right")])]}),"instanceName":"1"}),"instanceName":"1"}),"instanceName":"1"});
            var Q5;
            Q5=makeQuery(id+"F13.opPattern","COPY",BODY,{"derivedFrom":makeQuery(id+"F11.opPattern","COPY",BODY,{"derivedFrom":makeQuery(id+"F6.opPattern","COPY",BODY,{"derivedFrom":makeQuery(id+"F4.opPattern","COPY",BODY,{"derivedFrom":makeQuery(id+"F2.opExtrude","SWEPT_BODY",BODY,{"disambiguationData":[OSD([sQuery(id+"F1.wireOp",EDGE,"E1.bottom"),sQuery(id+"F1.wireOp",EDGE,"E1.top"),sQuery(id+"F1.wireOp",EDGE,"E1.left"),sQuery(id+"F1.wireOp",EDGE,"E1.right")])]}),"instanceName":"1"}),"instanceName":"1"}),"instanceName":"1"}),"instanceName":"1"});
            var Q6;
            Q6=makeQuery(id+"F11.opPattern","COPY",BODY,{"derivedFrom":makeQuery(id+"F6.opPattern","COPY",BODY,{"derivedFrom":makeQuery(id+"F4.opPattern","COPY",BODY,{"derivedFrom":makeQuery(id+"F2.opExtrude","SWEPT_BODY",BODY,{"disambiguationData":[OSD([sQuery(id+"F1.wireOp",EDGE,"E1.bottom"),sQuery(id+"F1.wireOp",EDGE,"E1.top"),sQuery(id+"F1.wireOp",EDGE,"E1.left"),sQuery(id+"F1.wireOp",EDGE,"E1.right")])]}),"instanceName":"1"}),"instanceName":"1"}),"instanceName":"1"});
            var Q7;
            Q7=makeQuery(id+"F11.opPattern","COPY",BODY,{"derivedFrom":makeQuery(id+"F4.opPattern","COPY",BODY,{"derivedFrom":makeQuery(id+"F2.opExtrude","SWEPT_BODY",BODY,{"disambiguationData":[OSD([sQuery(id+"F1.wireOp",EDGE,"E1.bottom"),sQuery(id+"F1.wireOp",EDGE,"E1.top"),sQuery(id+"F1.wireOp",EDGE,"E1.left"),sQuery(id+"F1.wireOp",EDGE,"E1.right")])]}),"instanceName":"1"}),"instanceName":"1"});
            var Q8;
            Q8=makeQuery(id+"F11.opPattern","COPY",BODY,{"derivedFrom":makeQuery(id+"F2.opExtrude","SWEPT_BODY",BODY,{"disambiguationData":[OSD([sQuery(id+"F1.wireOp",EDGE,"E1.bottom"),sQuery(id+"F1.wireOp",EDGE,"E1.top"),sQuery(id+"F1.wireOp",EDGE,"E1.left"),sQuery(id+"F1.wireOp",EDGE,"E1.right")])]}),"instanceName":"1"});
            transform(context, id + "F70", {"entities" : qUnion([Q0, Q1, Q2, Q3, Q4, Q5, Q6, Q7, Q8]), "transformType" : TransformType.TRANSLATION_3D, "dx" : 62.23 * mm, "dy" : 0 * mm, "dz" : 0 * mm, "makeCopy" : false});
        }
        {
            var Q0;
            Q0=makeQuery(id+"F69.opPattern","COPY",BODY,{"derivedFrom":makeQuery(id+"F11.opPattern","COPY",BODY,{"derivedFrom":makeQuery(id+"F2.opExtrude","SWEPT_BODY",BODY,{"disambiguationData":[OSD([sQuery(id+"F1.wireOp",EDGE,"E1.bottom"),sQuery(id+"F1.wireOp",EDGE,"E1.top"),sQuery(id+"F1.wireOp",EDGE,"E1.left"),sQuery(id+"F1.wireOp",EDGE,"E1.right")])]}),"instanceName":"1"}),"instanceName":"1"});
            var Q1;
            Q1=makeQuery(id+"F69.opPattern","COPY",BODY,{"derivedFrom":makeQuery(id+"F6.opPattern","COPY",BODY,{"derivedFrom":makeQuery(id+"F4.opPattern","COPY",BODY,{"derivedFrom":makeQuery(id+"F2.opExtrude","SWEPT_BODY",BODY,{"disambiguationData":[OSD([sQuery(id+"F1.wireOp",EDGE,"E1.bottom"),sQuery(id+"F1.wireOp",EDGE,"E1.top"),sQuery(id+"F1.wireOp",EDGE,"E1.left"),sQuery(id+"F1.wireOp",EDGE,"E1.right")])]}),"instanceName":"1"}),"instanceName":"1"}),"instanceName":"1"});
            var Q2;
            Q2=makeQuery(id+"F65.opPattern","COPY",BODY,{"derivedFrom":makeQuery(id+"F13.opPattern","COPY",BODY,{"derivedFrom":makeQuery(id+"F11.opPattern","COPY",BODY,{"derivedFrom":makeQuery(id+"F6.opPattern","COPY",BODY,{"derivedFrom":makeQuery(id+"F4.opPattern","COPY",BODY,{"derivedFrom":makeQuery(id+"F2.opExtrude","SWEPT_BODY",BODY,{"disambiguationData":[OSD([sQuery(id+"F1.wireOp",EDGE,"E1.bottom"),sQuery(id+"F1.wireOp",EDGE,"E1.top"),sQuery(id+"F1.wireOp",EDGE,"E1.left"),sQuery(id+"F1.wireOp",EDGE,"E1.right")])]}),"instanceName":"1"}),"instanceName":"1"}),"instanceName":"1"}),"instanceName":"1"}),"instanceName":"1"});
            var Q3;
            Q3=makeQuery(id+"F2.opExtrude","SWEPT_BODY",BODY,{"disambiguationData":[OSD([sQuery(id+"F1.wireOp",EDGE,"E1.bottom"),sQuery(id+"F1.wireOp",EDGE,"E1.top"),sQuery(id+"F1.wireOp",EDGE,"E1.left"),sQuery(id+"F1.wireOp",EDGE,"E1.right")])]});
            var Q4;
            Q4=makeQuery(id+"F4.opPattern","COPY",BODY,{"derivedFrom":makeQuery(id+"F2.opExtrude","SWEPT_BODY",BODY,{"disambiguationData":[OSD([sQuery(id+"F1.wireOp",EDGE,"E1.bottom"),sQuery(id+"F1.wireOp",EDGE,"E1.top"),sQuery(id+"F1.wireOp",EDGE,"E1.left"),sQuery(id+"F1.wireOp",EDGE,"E1.right")])]}),"instanceName":"1"});
            var Q5;
            Q5=makeQuery(id+"F65.opPattern","COPY",BODY,{"derivedFrom":makeQuery(id+"F6.opPattern","COPY",BODY,{"derivedFrom":makeQuery(id+"F4.opPattern","COPY",BODY,{"derivedFrom":makeQuery(id+"F2.opExtrude","SWEPT_BODY",BODY,{"disambiguationData":[OSD([sQuery(id+"F1.wireOp",EDGE,"E1.bottom"),sQuery(id+"F1.wireOp",EDGE,"E1.top"),sQuery(id+"F1.wireOp",EDGE,"E1.left"),sQuery(id+"F1.wireOp",EDGE,"E1.right")])]}),"instanceName":"1"}),"instanceName":"1"}),"instanceName":"1"});
            var Q6;
            Q6=makeQuery(id+"F69.opPattern","COPY",BODY,{"derivedFrom":makeQuery(id+"F11.opPattern","COPY",BODY,{"derivedFrom":makeQuery(id+"F4.opPattern","COPY",BODY,{"derivedFrom":makeQuery(id+"F2.opExtrude","SWEPT_BODY",BODY,{"disambiguationData":[OSD([sQuery(id+"F1.wireOp",EDGE,"E1.bottom"),sQuery(id+"F1.wireOp",EDGE,"E1.top"),sQuery(id+"F1.wireOp",EDGE,"E1.left"),sQuery(id+"F1.wireOp",EDGE,"E1.right")])]}),"instanceName":"1"}),"instanceName":"1"}),"instanceName":"1"});
            var Q7;
            Q7=makeQuery(id+"F6.opPattern","COPY",BODY,{"derivedFrom":makeQuery(id+"F2.opExtrude","SWEPT_BODY",BODY,{"disambiguationData":[OSD([sQuery(id+"F1.wireOp",EDGE,"E1.bottom"),sQuery(id+"F1.wireOp",EDGE,"E1.top"),sQuery(id+"F1.wireOp",EDGE,"E1.left"),sQuery(id+"F1.wireOp",EDGE,"E1.right")])]}),"instanceName":"1"});
            var Q8;
            Q8=makeQuery(id+"F6.opPattern","COPY",BODY,{"derivedFrom":makeQuery(id+"F4.opPattern","COPY",BODY,{"derivedFrom":makeQuery(id+"F2.opExtrude","SWEPT_BODY",BODY,{"disambiguationData":[OSD([sQuery(id+"F1.wireOp",EDGE,"E1.bottom"),sQuery(id+"F1.wireOp",EDGE,"E1.top"),sQuery(id+"F1.wireOp",EDGE,"E1.left"),sQuery(id+"F1.wireOp",EDGE,"E1.right")])]}),"instanceName":"1"}),"instanceName":"1"});
            var Q9;
            Q9=makeQuery(id+"F69.opPattern","COPY",BODY,{"derivedFrom":makeQuery(id+"F6.opPattern","COPY",BODY,{"derivedFrom":makeQuery(id+"F2.opExtrude","SWEPT_BODY",BODY,{"disambiguationData":[OSD([sQuery(id+"F1.wireOp",EDGE,"E1.bottom"),sQuery(id+"F1.wireOp",EDGE,"E1.top"),sQuery(id+"F1.wireOp",EDGE,"E1.left"),sQuery(id+"F1.wireOp",EDGE,"E1.right")])]}),"instanceName":"1"}),"instanceName":"1"});
            var Q10;
            Q10=makeQuery(id+"F69.opPattern","COPY",BODY,{"derivedFrom":makeQuery(id+"F4.opPattern","COPY",BODY,{"derivedFrom":makeQuery(id+"F2.opExtrude","SWEPT_BODY",BODY,{"disambiguationData":[OSD([sQuery(id+"F1.wireOp",EDGE,"E1.bottom"),sQuery(id+"F1.wireOp",EDGE,"E1.top"),sQuery(id+"F1.wireOp",EDGE,"E1.left"),sQuery(id+"F1.wireOp",EDGE,"E1.right")])]}),"instanceName":"1"}),"instanceName":"1"});
            var Q11;
            Q11=makeQuery(id+"F55.opPattern","COPY",BODY,{"derivedFrom":makeQuery(id+"F2.opExtrude","SWEPT_BODY",BODY,{"disambiguationData":[OSD([sQuery(id+"F1.wireOp",EDGE,"E1.bottom"),sQuery(id+"F1.wireOp",EDGE,"E1.top"),sQuery(id+"F1.wireOp",EDGE,"E1.left"),sQuery(id+"F1.wireOp",EDGE,"E1.right")])]}),"instanceName":"1"});
            var Q12;
            Q12=makeQuery(id+"F55.opPattern","COPY",BODY,{"derivedFrom":makeQuery(id+"F4.opPattern","COPY",BODY,{"derivedFrom":makeQuery(id+"F2.opExtrude","SWEPT_BODY",BODY,{"disambiguationData":[OSD([sQuery(id+"F1.wireOp",EDGE,"E1.bottom"),sQuery(id+"F1.wireOp",EDGE,"E1.top"),sQuery(id+"F1.wireOp",EDGE,"E1.left"),sQuery(id+"F1.wireOp",EDGE,"E1.right")])]}),"instanceName":"1"}),"instanceName":"1"});
            var Q13;
            Q13=makeQuery(id+"F55.opPattern","COPY",BODY,{"derivedFrom":makeQuery(id+"F6.opPattern","COPY",BODY,{"derivedFrom":makeQuery(id+"F2.opExtrude","SWEPT_BODY",BODY,{"disambiguationData":[OSD([sQuery(id+"F1.wireOp",EDGE,"E1.bottom"),sQuery(id+"F1.wireOp",EDGE,"E1.top"),sQuery(id+"F1.wireOp",EDGE,"E1.left"),sQuery(id+"F1.wireOp",EDGE,"E1.right")])]}),"instanceName":"1"}),"instanceName":"1"});
            var Q14;
            Q14=makeQuery(id+"F55.opPattern","COPY",BODY,{"derivedFrom":makeQuery(id+"F6.opPattern","COPY",BODY,{"derivedFrom":makeQuery(id+"F4.opPattern","COPY",BODY,{"derivedFrom":makeQuery(id+"F2.opExtrude","SWEPT_BODY",BODY,{"disambiguationData":[OSD([sQuery(id+"F1.wireOp",EDGE,"E1.bottom"),sQuery(id+"F1.wireOp",EDGE,"E1.top"),sQuery(id+"F1.wireOp",EDGE,"E1.left"),sQuery(id+"F1.wireOp",EDGE,"E1.right")])]}),"instanceName":"1"}),"instanceName":"1"}),"instanceName":"1"});
            var Q15;
            Q15=makeQuery(id+"F55.opPattern","COPY",BODY,{"derivedFrom":makeQuery(id+"F11.opPattern","COPY",BODY,{"derivedFrom":makeQuery(id+"F2.opExtrude","SWEPT_BODY",BODY,{"disambiguationData":[OSD([sQuery(id+"F1.wireOp",EDGE,"E1.bottom"),sQuery(id+"F1.wireOp",EDGE,"E1.top"),sQuery(id+"F1.wireOp",EDGE,"E1.left"),sQuery(id+"F1.wireOp",EDGE,"E1.right")])]}),"instanceName":"1"}),"instanceName":"1"});
            var Q16;
            Q16=makeQuery(id+"F65.opPattern","COPY",BODY,{"derivedFrom":makeQuery(id+"F55.opPattern","COPY",BODY,{"derivedFrom":makeQuery(id+"F11.opPattern","COPY",BODY,{"derivedFrom":makeQuery(id+"F6.opPattern","COPY",BODY,{"derivedFrom":makeQuery(id+"F2.opExtrude","SWEPT_BODY",BODY,{"disambiguationData":[OSD([sQuery(id+"F1.wireOp",EDGE,"E1.bottom"),sQuery(id+"F1.wireOp",EDGE,"E1.top"),sQuery(id+"F1.wireOp",EDGE,"E1.left"),sQuery(id+"F1.wireOp",EDGE,"E1.right")])]}),"instanceName":"1"}),"instanceName":"1"}),"instanceName":"1"}),"instanceName":"1"});
            var Q17;
            Q17=makeQuery(id+"F55.opPattern","COPY",BODY,{"derivedFrom":makeQuery(id+"F11.opPattern","COPY",BODY,{"derivedFrom":makeQuery(id+"F4.opPattern","COPY",BODY,{"derivedFrom":makeQuery(id+"F2.opExtrude","SWEPT_BODY",BODY,{"disambiguationData":[OSD([sQuery(id+"F1.wireOp",EDGE,"E1.bottom"),sQuery(id+"F1.wireOp",EDGE,"E1.top"),sQuery(id+"F1.wireOp",EDGE,"E1.left"),sQuery(id+"F1.wireOp",EDGE,"E1.right")])]}),"instanceName":"1"}),"instanceName":"1"}),"instanceName":"1"});
            var Q18;
            Q18=makeQuery(id+"F55.opPattern","COPY",BODY,{"derivedFrom":makeQuery(id+"F11.opPattern","COPY",BODY,{"derivedFrom":makeQuery(id+"F6.opPattern","COPY",BODY,{"derivedFrom":makeQuery(id+"F2.opExtrude","SWEPT_BODY",BODY,{"disambiguationData":[OSD([sQuery(id+"F1.wireOp",EDGE,"E1.bottom"),sQuery(id+"F1.wireOp",EDGE,"E1.top"),sQuery(id+"F1.wireOp",EDGE,"E1.left"),sQuery(id+"F1.wireOp",EDGE,"E1.right")])]}),"instanceName":"1"}),"instanceName":"1"}),"instanceName":"1"});
            var Q19;
            Q19=makeQuery(id+"F69.opPattern","COPY",BODY,{"derivedFrom":makeQuery(id+"F55.opPattern","COPY",BODY,{"derivedFrom":makeQuery(id+"F2.opExtrude","SWEPT_BODY",BODY,{"disambiguationData":[OSD([sQuery(id+"F1.wireOp",EDGE,"E1.bottom"),sQuery(id+"F1.wireOp",EDGE,"E1.top"),sQuery(id+"F1.wireOp",EDGE,"E1.left"),sQuery(id+"F1.wireOp",EDGE,"E1.right")])]}),"instanceName":"1"}),"instanceName":"1"});
            var Q20;
            Q20=makeQuery(id+"F69.opPattern","COPY",BODY,{"derivedFrom":makeQuery(id+"F11.opPattern","COPY",BODY,{"derivedFrom":makeQuery(id+"F6.opPattern","COPY",BODY,{"derivedFrom":makeQuery(id+"F4.opPattern","COPY",BODY,{"derivedFrom":makeQuery(id+"F2.opExtrude","SWEPT_BODY",BODY,{"disambiguationData":[OSD([sQuery(id+"F1.wireOp",EDGE,"E1.bottom"),sQuery(id+"F1.wireOp",EDGE,"E1.top"),sQuery(id+"F1.wireOp",EDGE,"E1.left"),sQuery(id+"F1.wireOp",EDGE,"E1.right")])]}),"instanceName":"1"}),"instanceName":"1"}),"instanceName":"1"}),"instanceName":"1"});
            var Q21;
            Q21=makeQuery(id+"F69.opPattern","COPY",BODY,{"derivedFrom":makeQuery(id+"F13.opPattern","COPY",BODY,{"derivedFrom":makeQuery(id+"F11.opPattern","COPY",BODY,{"derivedFrom":makeQuery(id+"F6.opPattern","COPY",BODY,{"derivedFrom":makeQuery(id+"F4.opPattern","COPY",BODY,{"derivedFrom":makeQuery(id+"F2.opExtrude","SWEPT_BODY",BODY,{"disambiguationData":[OSD([sQuery(id+"F1.wireOp",EDGE,"E1.bottom"),sQuery(id+"F1.wireOp",EDGE,"E1.top"),sQuery(id+"F1.wireOp",EDGE,"E1.left"),sQuery(id+"F1.wireOp",EDGE,"E1.right")])]}),"instanceName":"1"}),"instanceName":"1"}),"instanceName":"1"}),"instanceName":"1"}),"instanceName":"1"});
            var Q22;
            Q22=makeQuery(id+"F13.opPattern","COPY",BODY,{"derivedFrom":makeQuery(id+"F11.opPattern","COPY",BODY,{"derivedFrom":makeQuery(id+"F6.opPattern","COPY",BODY,{"derivedFrom":makeQuery(id+"F4.opPattern","COPY",BODY,{"derivedFrom":makeQuery(id+"F2.opExtrude","SWEPT_BODY",BODY,{"disambiguationData":[OSD([sQuery(id+"F1.wireOp",EDGE,"E1.bottom"),sQuery(id+"F1.wireOp",EDGE,"E1.top"),sQuery(id+"F1.wireOp",EDGE,"E1.left"),sQuery(id+"F1.wireOp",EDGE,"E1.right")])]}),"instanceName":"1"}),"instanceName":"1"}),"instanceName":"1"}),"instanceName":"1"});
            var Q23;
            Q23=makeQuery(id+"F11.opPattern","COPY",BODY,{"derivedFrom":makeQuery(id+"F6.opPattern","COPY",BODY,{"derivedFrom":makeQuery(id+"F4.opPattern","COPY",BODY,{"derivedFrom":makeQuery(id+"F2.opExtrude","SWEPT_BODY",BODY,{"disambiguationData":[OSD([sQuery(id+"F1.wireOp",EDGE,"E1.bottom"),sQuery(id+"F1.wireOp",EDGE,"E1.top"),sQuery(id+"F1.wireOp",EDGE,"E1.left"),sQuery(id+"F1.wireOp",EDGE,"E1.right")])]}),"instanceName":"1"}),"instanceName":"1"}),"instanceName":"1"});
            var Q24;
            Q24=makeQuery(id+"F11.opPattern","COPY",BODY,{"derivedFrom":makeQuery(id+"F6.opPattern","COPY",BODY,{"derivedFrom":makeQuery(id+"F2.opExtrude","SWEPT_BODY",BODY,{"disambiguationData":[OSD([sQuery(id+"F1.wireOp",EDGE,"E1.bottom"),sQuery(id+"F1.wireOp",EDGE,"E1.top"),sQuery(id+"F1.wireOp",EDGE,"E1.left"),sQuery(id+"F1.wireOp",EDGE,"E1.right")])]}),"instanceName":"1"}),"instanceName":"1"});
            var Q25;
            Q25=makeQuery(id+"F11.opPattern","COPY",BODY,{"derivedFrom":makeQuery(id+"F4.opPattern","COPY",BODY,{"derivedFrom":makeQuery(id+"F2.opExtrude","SWEPT_BODY",BODY,{"disambiguationData":[OSD([sQuery(id+"F1.wireOp",EDGE,"E1.bottom"),sQuery(id+"F1.wireOp",EDGE,"E1.top"),sQuery(id+"F1.wireOp",EDGE,"E1.left"),sQuery(id+"F1.wireOp",EDGE,"E1.right")])]}),"instanceName":"1"}),"instanceName":"1"});
            var Q26;
            Q26=makeQuery(id+"F69.opPattern","COPY",BODY,{"derivedFrom":makeQuery(id+"F55.opPattern","COPY",BODY,{"derivedFrom":makeQuery(id+"F11.opPattern","COPY",BODY,{"derivedFrom":makeQuery(id+"F6.opPattern","COPY",BODY,{"derivedFrom":makeQuery(id+"F2.opExtrude","SWEPT_BODY",BODY,{"disambiguationData":[OSD([sQuery(id+"F1.wireOp",EDGE,"E1.bottom"),sQuery(id+"F1.wireOp",EDGE,"E1.top"),sQuery(id+"F1.wireOp",EDGE,"E1.left"),sQuery(id+"F1.wireOp",EDGE,"E1.right")])]}),"instanceName":"1"}),"instanceName":"1"}),"instanceName":"1"}),"instanceName":"1"});
            var Q27;
            Q27=makeQuery(id+"F65.opPattern","COPY",BODY,{"derivedFrom":makeQuery(id+"F6.opPattern","COPY",BODY,{"derivedFrom":makeQuery(id+"F2.opExtrude","SWEPT_BODY",BODY,{"disambiguationData":[OSD([sQuery(id+"F1.wireOp",EDGE,"E1.bottom"),sQuery(id+"F1.wireOp",EDGE,"E1.top"),sQuery(id+"F1.wireOp",EDGE,"E1.left"),sQuery(id+"F1.wireOp",EDGE,"E1.right")])]}),"instanceName":"1"}),"instanceName":"1"});
            var Q28;
            Q28=makeQuery(id+"F65.opPattern","COPY",BODY,{"derivedFrom":makeQuery(id+"F4.opPattern","COPY",BODY,{"derivedFrom":makeQuery(id+"F2.opExtrude","SWEPT_BODY",BODY,{"disambiguationData":[OSD([sQuery(id+"F1.wireOp",EDGE,"E1.bottom"),sQuery(id+"F1.wireOp",EDGE,"E1.top"),sQuery(id+"F1.wireOp",EDGE,"E1.left"),sQuery(id+"F1.wireOp",EDGE,"E1.right")])]}),"instanceName":"1"}),"instanceName":"1"});
            var Q29;
            Q29=makeQuery(id+"F65.opPattern","COPY",BODY,{"derivedFrom":makeQuery(id+"F55.opPattern","COPY",BODY,{"derivedFrom":makeQuery(id+"F2.opExtrude","SWEPT_BODY",BODY,{"disambiguationData":[OSD([sQuery(id+"F1.wireOp",EDGE,"E1.bottom"),sQuery(id+"F1.wireOp",EDGE,"E1.top"),sQuery(id+"F1.wireOp",EDGE,"E1.left"),sQuery(id+"F1.wireOp",EDGE,"E1.right")])]}),"instanceName":"1"}),"instanceName":"1"});
            var Q30;
            Q30=makeQuery(id+"F59.opExtrude","SWEPT_BODY",BODY,{"disambiguationData":[OSD([sQuery(id+"F58.wireOp",EDGE,"E2.bottom"),sQuery(id+"F58.wireOp",EDGE,"E2.top"),sQuery(id+"F58.wireOp",EDGE,"E2.left"),sQuery(id+"F58.wireOp",EDGE,"E2.right")])]});
            var Q31;
            Q31=makeQuery(id+"F65.opPattern","COPY",BODY,{"derivedFrom":makeQuery(id+"F11.opPattern","COPY",BODY,{"derivedFrom":makeQuery(id+"F2.opExtrude","SWEPT_BODY",BODY,{"disambiguationData":[OSD([sQuery(id+"F1.wireOp",EDGE,"E1.bottom"),sQuery(id+"F1.wireOp",EDGE,"E1.top"),sQuery(id+"F1.wireOp",EDGE,"E1.left"),sQuery(id+"F1.wireOp",EDGE,"E1.right")])]}),"instanceName":"1"}),"instanceName":"1"});
            var Q32;
            Q32=makeQuery(id+"F11.opPattern","COPY",BODY,{"derivedFrom":makeQuery(id+"F2.opExtrude","SWEPT_BODY",BODY,{"disambiguationData":[OSD([sQuery(id+"F1.wireOp",EDGE,"E1.bottom"),sQuery(id+"F1.wireOp",EDGE,"E1.top"),sQuery(id+"F1.wireOp",EDGE,"E1.left"),sQuery(id+"F1.wireOp",EDGE,"E1.right")])]}),"instanceName":"1"});
            var Q33;
            Q33=makeQuery(id+"F65.opPattern","COPY",BODY,{"derivedFrom":makeQuery(id+"F11.opPattern","COPY",BODY,{"derivedFrom":makeQuery(id+"F4.opPattern","COPY",BODY,{"derivedFrom":makeQuery(id+"F2.opExtrude","SWEPT_BODY",BODY,{"disambiguationData":[OSD([sQuery(id+"F1.wireOp",EDGE,"E1.bottom"),sQuery(id+"F1.wireOp",EDGE,"E1.top"),sQuery(id+"F1.wireOp",EDGE,"E1.left"),sQuery(id+"F1.wireOp",EDGE,"E1.right")])]}),"instanceName":"1"}),"instanceName":"1"}),"instanceName":"1"});
            var Q34;
            Q34=makeQuery(id+"F55.opPattern","COPY",BODY,{"derivedFrom":makeQuery(id+"F11.opPattern","COPY",BODY,{"derivedFrom":makeQuery(id+"F6.opPattern","COPY",BODY,{"derivedFrom":makeQuery(id+"F4.opPattern","COPY",BODY,{"derivedFrom":makeQuery(id+"F2.opExtrude","SWEPT_BODY",BODY,{"disambiguationData":[OSD([sQuery(id+"F1.wireOp",EDGE,"E1.bottom"),sQuery(id+"F1.wireOp",EDGE,"E1.top"),sQuery(id+"F1.wireOp",EDGE,"E1.left"),sQuery(id+"F1.wireOp",EDGE,"E1.right")])]}),"instanceName":"1"}),"instanceName":"1"}),"instanceName":"1"}),"instanceName":"1"});
            var Q35;
            Q35=makeQuery(id+"F65.opPattern","COPY",BODY,{"derivedFrom":makeQuery(id+"F11.opPattern","COPY",BODY,{"derivedFrom":makeQuery(id+"F6.opPattern","COPY",BODY,{"derivedFrom":makeQuery(id+"F4.opPattern","COPY",BODY,{"derivedFrom":makeQuery(id+"F2.opExtrude","SWEPT_BODY",BODY,{"disambiguationData":[OSD([sQuery(id+"F1.wireOp",EDGE,"E1.bottom"),sQuery(id+"F1.wireOp",EDGE,"E1.top"),sQuery(id+"F1.wireOp",EDGE,"E1.left"),sQuery(id+"F1.wireOp",EDGE,"E1.right")])]}),"instanceName":"1"}),"instanceName":"1"}),"instanceName":"1"}),"instanceName":"1"});
            var Q36;
            Q36=makeQuery(id+"F55.opPattern","COPY",BODY,{"derivedFrom":makeQuery(id+"F13.opPattern","COPY",BODY,{"derivedFrom":makeQuery(id+"F11.opPattern","COPY",BODY,{"derivedFrom":makeQuery(id+"F6.opPattern","COPY",BODY,{"derivedFrom":makeQuery(id+"F4.opPattern","COPY",BODY,{"derivedFrom":makeQuery(id+"F2.opExtrude","SWEPT_BODY",BODY,{"disambiguationData":[OSD([sQuery(id+"F1.wireOp",EDGE,"E1.bottom"),sQuery(id+"F1.wireOp",EDGE,"E1.top"),sQuery(id+"F1.wireOp",EDGE,"E1.left"),sQuery(id+"F1.wireOp",EDGE,"E1.right")])]}),"instanceName":"1"}),"instanceName":"1"}),"instanceName":"1"}),"instanceName":"1"}),"instanceName":"1"});
            transform(context, id + "F71", {"entities" : qUnion([Q0, Q1, Q2, Q3, Q4, Q5, Q6, Q7, Q8, Q9, Q10, Q11, Q12, Q13, Q14, Q15, Q16, Q17, Q18, Q19, Q20, Q21, Q22, Q23, Q24, Q25, Q26, Q27, Q28, Q29, Q30, Q31, Q32, Q33, Q34, Q35, Q36]), "transformType" : TransformType.TRANSLATION_3D, "dx" : 95.76 * mm, "dy" : 0 * mm, "dz" : 0 * mm, "makeCopy" : true});
        }
        {
            var Q0;
            Q0=makeQuery(id+"F71.opPattern","COPY",BODY,{"derivedFrom":makeQuery(id+"F11.opPattern","COPY",BODY,{"derivedFrom":makeQuery(id+"F4.opPattern","COPY",BODY,{"derivedFrom":makeQuery(id+"F2.opExtrude","SWEPT_BODY",BODY,{"disambiguationData":[OSD([sQuery(id+"F1.wireOp",EDGE,"E1.bottom"),sQuery(id+"F1.wireOp",EDGE,"E1.top"),sQuery(id+"F1.wireOp",EDGE,"E1.left"),sQuery(id+"F1.wireOp",EDGE,"E1.right")])]}),"instanceName":"1"}),"instanceName":"1"}),"instanceName":"1"});
            var Q1;
            Q1=makeQuery(id+"F71.opPattern","COPY",BODY,{"derivedFrom":makeQuery(id+"F11.opPattern","COPY",BODY,{"derivedFrom":makeQuery(id+"F2.opExtrude","SWEPT_BODY",BODY,{"disambiguationData":[OSD([sQuery(id+"F1.wireOp",EDGE,"E1.bottom"),sQuery(id+"F1.wireOp",EDGE,"E1.top"),sQuery(id+"F1.wireOp",EDGE,"E1.left"),sQuery(id+"F1.wireOp",EDGE,"E1.right")])]}),"instanceName":"1"}),"instanceName":"1"});
            var Q2;
            Q2=makeQuery(id+"F71.opPattern","COPY",BODY,{"derivedFrom":makeQuery(id+"F4.opPattern","COPY",BODY,{"derivedFrom":makeQuery(id+"F2.opExtrude","SWEPT_BODY",BODY,{"disambiguationData":[OSD([sQuery(id+"F1.wireOp",EDGE,"E1.bottom"),sQuery(id+"F1.wireOp",EDGE,"E1.top"),sQuery(id+"F1.wireOp",EDGE,"E1.left"),sQuery(id+"F1.wireOp",EDGE,"E1.right")])]}),"instanceName":"1"}),"instanceName":"1"});
            var Q3;
            Q3=makeQuery(id+"F71.opPattern","COPY",BODY,{"derivedFrom":makeQuery(id+"F55.opPattern","COPY",BODY,{"derivedFrom":makeQuery(id+"F2.opExtrude","SWEPT_BODY",BODY,{"disambiguationData":[OSD([sQuery(id+"F1.wireOp",EDGE,"E1.bottom"),sQuery(id+"F1.wireOp",EDGE,"E1.top"),sQuery(id+"F1.wireOp",EDGE,"E1.left"),sQuery(id+"F1.wireOp",EDGE,"E1.right")])]}),"instanceName":"1"}),"instanceName":"1"});
            var Q4;
            Q4=makeQuery(id+"F71.opPattern","COPY",BODY,{"derivedFrom":makeQuery(id+"F65.opPattern","COPY",BODY,{"derivedFrom":makeQuery(id+"F11.opPattern","COPY",BODY,{"derivedFrom":makeQuery(id+"F4.opPattern","COPY",BODY,{"derivedFrom":makeQuery(id+"F2.opExtrude","SWEPT_BODY",BODY,{"disambiguationData":[OSD([sQuery(id+"F1.wireOp",EDGE,"E1.bottom"),sQuery(id+"F1.wireOp",EDGE,"E1.top"),sQuery(id+"F1.wireOp",EDGE,"E1.left"),sQuery(id+"F1.wireOp",EDGE,"E1.right")])]}),"instanceName":"1"}),"instanceName":"1"}),"instanceName":"1"}),"instanceName":"1"});
            var Q5;
            Q5=makeQuery(id+"F71.opPattern","COPY",BODY,{"derivedFrom":makeQuery(id+"F65.opPattern","COPY",BODY,{"derivedFrom":makeQuery(id+"F11.opPattern","COPY",BODY,{"derivedFrom":makeQuery(id+"F2.opExtrude","SWEPT_BODY",BODY,{"disambiguationData":[OSD([sQuery(id+"F1.wireOp",EDGE,"E1.bottom"),sQuery(id+"F1.wireOp",EDGE,"E1.top"),sQuery(id+"F1.wireOp",EDGE,"E1.left"),sQuery(id+"F1.wireOp",EDGE,"E1.right")])]}),"instanceName":"1"}),"instanceName":"1"}),"instanceName":"1"});
            var Q6;
            Q6=makeQuery(id+"F71.opPattern","COPY",BODY,{"derivedFrom":makeQuery(id+"F65.opPattern","COPY",BODY,{"derivedFrom":makeQuery(id+"F4.opPattern","COPY",BODY,{"derivedFrom":makeQuery(id+"F2.opExtrude","SWEPT_BODY",BODY,{"disambiguationData":[OSD([sQuery(id+"F1.wireOp",EDGE,"E1.bottom"),sQuery(id+"F1.wireOp",EDGE,"E1.top"),sQuery(id+"F1.wireOp",EDGE,"E1.left"),sQuery(id+"F1.wireOp",EDGE,"E1.right")])]}),"instanceName":"1"}),"instanceName":"1"}),"instanceName":"1"});
            var Q7;
            Q7=makeQuery(id+"F71.opPattern","COPY",BODY,{"derivedFrom":makeQuery(id+"F65.opPattern","COPY",BODY,{"derivedFrom":makeQuery(id+"F55.opPattern","COPY",BODY,{"derivedFrom":makeQuery(id+"F2.opExtrude","SWEPT_BODY",BODY,{"disambiguationData":[OSD([sQuery(id+"F1.wireOp",EDGE,"E1.bottom"),sQuery(id+"F1.wireOp",EDGE,"E1.top"),sQuery(id+"F1.wireOp",EDGE,"E1.left"),sQuery(id+"F1.wireOp",EDGE,"E1.right")])]}),"instanceName":"1"}),"instanceName":"1"}),"instanceName":"1"});
            var Q8;
            Q8=makeQuery(id+"F71.opPattern","COPY",BODY,{"derivedFrom":makeQuery(id+"F69.opPattern","COPY",BODY,{"derivedFrom":makeQuery(id+"F55.opPattern","COPY",BODY,{"derivedFrom":makeQuery(id+"F2.opExtrude","SWEPT_BODY",BODY,{"disambiguationData":[OSD([sQuery(id+"F1.wireOp",EDGE,"E1.bottom"),sQuery(id+"F1.wireOp",EDGE,"E1.top"),sQuery(id+"F1.wireOp",EDGE,"E1.left"),sQuery(id+"F1.wireOp",EDGE,"E1.right")])]}),"instanceName":"1"}),"instanceName":"1"}),"instanceName":"1"});
            var Q9;
            Q9=makeQuery(id+"F71.opPattern","COPY",BODY,{"derivedFrom":makeQuery(id+"F69.opPattern","COPY",BODY,{"derivedFrom":makeQuery(id+"F4.opPattern","COPY",BODY,{"derivedFrom":makeQuery(id+"F2.opExtrude","SWEPT_BODY",BODY,{"disambiguationData":[OSD([sQuery(id+"F1.wireOp",EDGE,"E1.bottom"),sQuery(id+"F1.wireOp",EDGE,"E1.top"),sQuery(id+"F1.wireOp",EDGE,"E1.left"),sQuery(id+"F1.wireOp",EDGE,"E1.right")])]}),"instanceName":"1"}),"instanceName":"1"}),"instanceName":"1"});
            var Q10;
            Q10=makeQuery(id+"F71.opPattern","COPY",BODY,{"derivedFrom":makeQuery(id+"F69.opPattern","COPY",BODY,{"derivedFrom":makeQuery(id+"F11.opPattern","COPY",BODY,{"derivedFrom":makeQuery(id+"F2.opExtrude","SWEPT_BODY",BODY,{"disambiguationData":[OSD([sQuery(id+"F1.wireOp",EDGE,"E1.bottom"),sQuery(id+"F1.wireOp",EDGE,"E1.top"),sQuery(id+"F1.wireOp",EDGE,"E1.left"),sQuery(id+"F1.wireOp",EDGE,"E1.right")])]}),"instanceName":"1"}),"instanceName":"1"}),"instanceName":"1"});
            var Q11;
            Q11=makeQuery(id+"F71.opPattern","COPY",BODY,{"derivedFrom":makeQuery(id+"F69.opPattern","COPY",BODY,{"derivedFrom":makeQuery(id+"F11.opPattern","COPY",BODY,{"derivedFrom":makeQuery(id+"F4.opPattern","COPY",BODY,{"derivedFrom":makeQuery(id+"F2.opExtrude","SWEPT_BODY",BODY,{"disambiguationData":[OSD([sQuery(id+"F1.wireOp",EDGE,"E1.bottom"),sQuery(id+"F1.wireOp",EDGE,"E1.top"),sQuery(id+"F1.wireOp",EDGE,"E1.left"),sQuery(id+"F1.wireOp",EDGE,"E1.right")])]}),"instanceName":"1"}),"instanceName":"1"}),"instanceName":"1"}),"instanceName":"1"});
            var Q12;
            Q12=makeQuery(id+"F71.opPattern","COPY",BODY,{"derivedFrom":makeQuery(id+"F2.opExtrude","SWEPT_BODY",BODY,{"disambiguationData":[OSD([sQuery(id+"F1.wireOp",EDGE,"E1.bottom"),sQuery(id+"F1.wireOp",EDGE,"E1.top"),sQuery(id+"F1.wireOp",EDGE,"E1.left"),sQuery(id+"F1.wireOp",EDGE,"E1.right")])]}),"instanceName":"1"});
            var Q13;
            Q13=makeQuery(id+"F71.opPattern","COPY",BODY,{"derivedFrom":makeQuery(id+"F55.opPattern","COPY",BODY,{"derivedFrom":makeQuery(id+"F4.opPattern","COPY",BODY,{"derivedFrom":makeQuery(id+"F2.opExtrude","SWEPT_BODY",BODY,{"disambiguationData":[OSD([sQuery(id+"F1.wireOp",EDGE,"E1.bottom"),sQuery(id+"F1.wireOp",EDGE,"E1.top"),sQuery(id+"F1.wireOp",EDGE,"E1.left"),sQuery(id+"F1.wireOp",EDGE,"E1.right")])]}),"instanceName":"1"}),"instanceName":"1"}),"instanceName":"1"});
            var Q14;
            Q14=makeQuery(id+"F71.opPattern","COPY",BODY,{"derivedFrom":makeQuery(id+"F55.opPattern","COPY",BODY,{"derivedFrom":makeQuery(id+"F11.opPattern","COPY",BODY,{"derivedFrom":makeQuery(id+"F2.opExtrude","SWEPT_BODY",BODY,{"disambiguationData":[OSD([sQuery(id+"F1.wireOp",EDGE,"E1.bottom"),sQuery(id+"F1.wireOp",EDGE,"E1.top"),sQuery(id+"F1.wireOp",EDGE,"E1.left"),sQuery(id+"F1.wireOp",EDGE,"E1.right")])]}),"instanceName":"1"}),"instanceName":"1"}),"instanceName":"1"});
            var Q15;
            Q15=makeQuery(id+"F71.opPattern","COPY",BODY,{"derivedFrom":makeQuery(id+"F55.opPattern","COPY",BODY,{"derivedFrom":makeQuery(id+"F11.opPattern","COPY",BODY,{"derivedFrom":makeQuery(id+"F4.opPattern","COPY",BODY,{"derivedFrom":makeQuery(id+"F2.opExtrude","SWEPT_BODY",BODY,{"disambiguationData":[OSD([sQuery(id+"F1.wireOp",EDGE,"E1.bottom"),sQuery(id+"F1.wireOp",EDGE,"E1.top"),sQuery(id+"F1.wireOp",EDGE,"E1.left"),sQuery(id+"F1.wireOp",EDGE,"E1.right")])]}),"instanceName":"1"}),"instanceName":"1"}),"instanceName":"1"}),"instanceName":"1"});
            var Q16;
            Q16=makeQuery(id+"F69.opPattern","COPY",BODY,{"derivedFrom":makeQuery(id+"F13.opPattern","COPY",BODY,{"derivedFrom":makeQuery(id+"F11.opPattern","COPY",BODY,{"derivedFrom":makeQuery(id+"F6.opPattern","COPY",BODY,{"derivedFrom":makeQuery(id+"F4.opPattern","COPY",BODY,{"derivedFrom":makeQuery(id+"F2.opExtrude","SWEPT_BODY",BODY,{"disambiguationData":[OSD([sQuery(id+"F1.wireOp",EDGE,"E1.bottom"),sQuery(id+"F1.wireOp",EDGE,"E1.top"),sQuery(id+"F1.wireOp",EDGE,"E1.left"),sQuery(id+"F1.wireOp",EDGE,"E1.right")])]}),"instanceName":"1"}),"instanceName":"1"}),"instanceName":"1"}),"instanceName":"1"}),"instanceName":"1"});
            var Q17;
            Q17=makeQuery(id+"F69.opPattern","COPY",BODY,{"derivedFrom":makeQuery(id+"F6.opPattern","COPY",BODY,{"derivedFrom":makeQuery(id+"F2.opExtrude","SWEPT_BODY",BODY,{"disambiguationData":[OSD([sQuery(id+"F1.wireOp",EDGE,"E1.bottom"),sQuery(id+"F1.wireOp",EDGE,"E1.top"),sQuery(id+"F1.wireOp",EDGE,"E1.left"),sQuery(id+"F1.wireOp",EDGE,"E1.right")])]}),"instanceName":"1"}),"instanceName":"1"});
            var Q18;
            Q18=makeQuery(id+"F69.opPattern","COPY",BODY,{"derivedFrom":makeQuery(id+"F6.opPattern","COPY",BODY,{"derivedFrom":makeQuery(id+"F4.opPattern","COPY",BODY,{"derivedFrom":makeQuery(id+"F2.opExtrude","SWEPT_BODY",BODY,{"disambiguationData":[OSD([sQuery(id+"F1.wireOp",EDGE,"E1.bottom"),sQuery(id+"F1.wireOp",EDGE,"E1.top"),sQuery(id+"F1.wireOp",EDGE,"E1.left"),sQuery(id+"F1.wireOp",EDGE,"E1.right")])]}),"instanceName":"1"}),"instanceName":"1"}),"instanceName":"1"});
            var Q19;
            Q19=makeQuery(id+"F69.opPattern","COPY",BODY,{"derivedFrom":makeQuery(id+"F55.opPattern","COPY",BODY,{"derivedFrom":makeQuery(id+"F11.opPattern","COPY",BODY,{"derivedFrom":makeQuery(id+"F6.opPattern","COPY",BODY,{"derivedFrom":makeQuery(id+"F2.opExtrude","SWEPT_BODY",BODY,{"disambiguationData":[OSD([sQuery(id+"F1.wireOp",EDGE,"E1.bottom"),sQuery(id+"F1.wireOp",EDGE,"E1.top"),sQuery(id+"F1.wireOp",EDGE,"E1.left"),sQuery(id+"F1.wireOp",EDGE,"E1.right")])]}),"instanceName":"1"}),"instanceName":"1"}),"instanceName":"1"}),"instanceName":"1"});
            var Q20;
            Q20=makeQuery(id+"F69.opPattern","COPY",BODY,{"derivedFrom":makeQuery(id+"F11.opPattern","COPY",BODY,{"derivedFrom":makeQuery(id+"F6.opPattern","COPY",BODY,{"derivedFrom":makeQuery(id+"F4.opPattern","COPY",BODY,{"derivedFrom":makeQuery(id+"F2.opExtrude","SWEPT_BODY",BODY,{"disambiguationData":[OSD([sQuery(id+"F1.wireOp",EDGE,"E1.bottom"),sQuery(id+"F1.wireOp",EDGE,"E1.top"),sQuery(id+"F1.wireOp",EDGE,"E1.left"),sQuery(id+"F1.wireOp",EDGE,"E1.right")])]}),"instanceName":"1"}),"instanceName":"1"}),"instanceName":"1"}),"instanceName":"1"});
            var Q21;
            Q21=makeQuery(id+"F11.opPattern","COPY",BODY,{"derivedFrom":makeQuery(id+"F6.opPattern","COPY",BODY,{"derivedFrom":makeQuery(id+"F4.opPattern","COPY",BODY,{"derivedFrom":makeQuery(id+"F2.opExtrude","SWEPT_BODY",BODY,{"disambiguationData":[OSD([sQuery(id+"F1.wireOp",EDGE,"E1.bottom"),sQuery(id+"F1.wireOp",EDGE,"E1.top"),sQuery(id+"F1.wireOp",EDGE,"E1.left"),sQuery(id+"F1.wireOp",EDGE,"E1.right")])]}),"instanceName":"1"}),"instanceName":"1"}),"instanceName":"1"});
            var Q22;
            Q22=makeQuery(id+"F55.opPattern","COPY",BODY,{"derivedFrom":makeQuery(id+"F11.opPattern","COPY",BODY,{"derivedFrom":makeQuery(id+"F6.opPattern","COPY",BODY,{"derivedFrom":makeQuery(id+"F2.opExtrude","SWEPT_BODY",BODY,{"disambiguationData":[OSD([sQuery(id+"F1.wireOp",EDGE,"E1.bottom"),sQuery(id+"F1.wireOp",EDGE,"E1.top"),sQuery(id+"F1.wireOp",EDGE,"E1.left"),sQuery(id+"F1.wireOp",EDGE,"E1.right")])]}),"instanceName":"1"}),"instanceName":"1"}),"instanceName":"1"});
            var Q23;
            Q23=makeQuery(id+"F6.opPattern","COPY",BODY,{"derivedFrom":makeQuery(id+"F4.opPattern","COPY",BODY,{"derivedFrom":makeQuery(id+"F2.opExtrude","SWEPT_BODY",BODY,{"disambiguationData":[OSD([sQuery(id+"F1.wireOp",EDGE,"E1.bottom"),sQuery(id+"F1.wireOp",EDGE,"E1.top"),sQuery(id+"F1.wireOp",EDGE,"E1.left"),sQuery(id+"F1.wireOp",EDGE,"E1.right")])]}),"instanceName":"1"}),"instanceName":"1"});
            var Q24;
            Q24=makeQuery(id+"F6.opPattern","COPY",BODY,{"derivedFrom":makeQuery(id+"F2.opExtrude","SWEPT_BODY",BODY,{"disambiguationData":[OSD([sQuery(id+"F1.wireOp",EDGE,"E1.bottom"),sQuery(id+"F1.wireOp",EDGE,"E1.top"),sQuery(id+"F1.wireOp",EDGE,"E1.left"),sQuery(id+"F1.wireOp",EDGE,"E1.right")])]}),"instanceName":"1"});
            var Q25;
            Q25=makeQuery(id+"F13.opPattern","COPY",BODY,{"derivedFrom":makeQuery(id+"F11.opPattern","COPY",BODY,{"derivedFrom":makeQuery(id+"F6.opPattern","COPY",BODY,{"derivedFrom":makeQuery(id+"F4.opPattern","COPY",BODY,{"derivedFrom":makeQuery(id+"F2.opExtrude","SWEPT_BODY",BODY,{"disambiguationData":[OSD([sQuery(id+"F1.wireOp",EDGE,"E1.bottom"),sQuery(id+"F1.wireOp",EDGE,"E1.top"),sQuery(id+"F1.wireOp",EDGE,"E1.left"),sQuery(id+"F1.wireOp",EDGE,"E1.right")])]}),"instanceName":"1"}),"instanceName":"1"}),"instanceName":"1"}),"instanceName":"1"});
            var Q26;
            Q26=makeQuery(id+"F55.opPattern","COPY",BODY,{"derivedFrom":makeQuery(id+"F13.opPattern","COPY",BODY,{"derivedFrom":makeQuery(id+"F11.opPattern","COPY",BODY,{"derivedFrom":makeQuery(id+"F6.opPattern","COPY",BODY,{"derivedFrom":makeQuery(id+"F4.opPattern","COPY",BODY,{"derivedFrom":makeQuery(id+"F2.opExtrude","SWEPT_BODY",BODY,{"disambiguationData":[OSD([sQuery(id+"F1.wireOp",EDGE,"E1.bottom"),sQuery(id+"F1.wireOp",EDGE,"E1.top"),sQuery(id+"F1.wireOp",EDGE,"E1.left"),sQuery(id+"F1.wireOp",EDGE,"E1.right")])]}),"instanceName":"1"}),"instanceName":"1"}),"instanceName":"1"}),"instanceName":"1"}),"instanceName":"1"});
            var Q27;
            Q27=makeQuery(id+"F55.opPattern","COPY",BODY,{"derivedFrom":makeQuery(id+"F6.opPattern","COPY",BODY,{"derivedFrom":makeQuery(id+"F2.opExtrude","SWEPT_BODY",BODY,{"disambiguationData":[OSD([sQuery(id+"F1.wireOp",EDGE,"E1.bottom"),sQuery(id+"F1.wireOp",EDGE,"E1.top"),sQuery(id+"F1.wireOp",EDGE,"E1.left"),sQuery(id+"F1.wireOp",EDGE,"E1.right")])]}),"instanceName":"1"}),"instanceName":"1"});
            var Q28;
            Q28=makeQuery(id+"F55.opPattern","COPY",BODY,{"derivedFrom":makeQuery(id+"F6.opPattern","COPY",BODY,{"derivedFrom":makeQuery(id+"F4.opPattern","COPY",BODY,{"derivedFrom":makeQuery(id+"F2.opExtrude","SWEPT_BODY",BODY,{"disambiguationData":[OSD([sQuery(id+"F1.wireOp",EDGE,"E1.bottom"),sQuery(id+"F1.wireOp",EDGE,"E1.top"),sQuery(id+"F1.wireOp",EDGE,"E1.left"),sQuery(id+"F1.wireOp",EDGE,"E1.right")])]}),"instanceName":"1"}),"instanceName":"1"}),"instanceName":"1"});
            var Q29;
            Q29=makeQuery(id+"F11.opPattern","COPY",BODY,{"derivedFrom":makeQuery(id+"F6.opPattern","COPY",BODY,{"derivedFrom":makeQuery(id+"F2.opExtrude","SWEPT_BODY",BODY,{"disambiguationData":[OSD([sQuery(id+"F1.wireOp",EDGE,"E1.bottom"),sQuery(id+"F1.wireOp",EDGE,"E1.top"),sQuery(id+"F1.wireOp",EDGE,"E1.left"),sQuery(id+"F1.wireOp",EDGE,"E1.right")])]}),"instanceName":"1"}),"instanceName":"1"});
            var Q30;
            Q30=makeQuery(id+"F55.opPattern","COPY",BODY,{"derivedFrom":makeQuery(id+"F11.opPattern","COPY",BODY,{"derivedFrom":makeQuery(id+"F6.opPattern","COPY",BODY,{"derivedFrom":makeQuery(id+"F4.opPattern","COPY",BODY,{"derivedFrom":makeQuery(id+"F2.opExtrude","SWEPT_BODY",BODY,{"disambiguationData":[OSD([sQuery(id+"F1.wireOp",EDGE,"E1.bottom"),sQuery(id+"F1.wireOp",EDGE,"E1.top"),sQuery(id+"F1.wireOp",EDGE,"E1.left"),sQuery(id+"F1.wireOp",EDGE,"E1.right")])]}),"instanceName":"1"}),"instanceName":"1"}),"instanceName":"1"}),"instanceName":"1"});
            var Q31;
            Q31=makeQuery(id+"F65.opPattern","COPY",BODY,{"derivedFrom":makeQuery(id+"F11.opPattern","COPY",BODY,{"derivedFrom":makeQuery(id+"F6.opPattern","COPY",BODY,{"derivedFrom":makeQuery(id+"F4.opPattern","COPY",BODY,{"derivedFrom":makeQuery(id+"F2.opExtrude","SWEPT_BODY",BODY,{"disambiguationData":[OSD([sQuery(id+"F1.wireOp",EDGE,"E1.bottom"),sQuery(id+"F1.wireOp",EDGE,"E1.top"),sQuery(id+"F1.wireOp",EDGE,"E1.left"),sQuery(id+"F1.wireOp",EDGE,"E1.right")])]}),"instanceName":"1"}),"instanceName":"1"}),"instanceName":"1"}),"instanceName":"1"});
            var Q32;
            Q32=makeQuery(id+"F65.opPattern","COPY",BODY,{"derivedFrom":makeQuery(id+"F55.opPattern","COPY",BODY,{"derivedFrom":makeQuery(id+"F11.opPattern","COPY",BODY,{"derivedFrom":makeQuery(id+"F6.opPattern","COPY",BODY,{"derivedFrom":makeQuery(id+"F2.opExtrude","SWEPT_BODY",BODY,{"disambiguationData":[OSD([sQuery(id+"F1.wireOp",EDGE,"E1.bottom"),sQuery(id+"F1.wireOp",EDGE,"E1.top"),sQuery(id+"F1.wireOp",EDGE,"E1.left"),sQuery(id+"F1.wireOp",EDGE,"E1.right")])]}),"instanceName":"1"}),"instanceName":"1"}),"instanceName":"1"}),"instanceName":"1"});
            var Q33;
            Q33=makeQuery(id+"F65.opPattern","COPY",BODY,{"derivedFrom":makeQuery(id+"F6.opPattern","COPY",BODY,{"derivedFrom":makeQuery(id+"F4.opPattern","COPY",BODY,{"derivedFrom":makeQuery(id+"F2.opExtrude","SWEPT_BODY",BODY,{"disambiguationData":[OSD([sQuery(id+"F1.wireOp",EDGE,"E1.bottom"),sQuery(id+"F1.wireOp",EDGE,"E1.top"),sQuery(id+"F1.wireOp",EDGE,"E1.left"),sQuery(id+"F1.wireOp",EDGE,"E1.right")])]}),"instanceName":"1"}),"instanceName":"1"}),"instanceName":"1"});
            var Q34;
            Q34=makeQuery(id+"F65.opPattern","COPY",BODY,{"derivedFrom":makeQuery(id+"F6.opPattern","COPY",BODY,{"derivedFrom":makeQuery(id+"F2.opExtrude","SWEPT_BODY",BODY,{"disambiguationData":[OSD([sQuery(id+"F1.wireOp",EDGE,"E1.bottom"),sQuery(id+"F1.wireOp",EDGE,"E1.top"),sQuery(id+"F1.wireOp",EDGE,"E1.left"),sQuery(id+"F1.wireOp",EDGE,"E1.right")])]}),"instanceName":"1"}),"instanceName":"1"});
            var Q35;
            Q35=makeQuery(id+"F65.opPattern","COPY",BODY,{"derivedFrom":makeQuery(id+"F13.opPattern","COPY",BODY,{"derivedFrom":makeQuery(id+"F11.opPattern","COPY",BODY,{"derivedFrom":makeQuery(id+"F6.opPattern","COPY",BODY,{"derivedFrom":makeQuery(id+"F4.opPattern","COPY",BODY,{"derivedFrom":makeQuery(id+"F2.opExtrude","SWEPT_BODY",BODY,{"disambiguationData":[OSD([sQuery(id+"F1.wireOp",EDGE,"E1.bottom"),sQuery(id+"F1.wireOp",EDGE,"E1.top"),sQuery(id+"F1.wireOp",EDGE,"E1.left"),sQuery(id+"F1.wireOp",EDGE,"E1.right")])]}),"instanceName":"1"}),"instanceName":"1"}),"instanceName":"1"}),"instanceName":"1"}),"instanceName":"1"});
            deleteBodies(context, id + "F72", {"entities" : qUnion([Q0, Q1, Q2, Q3, Q4, Q5, Q6, Q7, Q8, Q9, Q10, Q11, Q12, Q13, Q14, Q15, Q16, Q17, Q18, Q19, Q20, Q21, Q22, Q23, Q24, Q25, Q26, Q27, Q28, Q29, Q30, Q31, Q32, Q33, Q34, Q35])});
        }
        {
            var Q0;
            Q0=makeQuery(id+"F71.opPattern","COPY",BODY,{"derivedFrom":makeQuery(id+"F55.opPattern","COPY",BODY,{"derivedFrom":makeQuery(id+"F11.opPattern","COPY",BODY,{"derivedFrom":makeQuery(id+"F6.opPattern","COPY",BODY,{"derivedFrom":makeQuery(id+"F4.opPattern","COPY",BODY,{"derivedFrom":makeQuery(id+"F2.opExtrude","SWEPT_BODY",BODY,{"disambiguationData":[OSD([sQuery(id+"F1.wireOp",EDGE,"E1.bottom"),sQuery(id+"F1.wireOp",EDGE,"E1.top"),sQuery(id+"F1.wireOp",EDGE,"E1.left"),sQuery(id+"F1.wireOp",EDGE,"E1.right")])]}),"instanceName":"1"}),"instanceName":"1"}),"instanceName":"1"}),"instanceName":"1"}),"instanceName":"1"});
            transform(context, id + "F73", {"entities" : qUnion([Q0]), "transformType" : TransformType.TRANSLATION_3D, "dx" : 0.25 * mm, "dy" : 0 * mm, "dz" : 0 * mm, "makeCopy" : false});
        }
        {
            var Q0;
            Q0=makeQuery(id+"F71.opPattern","COPY",BODY,{"derivedFrom":makeQuery(id+"F13.opPattern","COPY",BODY,{"derivedFrom":makeQuery(id+"F11.opPattern","COPY",BODY,{"derivedFrom":makeQuery(id+"F6.opPattern","COPY",BODY,{"derivedFrom":makeQuery(id+"F4.opPattern","COPY",BODY,{"derivedFrom":makeQuery(id+"F2.opExtrude","SWEPT_BODY",BODY,{"disambiguationData":[OSD([sQuery(id+"F1.wireOp",EDGE,"E1.bottom"),sQuery(id+"F1.wireOp",EDGE,"E1.top"),sQuery(id+"F1.wireOp",EDGE,"E1.left"),sQuery(id+"F1.wireOp",EDGE,"E1.right")])]}),"instanceName":"1"}),"instanceName":"1"}),"instanceName":"1"}),"instanceName":"1"}),"instanceName":"1"});
            transform(context, id + "F74", {"entities" : qUnion([Q0]), "transformType" : TransformType.TRANSLATION_3D, "dx" : 0 * mm, "dy" : 0.25 * mm, "dz" : 0 * mm, "makeCopy" : false});
        }
        {
            var Q0;
            Q0=makeQuery(id+"F71.opPattern","COPY",BODY,{"derivedFrom":makeQuery(id+"F65.opPattern","COPY",BODY,{"derivedFrom":makeQuery(id+"F6.opPattern","COPY",BODY,{"derivedFrom":makeQuery(id+"F2.opExtrude","SWEPT_BODY",BODY,{"disambiguationData":[OSD([sQuery(id+"F1.wireOp",EDGE,"E1.bottom"),sQuery(id+"F1.wireOp",EDGE,"E1.top"),sQuery(id+"F1.wireOp",EDGE,"E1.left"),sQuery(id+"F1.wireOp",EDGE,"E1.right")])]}),"instanceName":"1"}),"instanceName":"1"}),"instanceName":"1"});
            var Q1;
            Q1=makeQuery(id+"F71.opPattern","COPY",BODY,{"derivedFrom":makeQuery(id+"F65.opPattern","COPY",BODY,{"derivedFrom":makeQuery(id+"F6.opPattern","COPY",BODY,{"derivedFrom":makeQuery(id+"F4.opPattern","COPY",BODY,{"derivedFrom":makeQuery(id+"F2.opExtrude","SWEPT_BODY",BODY,{"disambiguationData":[OSD([sQuery(id+"F1.wireOp",EDGE,"E1.bottom"),sQuery(id+"F1.wireOp",EDGE,"E1.top"),sQuery(id+"F1.wireOp",EDGE,"E1.left"),sQuery(id+"F1.wireOp",EDGE,"E1.right")])]}),"instanceName":"1"}),"instanceName":"1"}),"instanceName":"1"}),"instanceName":"1"});
            var Q2;
            Q2=makeQuery(id+"F71.opPattern","COPY",BODY,{"derivedFrom":makeQuery(id+"F65.opPattern","COPY",BODY,{"derivedFrom":makeQuery(id+"F11.opPattern","COPY",BODY,{"derivedFrom":makeQuery(id+"F6.opPattern","COPY",BODY,{"derivedFrom":makeQuery(id+"F4.opPattern","COPY",BODY,{"derivedFrom":makeQuery(id+"F2.opExtrude","SWEPT_BODY",BODY,{"disambiguationData":[OSD([sQuery(id+"F1.wireOp",EDGE,"E1.bottom"),sQuery(id+"F1.wireOp",EDGE,"E1.top"),sQuery(id+"F1.wireOp",EDGE,"E1.left"),sQuery(id+"F1.wireOp",EDGE,"E1.right")])]}),"instanceName":"1"}),"instanceName":"1"}),"instanceName":"1"}),"instanceName":"1"}),"instanceName":"1"});
            var Q3;
            Q3=makeQuery(id+"F71.opPattern","COPY",BODY,{"derivedFrom":makeQuery(id+"F65.opPattern","COPY",BODY,{"derivedFrom":makeQuery(id+"F13.opPattern","COPY",BODY,{"derivedFrom":makeQuery(id+"F11.opPattern","COPY",BODY,{"derivedFrom":makeQuery(id+"F6.opPattern","COPY",BODY,{"derivedFrom":makeQuery(id+"F4.opPattern","COPY",BODY,{"derivedFrom":makeQuery(id+"F2.opExtrude","SWEPT_BODY",BODY,{"disambiguationData":[OSD([sQuery(id+"F1.wireOp",EDGE,"E1.bottom"),sQuery(id+"F1.wireOp",EDGE,"E1.top"),sQuery(id+"F1.wireOp",EDGE,"E1.left"),sQuery(id+"F1.wireOp",EDGE,"E1.right")])]}),"instanceName":"1"}),"instanceName":"1"}),"instanceName":"1"}),"instanceName":"1"}),"instanceName":"1"}),"instanceName":"1"});
            var Q4;
            Q4=makeQuery(id+"F71.opPattern","COPY",BODY,{"derivedFrom":makeQuery(id+"F65.opPattern","COPY",BODY,{"derivedFrom":makeQuery(id+"F55.opPattern","COPY",BODY,{"derivedFrom":makeQuery(id+"F11.opPattern","COPY",BODY,{"derivedFrom":makeQuery(id+"F6.opPattern","COPY",BODY,{"derivedFrom":makeQuery(id+"F2.opExtrude","SWEPT_BODY",BODY,{"disambiguationData":[OSD([sQuery(id+"F1.wireOp",EDGE,"E1.bottom"),sQuery(id+"F1.wireOp",EDGE,"E1.top"),sQuery(id+"F1.wireOp",EDGE,"E1.left"),sQuery(id+"F1.wireOp",EDGE,"E1.right")])]}),"instanceName":"1"}),"instanceName":"1"}),"instanceName":"1"}),"instanceName":"1"}),"instanceName":"1"});
            transform(context, id + "F75", {"entities" : qUnion([Q0, Q1, Q2, Q3, Q4]), "transformType" : TransformType.TRANSLATION_3D, "dx" : 0 * mm, "dy" : 0.13 * mm, "dz" : 0 * mm, "makeCopy" : false});
        }
        {
            var Q0;
            Q0=makeQuery(id+"F71.opPattern","COPY",BODY,{"derivedFrom":makeQuery(id+"F13.opPattern","COPY",BODY,{"derivedFrom":makeQuery(id+"F11.opPattern","COPY",BODY,{"derivedFrom":makeQuery(id+"F6.opPattern","COPY",BODY,{"derivedFrom":makeQuery(id+"F4.opPattern","COPY",BODY,{"derivedFrom":makeQuery(id+"F2.opExtrude","SWEPT_BODY",BODY,{"disambiguationData":[OSD([sQuery(id+"F1.wireOp",EDGE,"E1.bottom"),sQuery(id+"F1.wireOp",EDGE,"E1.top"),sQuery(id+"F1.wireOp",EDGE,"E1.left"),sQuery(id+"F1.wireOp",EDGE,"E1.right")])]}),"instanceName":"1"}),"instanceName":"1"}),"instanceName":"1"}),"instanceName":"1"}),"instanceName":"1"});
            var Q1;
            Q1=makeQuery(id+"F71.opPattern","COPY",BODY,{"derivedFrom":makeQuery(id+"F6.opPattern","COPY",BODY,{"derivedFrom":makeQuery(id+"F2.opExtrude","SWEPT_BODY",BODY,{"disambiguationData":[OSD([sQuery(id+"F1.wireOp",EDGE,"E1.bottom"),sQuery(id+"F1.wireOp",EDGE,"E1.top"),sQuery(id+"F1.wireOp",EDGE,"E1.left"),sQuery(id+"F1.wireOp",EDGE,"E1.right")])]}),"instanceName":"1"}),"instanceName":"1"});
            var Q2;
            Q2=makeQuery(id+"F71.opPattern","COPY",BODY,{"derivedFrom":makeQuery(id+"F6.opPattern","COPY",BODY,{"derivedFrom":makeQuery(id+"F4.opPattern","COPY",BODY,{"derivedFrom":makeQuery(id+"F2.opExtrude","SWEPT_BODY",BODY,{"disambiguationData":[OSD([sQuery(id+"F1.wireOp",EDGE,"E1.bottom"),sQuery(id+"F1.wireOp",EDGE,"E1.top"),sQuery(id+"F1.wireOp",EDGE,"E1.left"),sQuery(id+"F1.wireOp",EDGE,"E1.right")])]}),"instanceName":"1"}),"instanceName":"1"}),"instanceName":"1"});
            var Q3;
            Q3=makeQuery(id+"F71.opPattern","COPY",BODY,{"derivedFrom":makeQuery(id+"F11.opPattern","COPY",BODY,{"derivedFrom":makeQuery(id+"F6.opPattern","COPY",BODY,{"derivedFrom":makeQuery(id+"F4.opPattern","COPY",BODY,{"derivedFrom":makeQuery(id+"F2.opExtrude","SWEPT_BODY",BODY,{"disambiguationData":[OSD([sQuery(id+"F1.wireOp",EDGE,"E1.bottom"),sQuery(id+"F1.wireOp",EDGE,"E1.top"),sQuery(id+"F1.wireOp",EDGE,"E1.left"),sQuery(id+"F1.wireOp",EDGE,"E1.right")])]}),"instanceName":"1"}),"instanceName":"1"}),"instanceName":"1"}),"instanceName":"1"});
            var Q4;
            Q4=makeQuery(id+"F71.opPattern","COPY",BODY,{"derivedFrom":makeQuery(id+"F55.opPattern","COPY",BODY,{"derivedFrom":makeQuery(id+"F11.opPattern","COPY",BODY,{"derivedFrom":makeQuery(id+"F6.opPattern","COPY",BODY,{"derivedFrom":makeQuery(id+"F2.opExtrude","SWEPT_BODY",BODY,{"disambiguationData":[OSD([sQuery(id+"F1.wireOp",EDGE,"E1.bottom"),sQuery(id+"F1.wireOp",EDGE,"E1.top"),sQuery(id+"F1.wireOp",EDGE,"E1.left"),sQuery(id+"F1.wireOp",EDGE,"E1.right")])]}),"instanceName":"1"}),"instanceName":"1"}),"instanceName":"1"}),"instanceName":"1"});
            transform(context, id + "F76", {"entities" : qUnion([Q0, Q1, Q2, Q3, Q4]), "transformType" : TransformType.TRANSLATION_3D, "dx" : 0.36 * mm, "dy" : 0 * mm, "dz" : 0 * mm, "makeCopy" : false});
        }
        {
            var Q0;
            Q0=makeQuery(id+"F71.opPattern","COPY",BODY,{"derivedFrom":makeQuery(id+"F11.opPattern","COPY",BODY,{"derivedFrom":makeQuery(id+"F6.opPattern","COPY",BODY,{"derivedFrom":makeQuery(id+"F2.opExtrude","SWEPT_BODY",BODY,{"disambiguationData":[OSD([sQuery(id+"F1.wireOp",EDGE,"E1.bottom"),sQuery(id+"F1.wireOp",EDGE,"E1.top"),sQuery(id+"F1.wireOp",EDGE,"E1.left"),sQuery(id+"F1.wireOp",EDGE,"E1.right")])]}),"instanceName":"1"}),"instanceName":"1"}),"instanceName":"1"});
            var Q1;
            Q1=makeQuery(id+"F71.opPattern","COPY",BODY,{"derivedFrom":makeQuery(id+"F55.opPattern","COPY",BODY,{"derivedFrom":makeQuery(id+"F6.opPattern","COPY",BODY,{"derivedFrom":makeQuery(id+"F2.opExtrude","SWEPT_BODY",BODY,{"disambiguationData":[OSD([sQuery(id+"F1.wireOp",EDGE,"E1.bottom"),sQuery(id+"F1.wireOp",EDGE,"E1.top"),sQuery(id+"F1.wireOp",EDGE,"E1.left"),sQuery(id+"F1.wireOp",EDGE,"E1.right")])]}),"instanceName":"1"}),"instanceName":"1"}),"instanceName":"1"});
            var Q2;
            Q2=makeQuery(id+"F71.opPattern","COPY",BODY,{"derivedFrom":makeQuery(id+"F55.opPattern","COPY",BODY,{"derivedFrom":makeQuery(id+"F6.opPattern","COPY",BODY,{"derivedFrom":makeQuery(id+"F4.opPattern","COPY",BODY,{"derivedFrom":makeQuery(id+"F2.opExtrude","SWEPT_BODY",BODY,{"disambiguationData":[OSD([sQuery(id+"F1.wireOp",EDGE,"E1.bottom"),sQuery(id+"F1.wireOp",EDGE,"E1.top"),sQuery(id+"F1.wireOp",EDGE,"E1.left"),sQuery(id+"F1.wireOp",EDGE,"E1.right")])]}),"instanceName":"1"}),"instanceName":"1"}),"instanceName":"1"}),"instanceName":"1"});
            var Q3;
            Q3=makeQuery(id+"F71.opPattern","COPY",BODY,{"derivedFrom":makeQuery(id+"F55.opPattern","COPY",BODY,{"derivedFrom":makeQuery(id+"F11.opPattern","COPY",BODY,{"derivedFrom":makeQuery(id+"F6.opPattern","COPY",BODY,{"derivedFrom":makeQuery(id+"F4.opPattern","COPY",BODY,{"derivedFrom":makeQuery(id+"F2.opExtrude","SWEPT_BODY",BODY,{"disambiguationData":[OSD([sQuery(id+"F1.wireOp",EDGE,"E1.bottom"),sQuery(id+"F1.wireOp",EDGE,"E1.top"),sQuery(id+"F1.wireOp",EDGE,"E1.left"),sQuery(id+"F1.wireOp",EDGE,"E1.right")])]}),"instanceName":"1"}),"instanceName":"1"}),"instanceName":"1"}),"instanceName":"1"}),"instanceName":"1"});
            var Q4;
            Q4=makeQuery(id+"F71.opPattern","COPY",BODY,{"derivedFrom":makeQuery(id+"F55.opPattern","COPY",BODY,{"derivedFrom":makeQuery(id+"F13.opPattern","COPY",BODY,{"derivedFrom":makeQuery(id+"F11.opPattern","COPY",BODY,{"derivedFrom":makeQuery(id+"F6.opPattern","COPY",BODY,{"derivedFrom":makeQuery(id+"F4.opPattern","COPY",BODY,{"derivedFrom":makeQuery(id+"F2.opExtrude","SWEPT_BODY",BODY,{"disambiguationData":[OSD([sQuery(id+"F1.wireOp",EDGE,"E1.bottom"),sQuery(id+"F1.wireOp",EDGE,"E1.top"),sQuery(id+"F1.wireOp",EDGE,"E1.left"),sQuery(id+"F1.wireOp",EDGE,"E1.right")])]}),"instanceName":"1"}),"instanceName":"1"}),"instanceName":"1"}),"instanceName":"1"}),"instanceName":"1"}),"instanceName":"1"});
            transform(context, id + "F77", {"entities" : qUnion([Q0, Q1, Q2, Q3, Q4]), "transformType" : TransformType.TRANSLATION_3D, "dx" : 0 * mm, "dy" : -0.13 * mm, "dz" : 0 * mm, "makeCopy" : false});
        }
        {
            var Q0;
            Q0=makeQuery(id+"F65.opPattern","COPY",BODY,{"derivedFrom":makeQuery(id+"F4.opPattern","COPY",BODY,{"derivedFrom":makeQuery(id+"F2.opExtrude","SWEPT_BODY",BODY,{"disambiguationData":[OSD([sQuery(id+"F1.wireOp",EDGE,"E1.bottom"),sQuery(id+"F1.wireOp",EDGE,"E1.top"),sQuery(id+"F1.wireOp",EDGE,"E1.left"),sQuery(id+"F1.wireOp",EDGE,"E1.right")])]}),"instanceName":"1"}),"instanceName":"1"});
            var Q1;
            Q1=makeQuery(id+"F65.opPattern","COPY",BODY,{"derivedFrom":makeQuery(id+"F11.opPattern","COPY",BODY,{"derivedFrom":makeQuery(id+"F2.opExtrude","SWEPT_BODY",BODY,{"disambiguationData":[OSD([sQuery(id+"F1.wireOp",EDGE,"E1.bottom"),sQuery(id+"F1.wireOp",EDGE,"E1.top"),sQuery(id+"F1.wireOp",EDGE,"E1.left"),sQuery(id+"F1.wireOp",EDGE,"E1.right")])]}),"instanceName":"1"}),"instanceName":"1"});
            var Q2;
            Q2=makeQuery(id+"F65.opPattern","COPY",BODY,{"derivedFrom":makeQuery(id+"F11.opPattern","COPY",BODY,{"derivedFrom":makeQuery(id+"F4.opPattern","COPY",BODY,{"derivedFrom":makeQuery(id+"F2.opExtrude","SWEPT_BODY",BODY,{"disambiguationData":[OSD([sQuery(id+"F1.wireOp",EDGE,"E1.bottom"),sQuery(id+"F1.wireOp",EDGE,"E1.top"),sQuery(id+"F1.wireOp",EDGE,"E1.left"),sQuery(id+"F1.wireOp",EDGE,"E1.right")])]}),"instanceName":"1"}),"instanceName":"1"}),"instanceName":"1"});
            var Q3;
            Q3=makeQuery(id+"F65.opPattern","COPY",BODY,{"derivedFrom":makeQuery(id+"F55.opPattern","COPY",BODY,{"derivedFrom":makeQuery(id+"F2.opExtrude","SWEPT_BODY",BODY,{"disambiguationData":[OSD([sQuery(id+"F1.wireOp",EDGE,"E1.bottom"),sQuery(id+"F1.wireOp",EDGE,"E1.top"),sQuery(id+"F1.wireOp",EDGE,"E1.left"),sQuery(id+"F1.wireOp",EDGE,"E1.right")])]}),"instanceName":"1"}),"instanceName":"1"});
            transform(context, id + "F78", {"entities" : qUnion([Q0, Q1, Q2, Q3]), "transformType" : TransformType.TRANSLATION_3D, "dx" : 0 * mm, "dy" : 0.13 * mm, "dz" : 0 * mm, "makeCopy" : false});
        }
        {
            var Q0;
            Q0=makeQuery(id+"F2.opExtrude","SWEPT_BODY",BODY,{"disambiguationData":[OSD([sQuery(id+"F1.wireOp",EDGE,"E1.bottom"),sQuery(id+"F1.wireOp",EDGE,"E1.top"),sQuery(id+"F1.wireOp",EDGE,"E1.left"),sQuery(id+"F1.wireOp",EDGE,"E1.right")])]});
            var Q1;
            Q1=makeQuery(id+"F55.opPattern","COPY",BODY,{"derivedFrom":makeQuery(id+"F4.opPattern","COPY",BODY,{"derivedFrom":makeQuery(id+"F2.opExtrude","SWEPT_BODY",BODY,{"disambiguationData":[OSD([sQuery(id+"F1.wireOp",EDGE,"E1.bottom"),sQuery(id+"F1.wireOp",EDGE,"E1.top"),sQuery(id+"F1.wireOp",EDGE,"E1.left"),sQuery(id+"F1.wireOp",EDGE,"E1.right")])]}),"instanceName":"1"}),"instanceName":"1"});
            var Q2;
            Q2=makeQuery(id+"F55.opPattern","COPY",BODY,{"derivedFrom":makeQuery(id+"F11.opPattern","COPY",BODY,{"derivedFrom":makeQuery(id+"F2.opExtrude","SWEPT_BODY",BODY,{"disambiguationData":[OSD([sQuery(id+"F1.wireOp",EDGE,"E1.bottom"),sQuery(id+"F1.wireOp",EDGE,"E1.top"),sQuery(id+"F1.wireOp",EDGE,"E1.left"),sQuery(id+"F1.wireOp",EDGE,"E1.right")])]}),"instanceName":"1"}),"instanceName":"1"});
            var Q3;
            Q3=makeQuery(id+"F55.opPattern","COPY",BODY,{"derivedFrom":makeQuery(id+"F11.opPattern","COPY",BODY,{"derivedFrom":makeQuery(id+"F4.opPattern","COPY",BODY,{"derivedFrom":makeQuery(id+"F2.opExtrude","SWEPT_BODY",BODY,{"disambiguationData":[OSD([sQuery(id+"F1.wireOp",EDGE,"E1.bottom"),sQuery(id+"F1.wireOp",EDGE,"E1.top"),sQuery(id+"F1.wireOp",EDGE,"E1.left"),sQuery(id+"F1.wireOp",EDGE,"E1.right")])]}),"instanceName":"1"}),"instanceName":"1"}),"instanceName":"1"});
            transform(context, id + "F79", {"entities" : qUnion([Q0, Q1, Q2, Q3]), "transformType" : TransformType.TRANSLATION_3D, "dx" : 0 * mm, "dy" : -0.13 * mm, "dz" : 0 * mm, "makeCopy" : false});
        }
        {
            var Q0;
            Q0=makeQuery(id+"F4.opPattern","COPY",BODY,{"derivedFrom":makeQuery(id+"F2.opExtrude","SWEPT_BODY",BODY,{"disambiguationData":[OSD([sQuery(id+"F1.wireOp",EDGE,"E1.bottom"),sQuery(id+"F1.wireOp",EDGE,"E1.top"),sQuery(id+"F1.wireOp",EDGE,"E1.left"),sQuery(id+"F1.wireOp",EDGE,"E1.right")])]}),"instanceName":"1"});
            var Q1;
            Q1=makeQuery(id+"F11.opPattern","COPY",BODY,{"derivedFrom":makeQuery(id+"F2.opExtrude","SWEPT_BODY",BODY,{"disambiguationData":[OSD([sQuery(id+"F1.wireOp",EDGE,"E1.bottom"),sQuery(id+"F1.wireOp",EDGE,"E1.top"),sQuery(id+"F1.wireOp",EDGE,"E1.left"),sQuery(id+"F1.wireOp",EDGE,"E1.right")])]}),"instanceName":"1"});
            var Q2;
            Q2=makeQuery(id+"F11.opPattern","COPY",BODY,{"derivedFrom":makeQuery(id+"F4.opPattern","COPY",BODY,{"derivedFrom":makeQuery(id+"F2.opExtrude","SWEPT_BODY",BODY,{"disambiguationData":[OSD([sQuery(id+"F1.wireOp",EDGE,"E1.bottom"),sQuery(id+"F1.wireOp",EDGE,"E1.top"),sQuery(id+"F1.wireOp",EDGE,"E1.left"),sQuery(id+"F1.wireOp",EDGE,"E1.right")])]}),"instanceName":"1"}),"instanceName":"1"});
            var Q3;
            Q3=makeQuery(id+"F55.opPattern","COPY",BODY,{"derivedFrom":makeQuery(id+"F2.opExtrude","SWEPT_BODY",BODY,{"disambiguationData":[OSD([sQuery(id+"F1.wireOp",EDGE,"E1.bottom"),sQuery(id+"F1.wireOp",EDGE,"E1.top"),sQuery(id+"F1.wireOp",EDGE,"E1.left"),sQuery(id+"F1.wireOp",EDGE,"E1.right")])]}),"instanceName":"1"});
            transform(context, id + "F80", {"entities" : qUnion([Q0, Q1, Q2, Q3]), "transformType" : TransformType.TRANSLATION_3D, "dx" : 0.13 * mm, "dy" : 0 * mm, "dz" : 0 * mm, "makeCopy" : false});
        }
        {
            var Q0;
            Q0=makeQuery(id+"F4.opPattern","COPY",BODY,{"derivedFrom":makeQuery(id+"F2.opExtrude","SWEPT_BODY",BODY,{"disambiguationData":[OSD([sQuery(id+"F1.wireOp",EDGE,"E1.bottom"),sQuery(id+"F1.wireOp",EDGE,"E1.top"),sQuery(id+"F1.wireOp",EDGE,"E1.left"),sQuery(id+"F1.wireOp",EDGE,"E1.right")])]}),"instanceName":"1"});
            var Q1;
            Q1=makeQuery(id+"F11.opPattern","COPY",BODY,{"derivedFrom":makeQuery(id+"F2.opExtrude","SWEPT_BODY",BODY,{"disambiguationData":[OSD([sQuery(id+"F1.wireOp",EDGE,"E1.bottom"),sQuery(id+"F1.wireOp",EDGE,"E1.top"),sQuery(id+"F1.wireOp",EDGE,"E1.left"),sQuery(id+"F1.wireOp",EDGE,"E1.right")])]}),"instanceName":"1"});
            var Q2;
            Q2=makeQuery(id+"F55.opPattern","COPY",BODY,{"derivedFrom":makeQuery(id+"F2.opExtrude","SWEPT_BODY",BODY,{"disambiguationData":[OSD([sQuery(id+"F1.wireOp",EDGE,"E1.bottom"),sQuery(id+"F1.wireOp",EDGE,"E1.top"),sQuery(id+"F1.wireOp",EDGE,"E1.left"),sQuery(id+"F1.wireOp",EDGE,"E1.right")])]}),"instanceName":"1"});
            var Q3;
            Q3=makeQuery(id+"F11.opPattern","COPY",BODY,{"derivedFrom":makeQuery(id+"F4.opPattern","COPY",BODY,{"derivedFrom":makeQuery(id+"F2.opExtrude","SWEPT_BODY",BODY,{"disambiguationData":[OSD([sQuery(id+"F1.wireOp",EDGE,"E1.bottom"),sQuery(id+"F1.wireOp",EDGE,"E1.top"),sQuery(id+"F1.wireOp",EDGE,"E1.left"),sQuery(id+"F1.wireOp",EDGE,"E1.right")])]}),"instanceName":"1"}),"instanceName":"1"});
            transform(context, id + "F81", {"entities" : qUnion([Q0, Q1, Q2, Q3]), "transformType" : TransformType.TRANSLATION_3D, "dx" : 0.25 * mm, "dy" : 0 * mm, "dz" : 0 * mm, "makeCopy" : false});
        }
        {
            var Q0;
            Q0=makeQuery(id+"F4.opPattern","COPY",BODY,{"derivedFrom":makeQuery(id+"F2.opExtrude","SWEPT_BODY",BODY,{"disambiguationData":[OSD([sQuery(id+"F1.wireOp",EDGE,"E1.bottom"),sQuery(id+"F1.wireOp",EDGE,"E1.top"),sQuery(id+"F1.wireOp",EDGE,"E1.left"),sQuery(id+"F1.wireOp",EDGE,"E1.right")])]}),"instanceName":"1"});
            var Q1;
            Q1=makeQuery(id+"F11.opPattern","COPY",BODY,{"derivedFrom":makeQuery(id+"F2.opExtrude","SWEPT_BODY",BODY,{"disambiguationData":[OSD([sQuery(id+"F1.wireOp",EDGE,"E1.bottom"),sQuery(id+"F1.wireOp",EDGE,"E1.top"),sQuery(id+"F1.wireOp",EDGE,"E1.left"),sQuery(id+"F1.wireOp",EDGE,"E1.right")])]}),"instanceName":"1"});
            var Q2;
            Q2=makeQuery(id+"F11.opPattern","COPY",BODY,{"derivedFrom":makeQuery(id+"F4.opPattern","COPY",BODY,{"derivedFrom":makeQuery(id+"F2.opExtrude","SWEPT_BODY",BODY,{"disambiguationData":[OSD([sQuery(id+"F1.wireOp",EDGE,"E1.bottom"),sQuery(id+"F1.wireOp",EDGE,"E1.top"),sQuery(id+"F1.wireOp",EDGE,"E1.left"),sQuery(id+"F1.wireOp",EDGE,"E1.right")])]}),"instanceName":"1"}),"instanceName":"1"});
            var Q3;
            Q3=makeQuery(id+"F55.opPattern","COPY",BODY,{"derivedFrom":makeQuery(id+"F2.opExtrude","SWEPT_BODY",BODY,{"disambiguationData":[OSD([sQuery(id+"F1.wireOp",EDGE,"E1.bottom"),sQuery(id+"F1.wireOp",EDGE,"E1.top"),sQuery(id+"F1.wireOp",EDGE,"E1.left"),sQuery(id+"F1.wireOp",EDGE,"E1.right")])]}),"instanceName":"1"});
            transform(context, id + "F82", {"entities" : qUnion([Q0, Q1, Q2, Q3]), "transformType" : TransformType.TRANSLATION_3D, "dx" : -7.37 * mm, "dy" : 0 * mm, "dz" : 0 * mm, "makeCopy" : true});
        }
        {
            var Q0;
            Q0=makeQuery(id+"F55.opPattern","COPY",BODY,{"derivedFrom":makeQuery(id+"F11.opPattern","COPY",BODY,{"derivedFrom":makeQuery(id+"F4.opPattern","COPY",BODY,{"derivedFrom":makeQuery(id+"F2.opExtrude","SWEPT_BODY",BODY,{"disambiguationData":[OSD([sQuery(id+"F1.wireOp",EDGE,"E1.bottom"),sQuery(id+"F1.wireOp",EDGE,"E1.top"),sQuery(id+"F1.wireOp",EDGE,"E1.left"),sQuery(id+"F1.wireOp",EDGE,"E1.right")])]}),"instanceName":"1"}),"instanceName":"1"}),"instanceName":"1"});
            var Q1;
            Q1=makeQuery(id+"F2.opExtrude","SWEPT_BODY",BODY,{"disambiguationData":[OSD([sQuery(id+"F1.wireOp",EDGE,"E1.bottom"),sQuery(id+"F1.wireOp",EDGE,"E1.top"),sQuery(id+"F1.wireOp",EDGE,"E1.left"),sQuery(id+"F1.wireOp",EDGE,"E1.right")])]});
            var Q2;
            Q2=makeQuery(id+"F55.opPattern","COPY",BODY,{"derivedFrom":makeQuery(id+"F4.opPattern","COPY",BODY,{"derivedFrom":makeQuery(id+"F2.opExtrude","SWEPT_BODY",BODY,{"disambiguationData":[OSD([sQuery(id+"F1.wireOp",EDGE,"E1.bottom"),sQuery(id+"F1.wireOp",EDGE,"E1.top"),sQuery(id+"F1.wireOp",EDGE,"E1.left"),sQuery(id+"F1.wireOp",EDGE,"E1.right")])]}),"instanceName":"1"}),"instanceName":"1"});
            var Q3;
            Q3=makeQuery(id+"F55.opPattern","COPY",BODY,{"derivedFrom":makeQuery(id+"F11.opPattern","COPY",BODY,{"derivedFrom":makeQuery(id+"F2.opExtrude","SWEPT_BODY",BODY,{"disambiguationData":[OSD([sQuery(id+"F1.wireOp",EDGE,"E1.bottom"),sQuery(id+"F1.wireOp",EDGE,"E1.top"),sQuery(id+"F1.wireOp",EDGE,"E1.left"),sQuery(id+"F1.wireOp",EDGE,"E1.right")])]}),"instanceName":"1"}),"instanceName":"1"});
            transform(context, id + "F83", {"entities" : qUnion([Q0, Q1, Q2, Q3]), "transformType" : TransformType.TRANSLATION_3D, "dx" : 0 * mm, "dy" : 6.86 * mm, "dz" : 0 * mm, "makeCopy" : true});
        }
        {
            var Q0;
            Q0=makeQuery(id+"F65.opPattern","COPY",BODY,{"derivedFrom":makeQuery(id+"F4.opPattern","COPY",BODY,{"derivedFrom":makeQuery(id+"F2.opExtrude","SWEPT_BODY",BODY,{"disambiguationData":[OSD([sQuery(id+"F1.wireOp",EDGE,"E1.bottom"),sQuery(id+"F1.wireOp",EDGE,"E1.top"),sQuery(id+"F1.wireOp",EDGE,"E1.left"),sQuery(id+"F1.wireOp",EDGE,"E1.right")])]}),"instanceName":"1"}),"instanceName":"1"});
            var Q1;
            Q1=makeQuery(id+"F65.opPattern","COPY",BODY,{"derivedFrom":makeQuery(id+"F11.opPattern","COPY",BODY,{"derivedFrom":makeQuery(id+"F2.opExtrude","SWEPT_BODY",BODY,{"disambiguationData":[OSD([sQuery(id+"F1.wireOp",EDGE,"E1.bottom"),sQuery(id+"F1.wireOp",EDGE,"E1.top"),sQuery(id+"F1.wireOp",EDGE,"E1.left"),sQuery(id+"F1.wireOp",EDGE,"E1.right")])]}),"instanceName":"1"}),"instanceName":"1"});
            var Q2;
            Q2=makeQuery(id+"F65.opPattern","COPY",BODY,{"derivedFrom":makeQuery(id+"F11.opPattern","COPY",BODY,{"derivedFrom":makeQuery(id+"F4.opPattern","COPY",BODY,{"derivedFrom":makeQuery(id+"F2.opExtrude","SWEPT_BODY",BODY,{"disambiguationData":[OSD([sQuery(id+"F1.wireOp",EDGE,"E1.bottom"),sQuery(id+"F1.wireOp",EDGE,"E1.top"),sQuery(id+"F1.wireOp",EDGE,"E1.left"),sQuery(id+"F1.wireOp",EDGE,"E1.right")])]}),"instanceName":"1"}),"instanceName":"1"}),"instanceName":"1"});
            var Q3;
            Q3=makeQuery(id+"F65.opPattern","COPY",BODY,{"derivedFrom":makeQuery(id+"F55.opPattern","COPY",BODY,{"derivedFrom":makeQuery(id+"F2.opExtrude","SWEPT_BODY",BODY,{"disambiguationData":[OSD([sQuery(id+"F1.wireOp",EDGE,"E1.bottom"),sQuery(id+"F1.wireOp",EDGE,"E1.top"),sQuery(id+"F1.wireOp",EDGE,"E1.left"),sQuery(id+"F1.wireOp",EDGE,"E1.right")])]}),"instanceName":"1"}),"instanceName":"1"});
            transform(context, id + "F84", {"entities" : qUnion([Q0, Q1, Q2, Q3]), "transformType" : TransformType.TRANSLATION_3D, "dx" : 0 * mm, "dy" : -6.86 * mm, "dz" : 0 * mm, "makeCopy" : true});
        }
        {
            var Q0;
            Q0=makeQuery(id+"F69.opPattern","COPY",BODY,{"derivedFrom":makeQuery(id+"F4.opPattern","COPY",BODY,{"derivedFrom":makeQuery(id+"F2.opExtrude","SWEPT_BODY",BODY,{"disambiguationData":[OSD([sQuery(id+"F1.wireOp",EDGE,"E1.bottom"),sQuery(id+"F1.wireOp",EDGE,"E1.top"),sQuery(id+"F1.wireOp",EDGE,"E1.left"),sQuery(id+"F1.wireOp",EDGE,"E1.right")])]}),"instanceName":"1"}),"instanceName":"1"});
            var Q1;
            Q1=makeQuery(id+"F69.opPattern","COPY",BODY,{"derivedFrom":makeQuery(id+"F11.opPattern","COPY",BODY,{"derivedFrom":makeQuery(id+"F2.opExtrude","SWEPT_BODY",BODY,{"disambiguationData":[OSD([sQuery(id+"F1.wireOp",EDGE,"E1.bottom"),sQuery(id+"F1.wireOp",EDGE,"E1.top"),sQuery(id+"F1.wireOp",EDGE,"E1.left"),sQuery(id+"F1.wireOp",EDGE,"E1.right")])]}),"instanceName":"1"}),"instanceName":"1"});
            var Q2;
            Q2=makeQuery(id+"F69.opPattern","COPY",BODY,{"derivedFrom":makeQuery(id+"F11.opPattern","COPY",BODY,{"derivedFrom":makeQuery(id+"F4.opPattern","COPY",BODY,{"derivedFrom":makeQuery(id+"F2.opExtrude","SWEPT_BODY",BODY,{"disambiguationData":[OSD([sQuery(id+"F1.wireOp",EDGE,"E1.bottom"),sQuery(id+"F1.wireOp",EDGE,"E1.top"),sQuery(id+"F1.wireOp",EDGE,"E1.left"),sQuery(id+"F1.wireOp",EDGE,"E1.right")])]}),"instanceName":"1"}),"instanceName":"1"}),"instanceName":"1"});
            var Q3;
            Q3=makeQuery(id+"F69.opPattern","COPY",BODY,{"derivedFrom":makeQuery(id+"F55.opPattern","COPY",BODY,{"derivedFrom":makeQuery(id+"F2.opExtrude","SWEPT_BODY",BODY,{"disambiguationData":[OSD([sQuery(id+"F1.wireOp",EDGE,"E1.bottom"),sQuery(id+"F1.wireOp",EDGE,"E1.top"),sQuery(id+"F1.wireOp",EDGE,"E1.left"),sQuery(id+"F1.wireOp",EDGE,"E1.right")])]}),"instanceName":"1"}),"instanceName":"1"});
            transform(context, id + "F85", {"entities" : qUnion([Q0, Q1, Q2, Q3]), "transformType" : TransformType.TRANSLATION_3D, "dx" : 6.86 * mm, "dy" : 0 * mm, "dz" : 0 * mm, "makeCopy" : true});
        }
        {
            var Q0;
            Q0=makeQuery(id+"F71.opPattern","COPY",BODY,{"derivedFrom":makeQuery(id+"F6.opPattern","COPY",BODY,{"derivedFrom":makeQuery(id+"F2.opExtrude","SWEPT_BODY",BODY,{"disambiguationData":[OSD([sQuery(id+"F1.wireOp",EDGE,"E1.bottom"),sQuery(id+"F1.wireOp",EDGE,"E1.top"),sQuery(id+"F1.wireOp",EDGE,"E1.left"),sQuery(id+"F1.wireOp",EDGE,"E1.right")])]}),"instanceName":"1"}),"instanceName":"1"});
            var Q1;
            Q1=makeQuery(id+"F71.opPattern","COPY",BODY,{"derivedFrom":makeQuery(id+"F6.opPattern","COPY",BODY,{"derivedFrom":makeQuery(id+"F4.opPattern","COPY",BODY,{"derivedFrom":makeQuery(id+"F2.opExtrude","SWEPT_BODY",BODY,{"disambiguationData":[OSD([sQuery(id+"F1.wireOp",EDGE,"E1.bottom"),sQuery(id+"F1.wireOp",EDGE,"E1.top"),sQuery(id+"F1.wireOp",EDGE,"E1.left"),sQuery(id+"F1.wireOp",EDGE,"E1.right")])]}),"instanceName":"1"}),"instanceName":"1"}),"instanceName":"1"});
            var Q2;
            Q2=makeQuery(id+"F71.opPattern","COPY",BODY,{"derivedFrom":makeQuery(id+"F11.opPattern","COPY",BODY,{"derivedFrom":makeQuery(id+"F6.opPattern","COPY",BODY,{"derivedFrom":makeQuery(id+"F4.opPattern","COPY",BODY,{"derivedFrom":makeQuery(id+"F2.opExtrude","SWEPT_BODY",BODY,{"disambiguationData":[OSD([sQuery(id+"F1.wireOp",EDGE,"E1.bottom"),sQuery(id+"F1.wireOp",EDGE,"E1.top"),sQuery(id+"F1.wireOp",EDGE,"E1.left"),sQuery(id+"F1.wireOp",EDGE,"E1.right")])]}),"instanceName":"1"}),"instanceName":"1"}),"instanceName":"1"}),"instanceName":"1"});
            var Q3;
            Q3=makeQuery(id+"F71.opPattern","COPY",BODY,{"derivedFrom":makeQuery(id+"F13.opPattern","COPY",BODY,{"derivedFrom":makeQuery(id+"F11.opPattern","COPY",BODY,{"derivedFrom":makeQuery(id+"F6.opPattern","COPY",BODY,{"derivedFrom":makeQuery(id+"F4.opPattern","COPY",BODY,{"derivedFrom":makeQuery(id+"F2.opExtrude","SWEPT_BODY",BODY,{"disambiguationData":[OSD([sQuery(id+"F1.wireOp",EDGE,"E1.bottom"),sQuery(id+"F1.wireOp",EDGE,"E1.top"),sQuery(id+"F1.wireOp",EDGE,"E1.left"),sQuery(id+"F1.wireOp",EDGE,"E1.right")])]}),"instanceName":"1"}),"instanceName":"1"}),"instanceName":"1"}),"instanceName":"1"}),"instanceName":"1"});
            var Q4;
            Q4=makeQuery(id+"F71.opPattern","COPY",BODY,{"derivedFrom":makeQuery(id+"F55.opPattern","COPY",BODY,{"derivedFrom":makeQuery(id+"F11.opPattern","COPY",BODY,{"derivedFrom":makeQuery(id+"F6.opPattern","COPY",BODY,{"derivedFrom":makeQuery(id+"F2.opExtrude","SWEPT_BODY",BODY,{"disambiguationData":[OSD([sQuery(id+"F1.wireOp",EDGE,"E1.bottom"),sQuery(id+"F1.wireOp",EDGE,"E1.top"),sQuery(id+"F1.wireOp",EDGE,"E1.left"),sQuery(id+"F1.wireOp",EDGE,"E1.right")])]}),"instanceName":"1"}),"instanceName":"1"}),"instanceName":"1"}),"instanceName":"1"});
            transform(context, id + "F86", {"entities" : qUnion([Q0, Q1, Q2, Q3, Q4]), "transformType" : TransformType.TRANSLATION_3D, "dx" : -7.11 * mm, "dy" : 0 * mm, "dz" : 0 * mm, "makeCopy" : true});
        }
        {
            var Q0;
            Q0=makeQuery(id+"F71.opPattern","COPY",BODY,{"derivedFrom":makeQuery(id+"F11.opPattern","COPY",BODY,{"derivedFrom":makeQuery(id+"F6.opPattern","COPY",BODY,{"derivedFrom":makeQuery(id+"F2.opExtrude","SWEPT_BODY",BODY,{"disambiguationData":[OSD([sQuery(id+"F1.wireOp",EDGE,"E1.bottom"),sQuery(id+"F1.wireOp",EDGE,"E1.top"),sQuery(id+"F1.wireOp",EDGE,"E1.left"),sQuery(id+"F1.wireOp",EDGE,"E1.right")])]}),"instanceName":"1"}),"instanceName":"1"}),"instanceName":"1"});
            var Q1;
            Q1=makeQuery(id+"F71.opPattern","COPY",BODY,{"derivedFrom":makeQuery(id+"F55.opPattern","COPY",BODY,{"derivedFrom":makeQuery(id+"F6.opPattern","COPY",BODY,{"derivedFrom":makeQuery(id+"F2.opExtrude","SWEPT_BODY",BODY,{"disambiguationData":[OSD([sQuery(id+"F1.wireOp",EDGE,"E1.bottom"),sQuery(id+"F1.wireOp",EDGE,"E1.top"),sQuery(id+"F1.wireOp",EDGE,"E1.left"),sQuery(id+"F1.wireOp",EDGE,"E1.right")])]}),"instanceName":"1"}),"instanceName":"1"}),"instanceName":"1"});
            var Q2;
            Q2=makeQuery(id+"F71.opPattern","COPY",BODY,{"derivedFrom":makeQuery(id+"F55.opPattern","COPY",BODY,{"derivedFrom":makeQuery(id+"F6.opPattern","COPY",BODY,{"derivedFrom":makeQuery(id+"F4.opPattern","COPY",BODY,{"derivedFrom":makeQuery(id+"F2.opExtrude","SWEPT_BODY",BODY,{"disambiguationData":[OSD([sQuery(id+"F1.wireOp",EDGE,"E1.bottom"),sQuery(id+"F1.wireOp",EDGE,"E1.top"),sQuery(id+"F1.wireOp",EDGE,"E1.left"),sQuery(id+"F1.wireOp",EDGE,"E1.right")])]}),"instanceName":"1"}),"instanceName":"1"}),"instanceName":"1"}),"instanceName":"1"});
            var Q3;
            Q3=makeQuery(id+"F71.opPattern","COPY",BODY,{"derivedFrom":makeQuery(id+"F55.opPattern","COPY",BODY,{"derivedFrom":makeQuery(id+"F11.opPattern","COPY",BODY,{"derivedFrom":makeQuery(id+"F6.opPattern","COPY",BODY,{"derivedFrom":makeQuery(id+"F4.opPattern","COPY",BODY,{"derivedFrom":makeQuery(id+"F2.opExtrude","SWEPT_BODY",BODY,{"disambiguationData":[OSD([sQuery(id+"F1.wireOp",EDGE,"E1.bottom"),sQuery(id+"F1.wireOp",EDGE,"E1.top"),sQuery(id+"F1.wireOp",EDGE,"E1.left"),sQuery(id+"F1.wireOp",EDGE,"E1.right")])]}),"instanceName":"1"}),"instanceName":"1"}),"instanceName":"1"}),"instanceName":"1"}),"instanceName":"1"});
            var Q4;
            Q4=makeQuery(id+"F71.opPattern","COPY",BODY,{"derivedFrom":makeQuery(id+"F55.opPattern","COPY",BODY,{"derivedFrom":makeQuery(id+"F13.opPattern","COPY",BODY,{"derivedFrom":makeQuery(id+"F11.opPattern","COPY",BODY,{"derivedFrom":makeQuery(id+"F6.opPattern","COPY",BODY,{"derivedFrom":makeQuery(id+"F4.opPattern","COPY",BODY,{"derivedFrom":makeQuery(id+"F2.opExtrude","SWEPT_BODY",BODY,{"disambiguationData":[OSD([sQuery(id+"F1.wireOp",EDGE,"E1.bottom"),sQuery(id+"F1.wireOp",EDGE,"E1.top"),sQuery(id+"F1.wireOp",EDGE,"E1.left"),sQuery(id+"F1.wireOp",EDGE,"E1.right")])]}),"instanceName":"1"}),"instanceName":"1"}),"instanceName":"1"}),"instanceName":"1"}),"instanceName":"1"}),"instanceName":"1"});
            transform(context, id + "F87", {"entities" : qUnion([Q0, Q1, Q2, Q3, Q4]), "transformType" : TransformType.TRANSLATION_3D, "dx" : 0 * mm, "dy" : 7.11 * mm, "dz" : 0 * mm, "makeCopy" : true});
        }
        {
            var Q0;
            Q0=makeQuery(id+"F71.opPattern","COPY",BODY,{"derivedFrom":makeQuery(id+"F69.opPattern","COPY",BODY,{"derivedFrom":makeQuery(id+"F6.opPattern","COPY",BODY,{"derivedFrom":makeQuery(id+"F2.opExtrude","SWEPT_BODY",BODY,{"disambiguationData":[OSD([sQuery(id+"F1.wireOp",EDGE,"E1.bottom"),sQuery(id+"F1.wireOp",EDGE,"E1.top"),sQuery(id+"F1.wireOp",EDGE,"E1.left"),sQuery(id+"F1.wireOp",EDGE,"E1.right")])]}),"instanceName":"1"}),"instanceName":"1"}),"instanceName":"1"});
            var Q1;
            Q1=makeQuery(id+"F71.opPattern","COPY",BODY,{"derivedFrom":makeQuery(id+"F69.opPattern","COPY",BODY,{"derivedFrom":makeQuery(id+"F6.opPattern","COPY",BODY,{"derivedFrom":makeQuery(id+"F4.opPattern","COPY",BODY,{"derivedFrom":makeQuery(id+"F2.opExtrude","SWEPT_BODY",BODY,{"disambiguationData":[OSD([sQuery(id+"F1.wireOp",EDGE,"E1.bottom"),sQuery(id+"F1.wireOp",EDGE,"E1.top"),sQuery(id+"F1.wireOp",EDGE,"E1.left"),sQuery(id+"F1.wireOp",EDGE,"E1.right")])]}),"instanceName":"1"}),"instanceName":"1"}),"instanceName":"1"}),"instanceName":"1"});
            var Q2;
            Q2=makeQuery(id+"F71.opPattern","COPY",BODY,{"derivedFrom":makeQuery(id+"F69.opPattern","COPY",BODY,{"derivedFrom":makeQuery(id+"F11.opPattern","COPY",BODY,{"derivedFrom":makeQuery(id+"F6.opPattern","COPY",BODY,{"derivedFrom":makeQuery(id+"F4.opPattern","COPY",BODY,{"derivedFrom":makeQuery(id+"F2.opExtrude","SWEPT_BODY",BODY,{"disambiguationData":[OSD([sQuery(id+"F1.wireOp",EDGE,"E1.bottom"),sQuery(id+"F1.wireOp",EDGE,"E1.top"),sQuery(id+"F1.wireOp",EDGE,"E1.left"),sQuery(id+"F1.wireOp",EDGE,"E1.right")])]}),"instanceName":"1"}),"instanceName":"1"}),"instanceName":"1"}),"instanceName":"1"}),"instanceName":"1"});
            var Q3;
            Q3=makeQuery(id+"F71.opPattern","COPY",BODY,{"derivedFrom":makeQuery(id+"F69.opPattern","COPY",BODY,{"derivedFrom":makeQuery(id+"F13.opPattern","COPY",BODY,{"derivedFrom":makeQuery(id+"F11.opPattern","COPY",BODY,{"derivedFrom":makeQuery(id+"F6.opPattern","COPY",BODY,{"derivedFrom":makeQuery(id+"F4.opPattern","COPY",BODY,{"derivedFrom":makeQuery(id+"F2.opExtrude","SWEPT_BODY",BODY,{"disambiguationData":[OSD([sQuery(id+"F1.wireOp",EDGE,"E1.bottom"),sQuery(id+"F1.wireOp",EDGE,"E1.top"),sQuery(id+"F1.wireOp",EDGE,"E1.left"),sQuery(id+"F1.wireOp",EDGE,"E1.right")])]}),"instanceName":"1"}),"instanceName":"1"}),"instanceName":"1"}),"instanceName":"1"}),"instanceName":"1"}),"instanceName":"1"});
            var Q4;
            Q4=makeQuery(id+"F71.opPattern","COPY",BODY,{"derivedFrom":makeQuery(id+"F69.opPattern","COPY",BODY,{"derivedFrom":makeQuery(id+"F55.opPattern","COPY",BODY,{"derivedFrom":makeQuery(id+"F11.opPattern","COPY",BODY,{"derivedFrom":makeQuery(id+"F6.opPattern","COPY",BODY,{"derivedFrom":makeQuery(id+"F2.opExtrude","SWEPT_BODY",BODY,{"disambiguationData":[OSD([sQuery(id+"F1.wireOp",EDGE,"E1.bottom"),sQuery(id+"F1.wireOp",EDGE,"E1.top"),sQuery(id+"F1.wireOp",EDGE,"E1.left"),sQuery(id+"F1.wireOp",EDGE,"E1.right")])]}),"instanceName":"1"}),"instanceName":"1"}),"instanceName":"1"}),"instanceName":"1"}),"instanceName":"1"});
            transform(context, id + "F88", {"entities" : qUnion([Q0, Q1, Q2, Q3, Q4]), "transformType" : TransformType.TRANSLATION_3D, "dx" : 6.86 * mm, "dy" : 0 * mm, "dz" : 0 * mm, "makeCopy" : true});
        }
        {
            var Q0;
            Q0=makeQuery(id+"F71.opPattern","COPY",BODY,{"derivedFrom":makeQuery(id+"F65.opPattern","COPY",BODY,{"derivedFrom":makeQuery(id+"F6.opPattern","COPY",BODY,{"derivedFrom":makeQuery(id+"F2.opExtrude","SWEPT_BODY",BODY,{"disambiguationData":[OSD([sQuery(id+"F1.wireOp",EDGE,"E1.bottom"),sQuery(id+"F1.wireOp",EDGE,"E1.top"),sQuery(id+"F1.wireOp",EDGE,"E1.left"),sQuery(id+"F1.wireOp",EDGE,"E1.right")])]}),"instanceName":"1"}),"instanceName":"1"}),"instanceName":"1"});
            var Q1;
            Q1=makeQuery(id+"F71.opPattern","COPY",BODY,{"derivedFrom":makeQuery(id+"F65.opPattern","COPY",BODY,{"derivedFrom":makeQuery(id+"F6.opPattern","COPY",BODY,{"derivedFrom":makeQuery(id+"F4.opPattern","COPY",BODY,{"derivedFrom":makeQuery(id+"F2.opExtrude","SWEPT_BODY",BODY,{"disambiguationData":[OSD([sQuery(id+"F1.wireOp",EDGE,"E1.bottom"),sQuery(id+"F1.wireOp",EDGE,"E1.top"),sQuery(id+"F1.wireOp",EDGE,"E1.left"),sQuery(id+"F1.wireOp",EDGE,"E1.right")])]}),"instanceName":"1"}),"instanceName":"1"}),"instanceName":"1"}),"instanceName":"1"});
            var Q2;
            Q2=makeQuery(id+"F71.opPattern","COPY",BODY,{"derivedFrom":makeQuery(id+"F65.opPattern","COPY",BODY,{"derivedFrom":makeQuery(id+"F11.opPattern","COPY",BODY,{"derivedFrom":makeQuery(id+"F6.opPattern","COPY",BODY,{"derivedFrom":makeQuery(id+"F4.opPattern","COPY",BODY,{"derivedFrom":makeQuery(id+"F2.opExtrude","SWEPT_BODY",BODY,{"disambiguationData":[OSD([sQuery(id+"F1.wireOp",EDGE,"E1.bottom"),sQuery(id+"F1.wireOp",EDGE,"E1.top"),sQuery(id+"F1.wireOp",EDGE,"E1.left"),sQuery(id+"F1.wireOp",EDGE,"E1.right")])]}),"instanceName":"1"}),"instanceName":"1"}),"instanceName":"1"}),"instanceName":"1"}),"instanceName":"1"});
            var Q3;
            Q3=makeQuery(id+"F71.opPattern","COPY",BODY,{"derivedFrom":makeQuery(id+"F65.opPattern","COPY",BODY,{"derivedFrom":makeQuery(id+"F13.opPattern","COPY",BODY,{"derivedFrom":makeQuery(id+"F11.opPattern","COPY",BODY,{"derivedFrom":makeQuery(id+"F6.opPattern","COPY",BODY,{"derivedFrom":makeQuery(id+"F4.opPattern","COPY",BODY,{"derivedFrom":makeQuery(id+"F2.opExtrude","SWEPT_BODY",BODY,{"disambiguationData":[OSD([sQuery(id+"F1.wireOp",EDGE,"E1.bottom"),sQuery(id+"F1.wireOp",EDGE,"E1.top"),sQuery(id+"F1.wireOp",EDGE,"E1.left"),sQuery(id+"F1.wireOp",EDGE,"E1.right")])]}),"instanceName":"1"}),"instanceName":"1"}),"instanceName":"1"}),"instanceName":"1"}),"instanceName":"1"}),"instanceName":"1"});
            var Q4;
            Q4=makeQuery(id+"F71.opPattern","COPY",BODY,{"derivedFrom":makeQuery(id+"F65.opPattern","COPY",BODY,{"derivedFrom":makeQuery(id+"F55.opPattern","COPY",BODY,{"derivedFrom":makeQuery(id+"F11.opPattern","COPY",BODY,{"derivedFrom":makeQuery(id+"F6.opPattern","COPY",BODY,{"derivedFrom":makeQuery(id+"F2.opExtrude","SWEPT_BODY",BODY,{"disambiguationData":[OSD([sQuery(id+"F1.wireOp",EDGE,"E1.bottom"),sQuery(id+"F1.wireOp",EDGE,"E1.top"),sQuery(id+"F1.wireOp",EDGE,"E1.left"),sQuery(id+"F1.wireOp",EDGE,"E1.right")])]}),"instanceName":"1"}),"instanceName":"1"}),"instanceName":"1"}),"instanceName":"1"}),"instanceName":"1"});
            transform(context, id + "F89", {"entities" : qUnion([Q0, Q1, Q2, Q3, Q4]), "transformType" : TransformType.TRANSLATION_3D, "dx" : 0 * mm, "dy" : -7.11 * mm, "dz" : 0 * mm, "makeCopy" : true});
        }
        {
            var Q0;
            Q0=makeQuery(id+"F82.opPattern","COPY",BODY,{"derivedFrom":makeQuery(id+"F55.opPattern","COPY",BODY,{"derivedFrom":makeQuery(id+"F2.opExtrude","SWEPT_BODY",BODY,{"disambiguationData":[OSD([sQuery(id+"F1.wireOp",EDGE,"E1.bottom"),sQuery(id+"F1.wireOp",EDGE,"E1.top"),sQuery(id+"F1.wireOp",EDGE,"E1.left"),sQuery(id+"F1.wireOp",EDGE,"E1.right")])]}),"instanceName":"1"}),"instanceName":"1"});
            var Q1;
            Q1=makeQuery(id+"F82.opPattern","COPY",BODY,{"derivedFrom":makeQuery(id+"F11.opPattern","COPY",BODY,{"derivedFrom":makeQuery(id+"F4.opPattern","COPY",BODY,{"derivedFrom":makeQuery(id+"F2.opExtrude","SWEPT_BODY",BODY,{"disambiguationData":[OSD([sQuery(id+"F1.wireOp",EDGE,"E1.bottom"),sQuery(id+"F1.wireOp",EDGE,"E1.top"),sQuery(id+"F1.wireOp",EDGE,"E1.left"),sQuery(id+"F1.wireOp",EDGE,"E1.right")])]}),"instanceName":"1"}),"instanceName":"1"}),"instanceName":"1"});
            var Q2;
            Q2=makeQuery(id+"F82.opPattern","COPY",BODY,{"derivedFrom":makeQuery(id+"F11.opPattern","COPY",BODY,{"derivedFrom":makeQuery(id+"F2.opExtrude","SWEPT_BODY",BODY,{"disambiguationData":[OSD([sQuery(id+"F1.wireOp",EDGE,"E1.bottom"),sQuery(id+"F1.wireOp",EDGE,"E1.top"),sQuery(id+"F1.wireOp",EDGE,"E1.left"),sQuery(id+"F1.wireOp",EDGE,"E1.right")])]}),"instanceName":"1"}),"instanceName":"1"});
            var Q3;
            Q3=makeQuery(id+"F82.opPattern","COPY",BODY,{"derivedFrom":makeQuery(id+"F4.opPattern","COPY",BODY,{"derivedFrom":makeQuery(id+"F2.opExtrude","SWEPT_BODY",BODY,{"disambiguationData":[OSD([sQuery(id+"F1.wireOp",EDGE,"E1.bottom"),sQuery(id+"F1.wireOp",EDGE,"E1.top"),sQuery(id+"F1.wireOp",EDGE,"E1.left"),sQuery(id+"F1.wireOp",EDGE,"E1.right")])]}),"instanceName":"1"}),"instanceName":"1"});
            transform(context, id + "F90", {"entities" : qUnion([Q0, Q1, Q2, Q3]), "transformType" : TransformType.TRANSLATION_3D, "dx" : 0.33 * mm, "dy" : 0 * mm, "dz" : 0 * mm, "makeCopy" : false});
        }
    });
